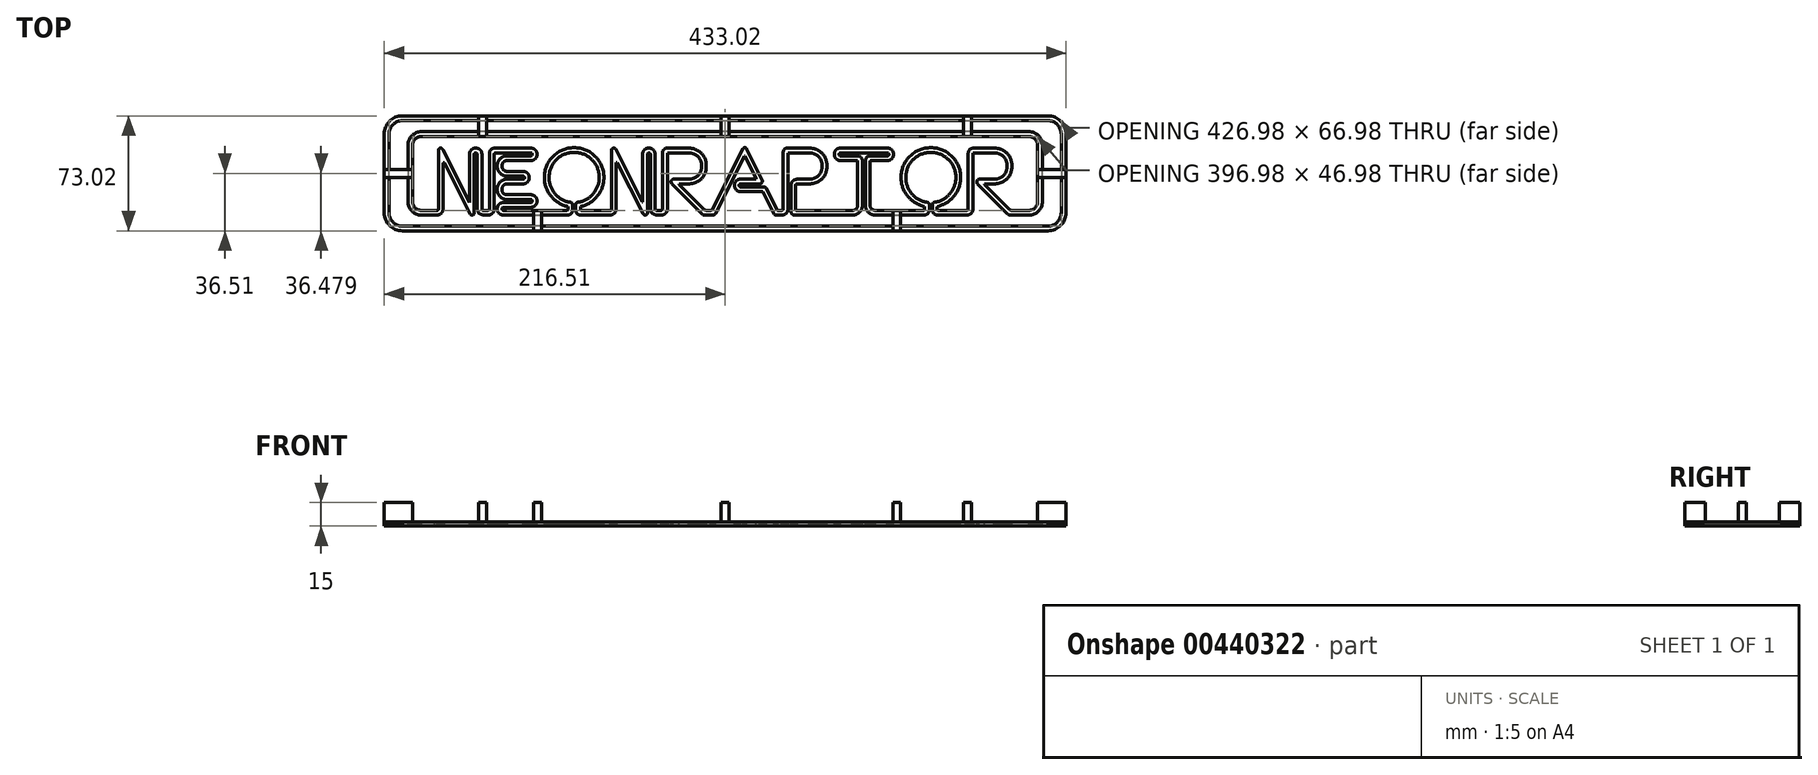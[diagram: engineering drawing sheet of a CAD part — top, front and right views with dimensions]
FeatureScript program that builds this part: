
annotation { "Feature Type Name" : "Feature", "Feature Type Description" : "" }
export const myFeature = defineFeature(function(context is Context, id is Id, definition is map)
    precondition{}
    {
        {
            var Q0;
            Q0=qCreatedBy(makeId("Top.planeOp"),FACE);
            var Q1;
            Q1=qCreatedBy(makeId("Top.planeOp"),FACE);
            var sketch = newSketch(context, id + "F0", { "sketchPlane" : qUnion([Q0, Q1])});
            skLineSegment(sketch, "E0", {"start": v(205, 36.51) * mm, "end": v(-205, 36.51) * mm});
            skLineSegment(sketch, "E1", {"start": v(-205, 36.51) * mm, "end": v(-206.18, 36.45) * mm});
            skLineSegment(sketch, "E2", {"start": v(-206.18, 36.45) * mm, "end": v(-207.32, 36.28) * mm});
            skLineSegment(sketch, "E3", {"start": v(-207.32, 36.28) * mm, "end": v(-208.42, 36) * mm});
            skLineSegment(sketch, "E4", {"start": v(-208.42, 36) * mm, "end": v(-209.48, 35.6) * mm});
            skLineSegment(sketch, "E5", {"start": v(-209.48, 35.6) * mm, "end": v(-210.48, 35.12) * mm});
            skLineSegment(sketch, "E6", {"start": v(-210.48, 35.12) * mm, "end": v(-211.43, 34.54) * mm});
            skLineSegment(sketch, "E7", {"start": v(-211.43, 34.54) * mm, "end": v(-212.32, 33.88) * mm});
            skLineSegment(sketch, "E8", {"start": v(-212.32, 33.88) * mm, "end": v(-213.14, 33.14) * mm});
            skLineSegment(sketch, "E9", {"start": v(-213.14, 33.14) * mm, "end": v(-213.88, 32.32) * mm});
            skLineSegment(sketch, "E10", {"start": v(-213.88, 32.32) * mm, "end": v(-214.54, 31.43) * mm});
            skLineSegment(sketch, "E11", {"start": v(-214.54, 31.43) * mm, "end": v(-215.12, 30.48) * mm});
            skLineSegment(sketch, "E12", {"start": v(-215.12, 30.48) * mm, "end": v(-215.6, 29.48) * mm});
            skLineSegment(sketch, "E13", {"start": v(-215.6, 29.48) * mm, "end": v(-216, 28.42) * mm});
            skLineSegment(sketch, "E14", {"start": v(-216, 28.42) * mm, "end": v(-216.28, 27.32) * mm});
            skLineSegment(sketch, "E15", {"start": v(-216.28, 27.32) * mm, "end": v(-216.45, 26.18) * mm});
            skLineSegment(sketch, "E16", {"start": v(-216.45, 26.18) * mm, "end": v(-216.51, 25) * mm});
            skLineSegment(sketch, "E17", {"start": v(-216.51, 25) * mm, "end": v(-216.51, -25) * mm});
            skLineSegment(sketch, "E18", {"start": v(-216.51, -25) * mm, "end": v(-216.45, -26.18) * mm});
            skLineSegment(sketch, "E19", {"start": v(-216.45, -26.18) * mm, "end": v(-216.28, -27.32) * mm});
            skLineSegment(sketch, "E20", {"start": v(-216.28, -27.32) * mm, "end": v(-216, -28.42) * mm});
            skLineSegment(sketch, "E21", {"start": v(-216, -28.42) * mm, "end": v(-215.6, -29.48) * mm});
            skLineSegment(sketch, "E22", {"start": v(-215.6, -29.48) * mm, "end": v(-215.12, -30.48) * mm});
            skLineSegment(sketch, "E23", {"start": v(-215.12, -30.48) * mm, "end": v(-214.54, -31.43) * mm});
            skLineSegment(sketch, "E24", {"start": v(-214.54, -31.43) * mm, "end": v(-213.88, -32.32) * mm});
            skLineSegment(sketch, "E25", {"start": v(-213.88, -32.32) * mm, "end": v(-213.14, -33.14) * mm});
            skLineSegment(sketch, "E26", {"start": v(-213.14, -33.14) * mm, "end": v(-212.32, -33.88) * mm});
            skLineSegment(sketch, "E27", {"start": v(-212.32, -33.88) * mm, "end": v(-211.43, -34.54) * mm});
            skLineSegment(sketch, "E28", {"start": v(-211.43, -34.54) * mm, "end": v(-210.48, -35.12) * mm});
            skLineSegment(sketch, "E29", {"start": v(-210.48, -35.12) * mm, "end": v(-209.48, -35.6) * mm});
            skLineSegment(sketch, "E30", {"start": v(-209.48, -35.6) * mm, "end": v(-208.42, -36) * mm});
            skLineSegment(sketch, "E31", {"start": v(-208.42, -36) * mm, "end": v(-207.32, -36.28) * mm});
            skLineSegment(sketch, "E32", {"start": v(-207.32, -36.28) * mm, "end": v(-206.18, -36.45) * mm});
            skLineSegment(sketch, "E33", {"start": v(-206.18, -36.45) * mm, "end": v(-205, -36.51) * mm});
            skLineSegment(sketch, "E34", {"start": v(-205, -36.51) * mm, "end": v(205, -36.51) * mm});
            skLineSegment(sketch, "E35", {"start": v(205, -36.51) * mm, "end": v(206.18, -36.45) * mm});
            skLineSegment(sketch, "E36", {"start": v(206.18, -36.45) * mm, "end": v(207.32, -36.28) * mm});
            skLineSegment(sketch, "E37", {"start": v(207.32, -36.28) * mm, "end": v(208.42, -36) * mm});
            skLineSegment(sketch, "E38", {"start": v(208.42, -36) * mm, "end": v(209.48, -35.6) * mm});
            skLineSegment(sketch, "E39", {"start": v(209.48, -35.6) * mm, "end": v(210.48, -35.12) * mm});
            skLineSegment(sketch, "E40", {"start": v(210.48, -35.12) * mm, "end": v(211.43, -34.54) * mm});
            skLineSegment(sketch, "E41", {"start": v(211.43, -34.54) * mm, "end": v(212.32, -33.88) * mm});
            skLineSegment(sketch, "E42", {"start": v(212.32, -33.88) * mm, "end": v(213.14, -33.14) * mm});
            skLineSegment(sketch, "E43", {"start": v(213.14, -33.14) * mm, "end": v(213.88, -32.32) * mm});
            skLineSegment(sketch, "E44", {"start": v(213.88, -32.32) * mm, "end": v(214.54, -31.43) * mm});
            skLineSegment(sketch, "E45", {"start": v(214.54, -31.43) * mm, "end": v(215.12, -30.48) * mm});
            skLineSegment(sketch, "E46", {"start": v(215.12, -30.48) * mm, "end": v(215.6, -29.48) * mm});
            skLineSegment(sketch, "E47", {"start": v(215.6, -29.48) * mm, "end": v(216, -28.42) * mm});
            skLineSegment(sketch, "E48", {"start": v(216, -28.42) * mm, "end": v(216.28, -27.32) * mm});
            skLineSegment(sketch, "E49", {"start": v(216.28, -27.32) * mm, "end": v(216.45, -26.18) * mm});
            skLineSegment(sketch, "E50", {"start": v(216.45, -26.18) * mm, "end": v(216.51, -25) * mm});
            skLineSegment(sketch, "E51", {"start": v(216.51, -25) * mm, "end": v(216.51, 25) * mm});
            skLineSegment(sketch, "E52", {"start": v(216.51, 25) * mm, "end": v(216.45, 26.18) * mm});
            skLineSegment(sketch, "E53", {"start": v(216.45, 26.18) * mm, "end": v(216.28, 27.32) * mm});
            skLineSegment(sketch, "E54", {"start": v(216.28, 27.32) * mm, "end": v(216, 28.42) * mm});
            skLineSegment(sketch, "E55", {"start": v(216, 28.42) * mm, "end": v(215.6, 29.48) * mm});
            skLineSegment(sketch, "E56", {"start": v(215.6, 29.48) * mm, "end": v(215.12, 30.48) * mm});
            skLineSegment(sketch, "E57", {"start": v(215.12, 30.48) * mm, "end": v(214.54, 31.43) * mm});
            skLineSegment(sketch, "E58", {"start": v(214.54, 31.43) * mm, "end": v(213.88, 32.32) * mm});
            skLineSegment(sketch, "E59", {"start": v(213.88, 32.32) * mm, "end": v(213.14, 33.14) * mm});
            skLineSegment(sketch, "E60", {"start": v(213.14, 33.14) * mm, "end": v(212.32, 33.88) * mm});
            skLineSegment(sketch, "E61", {"start": v(212.32, 33.88) * mm, "end": v(211.43, 34.54) * mm});
            skLineSegment(sketch, "E62", {"start": v(211.43, 34.54) * mm, "end": v(210.48, 35.12) * mm});
            skLineSegment(sketch, "E63", {"start": v(210.48, 35.12) * mm, "end": v(209.48, 35.6) * mm});
            skLineSegment(sketch, "E64", {"start": v(209.48, 35.6) * mm, "end": v(208.42, 36) * mm});
            skLineSegment(sketch, "E65", {"start": v(208.42, 36) * mm, "end": v(207.32, 36.28) * mm});
            skLineSegment(sketch, "E66", {"start": v(207.32, 36.28) * mm, "end": v(206.18, 36.45) * mm});
            skLineSegment(sketch, "E67", {"start": v(206.18, 36.45) * mm, "end": v(205, 36.51) * mm});
            skLineSegment(sketch, "E68", {"start": v(213.49, -25) * mm, "end": v(213.45, -25.87) * mm});
            skLineSegment(sketch, "E69", {"start": v(213.45, -25.87) * mm, "end": v(213.32, -26.7) * mm});
            skLineSegment(sketch, "E70", {"start": v(213.32, -26.7) * mm, "end": v(213.1, -27.52) * mm});
            skLineSegment(sketch, "E71", {"start": v(213.1, -27.52) * mm, "end": v(212.82, -28.3) * mm});
            skLineSegment(sketch, "E72", {"start": v(212.82, -28.3) * mm, "end": v(212.46, -29.04) * mm});
            skLineSegment(sketch, "E73", {"start": v(212.46, -29.04) * mm, "end": v(212.04, -29.74) * mm});
            skLineSegment(sketch, "E74", {"start": v(212.04, -29.74) * mm, "end": v(211.55, -30.4) * mm});
            skLineSegment(sketch, "E75", {"start": v(211.55, -30.4) * mm, "end": v(211, -31) * mm});
            skLineSegment(sketch, "E76", {"start": v(211, -31) * mm, "end": v(210.4, -31.55) * mm});
            skLineSegment(sketch, "E77", {"start": v(210.4, -31.55) * mm, "end": v(209.74, -32.04) * mm});
            skLineSegment(sketch, "E78", {"start": v(209.74, -32.04) * mm, "end": v(209.04, -32.46) * mm});
            skLineSegment(sketch, "E79", {"start": v(209.04, -32.46) * mm, "end": v(208.3, -32.82) * mm});
            skLineSegment(sketch, "E80", {"start": v(208.3, -32.82) * mm, "end": v(207.52, -33.1) * mm});
            skLineSegment(sketch, "E81", {"start": v(207.52, -33.1) * mm, "end": v(206.7, -33.32) * mm});
            skLineSegment(sketch, "E82", {"start": v(206.7, -33.32) * mm, "end": v(205.87, -33.45) * mm});
            skLineSegment(sketch, "E83", {"start": v(205.87, -33.45) * mm, "end": v(205, -33.49) * mm});
            skLineSegment(sketch, "E84", {"start": v(205, -33.49) * mm, "end": v(-205, -33.49) * mm});
            skLineSegment(sketch, "E85", {"start": v(-205, -33.49) * mm, "end": v(-205.87, -33.45) * mm});
            skLineSegment(sketch, "E86", {"start": v(-205.87, -33.45) * mm, "end": v(-206.7, -33.32) * mm});
            skLineSegment(sketch, "E87", {"start": v(-206.7, -33.32) * mm, "end": v(-207.52, -33.1) * mm});
            skLineSegment(sketch, "E88", {"start": v(-207.52, -33.1) * mm, "end": v(-208.3, -32.82) * mm});
            skLineSegment(sketch, "E89", {"start": v(-208.3, -32.82) * mm, "end": v(-209.04, -32.46) * mm});
            skLineSegment(sketch, "E90", {"start": v(-209.04, -32.46) * mm, "end": v(-209.74, -32.04) * mm});
            skLineSegment(sketch, "E91", {"start": v(-209.74, -32.04) * mm, "end": v(-210.4, -31.55) * mm});
            skLineSegment(sketch, "E92", {"start": v(-210.4, -31.55) * mm, "end": v(-211, -31) * mm});
            skLineSegment(sketch, "E93", {"start": v(-211, -31) * mm, "end": v(-211.55, -30.4) * mm});
            skLineSegment(sketch, "E94", {"start": v(-211.55, -30.4) * mm, "end": v(-212.04, -29.74) * mm});
            skLineSegment(sketch, "E95", {"start": v(-212.04, -29.74) * mm, "end": v(-212.46, -29.04) * mm});
            skLineSegment(sketch, "E96", {"start": v(-212.46, -29.04) * mm, "end": v(-212.82, -28.3) * mm});
            skLineSegment(sketch, "E97", {"start": v(-212.82, -28.3) * mm, "end": v(-213.1, -27.52) * mm});
            skLineSegment(sketch, "E98", {"start": v(-213.1, -27.52) * mm, "end": v(-213.32, -26.7) * mm});
            skLineSegment(sketch, "E99", {"start": v(-213.32, -26.7) * mm, "end": v(-213.44, -25.87) * mm});
            skLineSegment(sketch, "E100", {"start": v(-213.44, -25.87) * mm, "end": v(-213.49, -25) * mm});
            skLineSegment(sketch, "E101", {"start": v(-213.49, -25) * mm, "end": v(-213.49, 25) * mm});
            skLineSegment(sketch, "E102", {"start": v(-213.49, 25) * mm, "end": v(-213.44, 25.87) * mm});
            skLineSegment(sketch, "E103", {"start": v(-213.44, 25.87) * mm, "end": v(-213.32, 26.7) * mm});
            skLineSegment(sketch, "E104", {"start": v(-213.32, 26.7) * mm, "end": v(-213.1, 27.52) * mm});
            skLineSegment(sketch, "E105", {"start": v(-213.1, 27.52) * mm, "end": v(-212.82, 28.3) * mm});
            skLineSegment(sketch, "E106", {"start": v(-212.82, 28.3) * mm, "end": v(-212.46, 29.04) * mm});
            skLineSegment(sketch, "E107", {"start": v(-212.46, 29.04) * mm, "end": v(-212.04, 29.74) * mm});
            skLineSegment(sketch, "E108", {"start": v(-212.04, 29.74) * mm, "end": v(-211.55, 30.4) * mm});
            skLineSegment(sketch, "E109", {"start": v(-211.55, 30.4) * mm, "end": v(-211, 31) * mm});
            skLineSegment(sketch, "E110", {"start": v(-211, 31) * mm, "end": v(-210.4, 31.55) * mm});
            skLineSegment(sketch, "E111", {"start": v(-210.4, 31.55) * mm, "end": v(-209.74, 32.04) * mm});
            skLineSegment(sketch, "E112", {"start": v(-209.74, 32.04) * mm, "end": v(-209.04, 32.46) * mm});
            skLineSegment(sketch, "E113", {"start": v(-209.04, 32.46) * mm, "end": v(-208.3, 32.82) * mm});
            skLineSegment(sketch, "E114", {"start": v(-208.3, 32.82) * mm, "end": v(-207.52, 33.1) * mm});
            skLineSegment(sketch, "E115", {"start": v(-207.52, 33.1) * mm, "end": v(-206.7, 33.32) * mm});
            skLineSegment(sketch, "E116", {"start": v(-206.7, 33.32) * mm, "end": v(-205.87, 33.44) * mm});
            skLineSegment(sketch, "E117", {"start": v(-205.87, 33.44) * mm, "end": v(-205, 33.49) * mm});
            skLineSegment(sketch, "E118", {"start": v(-205, 33.49) * mm, "end": v(205, 33.49) * mm});
            skLineSegment(sketch, "E119", {"start": v(205, 33.49) * mm, "end": v(205.87, 33.44) * mm});
            skLineSegment(sketch, "E120", {"start": v(205.87, 33.44) * mm, "end": v(206.7, 33.32) * mm});
            skLineSegment(sketch, "E121", {"start": v(206.7, 33.32) * mm, "end": v(207.52, 33.1) * mm});
            skLineSegment(sketch, "E122", {"start": v(207.52, 33.1) * mm, "end": v(208.3, 32.82) * mm});
            skLineSegment(sketch, "E123", {"start": v(208.3, 32.82) * mm, "end": v(209.04, 32.46) * mm});
            skLineSegment(sketch, "E124", {"start": v(209.04, 32.46) * mm, "end": v(209.74, 32.04) * mm});
            skLineSegment(sketch, "E125", {"start": v(209.74, 32.04) * mm, "end": v(210.4, 31.55) * mm});
            skLineSegment(sketch, "E126", {"start": v(210.4, 31.55) * mm, "end": v(211, 31) * mm});
            skLineSegment(sketch, "E127", {"start": v(211, 31) * mm, "end": v(211.55, 30.4) * mm});
            skLineSegment(sketch, "E128", {"start": v(211.55, 30.4) * mm, "end": v(212.04, 29.74) * mm});
            skLineSegment(sketch, "E129", {"start": v(212.04, 29.74) * mm, "end": v(212.46, 29.04) * mm});
            skLineSegment(sketch, "E130", {"start": v(212.46, 29.04) * mm, "end": v(212.82, 28.3) * mm});
            skLineSegment(sketch, "E131", {"start": v(212.82, 28.3) * mm, "end": v(213.1, 27.52) * mm});
            skLineSegment(sketch, "E132", {"start": v(213.1, 27.52) * mm, "end": v(213.32, 26.7) * mm});
            skLineSegment(sketch, "E133", {"start": v(213.32, 26.7) * mm, "end": v(213.45, 25.87) * mm});
            skLineSegment(sketch, "E134", {"start": v(213.45, 25.87) * mm, "end": v(213.49, 25) * mm});
            skLineSegment(sketch, "E135", {"start": v(213.49, 25) * mm, "end": v(213.49, -25) * mm});
            skLineSegment(sketch, "E136", {"start": v(192.86, 26.48) * mm, "end": v(-192.86, 26.48) * mm});
            skLineSegment(sketch, "E137", {"start": v(-192.86, 26.48) * mm, "end": v(-193.74, 26.44) * mm});
            skLineSegment(sketch, "E138", {"start": v(-193.74, 26.44) * mm, "end": v(-194.6, 26.3) * mm});
            skLineSegment(sketch, "E139", {"start": v(-194.6, 26.3) * mm, "end": v(-195.43, 26.1) * mm});
            skLineSegment(sketch, "E140", {"start": v(-195.43, 26.1) * mm, "end": v(-196.22, 25.8) * mm});
            skLineSegment(sketch, "E141", {"start": v(-196.22, 25.8) * mm, "end": v(-196.98, 25.43) * mm});
            skLineSegment(sketch, "E142", {"start": v(-196.98, 25.43) * mm, "end": v(-197.7, 25) * mm});
            skLineSegment(sketch, "E143", {"start": v(-197.7, 25) * mm, "end": v(-198.36, 24.5) * mm});
            skLineSegment(sketch, "E144", {"start": v(-198.36, 24.5) * mm, "end": v(-198.97, 23.94) * mm});
            skLineSegment(sketch, "E145", {"start": v(-198.97, 23.94) * mm, "end": v(-199.53, 23.33) * mm});
            skLineSegment(sketch, "E146", {"start": v(-199.53, 23.33) * mm, "end": v(-200.03, 22.66) * mm});
            skLineSegment(sketch, "E147", {"start": v(-200.03, 22.66) * mm, "end": v(-200.46, 21.95) * mm});
            skLineSegment(sketch, "E148", {"start": v(-200.46, 21.95) * mm, "end": v(-200.83, 21.2) * mm});
            skLineSegment(sketch, "E149", {"start": v(-200.83, 21.2) * mm, "end": v(-201.12, 20.4) * mm});
            skLineSegment(sketch, "E150", {"start": v(-201.12, 20.4) * mm, "end": v(-201.33, 19.57) * mm});
            skLineSegment(sketch, "E151", {"start": v(-201.33, 19.57) * mm, "end": v(-201.47, 18.7) * mm});
            skLineSegment(sketch, "E152", {"start": v(-201.47, 18.7) * mm, "end": v(-201.51, 17.82) * mm});
            skLineSegment(sketch, "E153", {"start": v(-201.51, 17.82) * mm, "end": v(-201.51, -17.89) * mm});
            skLineSegment(sketch, "E154", {"start": v(-201.51, -17.89) * mm, "end": v(-201.47, -18.77) * mm});
            skLineSegment(sketch, "E155", {"start": v(-201.47, -18.77) * mm, "end": v(-201.33, -19.63) * mm});
            skLineSegment(sketch, "E156", {"start": v(-201.33, -19.63) * mm, "end": v(-201.12, -20.46) * mm});
            skLineSegment(sketch, "E157", {"start": v(-201.12, -20.46) * mm, "end": v(-200.83, -21.25) * mm});
            skLineSegment(sketch, "E158", {"start": v(-200.83, -21.25) * mm, "end": v(-200.46, -22) * mm});
            skLineSegment(sketch, "E159", {"start": v(-200.46, -22) * mm, "end": v(-200.03, -22.72) * mm});
            skLineSegment(sketch, "E160", {"start": v(-200.03, -22.72) * mm, "end": v(-199.53, -23.39) * mm});
            skLineSegment(sketch, "E161", {"start": v(-199.53, -23.39) * mm, "end": v(-198.97, -24) * mm});
            skLineSegment(sketch, "E162", {"start": v(-198.97, -24) * mm, "end": v(-198.36, -24.56) * mm});
            skLineSegment(sketch, "E163", {"start": v(-198.36, -24.56) * mm, "end": v(-197.7, -25.06) * mm});
            skLineSegment(sketch, "E164", {"start": v(-197.7, -25.06) * mm, "end": v(-196.98, -25.5) * mm});
            skLineSegment(sketch, "E165", {"start": v(-196.98, -25.5) * mm, "end": v(-196.22, -25.86) * mm});
            skLineSegment(sketch, "E166", {"start": v(-196.22, -25.86) * mm, "end": v(-195.43, -26.15) * mm});
            skLineSegment(sketch, "E167", {"start": v(-195.43, -26.15) * mm, "end": v(-194.6, -26.37) * mm});
            skLineSegment(sketch, "E168", {"start": v(-194.6, -26.37) * mm, "end": v(-193.74, -26.5) * mm});
            skLineSegment(sketch, "E169", {"start": v(-193.74, -26.5) * mm, "end": v(-192.86, -26.54) * mm});
            skLineSegment(sketch, "E170", {"start": v(-192.86, -26.54) * mm, "end": v(-184.5, -26.54) * mm});
            skLineSegment(sketch, "E171", {"start": v(-184.5, -26.54) * mm, "end": v(-184.4, -26.44) * mm});
            skLineSegment(sketch, "E172", {"start": v(-184.4, -26.44) * mm, "end": v(-184.4, -26.44) * mm});
            skLineSegment(sketch, "E173", {"start": v(-184.4, -26.44) * mm, "end": v(-183.06, -26.44) * mm});
            skLineSegment(sketch, "E174", {"start": v(-183.06, -26.44) * mm, "end": v(-182.85, -26.43) * mm});
            skLineSegment(sketch, "E175", {"start": v(-182.85, -26.43) * mm, "end": v(-182.64, -26.42) * mm});
            skLineSegment(sketch, "E176", {"start": v(-182.64, -26.42) * mm, "end": v(-182.44, -26.4) * mm});
            skLineSegment(sketch, "E177", {"start": v(-182.44, -26.4) * mm, "end": v(-182.24, -26.37) * mm});
            skLineSegment(sketch, "E178", {"start": v(-182.24, -26.37) * mm, "end": v(-182.04, -26.33) * mm});
            skLineSegment(sketch, "E179", {"start": v(-182.04, -26.33) * mm, "end": v(-181.85, -26.28) * mm});
            skLineSegment(sketch, "E180", {"start": v(-181.85, -26.28) * mm, "end": v(-181.67, -26.22) * mm});
            skLineSegment(sketch, "E181", {"start": v(-181.67, -26.22) * mm, "end": v(-181.5, -26.16) * mm});
            skLineSegment(sketch, "E182", {"start": v(-181.5, -26.16) * mm, "end": v(-181.32, -26.08) * mm});
            skLineSegment(sketch, "E183", {"start": v(-181.32, -26.08) * mm, "end": v(-181.15, -26) * mm});
            skLineSegment(sketch, "E184", {"start": v(-181.15, -26) * mm, "end": v(-180.98, -25.9) * mm});
            skLineSegment(sketch, "E185", {"start": v(-180.98, -25.9) * mm, "end": v(-180.82, -25.8) * mm});
            skLineSegment(sketch, "E186", {"start": v(-180.82, -25.8) * mm, "end": v(-180.67, -25.7) * mm});
            skLineSegment(sketch, "E187", {"start": v(-180.67, -25.7) * mm, "end": v(-180.52, -25.58) * mm});
            skLineSegment(sketch, "E188", {"start": v(-180.52, -25.58) * mm, "end": v(-180.38, -25.46) * mm});
            skLineSegment(sketch, "E189", {"start": v(-180.38, -25.46) * mm, "end": v(-180.24, -25.32) * mm});
            skLineSegment(sketch, "E190", {"start": v(-180.24, -25.32) * mm, "end": v(-180.1, -25.18) * mm});
            skLineSegment(sketch, "E191", {"start": v(-180.1, -25.18) * mm, "end": v(-179.99, -25.03) * mm});
            skLineSegment(sketch, "E192", {"start": v(-179.99, -25.03) * mm, "end": v(-179.87, -24.88) * mm});
            skLineSegment(sketch, "E193", {"start": v(-179.87, -24.88) * mm, "end": v(-179.77, -24.73) * mm});
            skLineSegment(sketch, "E194", {"start": v(-179.77, -24.73) * mm, "end": v(-179.67, -24.56) * mm});
            skLineSegment(sketch, "E195", {"start": v(-179.67, -24.56) * mm, "end": v(-179.58, -24.4) * mm});
            skLineSegment(sketch, "E196", {"start": v(-179.58, -24.4) * mm, "end": v(-179.5, -24.23) * mm});
            skLineSegment(sketch, "E197", {"start": v(-179.5, -24.23) * mm, "end": v(-179.43, -24.05) * mm});
            skLineSegment(sketch, "E198", {"start": v(-179.43, -24.05) * mm, "end": v(-179.36, -23.87) * mm});
            skLineSegment(sketch, "E199", {"start": v(-179.36, -23.87) * mm, "end": v(-179.3, -23.68) * mm});
            skLineSegment(sketch, "E200", {"start": v(-179.3, -23.68) * mm, "end": v(-179.26, -23.5) * mm});
            skLineSegment(sketch, "E201", {"start": v(-179.26, -23.5) * mm, "end": v(-179.22, -23.3) * mm});
            skLineSegment(sketch, "E202", {"start": v(-179.22, -23.3) * mm, "end": v(-179.2, -23.1) * mm});
            skLineSegment(sketch, "E203", {"start": v(-179.2, -23.1) * mm, "end": v(-179.17, -22.9) * mm});
            skLineSegment(sketch, "E204", {"start": v(-179.17, -22.9) * mm, "end": v(-179.16, -22.69) * mm});
            skLineSegment(sketch, "E205", {"start": v(-179.16, -22.69) * mm, "end": v(-179.15, -22.47) * mm});
            skLineSegment(sketch, "E206", {"start": v(-179.15, -22.47) * mm, "end": v(-179.15, 6.31) * mm});
            skLineSegment(sketch, "E207", {"start": v(-179.15, 6.31) * mm, "end": v(-179.15, 6.36) * mm});
            skLineSegment(sketch, "E208", {"start": v(-179.15, 6.36) * mm, "end": v(-179.14, 6.41) * mm});
            skLineSegment(sketch, "E209", {"start": v(-179.14, 6.41) * mm, "end": v(-179.13, 6.46) * mm});
            skLineSegment(sketch, "E210", {"start": v(-179.13, 6.46) * mm, "end": v(-179.11, 6.5) * mm});
            skLineSegment(sketch, "E211", {"start": v(-179.11, 6.5) * mm, "end": v(-179.1, 6.54) * mm});
            skLineSegment(sketch, "E212", {"start": v(-179.1, 6.54) * mm, "end": v(-179.07, 6.58) * mm});
            skLineSegment(sketch, "E213", {"start": v(-179.07, 6.58) * mm, "end": v(-179.04, 6.6) * mm});
            skLineSegment(sketch, "E214", {"start": v(-179.04, 6.6) * mm, "end": v(-179.01, 6.64) * mm});
            skLineSegment(sketch, "E215", {"start": v(-179.01, 6.64) * mm, "end": v(-178.98, 6.67) * mm});
            skLineSegment(sketch, "E216", {"start": v(-178.98, 6.67) * mm, "end": v(-178.94, 6.69) * mm});
            skLineSegment(sketch, "E217", {"start": v(-178.94, 6.69) * mm, "end": v(-178.9, 6.7) * mm});
            skLineSegment(sketch, "E218", {"start": v(-178.9, 6.7) * mm, "end": v(-178.87, 6.72) * mm});
            skLineSegment(sketch, "E219", {"start": v(-178.87, 6.72) * mm, "end": v(-178.83, 6.74) * mm});
            skLineSegment(sketch, "E220", {"start": v(-178.83, 6.74) * mm, "end": v(-178.79, 6.75) * mm});
            skLineSegment(sketch, "E221", {"start": v(-178.79, 6.75) * mm, "end": v(-178.75, 6.75) * mm});
            skLineSegment(sketch, "E222", {"start": v(-178.75, 6.75) * mm, "end": v(-178.7, 6.75) * mm});
            skLineSegment(sketch, "E223", {"start": v(-178.7, 6.75) * mm, "end": v(-178.67, 6.75) * mm});
            skLineSegment(sketch, "E224", {"start": v(-178.67, 6.75) * mm, "end": v(-178.64, 6.75) * mm});
            skLineSegment(sketch, "E225", {"start": v(-178.64, 6.75) * mm, "end": v(-178.61, 6.74) * mm});
            skLineSegment(sketch, "E226", {"start": v(-178.61, 6.74) * mm, "end": v(-178.58, 6.74) * mm});
            skLineSegment(sketch, "E227", {"start": v(-178.58, 6.74) * mm, "end": v(-178.56, 6.73) * mm});
            skLineSegment(sketch, "E228", {"start": v(-178.56, 6.73) * mm, "end": v(-178.53, 6.72) * mm});
            skLineSegment(sketch, "E229", {"start": v(-178.53, 6.72) * mm, "end": v(-178.5, 6.7) * mm});
            skLineSegment(sketch, "E230", {"start": v(-178.5, 6.7) * mm, "end": v(-178.48, 6.69) * mm});
            skLineSegment(sketch, "E231", {"start": v(-178.48, 6.69) * mm, "end": v(-178.45, 6.67) * mm});
            skLineSegment(sketch, "E232", {"start": v(-178.45, 6.67) * mm, "end": v(-178.43, 6.65) * mm});
            skLineSegment(sketch, "E233", {"start": v(-178.43, 6.65) * mm, "end": v(-178.4, 6.63) * mm});
            skLineSegment(sketch, "E234", {"start": v(-178.4, 6.63) * mm, "end": v(-178.39, 6.61) * mm});
            skLineSegment(sketch, "E235", {"start": v(-178.39, 6.61) * mm, "end": v(-178.37, 6.59) * mm});
            skLineSegment(sketch, "E236", {"start": v(-178.37, 6.59) * mm, "end": v(-178.35, 6.56) * mm});
            skLineSegment(sketch, "E237", {"start": v(-178.35, 6.56) * mm, "end": v(-178.33, 6.54) * mm});
            skLineSegment(sketch, "E238", {"start": v(-178.33, 6.54) * mm, "end": v(-178.32, 6.5) * mm});
            skLineSegment(sketch, "E239", {"start": v(-178.32, 6.5) * mm, "end": v(-162.07, -25.76) * mm});
            skLineSegment(sketch, "E240", {"start": v(-162.07, -25.76) * mm, "end": v(-162.03, -25.83) * mm});
            skLineSegment(sketch, "E241", {"start": v(-162.03, -25.83) * mm, "end": v(-161.98, -25.9) * mm});
            skLineSegment(sketch, "E242", {"start": v(-161.98, -25.9) * mm, "end": v(-161.92, -25.98) * mm});
            skLineSegment(sketch, "E243", {"start": v(-161.92, -25.98) * mm, "end": v(-161.86, -26.04) * mm});
            skLineSegment(sketch, "E244", {"start": v(-161.86, -26.04) * mm, "end": v(-161.8, -26.1) * mm});
            skLineSegment(sketch, "E245", {"start": v(-161.8, -26.1) * mm, "end": v(-161.72, -26.17) * mm});
            skLineSegment(sketch, "E246", {"start": v(-161.72, -26.17) * mm, "end": v(-161.65, -26.22) * mm});
            skLineSegment(sketch, "E247", {"start": v(-161.65, -26.22) * mm, "end": v(-161.57, -26.27) * mm});
            skLineSegment(sketch, "E248", {"start": v(-161.57, -26.27) * mm, "end": v(-161.49, -26.32) * mm});
            skLineSegment(sketch, "E249", {"start": v(-161.49, -26.32) * mm, "end": v(-161.4, -26.36) * mm});
            skLineSegment(sketch, "E250", {"start": v(-161.4, -26.36) * mm, "end": v(-161.32, -26.4) * mm});
            skLineSegment(sketch, "E251", {"start": v(-161.32, -26.4) * mm, "end": v(-161.23, -26.43) * mm});
            skLineSegment(sketch, "E252", {"start": v(-161.23, -26.43) * mm, "end": v(-161.14, -26.46) * mm});
            skLineSegment(sketch, "E253", {"start": v(-161.14, -26.46) * mm, "end": v(-161.05, -26.47) * mm});
            skLineSegment(sketch, "E254", {"start": v(-161.05, -26.47) * mm, "end": v(-160.97, -26.48) * mm});
            skLineSegment(sketch, "E255", {"start": v(-160.97, -26.48) * mm, "end": v(-160.88, -26.49) * mm});
            skLineSegment(sketch, "E256", {"start": v(-160.88, -26.49) * mm, "end": v(-160.61, -26.49) * mm});
            skLineSegment(sketch, "E257", {"start": v(-160.61, -26.49) * mm, "end": v(-160.49, -26.48) * mm});
            skLineSegment(sketch, "E258", {"start": v(-160.49, -26.48) * mm, "end": v(-160.36, -26.46) * mm});
            skLineSegment(sketch, "E259", {"start": v(-160.36, -26.46) * mm, "end": v(-160.24, -26.43) * mm});
            skLineSegment(sketch, "E260", {"start": v(-160.24, -26.43) * mm, "end": v(-160.13, -26.4) * mm});
            skLineSegment(sketch, "E261", {"start": v(-160.13, -26.4) * mm, "end": v(-160.02, -26.34) * mm});
            skLineSegment(sketch, "E262", {"start": v(-160.02, -26.34) * mm, "end": v(-159.91, -26.27) * mm});
            skLineSegment(sketch, "E263", {"start": v(-159.91, -26.27) * mm, "end": v(-159.82, -26.2) * mm});
            skLineSegment(sketch, "E264", {"start": v(-159.82, -26.2) * mm, "end": v(-159.73, -26.12) * mm});
            skLineSegment(sketch, "E265", {"start": v(-159.73, -26.12) * mm, "end": v(-159.65, -26.03) * mm});
            skLineSegment(sketch, "E266", {"start": v(-159.65, -26.03) * mm, "end": v(-159.58, -25.94) * mm});
            skLineSegment(sketch, "E267", {"start": v(-159.58, -25.94) * mm, "end": v(-159.51, -25.83) * mm});
            skLineSegment(sketch, "E268", {"start": v(-159.51, -25.83) * mm, "end": v(-159.46, -25.72) * mm});
            skLineSegment(sketch, "E269", {"start": v(-159.46, -25.72) * mm, "end": v(-159.42, -25.61) * mm});
            skLineSegment(sketch, "E270", {"start": v(-159.42, -25.61) * mm, "end": v(-159.39, -25.5) * mm});
            skLineSegment(sketch, "E271", {"start": v(-159.39, -25.5) * mm, "end": v(-159.37, -25.37) * mm});
            skLineSegment(sketch, "E272", {"start": v(-159.37, -25.37) * mm, "end": v(-159.36, -25.24) * mm});
            skLineSegment(sketch, "E273", {"start": v(-159.36, -25.24) * mm, "end": v(-159.36, 11.98) * mm});
            skLineSegment(sketch, "E274", {"start": v(-159.36, 11.98) * mm, "end": v(-159.36, 12.1) * mm});
            skLineSegment(sketch, "E275", {"start": v(-159.36, 12.1) * mm, "end": v(-159.35, 12.22) * mm});
            skLineSegment(sketch, "E276", {"start": v(-159.35, 12.22) * mm, "end": v(-159.33, 12.33) * mm});
            skLineSegment(sketch, "E277", {"start": v(-159.33, 12.33) * mm, "end": v(-159.3, 12.43) * mm});
            skLineSegment(sketch, "E278", {"start": v(-159.3, 12.43) * mm, "end": v(-159.27, 12.52) * mm});
            skLineSegment(sketch, "E279", {"start": v(-159.27, 12.52) * mm, "end": v(-159.24, 12.6) * mm});
            skLineSegment(sketch, "E280", {"start": v(-159.24, 12.6) * mm, "end": v(-159.19, 12.67) * mm});
            skLineSegment(sketch, "E281", {"start": v(-159.19, 12.67) * mm, "end": v(-159.14, 12.74) * mm});
            skLineSegment(sketch, "E282", {"start": v(-159.14, 12.74) * mm, "end": v(-159.07, 12.8) * mm});
            skLineSegment(sketch, "E283", {"start": v(-159.07, 12.8) * mm, "end": v(-159, 12.85) * mm});
            skLineSegment(sketch, "E284", {"start": v(-159, 12.85) * mm, "end": v(-158.93, 12.9) * mm});
            skLineSegment(sketch, "E285", {"start": v(-158.93, 12.9) * mm, "end": v(-158.84, 12.93) * mm});
            skLineSegment(sketch, "E286", {"start": v(-158.84, 12.93) * mm, "end": v(-158.75, 12.95) * mm});
            skLineSegment(sketch, "E287", {"start": v(-158.75, 12.95) * mm, "end": v(-158.65, 12.97) * mm});
            skLineSegment(sketch, "E288", {"start": v(-158.65, 12.97) * mm, "end": v(-158.55, 12.98) * mm});
            skLineSegment(sketch, "E289", {"start": v(-158.55, 12.98) * mm, "end": v(-158.43, 12.99) * mm});
            skLineSegment(sketch, "E290", {"start": v(-158.43, 12.99) * mm, "end": v(-158.3, 12.98) * mm});
            skLineSegment(sketch, "E291", {"start": v(-158.3, 12.98) * mm, "end": v(-158.2, 12.97) * mm});
            skLineSegment(sketch, "E292", {"start": v(-158.2, 12.97) * mm, "end": v(-158.09, 12.95) * mm});
            skLineSegment(sketch, "E293", {"start": v(-158.09, 12.95) * mm, "end": v(-158, 12.93) * mm});
            skLineSegment(sketch, "E294", {"start": v(-158, 12.93) * mm, "end": v(-157.9, 12.9) * mm});
            skLineSegment(sketch, "E295", {"start": v(-157.9, 12.9) * mm, "end": v(-157.82, 12.85) * mm});
            skLineSegment(sketch, "E296", {"start": v(-157.82, 12.85) * mm, "end": v(-157.75, 12.8) * mm});
            skLineSegment(sketch, "E297", {"start": v(-157.75, 12.8) * mm, "end": v(-157.69, 12.74) * mm});
            skLineSegment(sketch, "E298", {"start": v(-157.69, 12.74) * mm, "end": v(-157.63, 12.67) * mm});
            skLineSegment(sketch, "E299", {"start": v(-157.63, 12.67) * mm, "end": v(-157.58, 12.6) * mm});
            skLineSegment(sketch, "E300", {"start": v(-157.58, 12.6) * mm, "end": v(-157.54, 12.52) * mm});
            skLineSegment(sketch, "E301", {"start": v(-157.54, 12.52) * mm, "end": v(-157.5, 12.43) * mm});
            skLineSegment(sketch, "E302", {"start": v(-157.5, 12.43) * mm, "end": v(-157.48, 12.33) * mm});
            skLineSegment(sketch, "E303", {"start": v(-157.48, 12.33) * mm, "end": v(-157.46, 12.22) * mm});
            skLineSegment(sketch, "E304", {"start": v(-157.46, 12.22) * mm, "end": v(-157.45, 12.1) * mm});
            skLineSegment(sketch, "E305", {"start": v(-157.45, 12.1) * mm, "end": v(-157.45, 11.98) * mm});
            skLineSegment(sketch, "E306", {"start": v(-157.45, 11.98) * mm, "end": v(-157.45, -22.43) * mm});
            skLineSegment(sketch, "E307", {"start": v(-157.45, -22.43) * mm, "end": v(-157.43, -22.85) * mm});
            skLineSegment(sketch, "E308", {"start": v(-157.43, -22.85) * mm, "end": v(-157.38, -23.26) * mm});
            skLineSegment(sketch, "E309", {"start": v(-157.38, -23.26) * mm, "end": v(-157.3, -23.63) * mm});
            skLineSegment(sketch, "E310", {"start": v(-157.3, -23.63) * mm, "end": v(-157.2, -24) * mm});
            skLineSegment(sketch, "E311", {"start": v(-157.2, -24) * mm, "end": v(-157.06, -24.32) * mm});
            skLineSegment(sketch, "E312", {"start": v(-157.06, -24.32) * mm, "end": v(-156.9, -24.63) * mm});
            skLineSegment(sketch, "E313", {"start": v(-156.9, -24.63) * mm, "end": v(-156.7, -24.91) * mm});
            skLineSegment(sketch, "E314", {"start": v(-156.7, -24.91) * mm, "end": v(-156.46, -25.17) * mm});
            skLineSegment(sketch, "E315", {"start": v(-156.46, -25.17) * mm, "end": v(-156.2, -25.4) * mm});
            skLineSegment(sketch, "E316", {"start": v(-156.2, -25.4) * mm, "end": v(-155.91, -25.62) * mm});
            skLineSegment(sketch, "E317", {"start": v(-155.91, -25.62) * mm, "end": v(-155.6, -25.8) * mm});
            skLineSegment(sketch, "E318", {"start": v(-155.6, -25.8) * mm, "end": v(-155.24, -25.97) * mm});
            skLineSegment(sketch, "E319", {"start": v(-155.24, -25.97) * mm, "end": v(-154.86, -26.11) * mm});
            skLineSegment(sketch, "E320", {"start": v(-154.86, -26.11) * mm, "end": v(-154.45, -26.23) * mm});
            skLineSegment(sketch, "E321", {"start": v(-154.45, -26.23) * mm, "end": v(-154, -26.32) * mm});
            skLineSegment(sketch, "E322", {"start": v(-154, -26.32) * mm, "end": v(-153.53, -26.38) * mm});
            skLineSegment(sketch, "E323", {"start": v(-153.53, -26.38) * mm, "end": v(-150.63, -26.49) * mm});
            skLineSegment(sketch, "E324", {"start": v(-150.63, -26.49) * mm, "end": v(-150.41, -26.48) * mm});
            skLineSegment(sketch, "E325", {"start": v(-150.41, -26.48) * mm, "end": v(-150.2, -26.47) * mm});
            skLineSegment(sketch, "E326", {"start": v(-150.2, -26.47) * mm, "end": v(-150, -26.45) * mm});
            skLineSegment(sketch, "E327", {"start": v(-150, -26.45) * mm, "end": v(-149.8, -26.42) * mm});
            skLineSegment(sketch, "E328", {"start": v(-149.8, -26.42) * mm, "end": v(-149.6, -26.38) * mm});
            skLineSegment(sketch, "E329", {"start": v(-149.6, -26.38) * mm, "end": v(-149.41, -26.33) * mm});
            skLineSegment(sketch, "E330", {"start": v(-149.41, -26.33) * mm, "end": v(-149.23, -26.27) * mm});
            skLineSegment(sketch, "E331", {"start": v(-149.23, -26.27) * mm, "end": v(-149.05, -26.2) * mm});
            skLineSegment(sketch, "E332", {"start": v(-149.05, -26.2) * mm, "end": v(-148.87, -26.13) * mm});
            skLineSegment(sketch, "E333", {"start": v(-148.87, -26.13) * mm, "end": v(-148.7, -26.05) * mm});
            skLineSegment(sketch, "E334", {"start": v(-148.7, -26.05) * mm, "end": v(-148.53, -25.96) * mm});
            skLineSegment(sketch, "E335", {"start": v(-148.53, -25.96) * mm, "end": v(-148.37, -25.86) * mm});
            skLineSegment(sketch, "E336", {"start": v(-148.37, -25.86) * mm, "end": v(-148.22, -25.75) * mm});
            skLineSegment(sketch, "E337", {"start": v(-148.22, -25.75) * mm, "end": v(-148.06, -25.63) * mm});
            skLineSegment(sketch, "E338", {"start": v(-148.06, -25.63) * mm, "end": v(-147.92, -25.5) * mm});
            skLineSegment(sketch, "E339", {"start": v(-147.92, -25.5) * mm, "end": v(-147.78, -25.37) * mm});
            skLineSegment(sketch, "E340", {"start": v(-147.78, -25.37) * mm, "end": v(-147.64, -25.23) * mm});
            skLineSegment(sketch, "E341", {"start": v(-147.64, -25.23) * mm, "end": v(-147.52, -25.09) * mm});
            skLineSegment(sketch, "E342", {"start": v(-147.52, -25.09) * mm, "end": v(-147.4, -24.94) * mm});
            skLineSegment(sketch, "E343", {"start": v(-147.4, -24.94) * mm, "end": v(-147.3, -24.78) * mm});
            skLineSegment(sketch, "E344", {"start": v(-147.3, -24.78) * mm, "end": v(-147.2, -24.62) * mm});
            skLineSegment(sketch, "E345", {"start": v(-147.2, -24.62) * mm, "end": v(-147.1, -24.45) * mm});
            skLineSegment(sketch, "E346", {"start": v(-147.1, -24.45) * mm, "end": v(-147.02, -24.28) * mm});
            skLineSegment(sketch, "E347", {"start": v(-147.02, -24.28) * mm, "end": v(-146.94, -24.1) * mm});
            skLineSegment(sketch, "E348", {"start": v(-146.94, -24.1) * mm, "end": v(-146.88, -23.92) * mm});
            skLineSegment(sketch, "E349", {"start": v(-146.88, -23.92) * mm, "end": v(-146.82, -23.74) * mm});
            skLineSegment(sketch, "E350", {"start": v(-146.82, -23.74) * mm, "end": v(-146.77, -23.55) * mm});
            skLineSegment(sketch, "E351", {"start": v(-146.77, -23.55) * mm, "end": v(-146.73, -23.35) * mm});
            skLineSegment(sketch, "E352", {"start": v(-146.73, -23.35) * mm, "end": v(-146.7, -23.15) * mm});
            skLineSegment(sketch, "E353", {"start": v(-146.7, -23.15) * mm, "end": v(-146.68, -22.95) * mm});
            skLineSegment(sketch, "E354", {"start": v(-146.68, -22.95) * mm, "end": v(-146.67, -22.74) * mm});
            skLineSegment(sketch, "E355", {"start": v(-146.67, -22.74) * mm, "end": v(-146.66, -22.53) * mm});
            skLineSegment(sketch, "E356", {"start": v(-146.66, -22.53) * mm, "end": v(-146.66, 12.15) * mm});
            skLineSegment(sketch, "E357", {"start": v(-146.66, 12.15) * mm, "end": v(-146.66, 12.24) * mm});
            skLineSegment(sketch, "E358", {"start": v(-146.66, 12.24) * mm, "end": v(-146.65, 12.33) * mm});
            skLineSegment(sketch, "E359", {"start": v(-146.65, 12.33) * mm, "end": v(-146.62, 12.42) * mm});
            skLineSegment(sketch, "E360", {"start": v(-146.62, 12.42) * mm, "end": v(-146.6, 12.5) * mm});
            skLineSegment(sketch, "E361", {"start": v(-146.6, 12.5) * mm, "end": v(-146.56, 12.58) * mm});
            skLineSegment(sketch, "E362", {"start": v(-146.56, 12.58) * mm, "end": v(-146.51, 12.65) * mm});
            skLineSegment(sketch, "E363", {"start": v(-146.51, 12.65) * mm, "end": v(-146.46, 12.72) * mm});
            skLineSegment(sketch, "E364", {"start": v(-146.46, 12.72) * mm, "end": v(-146.4, 12.78) * mm});
            skLineSegment(sketch, "E365", {"start": v(-146.4, 12.78) * mm, "end": v(-146.34, 12.84) * mm});
            skLineSegment(sketch, "E366", {"start": v(-146.34, 12.84) * mm, "end": v(-146.27, 12.89) * mm});
            skLineSegment(sketch, "E367", {"start": v(-146.27, 12.89) * mm, "end": v(-146.2, 12.93) * mm});
            skLineSegment(sketch, "E368", {"start": v(-146.2, 12.93) * mm, "end": v(-146.12, 12.97) * mm});
            skLineSegment(sketch, "E369", {"start": v(-146.12, 12.97) * mm, "end": v(-146.04, 13) * mm});
            skLineSegment(sketch, "E370", {"start": v(-146.04, 13) * mm, "end": v(-145.96, 13.02) * mm});
            skLineSegment(sketch, "E371", {"start": v(-145.96, 13.02) * mm, "end": v(-145.87, 13.04) * mm});
            skLineSegment(sketch, "E372", {"start": v(-145.87, 13.04) * mm, "end": v(-145.78, 13.04) * mm});
            skLineSegment(sketch, "E373", {"start": v(-145.78, 13.04) * mm, "end": v(-123.48, 13.04) * mm});
            skLineSegment(sketch, "E374", {"start": v(-123.48, 13.04) * mm, "end": v(-123.35, 13.04) * mm});
            skLineSegment(sketch, "E375", {"start": v(-123.35, 13.04) * mm, "end": v(-123.24, 13.03) * mm});
            skLineSegment(sketch, "E376", {"start": v(-123.24, 13.03) * mm, "end": v(-123.13, 13) * mm});
            skLineSegment(sketch, "E377", {"start": v(-123.13, 13) * mm, "end": v(-123.03, 12.98) * mm});
            skLineSegment(sketch, "E378", {"start": v(-123.03, 12.98) * mm, "end": v(-122.94, 12.95) * mm});
            skLineSegment(sketch, "E379", {"start": v(-122.94, 12.95) * mm, "end": v(-122.86, 12.9) * mm});
            skLineSegment(sketch, "E380", {"start": v(-122.86, 12.9) * mm, "end": v(-122.78, 12.86) * mm});
            skLineSegment(sketch, "E381", {"start": v(-122.78, 12.86) * mm, "end": v(-122.72, 12.8) * mm});
            skLineSegment(sketch, "E382", {"start": v(-122.72, 12.8) * mm, "end": v(-122.66, 12.74) * mm});
            skLineSegment(sketch, "E383", {"start": v(-122.66, 12.74) * mm, "end": v(-122.6, 12.67) * mm});
            skLineSegment(sketch, "E384", {"start": v(-122.6, 12.67) * mm, "end": v(-122.56, 12.6) * mm});
            skLineSegment(sketch, "E385", {"start": v(-122.56, 12.6) * mm, "end": v(-122.53, 12.5) * mm});
            skLineSegment(sketch, "E386", {"start": v(-122.53, 12.5) * mm, "end": v(-122.5, 12.41) * mm});
            skLineSegment(sketch, "E387", {"start": v(-122.5, 12.41) * mm, "end": v(-122.48, 12.31) * mm});
            skLineSegment(sketch, "E388", {"start": v(-122.48, 12.31) * mm, "end": v(-122.47, 12.2) * mm});
            skLineSegment(sketch, "E389", {"start": v(-122.47, 12.2) * mm, "end": v(-122.47, 12.08) * mm});
            skLineSegment(sketch, "E390", {"start": v(-122.47, 12.08) * mm, "end": v(-122.47, 11.96) * mm});
            skLineSegment(sketch, "E391", {"start": v(-122.47, 11.96) * mm, "end": v(-122.48, 11.85) * mm});
            skLineSegment(sketch, "E392", {"start": v(-122.48, 11.85) * mm, "end": v(-122.5, 11.75) * mm});
            skLineSegment(sketch, "E393", {"start": v(-122.5, 11.75) * mm, "end": v(-122.53, 11.66) * mm});
            skLineSegment(sketch, "E394", {"start": v(-122.53, 11.66) * mm, "end": v(-122.56, 11.57) * mm});
            skLineSegment(sketch, "E395", {"start": v(-122.56, 11.57) * mm, "end": v(-122.6, 11.5) * mm});
            skLineSegment(sketch, "E396", {"start": v(-122.6, 11.5) * mm, "end": v(-122.66, 11.42) * mm});
            skLineSegment(sketch, "E397", {"start": v(-122.66, 11.42) * mm, "end": v(-122.72, 11.36) * mm});
            skLineSegment(sketch, "E398", {"start": v(-122.72, 11.36) * mm, "end": v(-122.78, 11.3) * mm});
            skLineSegment(sketch, "E399", {"start": v(-122.78, 11.3) * mm, "end": v(-122.86, 11.25) * mm});
            skLineSegment(sketch, "E400", {"start": v(-122.86, 11.25) * mm, "end": v(-122.94, 11.21) * mm});
            skLineSegment(sketch, "E401", {"start": v(-122.94, 11.21) * mm, "end": v(-123.03, 11.18) * mm});
            skLineSegment(sketch, "E402", {"start": v(-123.03, 11.18) * mm, "end": v(-123.13, 11.16) * mm});
            skLineSegment(sketch, "E403", {"start": v(-123.13, 11.16) * mm, "end": v(-123.24, 11.14) * mm});
            skLineSegment(sketch, "E404", {"start": v(-123.24, 11.14) * mm, "end": v(-123.35, 11.13) * mm});
            skLineSegment(sketch, "E405", {"start": v(-123.35, 11.13) * mm, "end": v(-123.48, 11.12) * mm});
            skLineSegment(sketch, "E406", {"start": v(-123.48, 11.12) * mm, "end": v(-138.3, 11.12) * mm});
            skLineSegment(sketch, "E407", {"start": v(-138.3, 11.12) * mm, "end": v(-138.64, 11.12) * mm});
            skLineSegment(sketch, "E408", {"start": v(-138.64, 11.12) * mm, "end": v(-138.98, 11.1) * mm});
            skLineSegment(sketch, "E409", {"start": v(-138.98, 11.1) * mm, "end": v(-139.3, 11.06) * mm});
            skLineSegment(sketch, "E410", {"start": v(-139.3, 11.06) * mm, "end": v(-139.63, 11) * mm});
            skLineSegment(sketch, "E411", {"start": v(-139.63, 11) * mm, "end": v(-139.95, 10.94) * mm});
            skLineSegment(sketch, "E412", {"start": v(-139.95, 10.94) * mm, "end": v(-140.25, 10.86) * mm});
            skLineSegment(sketch, "E413", {"start": v(-140.25, 10.86) * mm, "end": v(-140.55, 10.77) * mm});
            skLineSegment(sketch, "E414", {"start": v(-140.55, 10.77) * mm, "end": v(-140.85, 10.66) * mm});
            skLineSegment(sketch, "E415", {"start": v(-140.85, 10.66) * mm, "end": v(-141.13, 10.54) * mm});
            skLineSegment(sketch, "E416", {"start": v(-141.13, 10.54) * mm, "end": v(-141.41, 10.4) * mm});
            skLineSegment(sketch, "E417", {"start": v(-141.41, 10.4) * mm, "end": v(-141.68, 10.26) * mm});
            skLineSegment(sketch, "E418", {"start": v(-141.68, 10.26) * mm, "end": v(-141.94, 10.1) * mm});
            skLineSegment(sketch, "E419", {"start": v(-141.94, 10.1) * mm, "end": v(-142.2, 9.91) * mm});
            skLineSegment(sketch, "E420", {"start": v(-142.2, 9.91) * mm, "end": v(-142.45, 9.72) * mm});
            skLineSegment(sketch, "E421", {"start": v(-142.45, 9.72) * mm, "end": v(-142.69, 9.52) * mm});
            skLineSegment(sketch, "E422", {"start": v(-142.69, 9.52) * mm, "end": v(-142.92, 9.3) * mm});
            skLineSegment(sketch, "E423", {"start": v(-142.92, 9.3) * mm, "end": v(-143.14, 9.06) * mm});
            skLineSegment(sketch, "E424", {"start": v(-143.14, 9.06) * mm, "end": v(-143.34, 8.82) * mm});
            skLineSegment(sketch, "E425", {"start": v(-143.34, 8.82) * mm, "end": v(-143.54, 8.58) * mm});
            skLineSegment(sketch, "E426", {"start": v(-143.54, 8.58) * mm, "end": v(-143.72, 8.32) * mm});
            skLineSegment(sketch, "E427", {"start": v(-143.72, 8.32) * mm, "end": v(-143.88, 8.06) * mm});
            skLineSegment(sketch, "E428", {"start": v(-143.88, 8.06) * mm, "end": v(-144.03, 7.79) * mm});
            skLineSegment(sketch, "E429", {"start": v(-144.03, 7.79) * mm, "end": v(-144.17, 7.5) * mm});
            skLineSegment(sketch, "E430", {"start": v(-144.17, 7.5) * mm, "end": v(-144.29, 7.22) * mm});
            skLineSegment(sketch, "E431", {"start": v(-144.29, 7.22) * mm, "end": v(-144.4, 6.93) * mm});
            skLineSegment(sketch, "E432", {"start": v(-144.4, 6.93) * mm, "end": v(-144.49, 6.63) * mm});
            skLineSegment(sketch, "E433", {"start": v(-144.49, 6.63) * mm, "end": v(-144.57, 6.32) * mm});
            skLineSegment(sketch, "E434", {"start": v(-144.57, 6.32) * mm, "end": v(-144.63, 6) * mm});
            skLineSegment(sketch, "E435", {"start": v(-144.63, 6) * mm, "end": v(-144.68, 5.68) * mm});
            skLineSegment(sketch, "E436", {"start": v(-144.68, 5.68) * mm, "end": v(-144.72, 5.35) * mm});
            skLineSegment(sketch, "E437", {"start": v(-144.72, 5.35) * mm, "end": v(-144.74, 5.02) * mm});
            skLineSegment(sketch, "E438", {"start": v(-144.74, 5.02) * mm, "end": v(-144.75, 4.67) * mm});
            skLineSegment(sketch, "E439", {"start": v(-144.75, 4.67) * mm, "end": v(-144.74, 4.33) * mm});
            skLineSegment(sketch, "E440", {"start": v(-144.74, 4.33) * mm, "end": v(-144.72, 4) * mm});
            skLineSegment(sketch, "E441", {"start": v(-144.72, 4) * mm, "end": v(-144.68, 3.66) * mm});
            skLineSegment(sketch, "E442", {"start": v(-144.68, 3.66) * mm, "end": v(-144.63, 3.34) * mm});
            skLineSegment(sketch, "E443", {"start": v(-144.63, 3.34) * mm, "end": v(-144.57, 3.02) * mm});
            skLineSegment(sketch, "E444", {"start": v(-144.57, 3.02) * mm, "end": v(-144.49, 2.72) * mm});
            skLineSegment(sketch, "E445", {"start": v(-144.49, 2.72) * mm, "end": v(-144.4, 2.42) * mm});
            skLineSegment(sketch, "E446", {"start": v(-144.4, 2.42) * mm, "end": v(-144.29, 2.12) * mm});
            skLineSegment(sketch, "E447", {"start": v(-144.29, 2.12) * mm, "end": v(-144.17, 1.84) * mm});
            skLineSegment(sketch, "E448", {"start": v(-144.17, 1.84) * mm, "end": v(-144.03, 1.56) * mm});
            skLineSegment(sketch, "E449", {"start": v(-144.03, 1.56) * mm, "end": v(-143.88, 1.29) * mm});
            skLineSegment(sketch, "E450", {"start": v(-143.88, 1.29) * mm, "end": v(-143.72, 1.02) * mm});
            skLineSegment(sketch, "E451", {"start": v(-143.72, 1.02) * mm, "end": v(-143.54, 0.77) * mm});
            skLineSegment(sketch, "E452", {"start": v(-143.54, 0.77) * mm, "end": v(-143.35, 0.52) * mm});
            skLineSegment(sketch, "E453", {"start": v(-143.35, 0.52) * mm, "end": v(-143.14, 0.28) * mm});
            skLineSegment(sketch, "E454", {"start": v(-143.14, 0.28) * mm, "end": v(-142.92, 0.05) * mm});
            skLineSegment(sketch, "E455", {"start": v(-142.92, 0.05) * mm, "end": v(-142.69, -0.17) * mm});
            skLineSegment(sketch, "E456", {"start": v(-142.69, -0.17) * mm, "end": v(-142.45, -0.37) * mm});
            skLineSegment(sketch, "E457", {"start": v(-142.45, -0.37) * mm, "end": v(-142.2, -0.57) * mm});
            skLineSegment(sketch, "E458", {"start": v(-142.2, -0.57) * mm, "end": v(-141.95, -0.75) * mm});
            skLineSegment(sketch, "E459", {"start": v(-141.95, -0.75) * mm, "end": v(-141.68, -0.9) * mm});
            skLineSegment(sketch, "E460", {"start": v(-141.68, -0.9) * mm, "end": v(-141.41, -1.06) * mm});
            skLineSegment(sketch, "E461", {"start": v(-141.41, -1.06) * mm, "end": v(-141.13, -1.2) * mm});
            skLineSegment(sketch, "E462", {"start": v(-141.13, -1.2) * mm, "end": v(-140.85, -1.32) * mm});
            skLineSegment(sketch, "E463", {"start": v(-140.85, -1.32) * mm, "end": v(-140.55, -1.42) * mm});
            skLineSegment(sketch, "E464", {"start": v(-140.55, -1.42) * mm, "end": v(-140.25, -1.52) * mm});
            skLineSegment(sketch, "E465", {"start": v(-140.25, -1.52) * mm, "end": v(-139.95, -1.6) * mm});
            skLineSegment(sketch, "E466", {"start": v(-139.95, -1.6) * mm, "end": v(-139.63, -1.66) * mm});
            skLineSegment(sketch, "E467", {"start": v(-139.63, -1.66) * mm, "end": v(-139.3, -1.71) * mm});
            skLineSegment(sketch, "E468", {"start": v(-139.3, -1.71) * mm, "end": v(-138.98, -1.75) * mm});
            skLineSegment(sketch, "E469", {"start": v(-138.98, -1.75) * mm, "end": v(-138.64, -1.77) * mm});
            skLineSegment(sketch, "E470", {"start": v(-138.64, -1.77) * mm, "end": v(-138.3, -1.78) * mm});
            skLineSegment(sketch, "E471", {"start": v(-138.3, -1.78) * mm, "end": v(-128.4, -1.78) * mm});
            skLineSegment(sketch, "E472", {"start": v(-128.4, -1.78) * mm, "end": v(-128.28, -1.78) * mm});
            skLineSegment(sketch, "E473", {"start": v(-128.28, -1.78) * mm, "end": v(-128.17, -1.8) * mm});
            skLineSegment(sketch, "E474", {"start": v(-128.17, -1.8) * mm, "end": v(-128.07, -1.8) * mm});
            skLineSegment(sketch, "E475", {"start": v(-128.07, -1.8) * mm, "end": v(-127.98, -1.83) * mm});
            skLineSegment(sketch, "E476", {"start": v(-127.98, -1.83) * mm, "end": v(-127.89, -1.86) * mm});
            skLineSegment(sketch, "E477", {"start": v(-127.89, -1.86) * mm, "end": v(-127.81, -1.9) * mm});
            skLineSegment(sketch, "E478", {"start": v(-127.81, -1.9) * mm, "end": v(-127.74, -1.95) * mm});
            skLineSegment(sketch, "E479", {"start": v(-127.74, -1.95) * mm, "end": v(-127.68, -2) * mm});
            skLineSegment(sketch, "E480", {"start": v(-127.68, -2) * mm, "end": v(-127.62, -2.07) * mm});
            skLineSegment(sketch, "E481", {"start": v(-127.62, -2.07) * mm, "end": v(-127.57, -2.13) * mm});
            skLineSegment(sketch, "E482", {"start": v(-127.57, -2.13) * mm, "end": v(-127.53, -2.21) * mm});
            skLineSegment(sketch, "E483", {"start": v(-127.53, -2.21) * mm, "end": v(-127.5, -2.3) * mm});
            skLineSegment(sketch, "E484", {"start": v(-127.5, -2.3) * mm, "end": v(-127.48, -2.39) * mm});
            skLineSegment(sketch, "E485", {"start": v(-127.48, -2.39) * mm, "end": v(-127.46, -2.49) * mm});
            skLineSegment(sketch, "E486", {"start": v(-127.46, -2.49) * mm, "end": v(-127.45, -2.6) * mm});
            skLineSegment(sketch, "E487", {"start": v(-127.45, -2.6) * mm, "end": v(-127.44, -2.7) * mm});
            skLineSegment(sketch, "E488", {"start": v(-127.44, -2.7) * mm, "end": v(-127.45, -2.83) * mm});
            skLineSegment(sketch, "E489", {"start": v(-127.45, -2.83) * mm, "end": v(-127.46, -2.94) * mm});
            skLineSegment(sketch, "E490", {"start": v(-127.46, -2.94) * mm, "end": v(-127.48, -3.05) * mm});
            skLineSegment(sketch, "E491", {"start": v(-127.48, -3.05) * mm, "end": v(-127.5, -3.15) * mm});
            skLineSegment(sketch, "E492", {"start": v(-127.5, -3.15) * mm, "end": v(-127.53, -3.24) * mm});
            skLineSegment(sketch, "E493", {"start": v(-127.53, -3.24) * mm, "end": v(-127.57, -3.32) * mm});
            skLineSegment(sketch, "E494", {"start": v(-127.57, -3.32) * mm, "end": v(-127.62, -3.39) * mm});
            skLineSegment(sketch, "E495", {"start": v(-127.62, -3.39) * mm, "end": v(-127.68, -3.45) * mm});
            skLineSegment(sketch, "E496", {"start": v(-127.68, -3.45) * mm, "end": v(-127.74, -3.51) * mm});
            skLineSegment(sketch, "E497", {"start": v(-127.74, -3.51) * mm, "end": v(-127.81, -3.56) * mm});
            skLineSegment(sketch, "E498", {"start": v(-127.81, -3.56) * mm, "end": v(-127.89, -3.6) * mm});
            skLineSegment(sketch, "E499", {"start": v(-127.89, -3.6) * mm, "end": v(-127.98, -3.63) * mm});
            skLineSegment(sketch, "E500", {"start": v(-127.98, -3.63) * mm, "end": v(-128.07, -3.66) * mm});
            skLineSegment(sketch, "E501", {"start": v(-128.07, -3.66) * mm, "end": v(-128.17, -3.68) * mm});
            skLineSegment(sketch, "E502", {"start": v(-128.17, -3.68) * mm, "end": v(-128.28, -3.69) * mm});
            skLineSegment(sketch, "E503", {"start": v(-128.28, -3.69) * mm, "end": v(-128.4, -3.7) * mm});
            skLineSegment(sketch, "E504", {"start": v(-128.4, -3.7) * mm, "end": v(-138.3, -3.7) * mm});
            skLineSegment(sketch, "E505", {"start": v(-138.3, -3.7) * mm, "end": v(-138.64, -3.7) * mm});
            skLineSegment(sketch, "E506", {"start": v(-138.64, -3.7) * mm, "end": v(-138.98, -3.72) * mm});
            skLineSegment(sketch, "E507", {"start": v(-138.98, -3.72) * mm, "end": v(-139.3, -3.76) * mm});
            skLineSegment(sketch, "E508", {"start": v(-139.3, -3.76) * mm, "end": v(-139.63, -3.8) * mm});
            skLineSegment(sketch, "E509", {"start": v(-139.63, -3.8) * mm, "end": v(-139.95, -3.87) * mm});
            skLineSegment(sketch, "E510", {"start": v(-139.95, -3.87) * mm, "end": v(-140.25, -3.95) * mm});
            skLineSegment(sketch, "E511", {"start": v(-140.25, -3.95) * mm, "end": v(-140.55, -4.04) * mm});
            skLineSegment(sketch, "E512", {"start": v(-140.55, -4.04) * mm, "end": v(-140.85, -4.15) * mm});
            skLineSegment(sketch, "E513", {"start": v(-140.85, -4.15) * mm, "end": v(-141.13, -4.27) * mm});
            skLineSegment(sketch, "E514", {"start": v(-141.13, -4.27) * mm, "end": v(-141.41, -4.4) * mm});
            skLineSegment(sketch, "E515", {"start": v(-141.41, -4.4) * mm, "end": v(-141.68, -4.55) * mm});
            skLineSegment(sketch, "E516", {"start": v(-141.68, -4.55) * mm, "end": v(-141.94, -4.72) * mm});
            skLineSegment(sketch, "E517", {"start": v(-141.94, -4.72) * mm, "end": v(-142.2, -4.9) * mm});
            skLineSegment(sketch, "E518", {"start": v(-142.2, -4.9) * mm, "end": v(-142.45, -5.09) * mm});
            skLineSegment(sketch, "E519", {"start": v(-142.45, -5.09) * mm, "end": v(-142.69, -5.3) * mm});
            skLineSegment(sketch, "E520", {"start": v(-142.69, -5.3) * mm, "end": v(-142.92, -5.51) * mm});
            skLineSegment(sketch, "E521", {"start": v(-142.92, -5.51) * mm, "end": v(-143.14, -5.74) * mm});
            skLineSegment(sketch, "E522", {"start": v(-143.14, -5.74) * mm, "end": v(-143.34, -5.98) * mm});
            skLineSegment(sketch, "E523", {"start": v(-143.34, -5.98) * mm, "end": v(-143.54, -6.23) * mm});
            skLineSegment(sketch, "E524", {"start": v(-143.54, -6.23) * mm, "end": v(-143.72, -6.48) * mm});
            skLineSegment(sketch, "E525", {"start": v(-143.72, -6.48) * mm, "end": v(-143.88, -6.74) * mm});
            skLineSegment(sketch, "E526", {"start": v(-143.88, -6.74) * mm, "end": v(-144.03, -7.01) * mm});
            skLineSegment(sketch, "E527", {"start": v(-144.03, -7.01) * mm, "end": v(-144.17, -7.3) * mm});
            skLineSegment(sketch, "E528", {"start": v(-144.17, -7.3) * mm, "end": v(-144.29, -7.58) * mm});
            skLineSegment(sketch, "E529", {"start": v(-144.29, -7.58) * mm, "end": v(-144.4, -7.87) * mm});
            skLineSegment(sketch, "E530", {"start": v(-144.4, -7.87) * mm, "end": v(-144.49, -8.17) * mm});
            skLineSegment(sketch, "E531", {"start": v(-144.49, -8.17) * mm, "end": v(-144.57, -8.48) * mm});
            skLineSegment(sketch, "E532", {"start": v(-144.57, -8.48) * mm, "end": v(-144.63, -8.8) * mm});
            skLineSegment(sketch, "E533", {"start": v(-144.63, -8.8) * mm, "end": v(-144.68, -9.13) * mm});
            skLineSegment(sketch, "E534", {"start": v(-144.68, -9.13) * mm, "end": v(-144.72, -9.46) * mm});
            skLineSegment(sketch, "E535", {"start": v(-144.72, -9.46) * mm, "end": v(-144.74, -9.8) * mm});
            skLineSegment(sketch, "E536", {"start": v(-144.74, -9.8) * mm, "end": v(-144.75, -10.14) * mm});
            skLineSegment(sketch, "E537", {"start": v(-144.75, -10.14) * mm, "end": v(-144.74, -10.5) * mm});
            skLineSegment(sketch, "E538", {"start": v(-144.74, -10.5) * mm, "end": v(-144.72, -10.83) * mm});
            skLineSegment(sketch, "E539", {"start": v(-144.72, -10.83) * mm, "end": v(-144.68, -11.16) * mm});
            skLineSegment(sketch, "E540", {"start": v(-144.68, -11.16) * mm, "end": v(-144.63, -11.49) * mm});
            skLineSegment(sketch, "E541", {"start": v(-144.63, -11.49) * mm, "end": v(-144.57, -11.8) * mm});
            skLineSegment(sketch, "E542", {"start": v(-144.57, -11.8) * mm, "end": v(-144.49, -12.12) * mm});
            skLineSegment(sketch, "E543", {"start": v(-144.49, -12.12) * mm, "end": v(-144.4, -12.42) * mm});
            skLineSegment(sketch, "E544", {"start": v(-144.4, -12.42) * mm, "end": v(-144.29, -12.72) * mm});
            skLineSegment(sketch, "E545", {"start": v(-144.29, -12.72) * mm, "end": v(-144.17, -13) * mm});
            skLineSegment(sketch, "E546", {"start": v(-144.17, -13) * mm, "end": v(-144.03, -13.28) * mm});
            skLineSegment(sketch, "E547", {"start": v(-144.03, -13.28) * mm, "end": v(-143.88, -13.56) * mm});
            skLineSegment(sketch, "E548", {"start": v(-143.88, -13.56) * mm, "end": v(-143.72, -13.82) * mm});
            skLineSegment(sketch, "E549", {"start": v(-143.72, -13.82) * mm, "end": v(-143.54, -14.08) * mm});
            skLineSegment(sketch, "E550", {"start": v(-143.54, -14.08) * mm, "end": v(-143.35, -14.33) * mm});
            skLineSegment(sketch, "E551", {"start": v(-143.35, -14.33) * mm, "end": v(-143.14, -14.57) * mm});
            skLineSegment(sketch, "E552", {"start": v(-143.14, -14.57) * mm, "end": v(-142.92, -14.8) * mm});
            skLineSegment(sketch, "E553", {"start": v(-142.92, -14.8) * mm, "end": v(-142.69, -15.02) * mm});
            skLineSegment(sketch, "E554", {"start": v(-142.69, -15.02) * mm, "end": v(-142.45, -15.23) * mm});
            skLineSegment(sketch, "E555", {"start": v(-142.45, -15.23) * mm, "end": v(-142.2, -15.43) * mm});
            skLineSegment(sketch, "E556", {"start": v(-142.2, -15.43) * mm, "end": v(-141.95, -15.6) * mm});
            skLineSegment(sketch, "E557", {"start": v(-141.95, -15.6) * mm, "end": v(-141.68, -15.77) * mm});
            skLineSegment(sketch, "E558", {"start": v(-141.68, -15.77) * mm, "end": v(-141.41, -15.92) * mm});
            skLineSegment(sketch, "E559", {"start": v(-141.41, -15.92) * mm, "end": v(-141.13, -16.06) * mm});
            skLineSegment(sketch, "E560", {"start": v(-141.13, -16.06) * mm, "end": v(-140.85, -16.18) * mm});
            skLineSegment(sketch, "E561", {"start": v(-140.85, -16.18) * mm, "end": v(-140.55, -16.3) * mm});
            skLineSegment(sketch, "E562", {"start": v(-140.55, -16.3) * mm, "end": v(-140.25, -16.39) * mm});
            skLineSegment(sketch, "E563", {"start": v(-140.25, -16.39) * mm, "end": v(-139.95, -16.46) * mm});
            skLineSegment(sketch, "E564", {"start": v(-139.95, -16.46) * mm, "end": v(-139.63, -16.53) * mm});
            skLineSegment(sketch, "E565", {"start": v(-139.63, -16.53) * mm, "end": v(-139.3, -16.58) * mm});
            skLineSegment(sketch, "E566", {"start": v(-139.3, -16.58) * mm, "end": v(-138.98, -16.62) * mm});
            skLineSegment(sketch, "E567", {"start": v(-138.98, -16.62) * mm, "end": v(-138.64, -16.64) * mm});
            skLineSegment(sketch, "E568", {"start": v(-138.64, -16.64) * mm, "end": v(-138.3, -16.65) * mm});
            skLineSegment(sketch, "E569", {"start": v(-138.3, -16.65) * mm, "end": v(-123.48, -16.65) * mm});
            skLineSegment(sketch, "E570", {"start": v(-123.48, -16.65) * mm, "end": v(-123.35, -16.65) * mm});
            skLineSegment(sketch, "E571", {"start": v(-123.35, -16.65) * mm, "end": v(-123.24, -16.66) * mm});
            skLineSegment(sketch, "E572", {"start": v(-123.24, -16.66) * mm, "end": v(-123.13, -16.68) * mm});
            skLineSegment(sketch, "E573", {"start": v(-123.13, -16.68) * mm, "end": v(-123.03, -16.7) * mm});
            skLineSegment(sketch, "E574", {"start": v(-123.03, -16.7) * mm, "end": v(-122.94, -16.74) * mm});
            skLineSegment(sketch, "E575", {"start": v(-122.94, -16.74) * mm, "end": v(-122.86, -16.78) * mm});
            skLineSegment(sketch, "E576", {"start": v(-122.86, -16.78) * mm, "end": v(-122.78, -16.83) * mm});
            skLineSegment(sketch, "E577", {"start": v(-122.78, -16.83) * mm, "end": v(-122.72, -16.89) * mm});
            skLineSegment(sketch, "E578", {"start": v(-122.72, -16.89) * mm, "end": v(-122.66, -16.95) * mm});
            skLineSegment(sketch, "E579", {"start": v(-122.66, -16.95) * mm, "end": v(-122.6, -17.02) * mm});
            skLineSegment(sketch, "E580", {"start": v(-122.6, -17.02) * mm, "end": v(-122.56, -17.1) * mm});
            skLineSegment(sketch, "E581", {"start": v(-122.56, -17.1) * mm, "end": v(-122.53, -17.2) * mm});
            skLineSegment(sketch, "E582", {"start": v(-122.53, -17.2) * mm, "end": v(-122.5, -17.3) * mm});
            skLineSegment(sketch, "E583", {"start": v(-122.5, -17.3) * mm, "end": v(-122.48, -17.4) * mm});
            skLineSegment(sketch, "E584", {"start": v(-122.48, -17.4) * mm, "end": v(-122.47, -17.5) * mm});
            skLineSegment(sketch, "E585", {"start": v(-122.47, -17.5) * mm, "end": v(-122.47, -17.63) * mm});
            skLineSegment(sketch, "E586", {"start": v(-122.47, -17.63) * mm, "end": v(-122.47, -17.75) * mm});
            skLineSegment(sketch, "E587", {"start": v(-122.47, -17.75) * mm, "end": v(-122.48, -17.85) * mm});
            skLineSegment(sketch, "E588", {"start": v(-122.48, -17.85) * mm, "end": v(-122.5, -17.95) * mm});
            skLineSegment(sketch, "E589", {"start": v(-122.5, -17.95) * mm, "end": v(-122.53, -18.04) * mm});
            skLineSegment(sketch, "E590", {"start": v(-122.53, -18.04) * mm, "end": v(-122.56, -18.13) * mm});
            skLineSegment(sketch, "E591", {"start": v(-122.56, -18.13) * mm, "end": v(-122.6, -18.2) * mm});
            skLineSegment(sketch, "E592", {"start": v(-122.6, -18.2) * mm, "end": v(-122.66, -18.27) * mm});
            skLineSegment(sketch, "E593", {"start": v(-122.66, -18.27) * mm, "end": v(-122.72, -18.34) * mm});
            skLineSegment(sketch, "E594", {"start": v(-122.72, -18.34) * mm, "end": v(-122.78, -18.39) * mm});
            skLineSegment(sketch, "E595", {"start": v(-122.78, -18.39) * mm, "end": v(-122.86, -18.44) * mm});
            skLineSegment(sketch, "E596", {"start": v(-122.86, -18.44) * mm, "end": v(-122.94, -18.47) * mm});
            skLineSegment(sketch, "E597", {"start": v(-122.94, -18.47) * mm, "end": v(-123.03, -18.5) * mm});
            skLineSegment(sketch, "E598", {"start": v(-123.03, -18.5) * mm, "end": v(-123.13, -18.53) * mm});
            skLineSegment(sketch, "E599", {"start": v(-123.13, -18.53) * mm, "end": v(-123.24, -18.55) * mm});
            skLineSegment(sketch, "E600", {"start": v(-123.24, -18.55) * mm, "end": v(-123.35, -18.56) * mm});
            skLineSegment(sketch, "E601", {"start": v(-123.35, -18.56) * mm, "end": v(-123.48, -18.56) * mm});
            skLineSegment(sketch, "E602", {"start": v(-123.48, -18.56) * mm, "end": v(-140.73, -18.56) * mm});
            skLineSegment(sketch, "E603", {"start": v(-140.73, -18.56) * mm, "end": v(-140.94, -18.57) * mm});
            skLineSegment(sketch, "E604", {"start": v(-140.94, -18.57) * mm, "end": v(-141.15, -18.58) * mm});
            skLineSegment(sketch, "E605", {"start": v(-141.15, -18.58) * mm, "end": v(-141.36, -18.6) * mm});
            skLineSegment(sketch, "E606", {"start": v(-141.36, -18.6) * mm, "end": v(-141.56, -18.63) * mm});
            skLineSegment(sketch, "E607", {"start": v(-141.56, -18.63) * mm, "end": v(-141.75, -18.67) * mm});
            skLineSegment(sketch, "E608", {"start": v(-141.75, -18.67) * mm, "end": v(-141.95, -18.72) * mm});
            skLineSegment(sketch, "E609", {"start": v(-141.95, -18.72) * mm, "end": v(-142.13, -18.78) * mm});
            skLineSegment(sketch, "E610", {"start": v(-142.13, -18.78) * mm, "end": v(-142.31, -18.84) * mm});
            skLineSegment(sketch, "E611", {"start": v(-142.31, -18.84) * mm, "end": v(-142.5, -18.92) * mm});
            skLineSegment(sketch, "E612", {"start": v(-142.5, -18.92) * mm, "end": v(-142.67, -19) * mm});
            skLineSegment(sketch, "E613", {"start": v(-142.67, -19) * mm, "end": v(-142.83, -19.1) * mm});
            skLineSegment(sketch, "E614", {"start": v(-142.83, -19.1) * mm, "end": v(-143, -19.2) * mm});
            skLineSegment(sketch, "E615", {"start": v(-143, -19.2) * mm, "end": v(-143.16, -19.3) * mm});
            skLineSegment(sketch, "E616", {"start": v(-143.16, -19.3) * mm, "end": v(-143.31, -19.42) * mm});
            skLineSegment(sketch, "E617", {"start": v(-143.31, -19.42) * mm, "end": v(-143.46, -19.54) * mm});
            skLineSegment(sketch, "E618", {"start": v(-143.46, -19.54) * mm, "end": v(-143.6, -19.68) * mm});
            skLineSegment(sketch, "E619", {"start": v(-143.6, -19.68) * mm, "end": v(-143.74, -19.82) * mm});
            skLineSegment(sketch, "E620", {"start": v(-143.74, -19.82) * mm, "end": v(-143.87, -19.96) * mm});
            skLineSegment(sketch, "E621", {"start": v(-143.87, -19.96) * mm, "end": v(-144, -20.11) * mm});
            skLineSegment(sketch, "E622", {"start": v(-144, -20.11) * mm, "end": v(-144.1, -20.27) * mm});
            skLineSegment(sketch, "E623", {"start": v(-144.1, -20.27) * mm, "end": v(-144.2, -20.43) * mm});
            skLineSegment(sketch, "E624", {"start": v(-144.2, -20.43) * mm, "end": v(-144.3, -20.6) * mm});
            skLineSegment(sketch, "E625", {"start": v(-144.3, -20.6) * mm, "end": v(-144.38, -20.77) * mm});
            skLineSegment(sketch, "E626", {"start": v(-144.38, -20.77) * mm, "end": v(-144.46, -20.95) * mm});
            skLineSegment(sketch, "E627", {"start": v(-144.46, -20.95) * mm, "end": v(-144.53, -21.13) * mm});
            skLineSegment(sketch, "E628", {"start": v(-144.53, -21.13) * mm, "end": v(-144.59, -21.31) * mm});
            skLineSegment(sketch, "E629", {"start": v(-144.59, -21.31) * mm, "end": v(-144.63, -21.5) * mm});
            skLineSegment(sketch, "E630", {"start": v(-144.63, -21.5) * mm, "end": v(-144.67, -21.7) * mm});
            skLineSegment(sketch, "E631", {"start": v(-144.67, -21.7) * mm, "end": v(-144.7, -21.9) * mm});
            skLineSegment(sketch, "E632", {"start": v(-144.7, -21.9) * mm, "end": v(-144.73, -22.1) * mm});
            skLineSegment(sketch, "E633", {"start": v(-144.73, -22.1) * mm, "end": v(-144.74, -22.31) * mm});
            skLineSegment(sketch, "E634", {"start": v(-144.74, -22.31) * mm, "end": v(-144.75, -22.53) * mm});
            skLineSegment(sketch, "E635", {"start": v(-144.75, -22.53) * mm, "end": v(-144.74, -22.74) * mm});
            skLineSegment(sketch, "E636", {"start": v(-144.74, -22.74) * mm, "end": v(-144.73, -22.95) * mm});
            skLineSegment(sketch, "E637", {"start": v(-144.73, -22.95) * mm, "end": v(-144.7, -23.15) * mm});
            skLineSegment(sketch, "E638", {"start": v(-144.7, -23.15) * mm, "end": v(-144.67, -23.35) * mm});
            skLineSegment(sketch, "E639", {"start": v(-144.67, -23.35) * mm, "end": v(-144.63, -23.55) * mm});
            skLineSegment(sketch, "E640", {"start": v(-144.63, -23.55) * mm, "end": v(-144.59, -23.74) * mm});
            skLineSegment(sketch, "E641", {"start": v(-144.59, -23.74) * mm, "end": v(-144.53, -23.92) * mm});
            skLineSegment(sketch, "E642", {"start": v(-144.53, -23.92) * mm, "end": v(-144.46, -24.1) * mm});
            skLineSegment(sketch, "E643", {"start": v(-144.46, -24.1) * mm, "end": v(-144.38, -24.28) * mm});
            skLineSegment(sketch, "E644", {"start": v(-144.38, -24.28) * mm, "end": v(-144.3, -24.45) * mm});
            skLineSegment(sketch, "E645", {"start": v(-144.3, -24.45) * mm, "end": v(-144.2, -24.62) * mm});
            skLineSegment(sketch, "E646", {"start": v(-144.2, -24.62) * mm, "end": v(-144.1, -24.78) * mm});
            skLineSegment(sketch, "E647", {"start": v(-144.1, -24.78) * mm, "end": v(-144, -24.94) * mm});
            skLineSegment(sketch, "E648", {"start": v(-144, -24.94) * mm, "end": v(-143.87, -25.09) * mm});
            skLineSegment(sketch, "E649", {"start": v(-143.87, -25.09) * mm, "end": v(-143.74, -25.23) * mm});
            skLineSegment(sketch, "E650", {"start": v(-143.74, -25.23) * mm, "end": v(-143.6, -25.38) * mm});
            skLineSegment(sketch, "E651", {"start": v(-143.6, -25.38) * mm, "end": v(-143.46, -25.5) * mm});
            skLineSegment(sketch, "E652", {"start": v(-143.46, -25.5) * mm, "end": v(-143.31, -25.64) * mm});
            skLineSegment(sketch, "E653", {"start": v(-143.31, -25.64) * mm, "end": v(-143.16, -25.75) * mm});
            skLineSegment(sketch, "E654", {"start": v(-143.16, -25.75) * mm, "end": v(-143, -25.86) * mm});
            skLineSegment(sketch, "E655", {"start": v(-143, -25.86) * mm, "end": v(-142.84, -25.96) * mm});
            skLineSegment(sketch, "E656", {"start": v(-142.84, -25.96) * mm, "end": v(-142.67, -26.05) * mm});
            skLineSegment(sketch, "E657", {"start": v(-142.67, -26.05) * mm, "end": v(-142.5, -26.14) * mm});
            skLineSegment(sketch, "E658", {"start": v(-142.5, -26.14) * mm, "end": v(-142.32, -26.2) * mm});
            skLineSegment(sketch, "E659", {"start": v(-142.32, -26.2) * mm, "end": v(-142.13, -26.27) * mm});
            skLineSegment(sketch, "E660", {"start": v(-142.13, -26.27) * mm, "end": v(-141.95, -26.33) * mm});
            skLineSegment(sketch, "E661", {"start": v(-141.95, -26.33) * mm, "end": v(-141.75, -26.38) * mm});
            skLineSegment(sketch, "E662", {"start": v(-141.75, -26.38) * mm, "end": v(-141.56, -26.42) * mm});
            skLineSegment(sketch, "E663", {"start": v(-141.56, -26.42) * mm, "end": v(-141.36, -26.45) * mm});
            skLineSegment(sketch, "E664", {"start": v(-141.36, -26.45) * mm, "end": v(-141.15, -26.47) * mm});
            skLineSegment(sketch, "E665", {"start": v(-141.15, -26.47) * mm, "end": v(-140.94, -26.48) * mm});
            skLineSegment(sketch, "E666", {"start": v(-140.94, -26.48) * mm, "end": v(-140.73, -26.49) * mm});
            skLineSegment(sketch, "E667", {"start": v(-140.73, -26.49) * mm, "end": v(-100, -26.49) * mm});
            skLineSegment(sketch, "E668", {"start": v(-100, -26.49) * mm, "end": v(-99.68, -26.47) * mm});
            skLineSegment(sketch, "E669", {"start": v(-99.68, -26.47) * mm, "end": v(-99.37, -26.42) * mm});
            skLineSegment(sketch, "E670", {"start": v(-99.37, -26.42) * mm, "end": v(-99.07, -26.35) * mm});
            skLineSegment(sketch, "E671", {"start": v(-99.07, -26.35) * mm, "end": v(-98.78, -26.24) * mm});
            skLineSegment(sketch, "E672", {"start": v(-98.78, -26.24) * mm, "end": v(-98.5, -26.11) * mm});
            skLineSegment(sketch, "E673", {"start": v(-98.5, -26.11) * mm, "end": v(-98.25, -25.95) * mm});
            skLineSegment(sketch, "E674", {"start": v(-98.25, -25.95) * mm, "end": v(-98.01, -25.77) * mm});
            skLineSegment(sketch, "E675", {"start": v(-98.01, -25.77) * mm, "end": v(-97.79, -25.57) * mm});
            skLineSegment(sketch, "E676", {"start": v(-97.79, -25.57) * mm, "end": v(-97.59, -25.35) * mm});
            skLineSegment(sketch, "E677", {"start": v(-97.59, -25.35) * mm, "end": v(-97.4, -25.1) * mm});
            skLineSegment(sketch, "E678", {"start": v(-97.4, -25.1) * mm, "end": v(-97.25, -24.85) * mm});
            skLineSegment(sketch, "E679", {"start": v(-97.25, -24.85) * mm, "end": v(-97.12, -24.57) * mm});
            skLineSegment(sketch, "E680", {"start": v(-97.12, -24.57) * mm, "end": v(-97.01, -24.29) * mm});
            skLineSegment(sketch, "E681", {"start": v(-97.01, -24.29) * mm, "end": v(-96.93, -23.99) * mm});
            skLineSegment(sketch, "E682", {"start": v(-96.93, -23.99) * mm, "end": v(-96.89, -23.68) * mm});
            skLineSegment(sketch, "E683", {"start": v(-96.89, -23.68) * mm, "end": v(-96.87, -23.36) * mm});
            skLineSegment(sketch, "E684", {"start": v(-96.87, -23.36) * mm, "end": v(-96.87, -19.84) * mm});
            skLineSegment(sketch, "E685", {"start": v(-96.87, -19.84) * mm, "end": v(-96.88, -19.7) * mm});
            skLineSegment(sketch, "E686", {"start": v(-96.88, -19.7) * mm, "end": v(-96.9, -19.56) * mm});
            skLineSegment(sketch, "E687", {"start": v(-96.9, -19.56) * mm, "end": v(-96.93, -19.43) * mm});
            skLineSegment(sketch, "E688", {"start": v(-96.93, -19.43) * mm, "end": v(-96.97, -19.3) * mm});
            skLineSegment(sketch, "E689", {"start": v(-96.97, -19.3) * mm, "end": v(-97.02, -19.18) * mm});
            skLineSegment(sketch, "E690", {"start": v(-97.02, -19.18) * mm, "end": v(-97.09, -19.06) * mm});
            skLineSegment(sketch, "E691", {"start": v(-97.09, -19.06) * mm, "end": v(-97.16, -18.95) * mm});
            skLineSegment(sketch, "E692", {"start": v(-97.16, -18.95) * mm, "end": v(-97.24, -18.85) * mm});
            skLineSegment(sketch, "E693", {"start": v(-97.24, -18.85) * mm, "end": v(-97.33, -18.75) * mm});
            skLineSegment(sketch, "E694", {"start": v(-97.33, -18.75) * mm, "end": v(-97.43, -18.67) * mm});
            skLineSegment(sketch, "E695", {"start": v(-97.43, -18.67) * mm, "end": v(-97.54, -18.59) * mm});
            skLineSegment(sketch, "E696", {"start": v(-97.54, -18.59) * mm, "end": v(-97.66, -18.52) * mm});
            skLineSegment(sketch, "E697", {"start": v(-97.66, -18.52) * mm, "end": v(-97.78, -18.46) * mm});
            skLineSegment(sketch, "E698", {"start": v(-97.78, -18.46) * mm, "end": v(-97.9, -18.41) * mm});
            skLineSegment(sketch, "E699", {"start": v(-97.9, -18.41) * mm, "end": v(-98.04, -18.38) * mm});
            skLineSegment(sketch, "E700", {"start": v(-98.04, -18.38) * mm, "end": v(-98.17, -18.35) * mm});
            skLineSegment(sketch, "E701", {"start": v(-98.17, -18.35) * mm, "end": v(-98.9, -18.25) * mm});
            skLineSegment(sketch, "E702", {"start": v(-98.9, -18.25) * mm, "end": v(-99.6, -18.1) * mm});
            skLineSegment(sketch, "E703", {"start": v(-99.6, -18.1) * mm, "end": v(-100.29, -17.94) * mm});
            skLineSegment(sketch, "E704", {"start": v(-100.29, -17.94) * mm, "end": v(-100.96, -17.74) * mm});
            skLineSegment(sketch, "E705", {"start": v(-100.96, -17.74) * mm, "end": v(-101.63, -17.52) * mm});
            skLineSegment(sketch, "E706", {"start": v(-101.63, -17.52) * mm, "end": v(-102.27, -17.26) * mm});
            skLineSegment(sketch, "E707", {"start": v(-102.27, -17.26) * mm, "end": v(-102.9, -16.97) * mm});
            skLineSegment(sketch, "E708", {"start": v(-102.9, -16.97) * mm, "end": v(-103.52, -16.66) * mm});
            skLineSegment(sketch, "E709", {"start": v(-103.52, -16.66) * mm, "end": v(-104.12, -16.31) * mm});
            skLineSegment(sketch, "E710", {"start": v(-104.12, -16.31) * mm, "end": v(-104.7, -15.94) * mm});
            skLineSegment(sketch, "E711", {"start": v(-104.7, -15.94) * mm, "end": v(-105.28, -15.53) * mm});
            skLineSegment(sketch, "E712", {"start": v(-105.28, -15.53) * mm, "end": v(-105.84, -15.1) * mm});
            skLineSegment(sketch, "E713", {"start": v(-105.84, -15.1) * mm, "end": v(-106.38, -14.63) * mm});
            skLineSegment(sketch, "E714", {"start": v(-106.38, -14.63) * mm, "end": v(-106.9, -14.14) * mm});
            skLineSegment(sketch, "E715", {"start": v(-106.9, -14.14) * mm, "end": v(-107.4, -13.62) * mm});
            skLineSegment(sketch, "E716", {"start": v(-107.4, -13.62) * mm, "end": v(-107.9, -13.07) * mm});
            skLineSegment(sketch, "E717", {"start": v(-107.9, -13.07) * mm, "end": v(-108.37, -12.5) * mm});
            skLineSegment(sketch, "E718", {"start": v(-108.37, -12.5) * mm, "end": v(-108.8, -11.91) * mm});
            skLineSegment(sketch, "E719", {"start": v(-108.8, -11.91) * mm, "end": v(-109.22, -11.32) * mm});
            skLineSegment(sketch, "E720", {"start": v(-109.22, -11.32) * mm, "end": v(-109.6, -10.71) * mm});
            skLineSegment(sketch, "E721", {"start": v(-109.6, -10.71) * mm, "end": v(-109.95, -10.1) * mm});
            skLineSegment(sketch, "E722", {"start": v(-109.95, -10.1) * mm, "end": v(-110.27, -9.47) * mm});
            skLineSegment(sketch, "E723", {"start": v(-110.27, -9.47) * mm, "end": v(-110.55, -8.83) * mm});
            skLineSegment(sketch, "E724", {"start": v(-110.55, -8.83) * mm, "end": v(-110.81, -8.18) * mm});
            skLineSegment(sketch, "E725", {"start": v(-110.81, -8.18) * mm, "end": v(-111.04, -7.52) * mm});
            skLineSegment(sketch, "E726", {"start": v(-111.04, -7.52) * mm, "end": v(-111.24, -6.85) * mm});
            skLineSegment(sketch, "E727", {"start": v(-111.24, -6.85) * mm, "end": v(-111.4, -6.17) * mm});
            skLineSegment(sketch, "E728", {"start": v(-111.4, -6.17) * mm, "end": v(-111.55, -5.49) * mm});
            skLineSegment(sketch, "E729", {"start": v(-111.55, -5.49) * mm, "end": v(-111.65, -4.79) * mm});
            skLineSegment(sketch, "E730", {"start": v(-111.65, -4.79) * mm, "end": v(-111.73, -4.08) * mm});
            skLineSegment(sketch, "E731", {"start": v(-111.73, -4.08) * mm, "end": v(-111.78, -3.36) * mm});
            skLineSegment(sketch, "E732", {"start": v(-111.78, -3.36) * mm, "end": v(-111.8, -2.63) * mm});
            skLineSegment(sketch, "E733", {"start": v(-111.8, -2.63) * mm, "end": v(-111.77, -1.81) * mm});
            skLineSegment(sketch, "E734", {"start": v(-111.77, -1.81) * mm, "end": v(-111.72, -1) * mm});
            skLineSegment(sketch, "E735", {"start": v(-111.72, -1) * mm, "end": v(-111.63, -0.22) * mm});
            skLineSegment(sketch, "E736", {"start": v(-111.63, -0.22) * mm, "end": v(-111.5, 0.55) * mm});
            skLineSegment(sketch, "E737", {"start": v(-111.5, 0.55) * mm, "end": v(-111.34, 1.31) * mm});
            skLineSegment(sketch, "E738", {"start": v(-111.34, 1.31) * mm, "end": v(-111.14, 2.06) * mm});
            skLineSegment(sketch, "E739", {"start": v(-111.14, 2.06) * mm, "end": v(-110.9, 2.79) * mm});
            skLineSegment(sketch, "E740", {"start": v(-110.9, 2.79) * mm, "end": v(-110.63, 3.5) * mm});
            skLineSegment(sketch, "E741", {"start": v(-110.63, 3.5) * mm, "end": v(-110.32, 4.2) * mm});
            skLineSegment(sketch, "E742", {"start": v(-110.32, 4.2) * mm, "end": v(-109.98, 4.88) * mm});
            skLineSegment(sketch, "E743", {"start": v(-109.98, 4.88) * mm, "end": v(-109.6, 5.55) * mm});
            skLineSegment(sketch, "E744", {"start": v(-109.6, 5.55) * mm, "end": v(-109.18, 6.2) * mm});
            skLineSegment(sketch, "E745", {"start": v(-109.18, 6.2) * mm, "end": v(-108.73, 6.84) * mm});
            skLineSegment(sketch, "E746", {"start": v(-108.73, 6.84) * mm, "end": v(-108.24, 7.46) * mm});
            skLineSegment(sketch, "E747", {"start": v(-108.24, 7.46) * mm, "end": v(-107.72, 8.06) * mm});
            skLineSegment(sketch, "E748", {"start": v(-107.72, 8.06) * mm, "end": v(-107.16, 8.65) * mm});
            skLineSegment(sketch, "E749", {"start": v(-107.16, 8.65) * mm, "end": v(-106.58, 9.21) * mm});
            skLineSegment(sketch, "E750", {"start": v(-106.58, 9.21) * mm, "end": v(-105.98, 9.74) * mm});
            skLineSegment(sketch, "E751", {"start": v(-105.98, 9.74) * mm, "end": v(-105.36, 10.23) * mm});
            skLineSegment(sketch, "E752", {"start": v(-105.36, 10.23) * mm, "end": v(-104.73, 10.68) * mm});
            skLineSegment(sketch, "E753", {"start": v(-104.73, 10.68) * mm, "end": v(-104.08, 11.1) * mm});
            skLineSegment(sketch, "E754", {"start": v(-104.08, 11.1) * mm, "end": v(-103.41, 11.48) * mm});
            skLineSegment(sketch, "E755", {"start": v(-103.41, 11.48) * mm, "end": v(-102.73, 11.83) * mm});
            skLineSegment(sketch, "E756", {"start": v(-102.73, 11.83) * mm, "end": v(-102.03, 12.14) * mm});
            skLineSegment(sketch, "E757", {"start": v(-102.03, 12.14) * mm, "end": v(-101.32, 12.4) * mm});
            skLineSegment(sketch, "E758", {"start": v(-101.32, 12.4) * mm, "end": v(-100.6, 12.65) * mm});
            skLineSegment(sketch, "E759", {"start": v(-100.6, 12.65) * mm, "end": v(-99.85, 12.85) * mm});
            skLineSegment(sketch, "E760", {"start": v(-99.85, 12.85) * mm, "end": v(-99.1, 13.01) * mm});
            skLineSegment(sketch, "E761", {"start": v(-99.1, 13.01) * mm, "end": v(-98.32, 13.14) * mm});
            skLineSegment(sketch, "E762", {"start": v(-98.32, 13.14) * mm, "end": v(-97.53, 13.23) * mm});
            skLineSegment(sketch, "E763", {"start": v(-97.53, 13.23) * mm, "end": v(-96.73, 13.29) * mm});
            skLineSegment(sketch, "E764", {"start": v(-96.73, 13.29) * mm, "end": v(-95.91, 13.3) * mm});
            skLineSegment(sketch, "E765", {"start": v(-95.91, 13.3) * mm, "end": v(-95.09, 13.29) * mm});
            skLineSegment(sketch, "E766", {"start": v(-95.09, 13.29) * mm, "end": v(-94.28, 13.23) * mm});
            skLineSegment(sketch, "E767", {"start": v(-94.28, 13.23) * mm, "end": v(-93.48, 13.14) * mm});
            skLineSegment(sketch, "E768", {"start": v(-93.48, 13.14) * mm, "end": v(-92.7, 13.01) * mm});
            skLineSegment(sketch, "E769", {"start": v(-92.7, 13.01) * mm, "end": v(-91.94, 12.85) * mm});
            skLineSegment(sketch, "E770", {"start": v(-91.94, 12.85) * mm, "end": v(-91.2, 12.65) * mm});
            skLineSegment(sketch, "E771", {"start": v(-91.2, 12.65) * mm, "end": v(-90.46, 12.41) * mm});
            skLineSegment(sketch, "E772", {"start": v(-90.46, 12.41) * mm, "end": v(-89.75, 12.14) * mm});
            skLineSegment(sketch, "E773", {"start": v(-89.75, 12.14) * mm, "end": v(-89.05, 11.83) * mm});
            skLineSegment(sketch, "E774", {"start": v(-89.05, 11.83) * mm, "end": v(-88.36, 11.5) * mm});
            skLineSegment(sketch, "E775", {"start": v(-88.36, 11.5) * mm, "end": v(-87.7, 11.11) * mm});
            skLineSegment(sketch, "E776", {"start": v(-87.7, 11.11) * mm, "end": v(-87.04, 10.7) * mm});
            skLineSegment(sketch, "E777", {"start": v(-87.04, 10.7) * mm, "end": v(-86.4, 10.24) * mm});
            skLineSegment(sketch, "E778", {"start": v(-86.4, 10.24) * mm, "end": v(-85.8, 9.76) * mm});
            skLineSegment(sketch, "E779", {"start": v(-85.8, 9.76) * mm, "end": v(-85.19, 9.24) * mm});
            skLineSegment(sketch, "E780", {"start": v(-85.19, 9.24) * mm, "end": v(-84.6, 8.68) * mm});
            skLineSegment(sketch, "E781", {"start": v(-84.6, 8.68) * mm, "end": v(-84.05, 8.1) * mm});
            skLineSegment(sketch, "E782", {"start": v(-84.05, 8.1) * mm, "end": v(-83.52, 7.5) * mm});
            skLineSegment(sketch, "E783", {"start": v(-83.52, 7.5) * mm, "end": v(-83.04, 6.87) * mm});
            skLineSegment(sketch, "E784", {"start": v(-83.04, 6.87) * mm, "end": v(-82.59, 6.24) * mm});
            skLineSegment(sketch, "E785", {"start": v(-82.59, 6.24) * mm, "end": v(-82.17, 5.59) * mm});
            skLineSegment(sketch, "E786", {"start": v(-82.17, 5.59) * mm, "end": v(-81.8, 4.92) * mm});
            skLineSegment(sketch, "E787", {"start": v(-81.8, 4.92) * mm, "end": v(-81.45, 4.23) * mm});
            skLineSegment(sketch, "E788", {"start": v(-81.45, 4.23) * mm, "end": v(-81.14, 3.53) * mm});
            skLineSegment(sketch, "E789", {"start": v(-81.14, 3.53) * mm, "end": v(-80.87, 2.82) * mm});
            skLineSegment(sketch, "E790", {"start": v(-80.87, 2.82) * mm, "end": v(-80.63, 2.09) * mm});
            skLineSegment(sketch, "E791", {"start": v(-80.63, 2.09) * mm, "end": v(-80.43, 1.34) * mm});
            skLineSegment(sketch, "E792", {"start": v(-80.43, 1.34) * mm, "end": v(-80.27, 0.57) * mm});
            skLineSegment(sketch, "E793", {"start": v(-80.27, 0.57) * mm, "end": v(-80.14, -0.2) * mm});
            skLineSegment(sketch, "E794", {"start": v(-80.14, -0.2) * mm, "end": v(-80.05, -1) * mm});
            skLineSegment(sketch, "E795", {"start": v(-80.05, -1) * mm, "end": v(-80, -1.8) * mm});
            skLineSegment(sketch, "E796", {"start": v(-80, -1.8) * mm, "end": v(-79.98, -2.63) * mm});
            skLineSegment(sketch, "E797", {"start": v(-79.98, -2.63) * mm, "end": v(-80, -3.36) * mm});
            skLineSegment(sketch, "E798", {"start": v(-80, -3.36) * mm, "end": v(-80.04, -4.08) * mm});
            skLineSegment(sketch, "E799", {"start": v(-80.04, -4.08) * mm, "end": v(-80.12, -4.79) * mm});
            skLineSegment(sketch, "E800", {"start": v(-80.12, -4.79) * mm, "end": v(-80.22, -5.48) * mm});
            skLineSegment(sketch, "E801", {"start": v(-80.22, -5.48) * mm, "end": v(-80.36, -6.17) * mm});
            skLineSegment(sketch, "E802", {"start": v(-80.36, -6.17) * mm, "end": v(-80.53, -6.85) * mm});
            skLineSegment(sketch, "E803", {"start": v(-80.53, -6.85) * mm, "end": v(-80.73, -7.52) * mm});
            skLineSegment(sketch, "E804", {"start": v(-80.73, -7.52) * mm, "end": v(-80.96, -8.18) * mm});
            skLineSegment(sketch, "E805", {"start": v(-80.96, -8.18) * mm, "end": v(-81.22, -8.83) * mm});
            skLineSegment(sketch, "E806", {"start": v(-81.22, -8.83) * mm, "end": v(-81.5, -9.47) * mm});
            skLineSegment(sketch, "E807", {"start": v(-81.5, -9.47) * mm, "end": v(-81.83, -10.1) * mm});
            skLineSegment(sketch, "E808", {"start": v(-81.83, -10.1) * mm, "end": v(-82.18, -10.71) * mm});
            skLineSegment(sketch, "E809", {"start": v(-82.18, -10.71) * mm, "end": v(-82.56, -11.32) * mm});
            skLineSegment(sketch, "E810", {"start": v(-82.56, -11.32) * mm, "end": v(-82.97, -11.91) * mm});
            skLineSegment(sketch, "E811", {"start": v(-82.97, -11.91) * mm, "end": v(-83.41, -12.5) * mm});
            skLineSegment(sketch, "E812", {"start": v(-83.41, -12.5) * mm, "end": v(-83.88, -13.07) * mm});
            skLineSegment(sketch, "E813", {"start": v(-83.88, -13.07) * mm, "end": v(-84.38, -13.62) * mm});
            skLineSegment(sketch, "E814", {"start": v(-84.38, -13.62) * mm, "end": v(-84.89, -14.14) * mm});
            skLineSegment(sketch, "E815", {"start": v(-84.89, -14.14) * mm, "end": v(-85.41, -14.63) * mm});
            skLineSegment(sketch, "E816", {"start": v(-85.41, -14.63) * mm, "end": v(-85.95, -15.1) * mm});
            skLineSegment(sketch, "E817", {"start": v(-85.95, -15.1) * mm, "end": v(-86.51, -15.53) * mm});
            skLineSegment(sketch, "E818", {"start": v(-86.51, -15.53) * mm, "end": v(-87.09, -15.94) * mm});
            skLineSegment(sketch, "E819", {"start": v(-87.09, -15.94) * mm, "end": v(-87.67, -16.31) * mm});
            skLineSegment(sketch, "E820", {"start": v(-87.67, -16.31) * mm, "end": v(-88.28, -16.66) * mm});
            skLineSegment(sketch, "E821", {"start": v(-88.28, -16.66) * mm, "end": v(-88.9, -16.97) * mm});
            skLineSegment(sketch, "E822", {"start": v(-88.9, -16.97) * mm, "end": v(-89.53, -17.26) * mm});
            skLineSegment(sketch, "E823", {"start": v(-89.53, -17.26) * mm, "end": v(-90.18, -17.52) * mm});
            skLineSegment(sketch, "E824", {"start": v(-90.18, -17.52) * mm, "end": v(-90.85, -17.74) * mm});
            skLineSegment(sketch, "E825", {"start": v(-90.85, -17.74) * mm, "end": v(-91.52, -17.94) * mm});
            skLineSegment(sketch, "E826", {"start": v(-91.52, -17.94) * mm, "end": v(-92.22, -18.1) * mm});
            skLineSegment(sketch, "E827", {"start": v(-92.22, -18.1) * mm, "end": v(-92.93, -18.25) * mm});
            skLineSegment(sketch, "E828", {"start": v(-92.93, -18.25) * mm, "end": v(-93.65, -18.35) * mm});
            skLineSegment(sketch, "E829", {"start": v(-93.65, -18.35) * mm, "end": v(-93.78, -18.38) * mm});
            skLineSegment(sketch, "E830", {"start": v(-93.78, -18.38) * mm, "end": v(-93.92, -18.41) * mm});
            skLineSegment(sketch, "E831", {"start": v(-93.92, -18.41) * mm, "end": v(-94.04, -18.46) * mm});
            skLineSegment(sketch, "E832", {"start": v(-94.04, -18.46) * mm, "end": v(-94.17, -18.52) * mm});
            skLineSegment(sketch, "E833", {"start": v(-94.17, -18.52) * mm, "end": v(-94.28, -18.59) * mm});
            skLineSegment(sketch, "E834", {"start": v(-94.28, -18.59) * mm, "end": v(-94.39, -18.67) * mm});
            skLineSegment(sketch, "E835", {"start": v(-94.39, -18.67) * mm, "end": v(-94.49, -18.75) * mm});
            skLineSegment(sketch, "E836", {"start": v(-94.49, -18.75) * mm, "end": v(-94.58, -18.85) * mm});
            skLineSegment(sketch, "E837", {"start": v(-94.58, -18.85) * mm, "end": v(-94.66, -18.95) * mm});
            skLineSegment(sketch, "E838", {"start": v(-94.66, -18.95) * mm, "end": v(-94.74, -19.06) * mm});
            skLineSegment(sketch, "E839", {"start": v(-94.74, -19.06) * mm, "end": v(-94.8, -19.18) * mm});
            skLineSegment(sketch, "E840", {"start": v(-94.8, -19.18) * mm, "end": v(-94.85, -19.3) * mm});
            skLineSegment(sketch, "E841", {"start": v(-94.85, -19.3) * mm, "end": v(-94.9, -19.43) * mm});
            skLineSegment(sketch, "E842", {"start": v(-94.9, -19.43) * mm, "end": v(-94.93, -19.56) * mm});
            skLineSegment(sketch, "E843", {"start": v(-94.93, -19.56) * mm, "end": v(-94.95, -19.7) * mm});
            skLineSegment(sketch, "E844", {"start": v(-94.95, -19.7) * mm, "end": v(-94.95, -19.84) * mm});
            skLineSegment(sketch, "E845", {"start": v(-94.95, -19.84) * mm, "end": v(-94.95, -23.36) * mm});
            skLineSegment(sketch, "E846", {"start": v(-94.95, -23.36) * mm, "end": v(-94.94, -23.68) * mm});
            skLineSegment(sketch, "E847", {"start": v(-94.94, -23.68) * mm, "end": v(-94.89, -23.99) * mm});
            skLineSegment(sketch, "E848", {"start": v(-94.89, -23.99) * mm, "end": v(-94.81, -24.29) * mm});
            skLineSegment(sketch, "E849", {"start": v(-94.81, -24.29) * mm, "end": v(-94.7, -24.57) * mm});
            skLineSegment(sketch, "E850", {"start": v(-94.7, -24.57) * mm, "end": v(-94.57, -24.85) * mm});
            skLineSegment(sketch, "E851", {"start": v(-94.57, -24.85) * mm, "end": v(-94.42, -25.1) * mm});
            skLineSegment(sketch, "E852", {"start": v(-94.42, -25.1) * mm, "end": v(-94.24, -25.35) * mm});
            skLineSegment(sketch, "E853", {"start": v(-94.24, -25.35) * mm, "end": v(-94.03, -25.57) * mm});
            skLineSegment(sketch, "E854", {"start": v(-94.03, -25.57) * mm, "end": v(-93.81, -25.77) * mm});
            skLineSegment(sketch, "E855", {"start": v(-93.81, -25.77) * mm, "end": v(-93.57, -25.95) * mm});
            skLineSegment(sketch, "E856", {"start": v(-93.57, -25.95) * mm, "end": v(-93.31, -26.11) * mm});
            skLineSegment(sketch, "E857", {"start": v(-93.31, -26.11) * mm, "end": v(-93.04, -26.24) * mm});
            skLineSegment(sketch, "E858", {"start": v(-93.04, -26.24) * mm, "end": v(-92.75, -26.35) * mm});
            skLineSegment(sketch, "E859", {"start": v(-92.75, -26.35) * mm, "end": v(-92.45, -26.42) * mm});
            skLineSegment(sketch, "E860", {"start": v(-92.45, -26.42) * mm, "end": v(-92.14, -26.47) * mm});
            skLineSegment(sketch, "E861", {"start": v(-92.14, -26.47) * mm, "end": v(-91.82, -26.49) * mm});
            skLineSegment(sketch, "E862", {"start": v(-91.82, -26.49) * mm, "end": v(-73.1, -26.44) * mm});
            skLineSegment(sketch, "E863", {"start": v(-73.1, -26.44) * mm, "end": v(-72.89, -26.43) * mm});
            skLineSegment(sketch, "E864", {"start": v(-72.89, -26.43) * mm, "end": v(-72.68, -26.42) * mm});
            skLineSegment(sketch, "E865", {"start": v(-72.68, -26.42) * mm, "end": v(-72.48, -26.4) * mm});
            skLineSegment(sketch, "E866", {"start": v(-72.48, -26.4) * mm, "end": v(-72.28, -26.37) * mm});
            skLineSegment(sketch, "E867", {"start": v(-72.28, -26.37) * mm, "end": v(-72.08, -26.33) * mm});
            skLineSegment(sketch, "E868", {"start": v(-72.08, -26.33) * mm, "end": v(-71.9, -26.28) * mm});
            skLineSegment(sketch, "E869", {"start": v(-71.9, -26.28) * mm, "end": v(-71.71, -26.22) * mm});
            skLineSegment(sketch, "E870", {"start": v(-71.71, -26.22) * mm, "end": v(-71.53, -26.16) * mm});
            skLineSegment(sketch, "E871", {"start": v(-71.53, -26.16) * mm, "end": v(-71.36, -26.08) * mm});
            skLineSegment(sketch, "E872", {"start": v(-71.36, -26.08) * mm, "end": v(-71.19, -26) * mm});
            skLineSegment(sketch, "E873", {"start": v(-71.19, -26) * mm, "end": v(-71.02, -25.9) * mm});
            skLineSegment(sketch, "E874", {"start": v(-71.02, -25.9) * mm, "end": v(-70.86, -25.8) * mm});
            skLineSegment(sketch, "E875", {"start": v(-70.86, -25.8) * mm, "end": v(-70.71, -25.7) * mm});
            skLineSegment(sketch, "E876", {"start": v(-70.71, -25.7) * mm, "end": v(-70.56, -25.58) * mm});
            skLineSegment(sketch, "E877", {"start": v(-70.56, -25.58) * mm, "end": v(-70.42, -25.46) * mm});
            skLineSegment(sketch, "E878", {"start": v(-70.42, -25.46) * mm, "end": v(-70.28, -25.32) * mm});
            skLineSegment(sketch, "E879", {"start": v(-70.28, -25.32) * mm, "end": v(-70.15, -25.18) * mm});
            skLineSegment(sketch, "E880", {"start": v(-70.15, -25.18) * mm, "end": v(-70.03, -25.03) * mm});
            skLineSegment(sketch, "E881", {"start": v(-70.03, -25.03) * mm, "end": v(-69.91, -24.88) * mm});
            skLineSegment(sketch, "E882", {"start": v(-69.91, -24.88) * mm, "end": v(-69.8, -24.73) * mm});
            skLineSegment(sketch, "E883", {"start": v(-69.8, -24.73) * mm, "end": v(-69.7, -24.56) * mm});
            skLineSegment(sketch, "E884", {"start": v(-69.7, -24.56) * mm, "end": v(-69.62, -24.4) * mm});
            skLineSegment(sketch, "E885", {"start": v(-69.62, -24.4) * mm, "end": v(-69.54, -24.23) * mm});
            skLineSegment(sketch, "E886", {"start": v(-69.54, -24.23) * mm, "end": v(-69.47, -24.05) * mm});
            skLineSegment(sketch, "E887", {"start": v(-69.47, -24.05) * mm, "end": v(-69.4, -23.87) * mm});
            skLineSegment(sketch, "E888", {"start": v(-69.4, -23.87) * mm, "end": v(-69.35, -23.69) * mm});
            skLineSegment(sketch, "E889", {"start": v(-69.35, -23.69) * mm, "end": v(-69.3, -23.5) * mm});
            skLineSegment(sketch, "E890", {"start": v(-69.3, -23.5) * mm, "end": v(-69.26, -23.3) * mm});
            skLineSegment(sketch, "E891", {"start": v(-69.26, -23.3) * mm, "end": v(-69.23, -23.1) * mm});
            skLineSegment(sketch, "E892", {"start": v(-69.23, -23.1) * mm, "end": v(-69.21, -22.9) * mm});
            skLineSegment(sketch, "E893", {"start": v(-69.21, -22.9) * mm, "end": v(-69.2, -22.69) * mm});
            skLineSegment(sketch, "E894", {"start": v(-69.2, -22.69) * mm, "end": v(-69.2, -22.47) * mm});
            skLineSegment(sketch, "E895", {"start": v(-69.2, -22.47) * mm, "end": v(-69.2, 6.62) * mm});
            skLineSegment(sketch, "E896", {"start": v(-69.2, 6.62) * mm, "end": v(-69.2, 6.66) * mm});
            skLineSegment(sketch, "E897", {"start": v(-69.2, 6.66) * mm, "end": v(-69.18, 6.7) * mm});
            skLineSegment(sketch, "E898", {"start": v(-69.18, 6.7) * mm, "end": v(-69.17, 6.74) * mm});
            skLineSegment(sketch, "E899", {"start": v(-69.17, 6.74) * mm, "end": v(-69.16, 6.78) * mm});
            skLineSegment(sketch, "E900", {"start": v(-69.16, 6.78) * mm, "end": v(-69.14, 6.81) * mm});
            skLineSegment(sketch, "E901", {"start": v(-69.14, 6.81) * mm, "end": v(-69.12, 6.84) * mm});
            skLineSegment(sketch, "E902", {"start": v(-69.12, 6.84) * mm, "end": v(-69.1, 6.87) * mm});
            skLineSegment(sketch, "E903", {"start": v(-69.1, 6.87) * mm, "end": v(-69.07, 6.9) * mm});
            skLineSegment(sketch, "E904", {"start": v(-69.07, 6.9) * mm, "end": v(-69.05, 6.92) * mm});
            skLineSegment(sketch, "E905", {"start": v(-69.05, 6.92) * mm, "end": v(-69.02, 6.93) * mm});
            skLineSegment(sketch, "E906", {"start": v(-69.02, 6.93) * mm, "end": v(-68.99, 6.95) * mm});
            skLineSegment(sketch, "E907", {"start": v(-68.99, 6.95) * mm, "end": v(-68.95, 6.96) * mm});
            skLineSegment(sketch, "E908", {"start": v(-68.95, 6.96) * mm, "end": v(-68.92, 6.98) * mm});
            skLineSegment(sketch, "E909", {"start": v(-68.92, 6.98) * mm, "end": v(-68.89, 6.98) * mm});
            skLineSegment(sketch, "E910", {"start": v(-68.89, 6.98) * mm, "end": v(-68.85, 6.99) * mm});
            skLineSegment(sketch, "E911", {"start": v(-68.85, 6.99) * mm, "end": v(-68.82, 6.99) * mm});
            skLineSegment(sketch, "E912", {"start": v(-68.82, 6.99) * mm, "end": v(-68.8, 6.99) * mm});
            skLineSegment(sketch, "E913", {"start": v(-68.8, 6.99) * mm, "end": v(-68.77, 6.99) * mm});
            skLineSegment(sketch, "E914", {"start": v(-68.77, 6.99) * mm, "end": v(-68.74, 6.98) * mm});
            skLineSegment(sketch, "E915", {"start": v(-68.74, 6.98) * mm, "end": v(-68.72, 6.97) * mm});
            skLineSegment(sketch, "E916", {"start": v(-68.72, 6.97) * mm, "end": v(-68.7, 6.97) * mm});
            skLineSegment(sketch, "E917", {"start": v(-68.7, 6.97) * mm, "end": v(-68.67, 6.96) * mm});
            skLineSegment(sketch, "E918", {"start": v(-68.67, 6.96) * mm, "end": v(-68.65, 6.95) * mm});
            skLineSegment(sketch, "E919", {"start": v(-68.65, 6.95) * mm, "end": v(-68.63, 6.94) * mm});
            skLineSegment(sketch, "E920", {"start": v(-68.63, 6.94) * mm, "end": v(-68.6, 6.92) * mm});
            skLineSegment(sketch, "E921", {"start": v(-68.6, 6.92) * mm, "end": v(-68.6, 6.9) * mm});
            skLineSegment(sketch, "E922", {"start": v(-68.6, 6.9) * mm, "end": v(-68.57, 6.89) * mm});
            skLineSegment(sketch, "E923", {"start": v(-68.57, 6.89) * mm, "end": v(-68.55, 6.87) * mm});
            skLineSegment(sketch, "E924", {"start": v(-68.55, 6.87) * mm, "end": v(-68.54, 6.85) * mm});
            skLineSegment(sketch, "E925", {"start": v(-68.54, 6.85) * mm, "end": v(-68.52, 6.83) * mm});
            skLineSegment(sketch, "E926", {"start": v(-68.52, 6.83) * mm, "end": v(-68.5, 6.8) * mm});
            skLineSegment(sketch, "E927", {"start": v(-68.5, 6.8) * mm, "end": v(-68.5, 6.79) * mm});
            skLineSegment(sketch, "E928", {"start": v(-68.5, 6.79) * mm, "end": v(-52.2, -25.59) * mm});
            skLineSegment(sketch, "E929", {"start": v(-52.2, -25.59) * mm, "end": v(-52.14, -25.69) * mm});
            skLineSegment(sketch, "E930", {"start": v(-52.14, -25.69) * mm, "end": v(-52.08, -25.78) * mm});
            skLineSegment(sketch, "E931", {"start": v(-52.08, -25.78) * mm, "end": v(-52, -25.88) * mm});
            skLineSegment(sketch, "E932", {"start": v(-52, -25.88) * mm, "end": v(-51.93, -25.96) * mm});
            skLineSegment(sketch, "E933", {"start": v(-51.93, -25.96) * mm, "end": v(-51.86, -26.04) * mm});
            skLineSegment(sketch, "E934", {"start": v(-51.86, -26.04) * mm, "end": v(-51.77, -26.12) * mm});
            skLineSegment(sketch, "E935", {"start": v(-51.77, -26.12) * mm, "end": v(-51.68, -26.18) * mm});
            skLineSegment(sketch, "E936", {"start": v(-51.68, -26.18) * mm, "end": v(-51.6, -26.25) * mm});
            skLineSegment(sketch, "E937", {"start": v(-51.6, -26.25) * mm, "end": v(-51.5, -26.3) * mm});
            skLineSegment(sketch, "E938", {"start": v(-51.5, -26.3) * mm, "end": v(-51.4, -26.35) * mm});
            skLineSegment(sketch, "E939", {"start": v(-51.4, -26.35) * mm, "end": v(-51.29, -26.4) * mm});
            skLineSegment(sketch, "E940", {"start": v(-51.29, -26.4) * mm, "end": v(-51.18, -26.43) * mm});
            skLineSegment(sketch, "E941", {"start": v(-51.18, -26.43) * mm, "end": v(-51.07, -26.45) * mm});
            skLineSegment(sketch, "E942", {"start": v(-51.07, -26.45) * mm, "end": v(-50.96, -26.47) * mm});
            skLineSegment(sketch, "E943", {"start": v(-50.96, -26.47) * mm, "end": v(-50.85, -26.48) * mm});
            skLineSegment(sketch, "E944", {"start": v(-50.85, -26.48) * mm, "end": v(-50.73, -26.49) * mm});
            skLineSegment(sketch, "E945", {"start": v(-50.73, -26.49) * mm, "end": v(-50.6, -26.48) * mm});
            skLineSegment(sketch, "E946", {"start": v(-50.6, -26.48) * mm, "end": v(-50.46, -26.46) * mm});
            skLineSegment(sketch, "E947", {"start": v(-50.46, -26.46) * mm, "end": v(-50.34, -26.43) * mm});
            skLineSegment(sketch, "E948", {"start": v(-50.34, -26.43) * mm, "end": v(-50.21, -26.38) * mm});
            skLineSegment(sketch, "E949", {"start": v(-50.21, -26.38) * mm, "end": v(-50.1, -26.33) * mm});
            skLineSegment(sketch, "E950", {"start": v(-50.1, -26.33) * mm, "end": v(-49.99, -26.26) * mm});
            skLineSegment(sketch, "E951", {"start": v(-49.99, -26.26) * mm, "end": v(-49.89, -26.19) * mm});
            skLineSegment(sketch, "E952", {"start": v(-49.89, -26.19) * mm, "end": v(-49.8, -26.1) * mm});
            skLineSegment(sketch, "E953", {"start": v(-49.8, -26.1) * mm, "end": v(-49.7, -26) * mm});
            skLineSegment(sketch, "E954", {"start": v(-49.7, -26) * mm, "end": v(-49.63, -25.9) * mm});
            skLineSegment(sketch, "E955", {"start": v(-49.63, -25.9) * mm, "end": v(-49.56, -25.8) * mm});
            skLineSegment(sketch, "E956", {"start": v(-49.56, -25.8) * mm, "end": v(-49.5, -25.68) * mm});
            skLineSegment(sketch, "E957", {"start": v(-49.5, -25.68) * mm, "end": v(-49.46, -25.56) * mm});
            skLineSegment(sketch, "E958", {"start": v(-49.46, -25.56) * mm, "end": v(-49.43, -25.43) * mm});
            skLineSegment(sketch, "E959", {"start": v(-49.43, -25.43) * mm, "end": v(-49.4, -25.3) * mm});
            skLineSegment(sketch, "E960", {"start": v(-49.4, -25.3) * mm, "end": v(-49.4, -25.16) * mm});
            skLineSegment(sketch, "E961", {"start": v(-49.4, -25.16) * mm, "end": v(-49.4, 11.98) * mm});
            skLineSegment(sketch, "E962", {"start": v(-49.4, 11.98) * mm, "end": v(-49.4, 12.1) * mm});
            skLineSegment(sketch, "E963", {"start": v(-49.4, 12.1) * mm, "end": v(-49.39, 12.22) * mm});
            skLineSegment(sketch, "E964", {"start": v(-49.39, 12.22) * mm, "end": v(-49.37, 12.33) * mm});
            skLineSegment(sketch, "E965", {"start": v(-49.37, 12.33) * mm, "end": v(-49.35, 12.43) * mm});
            skLineSegment(sketch, "E966", {"start": v(-49.35, 12.43) * mm, "end": v(-49.31, 12.52) * mm});
            skLineSegment(sketch, "E967", {"start": v(-49.31, 12.52) * mm, "end": v(-49.28, 12.6) * mm});
            skLineSegment(sketch, "E968", {"start": v(-49.28, 12.6) * mm, "end": v(-49.23, 12.67) * mm});
            skLineSegment(sketch, "E969", {"start": v(-49.23, 12.67) * mm, "end": v(-49.17, 12.74) * mm});
            skLineSegment(sketch, "E970", {"start": v(-49.17, 12.74) * mm, "end": v(-49.11, 12.8) * mm});
            skLineSegment(sketch, "E971", {"start": v(-49.11, 12.8) * mm, "end": v(-49.04, 12.85) * mm});
            skLineSegment(sketch, "E972", {"start": v(-49.04, 12.85) * mm, "end": v(-48.97, 12.9) * mm});
            skLineSegment(sketch, "E973", {"start": v(-48.97, 12.9) * mm, "end": v(-48.88, 12.93) * mm});
            skLineSegment(sketch, "E974", {"start": v(-48.88, 12.93) * mm, "end": v(-48.8, 12.95) * mm});
            skLineSegment(sketch, "E975", {"start": v(-48.8, 12.95) * mm, "end": v(-48.7, 12.97) * mm});
            skLineSegment(sketch, "E976", {"start": v(-48.7, 12.97) * mm, "end": v(-48.59, 12.98) * mm});
            skLineSegment(sketch, "E977", {"start": v(-48.59, 12.98) * mm, "end": v(-48.47, 12.99) * mm});
            skLineSegment(sketch, "E978", {"start": v(-48.47, 12.99) * mm, "end": v(-48.35, 12.98) * mm});
            skLineSegment(sketch, "E979", {"start": v(-48.35, 12.98) * mm, "end": v(-48.23, 12.97) * mm});
            skLineSegment(sketch, "E980", {"start": v(-48.23, 12.97) * mm, "end": v(-48.13, 12.95) * mm});
            skLineSegment(sketch, "E981", {"start": v(-48.13, 12.95) * mm, "end": v(-48.03, 12.93) * mm});
            skLineSegment(sketch, "E982", {"start": v(-48.03, 12.93) * mm, "end": v(-47.94, 12.9) * mm});
            skLineSegment(sketch, "E983", {"start": v(-47.94, 12.9) * mm, "end": v(-47.86, 12.85) * mm});
            skLineSegment(sketch, "E984", {"start": v(-47.86, 12.85) * mm, "end": v(-47.8, 12.8) * mm});
            skLineSegment(sketch, "E985", {"start": v(-47.8, 12.8) * mm, "end": v(-47.73, 12.74) * mm});
            skLineSegment(sketch, "E986", {"start": v(-47.73, 12.74) * mm, "end": v(-47.67, 12.67) * mm});
            skLineSegment(sketch, "E987", {"start": v(-47.67, 12.67) * mm, "end": v(-47.62, 12.6) * mm});
            skLineSegment(sketch, "E988", {"start": v(-47.62, 12.6) * mm, "end": v(-47.58, 12.52) * mm});
            skLineSegment(sketch, "E989", {"start": v(-47.58, 12.52) * mm, "end": v(-47.55, 12.43) * mm});
            skLineSegment(sketch, "E990", {"start": v(-47.55, 12.43) * mm, "end": v(-47.52, 12.33) * mm});
            skLineSegment(sketch, "E991", {"start": v(-47.52, 12.33) * mm, "end": v(-47.5, 12.22) * mm});
            skLineSegment(sketch, "E992", {"start": v(-47.5, 12.22) * mm, "end": v(-47.49, 12.1) * mm});
            skLineSegment(sketch, "E993", {"start": v(-47.49, 12.1) * mm, "end": v(-47.49, 11.98) * mm});
            skLineSegment(sketch, "E994", {"start": v(-47.49, 11.98) * mm, "end": v(-47.49, -22.43) * mm});
            skLineSegment(sketch, "E995", {"start": v(-47.49, -22.43) * mm, "end": v(-47.47, -22.85) * mm});
            skLineSegment(sketch, "E996", {"start": v(-47.47, -22.85) * mm, "end": v(-47.42, -23.26) * mm});
            skLineSegment(sketch, "E997", {"start": v(-47.42, -23.26) * mm, "end": v(-47.35, -23.64) * mm});
            skLineSegment(sketch, "E998", {"start": v(-47.35, -23.64) * mm, "end": v(-47.24, -24) * mm});
            skLineSegment(sketch, "E999", {"start": v(-47.24, -24) * mm, "end": v(-47.1, -24.32) * mm});
            skLineSegment(sketch, "E1000", {"start": v(-47.1, -24.32) * mm, "end": v(-46.93, -24.63) * mm});
            skLineSegment(sketch, "E1001", {"start": v(-46.93, -24.63) * mm, "end": v(-46.73, -24.91) * mm});
            skLineSegment(sketch, "E1002", {"start": v(-46.73, -24.91) * mm, "end": v(-46.5, -25.17) * mm});
            skLineSegment(sketch, "E1003", {"start": v(-46.5, -25.17) * mm, "end": v(-46.24, -25.4) * mm});
            skLineSegment(sketch, "E1004", {"start": v(-46.24, -25.4) * mm, "end": v(-45.95, -25.62) * mm});
            skLineSegment(sketch, "E1005", {"start": v(-45.95, -25.62) * mm, "end": v(-45.63, -25.8) * mm});
            skLineSegment(sketch, "E1006", {"start": v(-45.63, -25.8) * mm, "end": v(-45.28, -25.97) * mm});
            skLineSegment(sketch, "E1007", {"start": v(-45.28, -25.97) * mm, "end": v(-44.9, -26.11) * mm});
            skLineSegment(sketch, "E1008", {"start": v(-44.9, -26.11) * mm, "end": v(-44.49, -26.23) * mm});
            skLineSegment(sketch, "E1009", {"start": v(-44.49, -26.23) * mm, "end": v(-44.04, -26.32) * mm});
            skLineSegment(sketch, "E1010", {"start": v(-44.04, -26.32) * mm, "end": v(-43.57, -26.38) * mm});
            skLineSegment(sketch, "E1011", {"start": v(-43.57, -26.38) * mm, "end": v(-40.67, -26.49) * mm});
            skLineSegment(sketch, "E1012", {"start": v(-40.67, -26.49) * mm, "end": v(-40.45, -26.48) * mm});
            skLineSegment(sketch, "E1013", {"start": v(-40.45, -26.48) * mm, "end": v(-40.24, -26.47) * mm});
            skLineSegment(sketch, "E1014", {"start": v(-40.24, -26.47) * mm, "end": v(-40.04, -26.45) * mm});
            skLineSegment(sketch, "E1015", {"start": v(-40.04, -26.45) * mm, "end": v(-39.84, -26.42) * mm});
            skLineSegment(sketch, "E1016", {"start": v(-39.84, -26.42) * mm, "end": v(-39.64, -26.38) * mm});
            skLineSegment(sketch, "E1017", {"start": v(-39.64, -26.38) * mm, "end": v(-39.45, -26.33) * mm});
            skLineSegment(sketch, "E1018", {"start": v(-39.45, -26.33) * mm, "end": v(-39.27, -26.27) * mm});
            skLineSegment(sketch, "E1019", {"start": v(-39.27, -26.27) * mm, "end": v(-39.09, -26.2) * mm});
            skLineSegment(sketch, "E1020", {"start": v(-39.09, -26.2) * mm, "end": v(-38.91, -26.13) * mm});
            skLineSegment(sketch, "E1021", {"start": v(-38.91, -26.13) * mm, "end": v(-38.74, -26.05) * mm});
            skLineSegment(sketch, "E1022", {"start": v(-38.74, -26.05) * mm, "end": v(-38.57, -25.96) * mm});
            skLineSegment(sketch, "E1023", {"start": v(-38.57, -25.96) * mm, "end": v(-38.41, -25.86) * mm});
            skLineSegment(sketch, "E1024", {"start": v(-38.41, -25.86) * mm, "end": v(-38.26, -25.75) * mm});
            skLineSegment(sketch, "E1025", {"start": v(-38.26, -25.75) * mm, "end": v(-38.1, -25.63) * mm});
            skLineSegment(sketch, "E1026", {"start": v(-38.1, -25.63) * mm, "end": v(-37.96, -25.5) * mm});
            skLineSegment(sketch, "E1027", {"start": v(-37.96, -25.5) * mm, "end": v(-37.82, -25.37) * mm});
            skLineSegment(sketch, "E1028", {"start": v(-37.82, -25.37) * mm, "end": v(-37.68, -25.23) * mm});
            skLineSegment(sketch, "E1029", {"start": v(-37.68, -25.23) * mm, "end": v(-37.56, -25.09) * mm});
            skLineSegment(sketch, "E1030", {"start": v(-37.56, -25.09) * mm, "end": v(-37.44, -24.94) * mm});
            skLineSegment(sketch, "E1031", {"start": v(-37.44, -24.94) * mm, "end": v(-37.33, -24.78) * mm});
            skLineSegment(sketch, "E1032", {"start": v(-37.33, -24.78) * mm, "end": v(-37.23, -24.62) * mm});
            skLineSegment(sketch, "E1033", {"start": v(-37.23, -24.62) * mm, "end": v(-37.14, -24.45) * mm});
            skLineSegment(sketch, "E1034", {"start": v(-37.14, -24.45) * mm, "end": v(-37.06, -24.28) * mm});
            skLineSegment(sketch, "E1035", {"start": v(-37.06, -24.28) * mm, "end": v(-36.98, -24.1) * mm});
            skLineSegment(sketch, "E1036", {"start": v(-36.98, -24.1) * mm, "end": v(-36.92, -23.92) * mm});
            skLineSegment(sketch, "E1037", {"start": v(-36.92, -23.92) * mm, "end": v(-36.86, -23.74) * mm});
            skLineSegment(sketch, "E1038", {"start": v(-36.86, -23.74) * mm, "end": v(-36.81, -23.55) * mm});
            skLineSegment(sketch, "E1039", {"start": v(-36.81, -23.55) * mm, "end": v(-36.77, -23.35) * mm});
            skLineSegment(sketch, "E1040", {"start": v(-36.77, -23.35) * mm, "end": v(-36.74, -23.15) * mm});
            skLineSegment(sketch, "E1041", {"start": v(-36.74, -23.15) * mm, "end": v(-36.72, -22.95) * mm});
            skLineSegment(sketch, "E1042", {"start": v(-36.72, -22.95) * mm, "end": v(-36.7, -22.74) * mm});
            skLineSegment(sketch, "E1043", {"start": v(-36.7, -22.74) * mm, "end": v(-36.7, -22.53) * mm});
            skLineSegment(sketch, "E1044", {"start": v(-36.7, -22.53) * mm, "end": v(-36.7, 12.27) * mm});
            skLineSegment(sketch, "E1045", {"start": v(-36.7, 12.27) * mm, "end": v(-36.7, 12.34) * mm});
            skLineSegment(sketch, "E1046", {"start": v(-36.7, 12.34) * mm, "end": v(-36.69, 12.42) * mm});
            skLineSegment(sketch, "E1047", {"start": v(-36.69, 12.42) * mm, "end": v(-36.67, 12.5) * mm});
            skLineSegment(sketch, "E1048", {"start": v(-36.67, 12.5) * mm, "end": v(-36.64, 12.57) * mm});
            skLineSegment(sketch, "E1049", {"start": v(-36.64, 12.57) * mm, "end": v(-36.6, 12.63) * mm});
            skLineSegment(sketch, "E1050", {"start": v(-36.6, 12.63) * mm, "end": v(-36.57, 12.7) * mm});
            skLineSegment(sketch, "E1051", {"start": v(-36.57, 12.7) * mm, "end": v(-36.53, 12.76) * mm});
            skLineSegment(sketch, "E1052", {"start": v(-36.53, 12.76) * mm, "end": v(-36.48, 12.81) * mm});
            skLineSegment(sketch, "E1053", {"start": v(-36.48, 12.81) * mm, "end": v(-36.42, 12.86) * mm});
            skLineSegment(sketch, "E1054", {"start": v(-36.42, 12.86) * mm, "end": v(-36.36, 12.9) * mm});
            skLineSegment(sketch, "E1055", {"start": v(-36.36, 12.9) * mm, "end": v(-36.3, 12.95) * mm});
            skLineSegment(sketch, "E1056", {"start": v(-36.3, 12.95) * mm, "end": v(-36.23, 12.98) * mm});
            skLineSegment(sketch, "E1057", {"start": v(-36.23, 12.98) * mm, "end": v(-36.16, 13) * mm});
            skLineSegment(sketch, "E1058", {"start": v(-36.16, 13) * mm, "end": v(-36.08, 13.02) * mm});
            skLineSegment(sketch, "E1059", {"start": v(-36.08, 13.02) * mm, "end": v(-36, 13.04) * mm});
            skLineSegment(sketch, "E1060", {"start": v(-36, 13.04) * mm, "end": v(-35.93, 13.04) * mm});
            skLineSegment(sketch, "E1061", {"start": v(-35.93, 13.04) * mm, "end": v(-23.09, 13.04) * mm});
            skLineSegment(sketch, "E1062", {"start": v(-23.09, 13.04) * mm, "end": v(-22.82, 13.02) * mm});
            skLineSegment(sketch, "E1063", {"start": v(-22.82, 13.02) * mm, "end": v(-22.54, 13) * mm});
            skLineSegment(sketch, "E1064", {"start": v(-22.54, 13) * mm, "end": v(-22.27, 12.97) * mm});
            skLineSegment(sketch, "E1065", {"start": v(-22.27, 12.97) * mm, "end": v(-22, 12.93) * mm});
            skLineSegment(sketch, "E1066", {"start": v(-22, 12.93) * mm, "end": v(-21.72, 12.88) * mm});
            skLineSegment(sketch, "E1067", {"start": v(-21.72, 12.88) * mm, "end": v(-21.45, 12.83) * mm});
            skLineSegment(sketch, "E1068", {"start": v(-21.45, 12.83) * mm, "end": v(-21.18, 12.76) * mm});
            skLineSegment(sketch, "E1069", {"start": v(-21.18, 12.76) * mm, "end": v(-20.9, 12.7) * mm});
            skLineSegment(sketch, "E1070", {"start": v(-20.9, 12.7) * mm, "end": v(-20.63, 12.6) * mm});
            skLineSegment(sketch, "E1071", {"start": v(-20.63, 12.6) * mm, "end": v(-20.36, 12.52) * mm});
            skLineSegment(sketch, "E1072", {"start": v(-20.36, 12.52) * mm, "end": v(-20.1, 12.42) * mm});
            skLineSegment(sketch, "E1073", {"start": v(-20.1, 12.42) * mm, "end": v(-19.82, 12.31) * mm});
            skLineSegment(sketch, "E1074", {"start": v(-19.82, 12.31) * mm, "end": v(-19.55, 12.2) * mm});
            skLineSegment(sketch, "E1075", {"start": v(-19.55, 12.2) * mm, "end": v(-19.28, 12.07) * mm});
            skLineSegment(sketch, "E1076", {"start": v(-19.28, 12.07) * mm, "end": v(-19.02, 11.94) * mm});
            skLineSegment(sketch, "E1077", {"start": v(-19.02, 11.94) * mm, "end": v(-18.53, 11.67) * mm});
            skLineSegment(sketch, "E1078", {"start": v(-18.53, 11.67) * mm, "end": v(-18.08, 11.37) * mm});
            skLineSegment(sketch, "E1079", {"start": v(-18.08, 11.37) * mm, "end": v(-17.65, 11.05) * mm});
            skLineSegment(sketch, "E1080", {"start": v(-17.65, 11.05) * mm, "end": v(-17.26, 10.7) * mm});
            skLineSegment(sketch, "E1081", {"start": v(-17.26, 10.7) * mm, "end": v(-16.9, 10.33) * mm});
            skLineSegment(sketch, "E1082", {"start": v(-16.9, 10.33) * mm, "end": v(-16.57, 9.94) * mm});
            skLineSegment(sketch, "E1083", {"start": v(-16.57, 9.94) * mm, "end": v(-16.27, 9.52) * mm});
            skLineSegment(sketch, "E1084", {"start": v(-16.27, 9.52) * mm, "end": v(-16, 9.08) * mm});
            skLineSegment(sketch, "E1085", {"start": v(-16, 9.08) * mm, "end": v(-15.77, 8.6) * mm});
            skLineSegment(sketch, "E1086", {"start": v(-15.77, 8.6) * mm, "end": v(-15.56, 8.12) * mm});
            skLineSegment(sketch, "E1087", {"start": v(-15.56, 8.12) * mm, "end": v(-15.4, 7.6) * mm});
            skLineSegment(sketch, "E1088", {"start": v(-15.4, 7.6) * mm, "end": v(-15.25, 7.06) * mm});
            skLineSegment(sketch, "E1089", {"start": v(-15.25, 7.06) * mm, "end": v(-15.14, 6.5) * mm});
            skLineSegment(sketch, "E1090", {"start": v(-15.14, 6.5) * mm, "end": v(-15.06, 5.92) * mm});
            skLineSegment(sketch, "E1091", {"start": v(-15.06, 5.92) * mm, "end": v(-15.01, 5.3) * mm});
            skLineSegment(sketch, "E1092", {"start": v(-15.01, 5.3) * mm, "end": v(-15, 4.67) * mm});
            skLineSegment(sketch, "E1093", {"start": v(-15, 4.67) * mm, "end": v(-15.01, 4.04) * mm});
            skLineSegment(sketch, "E1094", {"start": v(-15.01, 4.04) * mm, "end": v(-15.06, 3.43) * mm});
            skLineSegment(sketch, "E1095", {"start": v(-15.06, 3.43) * mm, "end": v(-15.14, 2.85) * mm});
            skLineSegment(sketch, "E1096", {"start": v(-15.14, 2.85) * mm, "end": v(-15.25, 2.28) * mm});
            skLineSegment(sketch, "E1097", {"start": v(-15.25, 2.28) * mm, "end": v(-15.4, 1.74) * mm});
            skLineSegment(sketch, "E1098", {"start": v(-15.4, 1.74) * mm, "end": v(-15.56, 1.23) * mm});
            skLineSegment(sketch, "E1099", {"start": v(-15.56, 1.23) * mm, "end": v(-15.77, 0.74) * mm});
            skLineSegment(sketch, "E1100", {"start": v(-15.77, 0.74) * mm, "end": v(-16, 0.27) * mm});
            skLineSegment(sketch, "E1101", {"start": v(-16, 0.27) * mm, "end": v(-16.27, -0.17) * mm});
            skLineSegment(sketch, "E1102", {"start": v(-16.27, -0.17) * mm, "end": v(-16.57, -0.6) * mm});
            skLineSegment(sketch, "E1103", {"start": v(-16.57, -0.6) * mm, "end": v(-16.9, -0.99) * mm});
            skLineSegment(sketch, "E1104", {"start": v(-16.9, -0.99) * mm, "end": v(-17.26, -1.36) * mm});
            skLineSegment(sketch, "E1105", {"start": v(-17.26, -1.36) * mm, "end": v(-17.65, -1.7) * mm});
            skLineSegment(sketch, "E1106", {"start": v(-17.65, -1.7) * mm, "end": v(-18.08, -2.02) * mm});
            skLineSegment(sketch, "E1107", {"start": v(-18.08, -2.02) * mm, "end": v(-18.53, -2.32) * mm});
            skLineSegment(sketch, "E1108", {"start": v(-18.53, -2.32) * mm, "end": v(-19.02, -2.6) * mm});
            skLineSegment(sketch, "E1109", {"start": v(-19.02, -2.6) * mm, "end": v(-19.3, -2.73) * mm});
            skLineSegment(sketch, "E1110", {"start": v(-19.3, -2.73) * mm, "end": v(-19.57, -2.86) * mm});
            skLineSegment(sketch, "E1111", {"start": v(-19.57, -2.86) * mm, "end": v(-19.85, -2.98) * mm});
            skLineSegment(sketch, "E1112", {"start": v(-19.85, -2.98) * mm, "end": v(-20.13, -3.1) * mm});
            skLineSegment(sketch, "E1113", {"start": v(-20.13, -3.1) * mm, "end": v(-20.4, -3.2) * mm});
            skLineSegment(sketch, "E1114", {"start": v(-20.4, -3.2) * mm, "end": v(-20.68, -3.3) * mm});
            skLineSegment(sketch, "E1115", {"start": v(-20.68, -3.3) * mm, "end": v(-20.96, -3.38) * mm});
            skLineSegment(sketch, "E1116", {"start": v(-20.96, -3.38) * mm, "end": v(-21.23, -3.46) * mm});
            skLineSegment(sketch, "E1117", {"start": v(-21.23, -3.46) * mm, "end": v(-21.5, -3.52) * mm});
            skLineSegment(sketch, "E1118", {"start": v(-21.5, -3.52) * mm, "end": v(-21.77, -3.58) * mm});
            skLineSegment(sketch, "E1119", {"start": v(-21.77, -3.58) * mm, "end": v(-22.04, -3.63) * mm});
            skLineSegment(sketch, "E1120", {"start": v(-22.04, -3.63) * mm, "end": v(-22.3, -3.67) * mm});
            skLineSegment(sketch, "E1121", {"start": v(-22.3, -3.67) * mm, "end": v(-22.57, -3.7) * mm});
            skLineSegment(sketch, "E1122", {"start": v(-22.57, -3.7) * mm, "end": v(-22.84, -3.73) * mm});
            skLineSegment(sketch, "E1123", {"start": v(-22.84, -3.73) * mm, "end": v(-23.1, -3.74) * mm});
            skLineSegment(sketch, "E1124", {"start": v(-23.1, -3.74) * mm, "end": v(-33.04, -3.75) * mm});
            skLineSegment(sketch, "E1125", {"start": v(-33.04, -3.75) * mm, "end": v(-33.16, -3.75) * mm});
            skLineSegment(sketch, "E1126", {"start": v(-33.16, -3.75) * mm, "end": v(-33.27, -3.77) * mm});
            skLineSegment(sketch, "E1127", {"start": v(-33.27, -3.77) * mm, "end": v(-33.39, -3.8) * mm});
            skLineSegment(sketch, "E1128", {"start": v(-33.39, -3.8) * mm, "end": v(-33.5, -3.84) * mm});
            skLineSegment(sketch, "E1129", {"start": v(-33.5, -3.84) * mm, "end": v(-33.6, -3.89) * mm});
            skLineSegment(sketch, "E1130", {"start": v(-33.6, -3.89) * mm, "end": v(-33.7, -3.95) * mm});
            skLineSegment(sketch, "E1131", {"start": v(-33.7, -3.95) * mm, "end": v(-33.78, -4.01) * mm});
            skLineSegment(sketch, "E1132", {"start": v(-33.78, -4.01) * mm, "end": v(-33.86, -4.09) * mm});
            skLineSegment(sketch, "E1133", {"start": v(-33.86, -4.09) * mm, "end": v(-33.94, -4.17) * mm});
            skLineSegment(sketch, "E1134", {"start": v(-33.94, -4.17) * mm, "end": v(-34, -4.26) * mm});
            skLineSegment(sketch, "E1135", {"start": v(-34, -4.26) * mm, "end": v(-34.06, -4.36) * mm});
            skLineSegment(sketch, "E1136", {"start": v(-34.06, -4.36) * mm, "end": v(-34.11, -4.46) * mm});
            skLineSegment(sketch, "E1137", {"start": v(-34.11, -4.46) * mm, "end": v(-34.15, -4.57) * mm});
            skLineSegment(sketch, "E1138", {"start": v(-34.15, -4.57) * mm, "end": v(-34.18, -4.68) * mm});
            skLineSegment(sketch, "E1139", {"start": v(-34.18, -4.68) * mm, "end": v(-34.2, -4.8) * mm});
            skLineSegment(sketch, "E1140", {"start": v(-34.2, -4.8) * mm, "end": v(-34.2, -4.91) * mm});
            skLineSegment(sketch, "E1141", {"start": v(-34.2, -4.91) * mm, "end": v(-34.2, -5.74) * mm});
            skLineSegment(sketch, "E1142", {"start": v(-34.2, -5.74) * mm, "end": v(-34.2, -5.82) * mm});
            skLineSegment(sketch, "E1143", {"start": v(-34.2, -5.82) * mm, "end": v(-34.2, -5.9) * mm});
            skLineSegment(sketch, "E1144", {"start": v(-34.2, -5.9) * mm, "end": v(-34.19, -5.98) * mm});
            skLineSegment(sketch, "E1145", {"start": v(-34.19, -5.98) * mm, "end": v(-34.17, -6.06) * mm});
            skLineSegment(sketch, "E1146", {"start": v(-34.17, -6.06) * mm, "end": v(-34.15, -6.14) * mm});
            skLineSegment(sketch, "E1147", {"start": v(-34.15, -6.14) * mm, "end": v(-34.13, -6.22) * mm});
            skLineSegment(sketch, "E1148", {"start": v(-34.13, -6.22) * mm, "end": v(-34.1, -6.3) * mm});
            skLineSegment(sketch, "E1149", {"start": v(-34.1, -6.3) * mm, "end": v(-34.08, -6.37) * mm});
            skLineSegment(sketch, "E1150", {"start": v(-34.08, -6.37) * mm, "end": v(-34.04, -6.45) * mm});
            skLineSegment(sketch, "E1151", {"start": v(-34.04, -6.45) * mm, "end": v(-34, -6.52) * mm});
            skLineSegment(sketch, "E1152", {"start": v(-34, -6.52) * mm, "end": v(-33.97, -6.6) * mm});
            skLineSegment(sketch, "E1153", {"start": v(-33.97, -6.6) * mm, "end": v(-33.92, -6.66) * mm});
            skLineSegment(sketch, "E1154", {"start": v(-33.92, -6.66) * mm, "end": v(-33.88, -6.73) * mm});
            skLineSegment(sketch, "E1155", {"start": v(-33.88, -6.73) * mm, "end": v(-33.83, -6.8) * mm});
            skLineSegment(sketch, "E1156", {"start": v(-33.83, -6.8) * mm, "end": v(-33.77, -6.86) * mm});
            skLineSegment(sketch, "E1157", {"start": v(-33.77, -6.86) * mm, "end": v(-33.72, -6.91) * mm});
            skLineSegment(sketch, "E1158", {"start": v(-33.72, -6.91) * mm, "end": v(-14.92, -25.66) * mm});
            skLineSegment(sketch, "E1159", {"start": v(-14.92, -25.66) * mm, "end": v(-14.82, -25.76) * mm});
            skLineSegment(sketch, "E1160", {"start": v(-14.82, -25.76) * mm, "end": v(-14.7, -25.85) * mm});
            skLineSegment(sketch, "E1161", {"start": v(-14.7, -25.85) * mm, "end": v(-14.6, -25.94) * mm});
            skLineSegment(sketch, "E1162", {"start": v(-14.6, -25.94) * mm, "end": v(-14.49, -26.02) * mm});
            skLineSegment(sketch, "E1163", {"start": v(-14.49, -26.02) * mm, "end": v(-14.37, -26.1) * mm});
            skLineSegment(sketch, "E1164", {"start": v(-14.37, -26.1) * mm, "end": v(-14.25, -26.16) * mm});
            skLineSegment(sketch, "E1165", {"start": v(-14.25, -26.16) * mm, "end": v(-14.13, -26.22) * mm});
            skLineSegment(sketch, "E1166", {"start": v(-14.13, -26.22) * mm, "end": v(-14, -26.28) * mm});
            skLineSegment(sketch, "E1167", {"start": v(-14, -26.28) * mm, "end": v(-13.87, -26.33) * mm});
            skLineSegment(sketch, "E1168", {"start": v(-13.87, -26.33) * mm, "end": v(-13.74, -26.37) * mm});
            skLineSegment(sketch, "E1169", {"start": v(-13.74, -26.37) * mm, "end": v(-13.61, -26.4) * mm});
            skLineSegment(sketch, "E1170", {"start": v(-13.61, -26.4) * mm, "end": v(-13.48, -26.43) * mm});
            skLineSegment(sketch, "E1171", {"start": v(-13.48, -26.43) * mm, "end": v(-13.34, -26.46) * mm});
            skLineSegment(sketch, "E1172", {"start": v(-13.34, -26.46) * mm, "end": v(-13.2, -26.48) * mm});
            skLineSegment(sketch, "E1173", {"start": v(-13.2, -26.48) * mm, "end": v(-13.06, -26.49) * mm});
            skLineSegment(sketch, "E1174", {"start": v(-13.06, -26.49) * mm, "end": v(-12.92, -26.49) * mm});
            skLineSegment(sketch, "E1175", {"start": v(-12.92, -26.49) * mm, "end": v(-7.66, -26.49) * mm});
            skLineSegment(sketch, "E1176", {"start": v(-7.66, -26.49) * mm, "end": v(-7.53, -26.48) * mm});
            skLineSegment(sketch, "E1177", {"start": v(-7.53, -26.48) * mm, "end": v(-7.4, -26.47) * mm});
            skLineSegment(sketch, "E1178", {"start": v(-7.4, -26.47) * mm, "end": v(-7.28, -26.45) * mm});
            skLineSegment(sketch, "E1179", {"start": v(-7.28, -26.45) * mm, "end": v(-7.15, -26.42) * mm});
            skLineSegment(sketch, "E1180", {"start": v(-7.15, -26.42) * mm, "end": v(-7.03, -26.38) * mm});
            skLineSegment(sketch, "E1181", {"start": v(-7.03, -26.38) * mm, "end": v(-6.92, -26.33) * mm});
            skLineSegment(sketch, "E1182", {"start": v(-6.92, -26.33) * mm, "end": v(-6.8, -26.28) * mm});
            skLineSegment(sketch, "E1183", {"start": v(-6.8, -26.28) * mm, "end": v(-6.7, -26.22) * mm});
            skLineSegment(sketch, "E1184", {"start": v(-6.7, -26.22) * mm, "end": v(-6.6, -26.15) * mm});
            skLineSegment(sketch, "E1185", {"start": v(-6.6, -26.15) * mm, "end": v(-6.5, -26.07) * mm});
            skLineSegment(sketch, "E1186", {"start": v(-6.5, -26.07) * mm, "end": v(-6.4, -25.99) * mm});
            skLineSegment(sketch, "E1187", {"start": v(-6.4, -25.99) * mm, "end": v(-6.3, -25.9) * mm});
            skLineSegment(sketch, "E1188", {"start": v(-6.3, -25.9) * mm, "end": v(-6.23, -25.8) * mm});
            skLineSegment(sketch, "E1189", {"start": v(-6.23, -25.8) * mm, "end": v(-6.15, -25.7) * mm});
            skLineSegment(sketch, "E1190", {"start": v(-6.15, -25.7) * mm, "end": v(-6.08, -25.59) * mm});
            skLineSegment(sketch, "E1191", {"start": v(-6.08, -25.59) * mm, "end": v(-6.02, -25.47) * mm});
            skLineSegment(sketch, "E1192", {"start": v(-6.02, -25.47) * mm, "end": v(12.19, 10.93) * mm});
            skLineSegment(sketch, "E1193", {"start": v(12.19, 10.93) * mm, "end": v(12.2, 10.95) * mm});
            skLineSegment(sketch, "E1194", {"start": v(12.2, 10.95) * mm, "end": v(12.2, 10.97) * mm});
            skLineSegment(sketch, "E1195", {"start": v(12.2, 10.97) * mm, "end": v(12.21, 10.98) * mm});
            skLineSegment(sketch, "E1196", {"start": v(12.21, 10.98) * mm, "end": v(12.22, 11) * mm});
            skLineSegment(sketch, "E1197", {"start": v(12.22, 11) * mm, "end": v(12.24, 11) * mm});
            skLineSegment(sketch, "E1198", {"start": v(12.24, 11) * mm, "end": v(12.25, 11.02) * mm});
            skLineSegment(sketch, "E1199", {"start": v(12.25, 11.02) * mm, "end": v(12.26, 11.03) * mm});
            skLineSegment(sketch, "E1200", {"start": v(12.26, 11.03) * mm, "end": v(12.28, 11.04) * mm});
            skLineSegment(sketch, "E1201", {"start": v(12.28, 11.04) * mm, "end": v(12.3, 11.04) * mm});
            skLineSegment(sketch, "E1202", {"start": v(12.3, 11.04) * mm, "end": v(12.3, 11.05) * mm});
            skLineSegment(sketch, "E1203", {"start": v(12.3, 11.05) * mm, "end": v(12.32, 11.06) * mm});
            skLineSegment(sketch, "E1204", {"start": v(12.32, 11.06) * mm, "end": v(12.34, 11.06) * mm});
            skLineSegment(sketch, "E1205", {"start": v(12.34, 11.06) * mm, "end": v(12.36, 11.07) * mm});
            skLineSegment(sketch, "E1206", {"start": v(12.36, 11.07) * mm, "end": v(12.37, 11.07) * mm});
            skLineSegment(sketch, "E1207", {"start": v(12.37, 11.07) * mm, "end": v(12.4, 11.07) * mm});
            skLineSegment(sketch, "E1208", {"start": v(12.4, 11.07) * mm, "end": v(12.4, 11.07) * mm});
            skLineSegment(sketch, "E1209", {"start": v(12.4, 11.07) * mm, "end": v(12.43, 11.07) * mm});
            skLineSegment(sketch, "E1210", {"start": v(12.43, 11.07) * mm, "end": v(12.44, 11.07) * mm});
            skLineSegment(sketch, "E1211", {"start": v(12.44, 11.07) * mm, "end": v(12.46, 11.07) * mm});
            skLineSegment(sketch, "E1212", {"start": v(12.46, 11.07) * mm, "end": v(12.48, 11.06) * mm});
            skLineSegment(sketch, "E1213", {"start": v(12.48, 11.06) * mm, "end": v(12.5, 11.06) * mm});
            skLineSegment(sketch, "E1214", {"start": v(12.5, 11.06) * mm, "end": v(12.51, 11.05) * mm});
            skLineSegment(sketch, "E1215", {"start": v(12.51, 11.05) * mm, "end": v(12.53, 11.04) * mm});
            skLineSegment(sketch, "E1216", {"start": v(12.53, 11.04) * mm, "end": v(12.54, 11.04) * mm});
            skLineSegment(sketch, "E1217", {"start": v(12.54, 11.04) * mm, "end": v(12.56, 11.03) * mm});
            skLineSegment(sketch, "E1218", {"start": v(12.56, 11.03) * mm, "end": v(12.57, 11.02) * mm});
            skLineSegment(sketch, "E1219", {"start": v(12.57, 11.02) * mm, "end": v(12.58, 11) * mm});
            skLineSegment(sketch, "E1220", {"start": v(12.58, 11) * mm, "end": v(12.6, 11) * mm});
            skLineSegment(sketch, "E1221", {"start": v(12.6, 11) * mm, "end": v(12.6, 10.98) * mm});
            skLineSegment(sketch, "E1222", {"start": v(12.6, 10.98) * mm, "end": v(12.61, 10.97) * mm});
            skLineSegment(sketch, "E1223", {"start": v(12.61, 10.97) * mm, "end": v(12.62, 10.95) * mm});
            skLineSegment(sketch, "E1224", {"start": v(12.62, 10.95) * mm, "end": v(12.63, 10.93) * mm});
            skLineSegment(sketch, "E1225", {"start": v(12.63, 10.93) * mm, "end": v(19.74, -3.27) * mm});
            skLineSegment(sketch, "E1226", {"start": v(19.74, -3.27) * mm, "end": v(19.74, -3.29) * mm});
            skLineSegment(sketch, "E1227", {"start": v(19.74, -3.29) * mm, "end": v(19.75, -3.3) * mm});
            skLineSegment(sketch, "E1228", {"start": v(19.75, -3.3) * mm, "end": v(19.75, -3.32) * mm});
            skLineSegment(sketch, "E1229", {"start": v(19.75, -3.32) * mm, "end": v(19.76, -3.33) * mm});
            skLineSegment(sketch, "E1230", {"start": v(19.76, -3.33) * mm, "end": v(19.76, -3.35) * mm});
            skLineSegment(sketch, "E1231", {"start": v(19.76, -3.35) * mm, "end": v(19.76, -3.37) * mm});
            skLineSegment(sketch, "E1232", {"start": v(19.76, -3.37) * mm, "end": v(19.76, -3.38) * mm});
            skLineSegment(sketch, "E1233", {"start": v(19.76, -3.38) * mm, "end": v(19.76, -3.4) * mm});
            skLineSegment(sketch, "E1234", {"start": v(19.76, -3.4) * mm, "end": v(19.76, -3.41) * mm});
            skLineSegment(sketch, "E1235", {"start": v(19.76, -3.41) * mm, "end": v(19.76, -3.43) * mm});
            skLineSegment(sketch, "E1236", {"start": v(19.76, -3.43) * mm, "end": v(19.76, -3.44) * mm});
            skLineSegment(sketch, "E1237", {"start": v(19.76, -3.44) * mm, "end": v(19.75, -3.46) * mm});
            skLineSegment(sketch, "E1238", {"start": v(19.75, -3.46) * mm, "end": v(19.75, -3.48) * mm});
            skLineSegment(sketch, "E1239", {"start": v(19.75, -3.48) * mm, "end": v(19.74, -3.5) * mm});
            skLineSegment(sketch, "E1240", {"start": v(19.74, -3.5) * mm, "end": v(19.73, -3.5) * mm});
            skLineSegment(sketch, "E1241", {"start": v(19.73, -3.5) * mm, "end": v(19.72, -3.52) * mm});
            skLineSegment(sketch, "E1242", {"start": v(19.72, -3.52) * mm, "end": v(19.72, -3.53) * mm});
            skLineSegment(sketch, "E1243", {"start": v(19.72, -3.53) * mm, "end": v(19.7, -3.55) * mm});
            skLineSegment(sketch, "E1244", {"start": v(19.7, -3.55) * mm, "end": v(19.7, -3.56) * mm});
            skLineSegment(sketch, "E1245", {"start": v(19.7, -3.56) * mm, "end": v(19.68, -3.57) * mm});
            skLineSegment(sketch, "E1246", {"start": v(19.68, -3.57) * mm, "end": v(19.67, -3.58) * mm});
            skLineSegment(sketch, "E1247", {"start": v(19.67, -3.58) * mm, "end": v(19.66, -3.6) * mm});
            skLineSegment(sketch, "E1248", {"start": v(19.66, -3.6) * mm, "end": v(19.65, -3.6) * mm});
            skLineSegment(sketch, "E1249", {"start": v(19.65, -3.6) * mm, "end": v(19.63, -3.6) * mm});
            skLineSegment(sketch, "E1250", {"start": v(19.63, -3.6) * mm, "end": v(19.62, -3.62) * mm});
            skLineSegment(sketch, "E1251", {"start": v(19.62, -3.62) * mm, "end": v(19.6, -3.62) * mm});
            skLineSegment(sketch, "E1252", {"start": v(19.6, -3.62) * mm, "end": v(19.59, -3.63) * mm});
            skLineSegment(sketch, "E1253", {"start": v(19.59, -3.63) * mm, "end": v(19.57, -3.63) * mm});
            skLineSegment(sketch, "E1254", {"start": v(19.57, -3.63) * mm, "end": v(19.56, -3.64) * mm});
            skLineSegment(sketch, "E1255", {"start": v(19.56, -3.64) * mm, "end": v(19.54, -3.64) * mm});
            skLineSegment(sketch, "E1256", {"start": v(19.54, -3.64) * mm, "end": v(19.53, -3.64) * mm});
            skLineSegment(sketch, "E1257", {"start": v(19.53, -3.64) * mm, "end": v(19.5, -3.64) * mm});
            skLineSegment(sketch, "E1258", {"start": v(19.5, -3.64) * mm, "end": v(9.92, -3.64) * mm});
            skLineSegment(sketch, "E1259", {"start": v(9.92, -3.64) * mm, "end": v(9.7, -3.64) * mm});
            skLineSegment(sketch, "E1260", {"start": v(9.7, -3.64) * mm, "end": v(9.49, -3.66) * mm});
            skLineSegment(sketch, "E1261", {"start": v(9.49, -3.66) * mm, "end": v(9.28, -3.68) * mm});
            skLineSegment(sketch, "E1262", {"start": v(9.28, -3.68) * mm, "end": v(9.07, -3.7) * mm});
            skLineSegment(sketch, "E1263", {"start": v(9.07, -3.7) * mm, "end": v(8.87, -3.75) * mm});
            skLineSegment(sketch, "E1264", {"start": v(8.87, -3.75) * mm, "end": v(8.68, -3.8) * mm});
            skLineSegment(sketch, "E1265", {"start": v(8.68, -3.8) * mm, "end": v(8.5, -3.85) * mm});
            skLineSegment(sketch, "E1266", {"start": v(8.5, -3.85) * mm, "end": v(8.31, -3.91) * mm});
            skLineSegment(sketch, "E1267", {"start": v(8.31, -3.91) * mm, "end": v(8.13, -3.99) * mm});
            skLineSegment(sketch, "E1268", {"start": v(8.13, -3.99) * mm, "end": v(7.96, -4.07) * mm});
            skLineSegment(sketch, "E1269", {"start": v(7.96, -4.07) * mm, "end": v(7.8, -4.16) * mm});
            skLineSegment(sketch, "E1270", {"start": v(7.8, -4.16) * mm, "end": v(7.63, -4.25) * mm});
            skLineSegment(sketch, "E1271", {"start": v(7.63, -4.25) * mm, "end": v(7.48, -4.36) * mm});
            skLineSegment(sketch, "E1272", {"start": v(7.48, -4.36) * mm, "end": v(7.33, -4.47) * mm});
            skLineSegment(sketch, "E1273", {"start": v(7.33, -4.47) * mm, "end": v(7.18, -4.6) * mm});
            skLineSegment(sketch, "E1274", {"start": v(7.18, -4.6) * mm, "end": v(7.05, -4.73) * mm});
            skLineSegment(sketch, "E1275", {"start": v(7.05, -4.73) * mm, "end": v(6.92, -4.87) * mm});
            skLineSegment(sketch, "E1276", {"start": v(6.92, -4.87) * mm, "end": v(6.8, -5.01) * mm});
            skLineSegment(sketch, "E1277", {"start": v(6.8, -5.01) * mm, "end": v(6.68, -5.16) * mm});
            skLineSegment(sketch, "E1278", {"start": v(6.68, -5.16) * mm, "end": v(6.57, -5.31) * mm});
            skLineSegment(sketch, "E1279", {"start": v(6.57, -5.31) * mm, "end": v(6.47, -5.48) * mm});
            skLineSegment(sketch, "E1280", {"start": v(6.47, -5.48) * mm, "end": v(6.39, -5.64) * mm});
            skLineSegment(sketch, "E1281", {"start": v(6.39, -5.64) * mm, "end": v(6.3, -5.81) * mm});
            skLineSegment(sketch, "E1282", {"start": v(6.3, -5.81) * mm, "end": v(6.23, -6) * mm});
            skLineSegment(sketch, "E1283", {"start": v(6.23, -6) * mm, "end": v(6.17, -6.17) * mm});
            skLineSegment(sketch, "E1284", {"start": v(6.17, -6.17) * mm, "end": v(6.11, -6.36) * mm});
            skLineSegment(sketch, "E1285", {"start": v(6.11, -6.36) * mm, "end": v(6.07, -6.56) * mm});
            skLineSegment(sketch, "E1286", {"start": v(6.07, -6.56) * mm, "end": v(6.03, -6.76) * mm});
            skLineSegment(sketch, "E1287", {"start": v(6.03, -6.76) * mm, "end": v(6, -6.96) * mm});
            skLineSegment(sketch, "E1288", {"start": v(6, -6.96) * mm, "end": v(5.98, -7.17) * mm});
            skLineSegment(sketch, "E1289", {"start": v(5.98, -7.17) * mm, "end": v(5.96, -7.38) * mm});
            skLineSegment(sketch, "E1290", {"start": v(5.96, -7.38) * mm, "end": v(5.96, -7.6) * mm});
            skLineSegment(sketch, "E1291", {"start": v(5.96, -7.6) * mm, "end": v(5.96, -7.82) * mm});
            skLineSegment(sketch, "E1292", {"start": v(5.96, -7.82) * mm, "end": v(5.98, -8.03) * mm});
            skLineSegment(sketch, "E1293", {"start": v(5.98, -8.03) * mm, "end": v(6, -8.23) * mm});
            skLineSegment(sketch, "E1294", {"start": v(6, -8.23) * mm, "end": v(6.03, -8.43) * mm});
            skLineSegment(sketch, "E1295", {"start": v(6.03, -8.43) * mm, "end": v(6.07, -8.63) * mm});
            skLineSegment(sketch, "E1296", {"start": v(6.07, -8.63) * mm, "end": v(6.12, -8.82) * mm});
            skLineSegment(sketch, "E1297", {"start": v(6.12, -8.82) * mm, "end": v(6.17, -9) * mm});
            skLineSegment(sketch, "E1298", {"start": v(6.17, -9) * mm, "end": v(6.24, -9.19) * mm});
            skLineSegment(sketch, "E1299", {"start": v(6.24, -9.19) * mm, "end": v(6.31, -9.37) * mm});
            skLineSegment(sketch, "E1300", {"start": v(6.31, -9.37) * mm, "end": v(6.4, -9.54) * mm});
            skLineSegment(sketch, "E1301", {"start": v(6.4, -9.54) * mm, "end": v(6.49, -9.7) * mm});
            skLineSegment(sketch, "E1302", {"start": v(6.49, -9.7) * mm, "end": v(6.59, -9.87) * mm});
            skLineSegment(sketch, "E1303", {"start": v(6.59, -9.87) * mm, "end": v(6.7, -10.03) * mm});
            skLineSegment(sketch, "E1304", {"start": v(6.7, -10.03) * mm, "end": v(6.81, -10.18) * mm});
            skLineSegment(sketch, "E1305", {"start": v(6.81, -10.18) * mm, "end": v(6.94, -10.33) * mm});
            skLineSegment(sketch, "E1306", {"start": v(6.94, -10.33) * mm, "end": v(7.07, -10.48) * mm});
            skLineSegment(sketch, "E1307", {"start": v(7.07, -10.48) * mm, "end": v(7.21, -10.62) * mm});
            skLineSegment(sketch, "E1308", {"start": v(7.21, -10.62) * mm, "end": v(7.36, -10.74) * mm});
            skLineSegment(sketch, "E1309", {"start": v(7.36, -10.74) * mm, "end": v(7.51, -10.86) * mm});
            skLineSegment(sketch, "E1310", {"start": v(7.51, -10.86) * mm, "end": v(7.67, -10.98) * mm});
            skLineSegment(sketch, "E1311", {"start": v(7.67, -10.98) * mm, "end": v(7.83, -11.08) * mm});
            skLineSegment(sketch, "E1312", {"start": v(7.83, -11.08) * mm, "end": v(8, -11.17) * mm});
            skLineSegment(sketch, "E1313", {"start": v(8, -11.17) * mm, "end": v(8.17, -11.26) * mm});
            skLineSegment(sketch, "E1314", {"start": v(8.17, -11.26) * mm, "end": v(8.34, -11.33) * mm});
            skLineSegment(sketch, "E1315", {"start": v(8.34, -11.33) * mm, "end": v(8.52, -11.4) * mm});
            skLineSegment(sketch, "E1316", {"start": v(8.52, -11.4) * mm, "end": v(8.7, -11.46) * mm});
            skLineSegment(sketch, "E1317", {"start": v(8.7, -11.46) * mm, "end": v(8.9, -11.5) * mm});
            skLineSegment(sketch, "E1318", {"start": v(8.9, -11.5) * mm, "end": v(9.1, -11.55) * mm});
            skLineSegment(sketch, "E1319", {"start": v(9.1, -11.55) * mm, "end": v(9.3, -11.58) * mm});
            skLineSegment(sketch, "E1320", {"start": v(9.3, -11.58) * mm, "end": v(9.5, -11.6) * mm});
            skLineSegment(sketch, "E1321", {"start": v(9.5, -11.6) * mm, "end": v(9.7, -11.61) * mm});
            skLineSegment(sketch, "E1322", {"start": v(9.7, -11.61) * mm, "end": v(9.92, -11.62) * mm});
            skLineSegment(sketch, "E1323", {"start": v(9.92, -11.62) * mm, "end": v(23.5, -11.62) * mm});
            skLineSegment(sketch, "E1324", {"start": v(23.5, -11.62) * mm, "end": v(23.54, -11.62) * mm});
            skLineSegment(sketch, "E1325", {"start": v(23.54, -11.62) * mm, "end": v(23.58, -11.63) * mm});
            skLineSegment(sketch, "E1326", {"start": v(23.58, -11.63) * mm, "end": v(23.63, -11.63) * mm});
            skLineSegment(sketch, "E1327", {"start": v(23.63, -11.63) * mm, "end": v(23.67, -11.64) * mm});
            skLineSegment(sketch, "E1328", {"start": v(23.67, -11.64) * mm, "end": v(23.7, -11.66) * mm});
            skLineSegment(sketch, "E1329", {"start": v(23.7, -11.66) * mm, "end": v(23.75, -11.67) * mm});
            skLineSegment(sketch, "E1330", {"start": v(23.75, -11.67) * mm, "end": v(23.79, -11.7) * mm});
            skLineSegment(sketch, "E1331", {"start": v(23.79, -11.7) * mm, "end": v(23.83, -11.71) * mm});
            skLineSegment(sketch, "E1332", {"start": v(23.83, -11.71) * mm, "end": v(23.86, -11.74) * mm});
            skLineSegment(sketch, "E1333", {"start": v(23.86, -11.74) * mm, "end": v(23.9, -11.76) * mm});
            skLineSegment(sketch, "E1334", {"start": v(23.9, -11.76) * mm, "end": v(23.93, -11.8) * mm});
            skLineSegment(sketch, "E1335", {"start": v(23.93, -11.8) * mm, "end": v(23.96, -11.82) * mm});
            skLineSegment(sketch, "E1336", {"start": v(23.96, -11.82) * mm, "end": v(23.99, -11.85) * mm});
            skLineSegment(sketch, "E1337", {"start": v(23.99, -11.85) * mm, "end": v(24.01, -11.89) * mm});
            skLineSegment(sketch, "E1338", {"start": v(24.01, -11.89) * mm, "end": v(24.04, -11.93) * mm});
            skLineSegment(sketch, "E1339", {"start": v(24.04, -11.93) * mm, "end": v(24.06, -11.97) * mm});
            skLineSegment(sketch, "E1340", {"start": v(24.06, -11.97) * mm, "end": v(30.99, -25.78) * mm});
            skLineSegment(sketch, "E1341", {"start": v(30.99, -25.78) * mm, "end": v(31.03, -25.86) * mm});
            skLineSegment(sketch, "E1342", {"start": v(31.03, -25.86) * mm, "end": v(31.08, -25.93) * mm});
            skLineSegment(sketch, "E1343", {"start": v(31.08, -25.93) * mm, "end": v(31.13, -26) * mm});
            skLineSegment(sketch, "E1344", {"start": v(31.13, -26) * mm, "end": v(31.2, -26.07) * mm});
            skLineSegment(sketch, "E1345", {"start": v(31.2, -26.07) * mm, "end": v(31.25, -26.14) * mm});
            skLineSegment(sketch, "E1346", {"start": v(31.25, -26.14) * mm, "end": v(31.32, -26.2) * mm});
            skLineSegment(sketch, "E1347", {"start": v(31.32, -26.2) * mm, "end": v(31.39, -26.25) * mm});
            skLineSegment(sketch, "E1348", {"start": v(31.39, -26.25) * mm, "end": v(31.46, -26.3) * mm});
            skLineSegment(sketch, "E1349", {"start": v(31.46, -26.3) * mm, "end": v(31.54, -26.34) * mm});
            skLineSegment(sketch, "E1350", {"start": v(31.54, -26.34) * mm, "end": v(31.62, -26.38) * mm});
            skLineSegment(sketch, "E1351", {"start": v(31.62, -26.38) * mm, "end": v(31.7, -26.41) * mm});
            skLineSegment(sketch, "E1352", {"start": v(31.7, -26.41) * mm, "end": v(31.79, -26.44) * mm});
            skLineSegment(sketch, "E1353", {"start": v(31.79, -26.44) * mm, "end": v(31.87, -26.46) * mm});
            skLineSegment(sketch, "E1354", {"start": v(31.87, -26.46) * mm, "end": v(31.96, -26.48) * mm});
            skLineSegment(sketch, "E1355", {"start": v(31.96, -26.48) * mm, "end": v(32.05, -26.49) * mm});
            skLineSegment(sketch, "E1356", {"start": v(32.05, -26.49) * mm, "end": v(32.14, -26.49) * mm});
            skLineSegment(sketch, "E1357", {"start": v(32.14, -26.49) * mm, "end": v(35.96, -26.49) * mm});
            skLineSegment(sketch, "E1358", {"start": v(35.96, -26.49) * mm, "end": v(36.17, -26.48) * mm});
            skLineSegment(sketch, "E1359", {"start": v(36.17, -26.48) * mm, "end": v(36.38, -26.47) * mm});
            skLineSegment(sketch, "E1360", {"start": v(36.38, -26.47) * mm, "end": v(36.58, -26.45) * mm});
            skLineSegment(sketch, "E1361", {"start": v(36.58, -26.45) * mm, "end": v(36.78, -26.42) * mm});
            skLineSegment(sketch, "E1362", {"start": v(36.78, -26.42) * mm, "end": v(36.98, -26.38) * mm});
            skLineSegment(sketch, "E1363", {"start": v(36.98, -26.38) * mm, "end": v(37.17, -26.33) * mm});
            skLineSegment(sketch, "E1364", {"start": v(37.17, -26.33) * mm, "end": v(37.35, -26.27) * mm});
            skLineSegment(sketch, "E1365", {"start": v(37.35, -26.27) * mm, "end": v(37.53, -26.2) * mm});
            skLineSegment(sketch, "E1366", {"start": v(37.53, -26.2) * mm, "end": v(37.71, -26.13) * mm});
            skLineSegment(sketch, "E1367", {"start": v(37.71, -26.13) * mm, "end": v(37.88, -26.05) * mm});
            skLineSegment(sketch, "E1368", {"start": v(37.88, -26.05) * mm, "end": v(38.05, -25.96) * mm});
            skLineSegment(sketch, "E1369", {"start": v(38.05, -25.96) * mm, "end": v(38.2, -25.86) * mm});
            skLineSegment(sketch, "E1370", {"start": v(38.2, -25.86) * mm, "end": v(38.37, -25.75) * mm});
            skLineSegment(sketch, "E1371", {"start": v(38.37, -25.75) * mm, "end": v(38.52, -25.63) * mm});
            skLineSegment(sketch, "E1372", {"start": v(38.52, -25.63) * mm, "end": v(38.66, -25.5) * mm});
            skLineSegment(sketch, "E1373", {"start": v(38.66, -25.5) * mm, "end": v(38.8, -25.37) * mm});
            skLineSegment(sketch, "E1374", {"start": v(38.8, -25.37) * mm, "end": v(38.94, -25.23) * mm});
            skLineSegment(sketch, "E1375", {"start": v(38.94, -25.23) * mm, "end": v(39.07, -25.09) * mm});
            skLineSegment(sketch, "E1376", {"start": v(39.07, -25.09) * mm, "end": v(39.18, -24.94) * mm});
            skLineSegment(sketch, "E1377", {"start": v(39.18, -24.94) * mm, "end": v(39.3, -24.78) * mm});
            skLineSegment(sketch, "E1378", {"start": v(39.3, -24.78) * mm, "end": v(39.4, -24.62) * mm});
            skLineSegment(sketch, "E1379", {"start": v(39.4, -24.62) * mm, "end": v(39.48, -24.45) * mm});
            skLineSegment(sketch, "E1380", {"start": v(39.48, -24.45) * mm, "end": v(39.57, -24.28) * mm});
            skLineSegment(sketch, "E1381", {"start": v(39.57, -24.28) * mm, "end": v(39.64, -24.1) * mm});
            skLineSegment(sketch, "E1382", {"start": v(39.64, -24.1) * mm, "end": v(39.7, -23.92) * mm});
            skLineSegment(sketch, "E1383", {"start": v(39.7, -23.92) * mm, "end": v(39.76, -23.74) * mm});
            skLineSegment(sketch, "E1384", {"start": v(39.76, -23.74) * mm, "end": v(39.8, -23.55) * mm});
            skLineSegment(sketch, "E1385", {"start": v(39.8, -23.55) * mm, "end": v(39.85, -23.35) * mm});
            skLineSegment(sketch, "E1386", {"start": v(39.85, -23.35) * mm, "end": v(39.88, -23.15) * mm});
            skLineSegment(sketch, "E1387", {"start": v(39.88, -23.15) * mm, "end": v(39.9, -22.95) * mm});
            skLineSegment(sketch, "E1388", {"start": v(39.9, -22.95) * mm, "end": v(39.91, -22.74) * mm});
            skLineSegment(sketch, "E1389", {"start": v(39.91, -22.74) * mm, "end": v(39.92, -22.53) * mm});
            skLineSegment(sketch, "E1390", {"start": v(39.92, -22.53) * mm, "end": v(39.92, 12.54) * mm});
            skLineSegment(sketch, "E1391", {"start": v(39.92, 12.54) * mm, "end": v(39.92, 12.6) * mm});
            skLineSegment(sketch, "E1392", {"start": v(39.92, 12.6) * mm, "end": v(39.93, 12.64) * mm});
            skLineSegment(sketch, "E1393", {"start": v(39.93, 12.64) * mm, "end": v(39.94, 12.7) * mm});
            skLineSegment(sketch, "E1394", {"start": v(39.94, 12.7) * mm, "end": v(39.96, 12.74) * mm});
            skLineSegment(sketch, "E1395", {"start": v(39.96, 12.74) * mm, "end": v(39.98, 12.78) * mm});
            skLineSegment(sketch, "E1396", {"start": v(39.98, 12.78) * mm, "end": v(40, 12.82) * mm});
            skLineSegment(sketch, "E1397", {"start": v(40, 12.82) * mm, "end": v(40.03, 12.86) * mm});
            skLineSegment(sketch, "E1398", {"start": v(40.03, 12.86) * mm, "end": v(40.06, 12.9) * mm});
            skLineSegment(sketch, "E1399", {"start": v(40.06, 12.9) * mm, "end": v(40.1, 12.93) * mm});
            skLineSegment(sketch, "E1400", {"start": v(40.1, 12.93) * mm, "end": v(40.14, 12.96) * mm});
            skLineSegment(sketch, "E1401", {"start": v(40.14, 12.96) * mm, "end": v(40.18, 12.98) * mm});
            skLineSegment(sketch, "E1402", {"start": v(40.18, 12.98) * mm, "end": v(40.22, 13) * mm});
            skLineSegment(sketch, "E1403", {"start": v(40.22, 13) * mm, "end": v(40.27, 13.02) * mm});
            skLineSegment(sketch, "E1404", {"start": v(40.27, 13.02) * mm, "end": v(40.32, 13.03) * mm});
            skLineSegment(sketch, "E1405", {"start": v(40.32, 13.03) * mm, "end": v(40.37, 13.04) * mm});
            skLineSegment(sketch, "E1406", {"start": v(40.37, 13.04) * mm, "end": v(40.42, 13.04) * mm});
            skLineSegment(sketch, "E1407", {"start": v(40.42, 13.04) * mm, "end": v(53.53, 13.04) * mm});
            skLineSegment(sketch, "E1408", {"start": v(53.53, 13.04) * mm, "end": v(53.8, 13.02) * mm});
            skLineSegment(sketch, "E1409", {"start": v(53.8, 13.02) * mm, "end": v(54.08, 13) * mm});
            skLineSegment(sketch, "E1410", {"start": v(54.08, 13) * mm, "end": v(54.35, 12.97) * mm});
            skLineSegment(sketch, "E1411", {"start": v(54.35, 12.97) * mm, "end": v(54.63, 12.93) * mm});
            skLineSegment(sketch, "E1412", {"start": v(54.63, 12.93) * mm, "end": v(54.9, 12.88) * mm});
            skLineSegment(sketch, "E1413", {"start": v(54.9, 12.88) * mm, "end": v(55.17, 12.83) * mm});
            skLineSegment(sketch, "E1414", {"start": v(55.17, 12.83) * mm, "end": v(55.45, 12.76) * mm});
            skLineSegment(sketch, "E1415", {"start": v(55.45, 12.76) * mm, "end": v(55.72, 12.7) * mm});
            skLineSegment(sketch, "E1416", {"start": v(55.72, 12.7) * mm, "end": v(55.99, 12.6) * mm});
            skLineSegment(sketch, "E1417", {"start": v(55.99, 12.6) * mm, "end": v(56.26, 12.52) * mm});
            skLineSegment(sketch, "E1418", {"start": v(56.26, 12.52) * mm, "end": v(56.53, 12.42) * mm});
            skLineSegment(sketch, "E1419", {"start": v(56.53, 12.42) * mm, "end": v(56.8, 12.31) * mm});
            skLineSegment(sketch, "E1420", {"start": v(56.8, 12.31) * mm, "end": v(57.07, 12.2) * mm});
            skLineSegment(sketch, "E1421", {"start": v(57.07, 12.2) * mm, "end": v(57.34, 12.07) * mm});
            skLineSegment(sketch, "E1422", {"start": v(57.34, 12.07) * mm, "end": v(57.6, 11.94) * mm});
            skLineSegment(sketch, "E1423", {"start": v(57.6, 11.94) * mm, "end": v(58.1, 11.67) * mm});
            skLineSegment(sketch, "E1424", {"start": v(58.1, 11.67) * mm, "end": v(58.54, 11.37) * mm});
            skLineSegment(sketch, "E1425", {"start": v(58.54, 11.37) * mm, "end": v(58.97, 11.05) * mm});
            skLineSegment(sketch, "E1426", {"start": v(58.97, 11.05) * mm, "end": v(59.36, 10.7) * mm});
            skLineSegment(sketch, "E1427", {"start": v(59.36, 10.7) * mm, "end": v(59.72, 10.33) * mm});
            skLineSegment(sketch, "E1428", {"start": v(59.72, 10.33) * mm, "end": v(60.05, 9.94) * mm});
            skLineSegment(sketch, "E1429", {"start": v(60.05, 9.94) * mm, "end": v(60.35, 9.52) * mm});
            skLineSegment(sketch, "E1430", {"start": v(60.35, 9.52) * mm, "end": v(60.62, 9.08) * mm});
            skLineSegment(sketch, "E1431", {"start": v(60.62, 9.08) * mm, "end": v(60.85, 8.6) * mm});
            skLineSegment(sketch, "E1432", {"start": v(60.85, 8.6) * mm, "end": v(61.06, 8.12) * mm});
            skLineSegment(sketch, "E1433", {"start": v(61.06, 8.12) * mm, "end": v(61.23, 7.6) * mm});
            skLineSegment(sketch, "E1434", {"start": v(61.23, 7.6) * mm, "end": v(61.37, 7.06) * mm});
            skLineSegment(sketch, "E1435", {"start": v(61.37, 7.06) * mm, "end": v(61.48, 6.5) * mm});
            skLineSegment(sketch, "E1436", {"start": v(61.48, 6.5) * mm, "end": v(61.56, 5.92) * mm});
            skLineSegment(sketch, "E1437", {"start": v(61.56, 5.92) * mm, "end": v(61.61, 5.3) * mm});
            skLineSegment(sketch, "E1438", {"start": v(61.61, 5.3) * mm, "end": v(61.63, 4.67) * mm});
            skLineSegment(sketch, "E1439", {"start": v(61.63, 4.67) * mm, "end": v(61.61, 4.04) * mm});
            skLineSegment(sketch, "E1440", {"start": v(61.61, 4.04) * mm, "end": v(61.56, 3.43) * mm});
            skLineSegment(sketch, "E1441", {"start": v(61.56, 3.43) * mm, "end": v(61.48, 2.85) * mm});
            skLineSegment(sketch, "E1442", {"start": v(61.48, 2.85) * mm, "end": v(61.37, 2.28) * mm});
            skLineSegment(sketch, "E1443", {"start": v(61.37, 2.28) * mm, "end": v(61.23, 1.74) * mm});
            skLineSegment(sketch, "E1444", {"start": v(61.23, 1.74) * mm, "end": v(61.06, 1.23) * mm});
            skLineSegment(sketch, "E1445", {"start": v(61.06, 1.23) * mm, "end": v(60.85, 0.74) * mm});
            skLineSegment(sketch, "E1446", {"start": v(60.85, 0.74) * mm, "end": v(60.62, 0.27) * mm});
            skLineSegment(sketch, "E1447", {"start": v(60.62, 0.27) * mm, "end": v(60.35, -0.17) * mm});
            skLineSegment(sketch, "E1448", {"start": v(60.35, -0.17) * mm, "end": v(60.05, -0.6) * mm});
            skLineSegment(sketch, "E1449", {"start": v(60.05, -0.6) * mm, "end": v(59.72, -0.99) * mm});
            skLineSegment(sketch, "E1450", {"start": v(59.72, -0.99) * mm, "end": v(59.36, -1.36) * mm});
            skLineSegment(sketch, "E1451", {"start": v(59.36, -1.36) * mm, "end": v(58.97, -1.7) * mm});
            skLineSegment(sketch, "E1452", {"start": v(58.97, -1.7) * mm, "end": v(58.55, -2.02) * mm});
            skLineSegment(sketch, "E1453", {"start": v(58.55, -2.02) * mm, "end": v(58.1, -2.32) * mm});
            skLineSegment(sketch, "E1454", {"start": v(58.1, -2.32) * mm, "end": v(57.6, -2.6) * mm});
            skLineSegment(sketch, "E1455", {"start": v(57.6, -2.6) * mm, "end": v(57.33, -2.73) * mm});
            skLineSegment(sketch, "E1456", {"start": v(57.33, -2.73) * mm, "end": v(57.05, -2.86) * mm});
            skLineSegment(sketch, "E1457", {"start": v(57.05, -2.86) * mm, "end": v(56.77, -2.98) * mm});
            skLineSegment(sketch, "E1458", {"start": v(56.77, -2.98) * mm, "end": v(56.5, -3.1) * mm});
            skLineSegment(sketch, "E1459", {"start": v(56.5, -3.1) * mm, "end": v(56.22, -3.2) * mm});
            skLineSegment(sketch, "E1460", {"start": v(56.22, -3.2) * mm, "end": v(55.94, -3.3) * mm});
            skLineSegment(sketch, "E1461", {"start": v(55.94, -3.3) * mm, "end": v(55.67, -3.38) * mm});
            skLineSegment(sketch, "E1462", {"start": v(55.67, -3.38) * mm, "end": v(55.4, -3.46) * mm});
            skLineSegment(sketch, "E1463", {"start": v(55.4, -3.46) * mm, "end": v(55.12, -3.52) * mm});
            skLineSegment(sketch, "E1464", {"start": v(55.12, -3.52) * mm, "end": v(54.85, -3.58) * mm});
            skLineSegment(sketch, "E1465", {"start": v(54.85, -3.58) * mm, "end": v(54.58, -3.63) * mm});
            skLineSegment(sketch, "E1466", {"start": v(54.58, -3.63) * mm, "end": v(54.31, -3.67) * mm});
            skLineSegment(sketch, "E1467", {"start": v(54.31, -3.67) * mm, "end": v(54.05, -3.7) * mm});
            skLineSegment(sketch, "E1468", {"start": v(54.05, -3.7) * mm, "end": v(53.78, -3.73) * mm});
            skLineSegment(sketch, "E1469", {"start": v(53.78, -3.73) * mm, "end": v(53.52, -3.74) * mm});
            skLineSegment(sketch, "E1470", {"start": v(53.52, -3.74) * mm, "end": v(45.85, -3.75) * mm});
            skLineSegment(sketch, "E1471", {"start": v(45.85, -3.75) * mm, "end": v(45.64, -3.75) * mm});
            skLineSegment(sketch, "E1472", {"start": v(45.64, -3.75) * mm, "end": v(45.43, -3.76) * mm});
            skLineSegment(sketch, "E1473", {"start": v(45.43, -3.76) * mm, "end": v(45.22, -3.79) * mm});
            skLineSegment(sketch, "E1474", {"start": v(45.22, -3.79) * mm, "end": v(45.02, -3.82) * mm});
            skLineSegment(sketch, "E1475", {"start": v(45.02, -3.82) * mm, "end": v(44.83, -3.86) * mm});
            skLineSegment(sketch, "E1476", {"start": v(44.83, -3.86) * mm, "end": v(44.64, -3.9) * mm});
            skLineSegment(sketch, "E1477", {"start": v(44.64, -3.9) * mm, "end": v(44.45, -3.96) * mm});
            skLineSegment(sketch, "E1478", {"start": v(44.45, -3.96) * mm, "end": v(44.27, -4.03) * mm});
            skLineSegment(sketch, "E1479", {"start": v(44.27, -4.03) * mm, "end": v(44.09, -4.1) * mm});
            skLineSegment(sketch, "E1480", {"start": v(44.09, -4.1) * mm, "end": v(43.92, -4.18) * mm});
            skLineSegment(sketch, "E1481", {"start": v(43.92, -4.18) * mm, "end": v(43.75, -4.27) * mm});
            skLineSegment(sketch, "E1482", {"start": v(43.75, -4.27) * mm, "end": v(43.58, -4.37) * mm});
            skLineSegment(sketch, "E1483", {"start": v(43.58, -4.37) * mm, "end": v(43.43, -4.48) * mm});
            skLineSegment(sketch, "E1484", {"start": v(43.43, -4.48) * mm, "end": v(43.27, -4.6) * mm});
            skLineSegment(sketch, "E1485", {"start": v(43.27, -4.6) * mm, "end": v(43.12, -4.73) * mm});
            skLineSegment(sketch, "E1486", {"start": v(43.12, -4.73) * mm, "end": v(42.98, -4.86) * mm});
            skLineSegment(sketch, "E1487", {"start": v(42.98, -4.86) * mm, "end": v(42.84, -5) * mm});
            skLineSegment(sketch, "E1488", {"start": v(42.84, -5) * mm, "end": v(42.71, -5.15) * mm});
            skLineSegment(sketch, "E1489", {"start": v(42.71, -5.15) * mm, "end": v(42.6, -5.3) * mm});
            skLineSegment(sketch, "E1490", {"start": v(42.6, -5.3) * mm, "end": v(42.48, -5.45) * mm});
            skLineSegment(sketch, "E1491", {"start": v(42.48, -5.45) * mm, "end": v(42.38, -5.62) * mm});
            skLineSegment(sketch, "E1492", {"start": v(42.38, -5.62) * mm, "end": v(42.28, -5.78) * mm});
            skLineSegment(sketch, "E1493", {"start": v(42.28, -5.78) * mm, "end": v(42.2, -5.95) * mm});
            skLineSegment(sketch, "E1494", {"start": v(42.2, -5.95) * mm, "end": v(42.12, -6.13) * mm});
            skLineSegment(sketch, "E1495", {"start": v(42.12, -6.13) * mm, "end": v(42.06, -6.31) * mm});
            skLineSegment(sketch, "E1496", {"start": v(42.06, -6.31) * mm, "end": v(42, -6.5) * mm});
            skLineSegment(sketch, "E1497", {"start": v(42, -6.5) * mm, "end": v(41.95, -6.69) * mm});
            skLineSegment(sketch, "E1498", {"start": v(41.95, -6.69) * mm, "end": v(41.9, -6.88) * mm});
            skLineSegment(sketch, "E1499", {"start": v(41.9, -6.88) * mm, "end": v(41.88, -7.08) * mm});
            skLineSegment(sketch, "E1500", {"start": v(41.88, -7.08) * mm, "end": v(41.85, -7.29) * mm});
            skLineSegment(sketch, "E1501", {"start": v(41.85, -7.29) * mm, "end": v(41.84, -7.5) * mm});
            skLineSegment(sketch, "E1502", {"start": v(41.84, -7.5) * mm, "end": v(41.84, -7.7) * mm});
            skLineSegment(sketch, "E1503", {"start": v(41.84, -7.7) * mm, "end": v(41.84, -24.27) * mm});
            skLineSegment(sketch, "E1504", {"start": v(41.84, -24.27) * mm, "end": v(41.85, -24.5) * mm});
            skLineSegment(sketch, "E1505", {"start": v(41.85, -24.5) * mm, "end": v(41.88, -24.72) * mm});
            skLineSegment(sketch, "E1506", {"start": v(41.88, -24.72) * mm, "end": v(41.94, -24.93) * mm});
            skLineSegment(sketch, "E1507", {"start": v(41.94, -24.93) * mm, "end": v(42.01, -25.13) * mm});
            skLineSegment(sketch, "E1508", {"start": v(42.01, -25.13) * mm, "end": v(42.1, -25.33) * mm});
            skLineSegment(sketch, "E1509", {"start": v(42.1, -25.33) * mm, "end": v(42.22, -25.5) * mm});
            skLineSegment(sketch, "E1510", {"start": v(42.22, -25.5) * mm, "end": v(42.34, -25.68) * mm});
            skLineSegment(sketch, "E1511", {"start": v(42.34, -25.68) * mm, "end": v(42.49, -25.84) * mm});
            skLineSegment(sketch, "E1512", {"start": v(42.49, -25.84) * mm, "end": v(42.64, -25.98) * mm});
            skLineSegment(sketch, "E1513", {"start": v(42.64, -25.98) * mm, "end": v(42.81, -26.1) * mm});
            skLineSegment(sketch, "E1514", {"start": v(42.81, -26.1) * mm, "end": v(43, -26.22) * mm});
            skLineSegment(sketch, "E1515", {"start": v(43, -26.22) * mm, "end": v(43.2, -26.31) * mm});
            skLineSegment(sketch, "E1516", {"start": v(43.2, -26.31) * mm, "end": v(43.4, -26.39) * mm});
            skLineSegment(sketch, "E1517", {"start": v(43.4, -26.39) * mm, "end": v(43.6, -26.44) * mm});
            skLineSegment(sketch, "E1518", {"start": v(43.6, -26.44) * mm, "end": v(43.83, -26.48) * mm});
            skLineSegment(sketch, "E1519", {"start": v(43.83, -26.48) * mm, "end": v(44.05, -26.49) * mm});
            skLineSegment(sketch, "E1520", {"start": v(44.05, -26.49) * mm, "end": v(80.72, -26.49) * mm});
            skLineSegment(sketch, "E1521", {"start": v(80.72, -26.49) * mm, "end": v(81.07, -26.48) * mm});
            skLineSegment(sketch, "E1522", {"start": v(81.07, -26.48) * mm, "end": v(81.42, -26.46) * mm});
            skLineSegment(sketch, "E1523", {"start": v(81.42, -26.46) * mm, "end": v(81.75, -26.42) * mm});
            skLineSegment(sketch, "E1524", {"start": v(81.75, -26.42) * mm, "end": v(82.08, -26.38) * mm});
            skLineSegment(sketch, "E1525", {"start": v(82.08, -26.38) * mm, "end": v(82.4, -26.31) * mm});
            skLineSegment(sketch, "E1526", {"start": v(82.4, -26.31) * mm, "end": v(82.7, -26.23) * mm});
            skLineSegment(sketch, "E1527", {"start": v(82.7, -26.23) * mm, "end": v(83.01, -26.14) * mm});
            skLineSegment(sketch, "E1528", {"start": v(83.01, -26.14) * mm, "end": v(83.3, -26.04) * mm});
            skLineSegment(sketch, "E1529", {"start": v(83.3, -26.04) * mm, "end": v(83.6, -25.92) * mm});
            skLineSegment(sketch, "E1530", {"start": v(83.6, -25.92) * mm, "end": v(83.87, -25.78) * mm});
            skLineSegment(sketch, "E1531", {"start": v(83.87, -25.78) * mm, "end": v(84.14, -25.63) * mm});
            skLineSegment(sketch, "E1532", {"start": v(84.14, -25.63) * mm, "end": v(84.4, -25.47) * mm});
            skLineSegment(sketch, "E1533", {"start": v(84.4, -25.47) * mm, "end": v(84.66, -25.3) * mm});
            skLineSegment(sketch, "E1534", {"start": v(84.66, -25.3) * mm, "end": v(84.9, -25.1) * mm});
            skLineSegment(sketch, "E1535", {"start": v(84.9, -25.1) * mm, "end": v(85.14, -24.9) * mm});
            skLineSegment(sketch, "E1536", {"start": v(85.14, -24.9) * mm, "end": v(85.37, -24.69) * mm});
            skLineSegment(sketch, "E1537", {"start": v(85.37, -24.69) * mm, "end": v(85.59, -24.46) * mm});
            skLineSegment(sketch, "E1538", {"start": v(85.59, -24.46) * mm, "end": v(85.8, -24.22) * mm});
            skLineSegment(sketch, "E1539", {"start": v(85.8, -24.22) * mm, "end": v(85.98, -23.98) * mm});
            skLineSegment(sketch, "E1540", {"start": v(85.98, -23.98) * mm, "end": v(86.16, -23.72) * mm});
            skLineSegment(sketch, "E1541", {"start": v(86.16, -23.72) * mm, "end": v(86.32, -23.46) * mm});
            skLineSegment(sketch, "E1542", {"start": v(86.32, -23.46) * mm, "end": v(86.47, -23.19) * mm});
            skLineSegment(sketch, "E1543", {"start": v(86.47, -23.19) * mm, "end": v(86.6, -22.9) * mm});
            skLineSegment(sketch, "E1544", {"start": v(86.6, -22.9) * mm, "end": v(86.72, -22.62) * mm});
            skLineSegment(sketch, "E1545", {"start": v(86.72, -22.62) * mm, "end": v(86.83, -22.33) * mm});
            skLineSegment(sketch, "E1546", {"start": v(86.83, -22.33) * mm, "end": v(86.92, -22.02) * mm});
            skLineSegment(sketch, "E1547", {"start": v(86.92, -22.02) * mm, "end": v(87, -21.71) * mm});
            skLineSegment(sketch, "E1548", {"start": v(87, -21.71) * mm, "end": v(87.06, -21.4) * mm});
            skLineSegment(sketch, "E1549", {"start": v(87.06, -21.4) * mm, "end": v(87.1, -21.07) * mm});
            skLineSegment(sketch, "E1550", {"start": v(87.1, -21.07) * mm, "end": v(87.15, -20.73) * mm});
            skLineSegment(sketch, "E1551", {"start": v(87.15, -20.73) * mm, "end": v(87.17, -20.39) * mm});
            skLineSegment(sketch, "E1552", {"start": v(87.17, -20.39) * mm, "end": v(87.17, -20.04) * mm});
            skLineSegment(sketch, "E1553", {"start": v(87.17, -20.04) * mm, "end": v(87.17, 7.99) * mm});
            skLineSegment(sketch, "E1554", {"start": v(87.17, 7.99) * mm, "end": v(87.16, 8.3) * mm});
            skLineSegment(sketch, "E1555", {"start": v(87.16, 8.3) * mm, "end": v(87.1, 8.62) * mm});
            skLineSegment(sketch, "E1556", {"start": v(87.1, 8.62) * mm, "end": v(87.03, 8.92) * mm});
            skLineSegment(sketch, "E1557", {"start": v(87.03, 8.92) * mm, "end": v(86.93, 9.2) * mm});
            skLineSegment(sketch, "E1558", {"start": v(86.93, 9.2) * mm, "end": v(86.8, 9.48) * mm});
            skLineSegment(sketch, "E1559", {"start": v(86.8, 9.48) * mm, "end": v(86.64, 9.74) * mm});
            skLineSegment(sketch, "E1560", {"start": v(86.64, 9.74) * mm, "end": v(86.46, 9.98) * mm});
            skLineSegment(sketch, "E1561", {"start": v(86.46, 9.98) * mm, "end": v(86.25, 10.2) * mm});
            skLineSegment(sketch, "E1562", {"start": v(86.25, 10.2) * mm, "end": v(86.03, 10.4) * mm});
            skLineSegment(sketch, "E1563", {"start": v(86.03, 10.4) * mm, "end": v(85.8, 10.59) * mm});
            skLineSegment(sketch, "E1564", {"start": v(85.8, 10.59) * mm, "end": v(85.53, 10.74) * mm});
            skLineSegment(sketch, "E1565", {"start": v(85.53, 10.74) * mm, "end": v(85.26, 10.88) * mm});
            skLineSegment(sketch, "E1566", {"start": v(85.26, 10.88) * mm, "end": v(84.97, 10.98) * mm});
            skLineSegment(sketch, "E1567", {"start": v(84.97, 10.98) * mm, "end": v(84.67, 11.06) * mm});
            skLineSegment(sketch, "E1568", {"start": v(84.67, 11.06) * mm, "end": v(84.36, 11.1) * mm});
            skLineSegment(sketch, "E1569", {"start": v(84.36, 11.1) * mm, "end": v(84.04, 11.12) * mm});
            skLineSegment(sketch, "E1570", {"start": v(84.04, 11.12) * mm, "end": v(73.32, 11.12) * mm});
            skLineSegment(sketch, "E1571", {"start": v(73.32, 11.12) * mm, "end": v(73.2, 11.13) * mm});
            skLineSegment(sketch, "E1572", {"start": v(73.2, 11.13) * mm, "end": v(73.07, 11.14) * mm});
            skLineSegment(sketch, "E1573", {"start": v(73.07, 11.14) * mm, "end": v(72.97, 11.16) * mm});
            skLineSegment(sketch, "E1574", {"start": v(72.97, 11.16) * mm, "end": v(72.87, 11.18) * mm});
            skLineSegment(sketch, "E1575", {"start": v(72.87, 11.18) * mm, "end": v(72.77, 11.21) * mm});
            skLineSegment(sketch, "E1576", {"start": v(72.77, 11.21) * mm, "end": v(72.7, 11.25) * mm});
            skLineSegment(sketch, "E1577", {"start": v(72.7, 11.25) * mm, "end": v(72.62, 11.3) * mm});
            skLineSegment(sketch, "E1578", {"start": v(72.62, 11.3) * mm, "end": v(72.55, 11.36) * mm});
            skLineSegment(sketch, "E1579", {"start": v(72.55, 11.36) * mm, "end": v(72.5, 11.42) * mm});
            skLineSegment(sketch, "E1580", {"start": v(72.5, 11.42) * mm, "end": v(72.44, 11.5) * mm});
            skLineSegment(sketch, "E1581", {"start": v(72.44, 11.5) * mm, "end": v(72.4, 11.57) * mm});
            skLineSegment(sketch, "E1582", {"start": v(72.4, 11.57) * mm, "end": v(72.36, 11.66) * mm});
            skLineSegment(sketch, "E1583", {"start": v(72.36, 11.66) * mm, "end": v(72.34, 11.75) * mm});
            skLineSegment(sketch, "E1584", {"start": v(72.34, 11.75) * mm, "end": v(72.32, 11.85) * mm});
            skLineSegment(sketch, "E1585", {"start": v(72.32, 11.85) * mm, "end": v(72.3, 11.96) * mm});
            skLineSegment(sketch, "E1586", {"start": v(72.3, 11.96) * mm, "end": v(72.3, 12.08) * mm});
            skLineSegment(sketch, "E1587", {"start": v(72.3, 12.08) * mm, "end": v(72.3, 12.2) * mm});
            skLineSegment(sketch, "E1588", {"start": v(72.3, 12.2) * mm, "end": v(72.32, 12.31) * mm});
            skLineSegment(sketch, "E1589", {"start": v(72.32, 12.31) * mm, "end": v(72.34, 12.41) * mm});
            skLineSegment(sketch, "E1590", {"start": v(72.34, 12.41) * mm, "end": v(72.36, 12.5) * mm});
            skLineSegment(sketch, "E1591", {"start": v(72.36, 12.5) * mm, "end": v(72.4, 12.6) * mm});
            skLineSegment(sketch, "E1592", {"start": v(72.4, 12.6) * mm, "end": v(72.44, 12.67) * mm});
            skLineSegment(sketch, "E1593", {"start": v(72.44, 12.67) * mm, "end": v(72.5, 12.74) * mm});
            skLineSegment(sketch, "E1594", {"start": v(72.5, 12.74) * mm, "end": v(72.55, 12.8) * mm});
            skLineSegment(sketch, "E1595", {"start": v(72.55, 12.8) * mm, "end": v(72.62, 12.86) * mm});
            skLineSegment(sketch, "E1596", {"start": v(72.62, 12.86) * mm, "end": v(72.7, 12.9) * mm});
            skLineSegment(sketch, "E1597", {"start": v(72.7, 12.9) * mm, "end": v(72.77, 12.95) * mm});
            skLineSegment(sketch, "E1598", {"start": v(72.77, 12.95) * mm, "end": v(72.87, 12.98) * mm});
            skLineSegment(sketch, "E1599", {"start": v(72.87, 12.98) * mm, "end": v(72.97, 13) * mm});
            skLineSegment(sketch, "E1600", {"start": v(72.97, 13) * mm, "end": v(73.07, 13.03) * mm});
            skLineSegment(sketch, "E1601", {"start": v(73.07, 13.03) * mm, "end": v(73.2, 13.04) * mm});
            skLineSegment(sketch, "E1602", {"start": v(73.2, 13.04) * mm, "end": v(73.32, 13.04) * mm});
            skLineSegment(sketch, "E1603", {"start": v(73.32, 13.04) * mm, "end": v(102.95, 13.04) * mm});
            skLineSegment(sketch, "E1604", {"start": v(102.95, 13.04) * mm, "end": v(103.07, 13.04) * mm});
            skLineSegment(sketch, "E1605", {"start": v(103.07, 13.04) * mm, "end": v(103.2, 13.03) * mm});
            skLineSegment(sketch, "E1606", {"start": v(103.2, 13.03) * mm, "end": v(103.3, 13) * mm});
            skLineSegment(sketch, "E1607", {"start": v(103.3, 13) * mm, "end": v(103.4, 12.98) * mm});
            skLineSegment(sketch, "E1608", {"start": v(103.4, 12.98) * mm, "end": v(103.49, 12.95) * mm});
            skLineSegment(sketch, "E1609", {"start": v(103.49, 12.95) * mm, "end": v(103.57, 12.9) * mm});
            skLineSegment(sketch, "E1610", {"start": v(103.57, 12.9) * mm, "end": v(103.65, 12.86) * mm});
            skLineSegment(sketch, "E1611", {"start": v(103.65, 12.86) * mm, "end": v(103.71, 12.8) * mm});
            skLineSegment(sketch, "E1612", {"start": v(103.71, 12.8) * mm, "end": v(103.77, 12.74) * mm});
            skLineSegment(sketch, "E1613", {"start": v(103.77, 12.74) * mm, "end": v(103.82, 12.67) * mm});
            skLineSegment(sketch, "E1614", {"start": v(103.82, 12.67) * mm, "end": v(103.86, 12.6) * mm});
            skLineSegment(sketch, "E1615", {"start": v(103.86, 12.6) * mm, "end": v(103.9, 12.5) * mm});
            skLineSegment(sketch, "E1616", {"start": v(103.9, 12.5) * mm, "end": v(103.93, 12.41) * mm});
            skLineSegment(sketch, "E1617", {"start": v(103.93, 12.41) * mm, "end": v(103.94, 12.31) * mm});
            skLineSegment(sketch, "E1618", {"start": v(103.94, 12.31) * mm, "end": v(103.96, 12.2) * mm});
            skLineSegment(sketch, "E1619", {"start": v(103.96, 12.2) * mm, "end": v(103.96, 12.08) * mm});
            skLineSegment(sketch, "E1620", {"start": v(103.96, 12.08) * mm, "end": v(103.96, 11.96) * mm});
            skLineSegment(sketch, "E1621", {"start": v(103.96, 11.96) * mm, "end": v(103.94, 11.85) * mm});
            skLineSegment(sketch, "E1622", {"start": v(103.94, 11.85) * mm, "end": v(103.93, 11.75) * mm});
            skLineSegment(sketch, "E1623", {"start": v(103.93, 11.75) * mm, "end": v(103.9, 11.66) * mm});
            skLineSegment(sketch, "E1624", {"start": v(103.9, 11.66) * mm, "end": v(103.86, 11.57) * mm});
            skLineSegment(sketch, "E1625", {"start": v(103.86, 11.57) * mm, "end": v(103.82, 11.5) * mm});
            skLineSegment(sketch, "E1626", {"start": v(103.82, 11.5) * mm, "end": v(103.77, 11.42) * mm});
            skLineSegment(sketch, "E1627", {"start": v(103.77, 11.42) * mm, "end": v(103.71, 11.36) * mm});
            skLineSegment(sketch, "E1628", {"start": v(103.71, 11.36) * mm, "end": v(103.65, 11.3) * mm});
            skLineSegment(sketch, "E1629", {"start": v(103.65, 11.3) * mm, "end": v(103.57, 11.25) * mm});
            skLineSegment(sketch, "E1630", {"start": v(103.57, 11.25) * mm, "end": v(103.49, 11.21) * mm});
            skLineSegment(sketch, "E1631", {"start": v(103.49, 11.21) * mm, "end": v(103.4, 11.18) * mm});
            skLineSegment(sketch, "E1632", {"start": v(103.4, 11.18) * mm, "end": v(103.3, 11.16) * mm});
            skLineSegment(sketch, "E1633", {"start": v(103.3, 11.16) * mm, "end": v(103.2, 11.14) * mm});
            skLineSegment(sketch, "E1634", {"start": v(103.2, 11.14) * mm, "end": v(103.07, 11.13) * mm});
            skLineSegment(sketch, "E1635", {"start": v(103.07, 11.13) * mm, "end": v(102.95, 11.12) * mm});
            skLineSegment(sketch, "E1636", {"start": v(102.95, 11.12) * mm, "end": v(92.22, 11.12) * mm});
            skLineSegment(sketch, "E1637", {"start": v(92.22, 11.12) * mm, "end": v(91.9, 11.1) * mm});
            skLineSegment(sketch, "E1638", {"start": v(91.9, 11.1) * mm, "end": v(91.6, 11.06) * mm});
            skLineSegment(sketch, "E1639", {"start": v(91.6, 11.06) * mm, "end": v(91.3, 10.98) * mm});
            skLineSegment(sketch, "E1640", {"start": v(91.3, 10.98) * mm, "end": v(91, 10.88) * mm});
            skLineSegment(sketch, "E1641", {"start": v(91, 10.88) * mm, "end": v(90.73, 10.74) * mm});
            skLineSegment(sketch, "E1642", {"start": v(90.73, 10.74) * mm, "end": v(90.47, 10.59) * mm});
            skLineSegment(sketch, "E1643", {"start": v(90.47, 10.59) * mm, "end": v(90.23, 10.4) * mm});
            skLineSegment(sketch, "E1644", {"start": v(90.23, 10.4) * mm, "end": v(90, 10.2) * mm});
            skLineSegment(sketch, "E1645", {"start": v(90, 10.2) * mm, "end": v(89.8, 9.98) * mm});
            skLineSegment(sketch, "E1646", {"start": v(89.8, 9.98) * mm, "end": v(89.63, 9.74) * mm});
            skLineSegment(sketch, "E1647", {"start": v(89.63, 9.74) * mm, "end": v(89.47, 9.48) * mm});
            skLineSegment(sketch, "E1648", {"start": v(89.47, 9.48) * mm, "end": v(89.34, 9.2) * mm});
            skLineSegment(sketch, "E1649", {"start": v(89.34, 9.2) * mm, "end": v(89.23, 8.92) * mm});
            skLineSegment(sketch, "E1650", {"start": v(89.23, 8.92) * mm, "end": v(89.15, 8.62) * mm});
            skLineSegment(sketch, "E1651", {"start": v(89.15, 8.62) * mm, "end": v(89.1, 8.3) * mm});
            skLineSegment(sketch, "E1652", {"start": v(89.1, 8.3) * mm, "end": v(89.1, 7.99) * mm});
            skLineSegment(sketch, "E1653", {"start": v(89.1, 7.99) * mm, "end": v(89.1, -20.04) * mm});
            skLineSegment(sketch, "E1654", {"start": v(89.1, -20.04) * mm, "end": v(89.1, -20.38) * mm});
            skLineSegment(sketch, "E1655", {"start": v(89.1, -20.38) * mm, "end": v(89.12, -20.72) * mm});
            skLineSegment(sketch, "E1656", {"start": v(89.12, -20.72) * mm, "end": v(89.16, -21.05) * mm});
            skLineSegment(sketch, "E1657", {"start": v(89.16, -21.05) * mm, "end": v(89.2, -21.37) * mm});
            skLineSegment(sketch, "E1658", {"start": v(89.2, -21.37) * mm, "end": v(89.27, -21.69) * mm});
            skLineSegment(sketch, "E1659", {"start": v(89.27, -21.69) * mm, "end": v(89.35, -22) * mm});
            skLineSegment(sketch, "E1660", {"start": v(89.35, -22) * mm, "end": v(89.44, -22.3) * mm});
            skLineSegment(sketch, "E1661", {"start": v(89.44, -22.3) * mm, "end": v(89.55, -22.6) * mm});
            skLineSegment(sketch, "E1662", {"start": v(89.55, -22.6) * mm, "end": v(89.67, -22.88) * mm});
            skLineSegment(sketch, "E1663", {"start": v(89.67, -22.88) * mm, "end": v(89.8, -23.15) * mm});
            skLineSegment(sketch, "E1664", {"start": v(89.8, -23.15) * mm, "end": v(89.96, -23.42) * mm});
            skLineSegment(sketch, "E1665", {"start": v(89.96, -23.42) * mm, "end": v(90.12, -23.69) * mm});
            skLineSegment(sketch, "E1666", {"start": v(90.12, -23.69) * mm, "end": v(90.3, -23.94) * mm});
            skLineSegment(sketch, "E1667", {"start": v(90.3, -23.94) * mm, "end": v(90.5, -24.19) * mm});
            skLineSegment(sketch, "E1668", {"start": v(90.5, -24.19) * mm, "end": v(90.7, -24.43) * mm});
            skLineSegment(sketch, "E1669", {"start": v(90.7, -24.43) * mm, "end": v(90.92, -24.66) * mm});
            skLineSegment(sketch, "E1670", {"start": v(90.92, -24.66) * mm, "end": v(91.15, -24.88) * mm});
            skLineSegment(sketch, "E1671", {"start": v(91.15, -24.88) * mm, "end": v(91.39, -25.09) * mm});
            skLineSegment(sketch, "E1672", {"start": v(91.39, -25.09) * mm, "end": v(91.64, -25.28) * mm});
            skLineSegment(sketch, "E1673", {"start": v(91.64, -25.28) * mm, "end": v(91.9, -25.46) * mm});
            skLineSegment(sketch, "E1674", {"start": v(91.9, -25.46) * mm, "end": v(92.15, -25.62) * mm});
            skLineSegment(sketch, "E1675", {"start": v(92.15, -25.62) * mm, "end": v(92.42, -25.77) * mm});
            skLineSegment(sketch, "E1676", {"start": v(92.42, -25.77) * mm, "end": v(92.7, -25.9) * mm});
            skLineSegment(sketch, "E1677", {"start": v(92.7, -25.9) * mm, "end": v(92.99, -26.03) * mm});
            skLineSegment(sketch, "E1678", {"start": v(92.99, -26.03) * mm, "end": v(93.28, -26.14) * mm});
            skLineSegment(sketch, "E1679", {"start": v(93.28, -26.14) * mm, "end": v(93.58, -26.23) * mm});
            skLineSegment(sketch, "E1680", {"start": v(93.58, -26.23) * mm, "end": v(93.9, -26.3) * mm});
            skLineSegment(sketch, "E1681", {"start": v(93.9, -26.3) * mm, "end": v(94.2, -26.37) * mm});
            skLineSegment(sketch, "E1682", {"start": v(94.2, -26.37) * mm, "end": v(94.53, -26.42) * mm});
            skLineSegment(sketch, "E1683", {"start": v(94.53, -26.42) * mm, "end": v(94.86, -26.46) * mm});
            skLineSegment(sketch, "E1684", {"start": v(94.86, -26.46) * mm, "end": v(95.2, -26.48) * mm});
            skLineSegment(sketch, "E1685", {"start": v(95.2, -26.48) * mm, "end": v(95.54, -26.49) * mm});
            skLineSegment(sketch, "E1686", {"start": v(95.54, -26.49) * mm, "end": v(126.33, -26.49) * mm});
            skLineSegment(sketch, "E1687", {"start": v(126.33, -26.49) * mm, "end": v(126.67, -26.47) * mm});
            skLineSegment(sketch, "E1688", {"start": v(126.67, -26.47) * mm, "end": v(127, -26.42) * mm});
            skLineSegment(sketch, "E1689", {"start": v(127, -26.42) * mm, "end": v(127.32, -26.34) * mm});
            skLineSegment(sketch, "E1690", {"start": v(127.32, -26.34) * mm, "end": v(127.63, -26.23) * mm});
            skLineSegment(sketch, "E1691", {"start": v(127.63, -26.23) * mm, "end": v(127.92, -26.09) * mm});
            skLineSegment(sketch, "E1692", {"start": v(127.92, -26.09) * mm, "end": v(128.2, -25.92) * mm});
            skLineSegment(sketch, "E1693", {"start": v(128.2, -25.92) * mm, "end": v(128.45, -25.73) * mm});
            skLineSegment(sketch, "E1694", {"start": v(128.45, -25.73) * mm, "end": v(128.69, -25.51) * mm});
            skLineSegment(sketch, "E1695", {"start": v(128.69, -25.51) * mm, "end": v(128.9, -25.27) * mm});
            skLineSegment(sketch, "E1696", {"start": v(128.9, -25.27) * mm, "end": v(129.1, -25.02) * mm});
            skLineSegment(sketch, "E1697", {"start": v(129.1, -25.02) * mm, "end": v(129.26, -24.74) * mm});
            skLineSegment(sketch, "E1698", {"start": v(129.26, -24.74) * mm, "end": v(129.4, -24.45) * mm});
            skLineSegment(sketch, "E1699", {"start": v(129.4, -24.45) * mm, "end": v(129.52, -24.14) * mm});
            skLineSegment(sketch, "E1700", {"start": v(129.52, -24.14) * mm, "end": v(129.6, -23.83) * mm});
            skLineSegment(sketch, "E1701", {"start": v(129.6, -23.83) * mm, "end": v(129.65, -23.5) * mm});
            skLineSegment(sketch, "E1702", {"start": v(129.65, -23.5) * mm, "end": v(129.67, -23.15) * mm});
            skLineSegment(sketch, "E1703", {"start": v(129.67, -23.15) * mm, "end": v(129.67, -19.84) * mm});
            skLineSegment(sketch, "E1704", {"start": v(129.67, -19.84) * mm, "end": v(129.66, -19.7) * mm});
            skLineSegment(sketch, "E1705", {"start": v(129.66, -19.7) * mm, "end": v(129.64, -19.56) * mm});
            skLineSegment(sketch, "E1706", {"start": v(129.64, -19.56) * mm, "end": v(129.6, -19.43) * mm});
            skLineSegment(sketch, "E1707", {"start": v(129.6, -19.43) * mm, "end": v(129.57, -19.3) * mm});
            skLineSegment(sketch, "E1708", {"start": v(129.57, -19.3) * mm, "end": v(129.51, -19.18) * mm});
            skLineSegment(sketch, "E1709", {"start": v(129.51, -19.18) * mm, "end": v(129.45, -19.06) * mm});
            skLineSegment(sketch, "E1710", {"start": v(129.45, -19.06) * mm, "end": v(129.37, -18.95) * mm});
            skLineSegment(sketch, "E1711", {"start": v(129.37, -18.95) * mm, "end": v(129.3, -18.85) * mm});
            skLineSegment(sketch, "E1712", {"start": v(129.3, -18.85) * mm, "end": v(129.2, -18.75) * mm});
            skLineSegment(sketch, "E1713", {"start": v(129.2, -18.75) * mm, "end": v(129.1, -18.67) * mm});
            skLineSegment(sketch, "E1714", {"start": v(129.1, -18.67) * mm, "end": v(129, -18.59) * mm});
            skLineSegment(sketch, "E1715", {"start": v(129, -18.59) * mm, "end": v(128.88, -18.52) * mm});
            skLineSegment(sketch, "E1716", {"start": v(128.88, -18.52) * mm, "end": v(128.76, -18.46) * mm});
            skLineSegment(sketch, "E1717", {"start": v(128.76, -18.46) * mm, "end": v(128.63, -18.41) * mm});
            skLineSegment(sketch, "E1718", {"start": v(128.63, -18.41) * mm, "end": v(128.5, -18.38) * mm});
            skLineSegment(sketch, "E1719", {"start": v(128.5, -18.38) * mm, "end": v(128.36, -18.35) * mm});
            skLineSegment(sketch, "E1720", {"start": v(128.36, -18.35) * mm, "end": v(127.64, -18.25) * mm});
            skLineSegment(sketch, "E1721", {"start": v(127.64, -18.25) * mm, "end": v(126.94, -18.1) * mm});
            skLineSegment(sketch, "E1722", {"start": v(126.94, -18.1) * mm, "end": v(126.25, -17.94) * mm});
            skLineSegment(sketch, "E1723", {"start": v(126.25, -17.94) * mm, "end": v(125.57, -17.74) * mm});
            skLineSegment(sketch, "E1724", {"start": v(125.57, -17.74) * mm, "end": v(124.9, -17.52) * mm});
            skLineSegment(sketch, "E1725", {"start": v(124.9, -17.52) * mm, "end": v(124.26, -17.26) * mm});
            skLineSegment(sketch, "E1726", {"start": v(124.26, -17.26) * mm, "end": v(123.63, -16.97) * mm});
            skLineSegment(sketch, "E1727", {"start": v(123.63, -16.97) * mm, "end": v(123.01, -16.66) * mm});
            skLineSegment(sketch, "E1728", {"start": v(123.01, -16.66) * mm, "end": v(122.41, -16.31) * mm});
            skLineSegment(sketch, "E1729", {"start": v(122.41, -16.31) * mm, "end": v(121.83, -15.94) * mm});
            skLineSegment(sketch, "E1730", {"start": v(121.83, -15.94) * mm, "end": v(121.25, -15.53) * mm});
            skLineSegment(sketch, "E1731", {"start": v(121.25, -15.53) * mm, "end": v(120.7, -15.1) * mm});
            skLineSegment(sketch, "E1732", {"start": v(120.7, -15.1) * mm, "end": v(120.16, -14.63) * mm});
            skLineSegment(sketch, "E1733", {"start": v(120.16, -14.63) * mm, "end": v(119.63, -14.14) * mm});
            skLineSegment(sketch, "E1734", {"start": v(119.63, -14.14) * mm, "end": v(119.13, -13.62) * mm});
            skLineSegment(sketch, "E1735", {"start": v(119.13, -13.62) * mm, "end": v(118.63, -13.07) * mm});
            skLineSegment(sketch, "E1736", {"start": v(118.63, -13.07) * mm, "end": v(118.17, -12.5) * mm});
            skLineSegment(sketch, "E1737", {"start": v(118.17, -12.5) * mm, "end": v(117.73, -11.91) * mm});
            skLineSegment(sketch, "E1738", {"start": v(117.73, -11.91) * mm, "end": v(117.32, -11.32) * mm});
            skLineSegment(sketch, "E1739", {"start": v(117.32, -11.32) * mm, "end": v(116.94, -10.71) * mm});
            skLineSegment(sketch, "E1740", {"start": v(116.94, -10.71) * mm, "end": v(116.59, -10.1) * mm});
            skLineSegment(sketch, "E1741", {"start": v(116.59, -10.1) * mm, "end": v(116.27, -9.47) * mm});
            skLineSegment(sketch, "E1742", {"start": v(116.27, -9.47) * mm, "end": v(115.98, -8.83) * mm});
            skLineSegment(sketch, "E1743", {"start": v(115.98, -8.83) * mm, "end": v(115.72, -8.18) * mm});
            skLineSegment(sketch, "E1744", {"start": v(115.72, -8.18) * mm, "end": v(115.5, -7.52) * mm});
            skLineSegment(sketch, "E1745", {"start": v(115.5, -7.52) * mm, "end": v(115.3, -6.85) * mm});
            skLineSegment(sketch, "E1746", {"start": v(115.3, -6.85) * mm, "end": v(115.13, -6.17) * mm});
            skLineSegment(sketch, "E1747", {"start": v(115.13, -6.17) * mm, "end": v(114.99, -5.49) * mm});
            skLineSegment(sketch, "E1748", {"start": v(114.99, -5.49) * mm, "end": v(114.88, -4.79) * mm});
            skLineSegment(sketch, "E1749", {"start": v(114.88, -4.79) * mm, "end": v(114.8, -4.08) * mm});
            skLineSegment(sketch, "E1750", {"start": v(114.8, -4.08) * mm, "end": v(114.76, -3.36) * mm});
            skLineSegment(sketch, "E1751", {"start": v(114.76, -3.36) * mm, "end": v(114.74, -2.63) * mm});
            skLineSegment(sketch, "E1752", {"start": v(114.74, -2.63) * mm, "end": v(114.76, -1.81) * mm});
            skLineSegment(sketch, "E1753", {"start": v(114.76, -1.81) * mm, "end": v(114.82, -1) * mm});
            skLineSegment(sketch, "E1754", {"start": v(114.82, -1) * mm, "end": v(114.9, -0.22) * mm});
            skLineSegment(sketch, "E1755", {"start": v(114.9, -0.22) * mm, "end": v(115.03, 0.55) * mm});
            skLineSegment(sketch, "E1756", {"start": v(115.03, 0.55) * mm, "end": v(115.2, 1.31) * mm});
            skLineSegment(sketch, "E1757", {"start": v(115.2, 1.31) * mm, "end": v(115.4, 2.06) * mm});
            skLineSegment(sketch, "E1758", {"start": v(115.4, 2.06) * mm, "end": v(115.63, 2.79) * mm});
            skLineSegment(sketch, "E1759", {"start": v(115.63, 2.79) * mm, "end": v(115.9, 3.5) * mm});
            skLineSegment(sketch, "E1760", {"start": v(115.9, 3.5) * mm, "end": v(116.21, 4.2) * mm});
            skLineSegment(sketch, "E1761", {"start": v(116.21, 4.2) * mm, "end": v(116.56, 4.88) * mm});
            skLineSegment(sketch, "E1762", {"start": v(116.56, 4.88) * mm, "end": v(116.94, 5.55) * mm});
            skLineSegment(sketch, "E1763", {"start": v(116.94, 5.55) * mm, "end": v(117.35, 6.2) * mm});
            skLineSegment(sketch, "E1764", {"start": v(117.35, 6.2) * mm, "end": v(117.8, 6.84) * mm});
            skLineSegment(sketch, "E1765", {"start": v(117.8, 6.84) * mm, "end": v(118.3, 7.46) * mm});
            skLineSegment(sketch, "E1766", {"start": v(118.3, 7.46) * mm, "end": v(118.81, 8.06) * mm});
            skLineSegment(sketch, "E1767", {"start": v(118.81, 8.06) * mm, "end": v(119.37, 8.65) * mm});
            skLineSegment(sketch, "E1768", {"start": v(119.37, 8.65) * mm, "end": v(119.95, 9.21) * mm});
            skLineSegment(sketch, "E1769", {"start": v(119.95, 9.21) * mm, "end": v(120.56, 9.74) * mm});
            skLineSegment(sketch, "E1770", {"start": v(120.56, 9.74) * mm, "end": v(121.17, 10.23) * mm});
            skLineSegment(sketch, "E1771", {"start": v(121.17, 10.23) * mm, "end": v(121.8, 10.68) * mm});
            skLineSegment(sketch, "E1772", {"start": v(121.8, 10.68) * mm, "end": v(122.46, 11.1) * mm});
            skLineSegment(sketch, "E1773", {"start": v(122.46, 11.1) * mm, "end": v(123.12, 11.48) * mm});
            skLineSegment(sketch, "E1774", {"start": v(123.12, 11.48) * mm, "end": v(123.8, 11.83) * mm});
            skLineSegment(sketch, "E1775", {"start": v(123.8, 11.83) * mm, "end": v(124.5, 12.14) * mm});
            skLineSegment(sketch, "E1776", {"start": v(124.5, 12.14) * mm, "end": v(125.21, 12.4) * mm});
            skLineSegment(sketch, "E1777", {"start": v(125.21, 12.4) * mm, "end": v(125.94, 12.65) * mm});
            skLineSegment(sketch, "E1778", {"start": v(125.94, 12.65) * mm, "end": v(126.68, 12.85) * mm});
            skLineSegment(sketch, "E1779", {"start": v(126.68, 12.85) * mm, "end": v(127.44, 13.01) * mm});
            skLineSegment(sketch, "E1780", {"start": v(127.44, 13.01) * mm, "end": v(128.22, 13.14) * mm});
            skLineSegment(sketch, "E1781", {"start": v(128.22, 13.14) * mm, "end": v(129, 13.23) * mm});
            skLineSegment(sketch, "E1782", {"start": v(129, 13.23) * mm, "end": v(129.8, 13.29) * mm});
            skLineSegment(sketch, "E1783", {"start": v(129.8, 13.29) * mm, "end": v(130.62, 13.3) * mm});
            skLineSegment(sketch, "E1784", {"start": v(130.62, 13.3) * mm, "end": v(131.45, 13.29) * mm});
            skLineSegment(sketch, "E1785", {"start": v(131.45, 13.29) * mm, "end": v(132.26, 13.23) * mm});
            skLineSegment(sketch, "E1786", {"start": v(132.26, 13.23) * mm, "end": v(133.05, 13.14) * mm});
            skLineSegment(sketch, "E1787", {"start": v(133.05, 13.14) * mm, "end": v(133.83, 13.01) * mm});
            skLineSegment(sketch, "E1788", {"start": v(133.83, 13.01) * mm, "end": v(134.6, 12.85) * mm});
            skLineSegment(sketch, "E1789", {"start": v(134.6, 12.85) * mm, "end": v(135.34, 12.65) * mm});
            skLineSegment(sketch, "E1790", {"start": v(135.34, 12.65) * mm, "end": v(136.07, 12.41) * mm});
            skLineSegment(sketch, "E1791", {"start": v(136.07, 12.41) * mm, "end": v(136.79, 12.14) * mm});
            skLineSegment(sketch, "E1792", {"start": v(136.79, 12.14) * mm, "end": v(137.49, 11.83) * mm});
            skLineSegment(sketch, "E1793", {"start": v(137.49, 11.83) * mm, "end": v(138.17, 11.5) * mm});
            skLineSegment(sketch, "E1794", {"start": v(138.17, 11.5) * mm, "end": v(138.84, 11.11) * mm});
            skLineSegment(sketch, "E1795", {"start": v(138.84, 11.11) * mm, "end": v(139.5, 10.7) * mm});
            skLineSegment(sketch, "E1796", {"start": v(139.5, 10.7) * mm, "end": v(140.13, 10.24) * mm});
            skLineSegment(sketch, "E1797", {"start": v(140.13, 10.24) * mm, "end": v(140.74, 9.76) * mm});
            skLineSegment(sketch, "E1798", {"start": v(140.74, 9.76) * mm, "end": v(141.35, 9.24) * mm});
            skLineSegment(sketch, "E1799", {"start": v(141.35, 9.24) * mm, "end": v(141.93, 8.68) * mm});
            skLineSegment(sketch, "E1800", {"start": v(141.93, 8.68) * mm, "end": v(142.49, 8.1) * mm});
            skLineSegment(sketch, "E1801", {"start": v(142.49, 8.1) * mm, "end": v(143.01, 7.5) * mm});
            skLineSegment(sketch, "E1802", {"start": v(143.01, 7.5) * mm, "end": v(143.5, 6.87) * mm});
            skLineSegment(sketch, "E1803", {"start": v(143.5, 6.87) * mm, "end": v(143.95, 6.24) * mm});
            skLineSegment(sketch, "E1804", {"start": v(143.95, 6.24) * mm, "end": v(144.36, 5.59) * mm});
            skLineSegment(sketch, "E1805", {"start": v(144.36, 5.59) * mm, "end": v(144.74, 4.92) * mm});
            skLineSegment(sketch, "E1806", {"start": v(144.74, 4.92) * mm, "end": v(145.09, 4.23) * mm});
            skLineSegment(sketch, "E1807", {"start": v(145.09, 4.23) * mm, "end": v(145.4, 3.53) * mm});
            skLineSegment(sketch, "E1808", {"start": v(145.4, 3.53) * mm, "end": v(145.67, 2.82) * mm});
            skLineSegment(sketch, "E1809", {"start": v(145.67, 2.82) * mm, "end": v(145.9, 2.09) * mm});
            skLineSegment(sketch, "E1810", {"start": v(145.9, 2.09) * mm, "end": v(146.1, 1.34) * mm});
            skLineSegment(sketch, "E1811", {"start": v(146.1, 1.34) * mm, "end": v(146.27, 0.57) * mm});
            skLineSegment(sketch, "E1812", {"start": v(146.27, 0.57) * mm, "end": v(146.4, -0.2) * mm});
            skLineSegment(sketch, "E1813", {"start": v(146.4, -0.2) * mm, "end": v(146.48, -1) * mm});
            skLineSegment(sketch, "E1814", {"start": v(146.48, -1) * mm, "end": v(146.54, -1.8) * mm});
            skLineSegment(sketch, "E1815", {"start": v(146.54, -1.8) * mm, "end": v(146.56, -2.63) * mm});
            skLineSegment(sketch, "E1816", {"start": v(146.56, -2.63) * mm, "end": v(146.54, -3.36) * mm});
            skLineSegment(sketch, "E1817", {"start": v(146.54, -3.36) * mm, "end": v(146.5, -4.08) * mm});
            skLineSegment(sketch, "E1818", {"start": v(146.5, -4.08) * mm, "end": v(146.42, -4.79) * mm});
            skLineSegment(sketch, "E1819", {"start": v(146.42, -4.79) * mm, "end": v(146.31, -5.48) * mm});
            skLineSegment(sketch, "E1820", {"start": v(146.31, -5.48) * mm, "end": v(146.17, -6.17) * mm});
            skLineSegment(sketch, "E1821", {"start": v(146.17, -6.17) * mm, "end": v(146, -6.85) * mm});
            skLineSegment(sketch, "E1822", {"start": v(146, -6.85) * mm, "end": v(145.8, -7.52) * mm});
            skLineSegment(sketch, "E1823", {"start": v(145.8, -7.52) * mm, "end": v(145.58, -8.18) * mm});
            skLineSegment(sketch, "E1824", {"start": v(145.58, -8.18) * mm, "end": v(145.32, -8.83) * mm});
            skLineSegment(sketch, "E1825", {"start": v(145.32, -8.83) * mm, "end": v(145.03, -9.47) * mm});
            skLineSegment(sketch, "E1826", {"start": v(145.03, -9.47) * mm, "end": v(144.7, -10.1) * mm});
            skLineSegment(sketch, "E1827", {"start": v(144.7, -10.1) * mm, "end": v(144.36, -10.71) * mm});
            skLineSegment(sketch, "E1828", {"start": v(144.36, -10.71) * mm, "end": v(143.97, -11.32) * mm});
            skLineSegment(sketch, "E1829", {"start": v(143.97, -11.32) * mm, "end": v(143.56, -11.91) * mm});
            skLineSegment(sketch, "E1830", {"start": v(143.56, -11.91) * mm, "end": v(143.12, -12.5) * mm});
            skLineSegment(sketch, "E1831", {"start": v(143.12, -12.5) * mm, "end": v(142.65, -13.07) * mm});
            skLineSegment(sketch, "E1832", {"start": v(142.65, -13.07) * mm, "end": v(142.16, -13.62) * mm});
            skLineSegment(sketch, "E1833", {"start": v(142.16, -13.62) * mm, "end": v(141.65, -14.14) * mm});
            skLineSegment(sketch, "E1834", {"start": v(141.65, -14.14) * mm, "end": v(141.12, -14.63) * mm});
            skLineSegment(sketch, "E1835", {"start": v(141.12, -14.63) * mm, "end": v(140.58, -15.1) * mm});
            skLineSegment(sketch, "E1836", {"start": v(140.58, -15.1) * mm, "end": v(140.02, -15.53) * mm});
            skLineSegment(sketch, "E1837", {"start": v(140.02, -15.53) * mm, "end": v(139.45, -15.94) * mm});
            skLineSegment(sketch, "E1838", {"start": v(139.45, -15.94) * mm, "end": v(138.86, -16.31) * mm});
            skLineSegment(sketch, "E1839", {"start": v(138.86, -16.31) * mm, "end": v(138.26, -16.66) * mm});
            skLineSegment(sketch, "E1840", {"start": v(138.26, -16.66) * mm, "end": v(137.64, -16.97) * mm});
            skLineSegment(sketch, "E1841", {"start": v(137.64, -16.97) * mm, "end": v(137, -17.26) * mm});
            skLineSegment(sketch, "E1842", {"start": v(137, -17.26) * mm, "end": v(136.35, -17.52) * mm});
            skLineSegment(sketch, "E1843", {"start": v(136.35, -17.52) * mm, "end": v(135.69, -17.74) * mm});
            skLineSegment(sketch, "E1844", {"start": v(135.69, -17.74) * mm, "end": v(135.01, -17.94) * mm});
            skLineSegment(sketch, "E1845", {"start": v(135.01, -17.94) * mm, "end": v(134.32, -18.1) * mm});
            skLineSegment(sketch, "E1846", {"start": v(134.32, -18.1) * mm, "end": v(133.6, -18.25) * mm});
            skLineSegment(sketch, "E1847", {"start": v(133.6, -18.25) * mm, "end": v(132.89, -18.35) * mm});
            skLineSegment(sketch, "E1848", {"start": v(132.89, -18.35) * mm, "end": v(132.75, -18.38) * mm});
            skLineSegment(sketch, "E1849", {"start": v(132.75, -18.38) * mm, "end": v(132.62, -18.41) * mm});
            skLineSegment(sketch, "E1850", {"start": v(132.62, -18.41) * mm, "end": v(132.5, -18.46) * mm});
            skLineSegment(sketch, "E1851", {"start": v(132.5, -18.46) * mm, "end": v(132.37, -18.52) * mm});
            skLineSegment(sketch, "E1852", {"start": v(132.37, -18.52) * mm, "end": v(132.25, -18.59) * mm});
            skLineSegment(sketch, "E1853", {"start": v(132.25, -18.59) * mm, "end": v(132.15, -18.67) * mm});
            skLineSegment(sketch, "E1854", {"start": v(132.15, -18.67) * mm, "end": v(132.05, -18.75) * mm});
            skLineSegment(sketch, "E1855", {"start": v(132.05, -18.75) * mm, "end": v(131.96, -18.85) * mm});
            skLineSegment(sketch, "E1856", {"start": v(131.96, -18.85) * mm, "end": v(131.87, -18.95) * mm});
            skLineSegment(sketch, "E1857", {"start": v(131.87, -18.95) * mm, "end": v(131.8, -19.06) * mm});
            skLineSegment(sketch, "E1858", {"start": v(131.8, -19.06) * mm, "end": v(131.73, -19.18) * mm});
            skLineSegment(sketch, "E1859", {"start": v(131.73, -19.18) * mm, "end": v(131.68, -19.3) * mm});
            skLineSegment(sketch, "E1860", {"start": v(131.68, -19.3) * mm, "end": v(131.64, -19.43) * mm});
            skLineSegment(sketch, "E1861", {"start": v(131.64, -19.43) * mm, "end": v(131.6, -19.56) * mm});
            skLineSegment(sketch, "E1862", {"start": v(131.6, -19.56) * mm, "end": v(131.59, -19.7) * mm});
            skLineSegment(sketch, "E1863", {"start": v(131.59, -19.7) * mm, "end": v(131.58, -19.84) * mm});
            skLineSegment(sketch, "E1864", {"start": v(131.58, -19.84) * mm, "end": v(131.58, -23.15) * mm});
            skLineSegment(sketch, "E1865", {"start": v(131.58, -23.15) * mm, "end": v(131.6, -23.5) * mm});
            skLineSegment(sketch, "E1866", {"start": v(131.6, -23.5) * mm, "end": v(131.65, -23.83) * mm});
            skLineSegment(sketch, "E1867", {"start": v(131.65, -23.83) * mm, "end": v(131.73, -24.14) * mm});
            skLineSegment(sketch, "E1868", {"start": v(131.73, -24.14) * mm, "end": v(131.84, -24.45) * mm});
            skLineSegment(sketch, "E1869", {"start": v(131.84, -24.45) * mm, "end": v(131.99, -24.74) * mm});
            skLineSegment(sketch, "E1870", {"start": v(131.99, -24.74) * mm, "end": v(132.15, -25.02) * mm});
            skLineSegment(sketch, "E1871", {"start": v(132.15, -25.02) * mm, "end": v(132.34, -25.27) * mm});
            skLineSegment(sketch, "E1872", {"start": v(132.34, -25.27) * mm, "end": v(132.56, -25.51) * mm});
            skLineSegment(sketch, "E1873", {"start": v(132.56, -25.51) * mm, "end": v(132.8, -25.73) * mm});
            skLineSegment(sketch, "E1874", {"start": v(132.8, -25.73) * mm, "end": v(133.05, -25.92) * mm});
            skLineSegment(sketch, "E1875", {"start": v(133.05, -25.92) * mm, "end": v(133.33, -26.09) * mm});
            skLineSegment(sketch, "E1876", {"start": v(133.33, -26.09) * mm, "end": v(133.62, -26.23) * mm});
            skLineSegment(sketch, "E1877", {"start": v(133.62, -26.23) * mm, "end": v(133.93, -26.34) * mm});
            skLineSegment(sketch, "E1878", {"start": v(133.93, -26.34) * mm, "end": v(134.25, -26.42) * mm});
            skLineSegment(sketch, "E1879", {"start": v(134.25, -26.42) * mm, "end": v(134.58, -26.47) * mm});
            skLineSegment(sketch, "E1880", {"start": v(134.58, -26.47) * mm, "end": v(134.92, -26.49) * mm});
            skLineSegment(sketch, "E1881", {"start": v(134.92, -26.49) * mm, "end": v(153.43, -26.49) * mm});
            skLineSegment(sketch, "E1882", {"start": v(153.43, -26.49) * mm, "end": v(153.64, -26.48) * mm});
            skLineSegment(sketch, "E1883", {"start": v(153.64, -26.48) * mm, "end": v(153.85, -26.47) * mm});
            skLineSegment(sketch, "E1884", {"start": v(153.85, -26.47) * mm, "end": v(154.06, -26.45) * mm});
            skLineSegment(sketch, "E1885", {"start": v(154.06, -26.45) * mm, "end": v(154.26, -26.42) * mm});
            skLineSegment(sketch, "E1886", {"start": v(154.26, -26.42) * mm, "end": v(154.45, -26.38) * mm});
            skLineSegment(sketch, "E1887", {"start": v(154.45, -26.38) * mm, "end": v(154.64, -26.33) * mm});
            skLineSegment(sketch, "E1888", {"start": v(154.64, -26.33) * mm, "end": v(154.83, -26.27) * mm});
            skLineSegment(sketch, "E1889", {"start": v(154.83, -26.27) * mm, "end": v(155, -26.2) * mm});
            skLineSegment(sketch, "E1890", {"start": v(155, -26.2) * mm, "end": v(155.19, -26.13) * mm});
            skLineSegment(sketch, "E1891", {"start": v(155.19, -26.13) * mm, "end": v(155.36, -26.05) * mm});
            skLineSegment(sketch, "E1892", {"start": v(155.36, -26.05) * mm, "end": v(155.52, -25.96) * mm});
            skLineSegment(sketch, "E1893", {"start": v(155.52, -25.96) * mm, "end": v(155.68, -25.86) * mm});
            skLineSegment(sketch, "E1894", {"start": v(155.68, -25.86) * mm, "end": v(155.84, -25.75) * mm});
            skLineSegment(sketch, "E1895", {"start": v(155.84, -25.75) * mm, "end": v(156, -25.63) * mm});
            skLineSegment(sketch, "E1896", {"start": v(156, -25.63) * mm, "end": v(156.14, -25.5) * mm});
            skLineSegment(sketch, "E1897", {"start": v(156.14, -25.5) * mm, "end": v(156.28, -25.37) * mm});
            skLineSegment(sketch, "E1898", {"start": v(156.28, -25.37) * mm, "end": v(156.41, -25.23) * mm});
            skLineSegment(sketch, "E1899", {"start": v(156.41, -25.23) * mm, "end": v(156.54, -25.09) * mm});
            skLineSegment(sketch, "E1900", {"start": v(156.54, -25.09) * mm, "end": v(156.66, -24.94) * mm});
            skLineSegment(sketch, "E1901", {"start": v(156.66, -24.94) * mm, "end": v(156.77, -24.78) * mm});
            skLineSegment(sketch, "E1902", {"start": v(156.77, -24.78) * mm, "end": v(156.87, -24.62) * mm});
            skLineSegment(sketch, "E1903", {"start": v(156.87, -24.62) * mm, "end": v(156.96, -24.45) * mm});
            skLineSegment(sketch, "E1904", {"start": v(156.96, -24.45) * mm, "end": v(157.04, -24.28) * mm});
            skLineSegment(sketch, "E1905", {"start": v(157.04, -24.28) * mm, "end": v(157.11, -24.1) * mm});
            skLineSegment(sketch, "E1906", {"start": v(157.11, -24.1) * mm, "end": v(157.18, -23.92) * mm});
            skLineSegment(sketch, "E1907", {"start": v(157.18, -23.92) * mm, "end": v(157.24, -23.74) * mm});
            skLineSegment(sketch, "E1908", {"start": v(157.24, -23.74) * mm, "end": v(157.28, -23.55) * mm});
            skLineSegment(sketch, "E1909", {"start": v(157.28, -23.55) * mm, "end": v(157.32, -23.35) * mm});
            skLineSegment(sketch, "E1910", {"start": v(157.32, -23.35) * mm, "end": v(157.35, -23.15) * mm});
            skLineSegment(sketch, "E1911", {"start": v(157.35, -23.15) * mm, "end": v(157.38, -22.95) * mm});
            skLineSegment(sketch, "E1912", {"start": v(157.38, -22.95) * mm, "end": v(157.39, -22.74) * mm});
            skLineSegment(sketch, "E1913", {"start": v(157.39, -22.74) * mm, "end": v(157.4, -22.53) * mm});
            skLineSegment(sketch, "E1914", {"start": v(157.4, -22.53) * mm, "end": v(157.4, 12.26) * mm});
            skLineSegment(sketch, "E1915", {"start": v(157.4, 12.26) * mm, "end": v(157.4, 12.34) * mm});
            skLineSegment(sketch, "E1916", {"start": v(157.4, 12.34) * mm, "end": v(157.4, 12.42) * mm});
            skLineSegment(sketch, "E1917", {"start": v(157.4, 12.42) * mm, "end": v(157.43, 12.5) * mm});
            skLineSegment(sketch, "E1918", {"start": v(157.43, 12.5) * mm, "end": v(157.45, 12.57) * mm});
            skLineSegment(sketch, "E1919", {"start": v(157.45, 12.57) * mm, "end": v(157.49, 12.63) * mm});
            skLineSegment(sketch, "E1920", {"start": v(157.49, 12.63) * mm, "end": v(157.53, 12.7) * mm});
            skLineSegment(sketch, "E1921", {"start": v(157.53, 12.7) * mm, "end": v(157.57, 12.76) * mm});
            skLineSegment(sketch, "E1922", {"start": v(157.57, 12.76) * mm, "end": v(157.62, 12.81) * mm});
            skLineSegment(sketch, "E1923", {"start": v(157.62, 12.81) * mm, "end": v(157.68, 12.86) * mm});
            skLineSegment(sketch, "E1924", {"start": v(157.68, 12.86) * mm, "end": v(157.74, 12.9) * mm});
            skLineSegment(sketch, "E1925", {"start": v(157.74, 12.9) * mm, "end": v(157.8, 12.95) * mm});
            skLineSegment(sketch, "E1926", {"start": v(157.8, 12.95) * mm, "end": v(157.87, 12.98) * mm});
            skLineSegment(sketch, "E1927", {"start": v(157.87, 12.98) * mm, "end": v(157.94, 13) * mm});
            skLineSegment(sketch, "E1928", {"start": v(157.94, 13) * mm, "end": v(158.01, 13.02) * mm});
            skLineSegment(sketch, "E1929", {"start": v(158.01, 13.02) * mm, "end": v(158.09, 13.04) * mm});
            skLineSegment(sketch, "E1930", {"start": v(158.09, 13.04) * mm, "end": v(158.17, 13.04) * mm});
            skLineSegment(sketch, "E1931", {"start": v(158.17, 13.04) * mm, "end": v(171, 13.04) * mm});
            skLineSegment(sketch, "E1932", {"start": v(171, 13.04) * mm, "end": v(171.28, 13.02) * mm});
            skLineSegment(sketch, "E1933", {"start": v(171.28, 13.02) * mm, "end": v(171.55, 13) * mm});
            skLineSegment(sketch, "E1934", {"start": v(171.55, 13) * mm, "end": v(171.83, 12.97) * mm});
            skLineSegment(sketch, "E1935", {"start": v(171.83, 12.97) * mm, "end": v(172.1, 12.93) * mm});
            skLineSegment(sketch, "E1936", {"start": v(172.1, 12.93) * mm, "end": v(172.37, 12.88) * mm});
            skLineSegment(sketch, "E1937", {"start": v(172.37, 12.88) * mm, "end": v(172.65, 12.83) * mm});
            skLineSegment(sketch, "E1938", {"start": v(172.65, 12.83) * mm, "end": v(172.92, 12.76) * mm});
            skLineSegment(sketch, "E1939", {"start": v(172.92, 12.76) * mm, "end": v(173.2, 12.7) * mm});
            skLineSegment(sketch, "E1940", {"start": v(173.2, 12.7) * mm, "end": v(173.46, 12.6) * mm});
            skLineSegment(sketch, "E1941", {"start": v(173.46, 12.6) * mm, "end": v(173.73, 12.52) * mm});
            skLineSegment(sketch, "E1942", {"start": v(173.73, 12.52) * mm, "end": v(174, 12.42) * mm});
            skLineSegment(sketch, "E1943", {"start": v(174, 12.42) * mm, "end": v(174.27, 12.31) * mm});
            skLineSegment(sketch, "E1944", {"start": v(174.27, 12.31) * mm, "end": v(174.54, 12.2) * mm});
            skLineSegment(sketch, "E1945", {"start": v(174.54, 12.2) * mm, "end": v(174.81, 12.07) * mm});
            skLineSegment(sketch, "E1946", {"start": v(174.81, 12.07) * mm, "end": v(175.08, 11.94) * mm});
            skLineSegment(sketch, "E1947", {"start": v(175.08, 11.94) * mm, "end": v(175.56, 11.67) * mm});
            skLineSegment(sketch, "E1948", {"start": v(175.56, 11.67) * mm, "end": v(176.02, 11.37) * mm});
            skLineSegment(sketch, "E1949", {"start": v(176.02, 11.37) * mm, "end": v(176.44, 11.05) * mm});
            skLineSegment(sketch, "E1950", {"start": v(176.44, 11.05) * mm, "end": v(176.83, 10.7) * mm});
            skLineSegment(sketch, "E1951", {"start": v(176.83, 10.7) * mm, "end": v(177.2, 10.33) * mm});
            skLineSegment(sketch, "E1952", {"start": v(177.2, 10.33) * mm, "end": v(177.52, 9.94) * mm});
            skLineSegment(sketch, "E1953", {"start": v(177.52, 9.94) * mm, "end": v(177.82, 9.52) * mm});
            skLineSegment(sketch, "E1954", {"start": v(177.82, 9.52) * mm, "end": v(178.1, 9.08) * mm});
            skLineSegment(sketch, "E1955", {"start": v(178.1, 9.08) * mm, "end": v(178.33, 8.6) * mm});
            skLineSegment(sketch, "E1956", {"start": v(178.33, 8.6) * mm, "end": v(178.53, 8.12) * mm});
            skLineSegment(sketch, "E1957", {"start": v(178.53, 8.12) * mm, "end": v(178.7, 7.6) * mm});
            skLineSegment(sketch, "E1958", {"start": v(178.7, 7.6) * mm, "end": v(178.85, 7.06) * mm});
            skLineSegment(sketch, "E1959", {"start": v(178.85, 7.06) * mm, "end": v(178.96, 6.5) * mm});
            skLineSegment(sketch, "E1960", {"start": v(178.96, 6.5) * mm, "end": v(179.04, 5.92) * mm});
            skLineSegment(sketch, "E1961", {"start": v(179.04, 5.92) * mm, "end": v(179.09, 5.3) * mm});
            skLineSegment(sketch, "E1962", {"start": v(179.09, 5.3) * mm, "end": v(179.1, 4.67) * mm});
            skLineSegment(sketch, "E1963", {"start": v(179.1, 4.67) * mm, "end": v(179.09, 4.04) * mm});
            skLineSegment(sketch, "E1964", {"start": v(179.09, 4.04) * mm, "end": v(179.04, 3.43) * mm});
            skLineSegment(sketch, "E1965", {"start": v(179.04, 3.43) * mm, "end": v(178.96, 2.85) * mm});
            skLineSegment(sketch, "E1966", {"start": v(178.96, 2.85) * mm, "end": v(178.85, 2.28) * mm});
            skLineSegment(sketch, "E1967", {"start": v(178.85, 2.28) * mm, "end": v(178.7, 1.74) * mm});
            skLineSegment(sketch, "E1968", {"start": v(178.7, 1.74) * mm, "end": v(178.53, 1.23) * mm});
            skLineSegment(sketch, "E1969", {"start": v(178.53, 1.23) * mm, "end": v(178.33, 0.74) * mm});
            skLineSegment(sketch, "E1970", {"start": v(178.33, 0.74) * mm, "end": v(178.1, 0.27) * mm});
            skLineSegment(sketch, "E1971", {"start": v(178.1, 0.27) * mm, "end": v(177.82, -0.17) * mm});
            skLineSegment(sketch, "E1972", {"start": v(177.82, -0.17) * mm, "end": v(177.52, -0.6) * mm});
            skLineSegment(sketch, "E1973", {"start": v(177.52, -0.6) * mm, "end": v(177.2, -0.99) * mm});
            skLineSegment(sketch, "E1974", {"start": v(177.2, -0.99) * mm, "end": v(176.83, -1.36) * mm});
            skLineSegment(sketch, "E1975", {"start": v(176.83, -1.36) * mm, "end": v(176.44, -1.7) * mm});
            skLineSegment(sketch, "E1976", {"start": v(176.44, -1.7) * mm, "end": v(176.02, -2.02) * mm});
            skLineSegment(sketch, "E1977", {"start": v(176.02, -2.02) * mm, "end": v(175.57, -2.32) * mm});
            skLineSegment(sketch, "E1978", {"start": v(175.57, -2.32) * mm, "end": v(175.08, -2.6) * mm});
            skLineSegment(sketch, "E1979", {"start": v(175.08, -2.6) * mm, "end": v(174.8, -2.73) * mm});
            skLineSegment(sketch, "E1980", {"start": v(174.8, -2.73) * mm, "end": v(174.52, -2.86) * mm});
            skLineSegment(sketch, "E1981", {"start": v(174.52, -2.86) * mm, "end": v(174.24, -2.98) * mm});
            skLineSegment(sketch, "E1982", {"start": v(174.24, -2.98) * mm, "end": v(173.97, -3.1) * mm});
            skLineSegment(sketch, "E1983", {"start": v(173.97, -3.1) * mm, "end": v(173.7, -3.2) * mm});
            skLineSegment(sketch, "E1984", {"start": v(173.7, -3.2) * mm, "end": v(173.41, -3.3) * mm});
            skLineSegment(sketch, "E1985", {"start": v(173.41, -3.3) * mm, "end": v(173.14, -3.38) * mm});
            skLineSegment(sketch, "E1986", {"start": v(173.14, -3.38) * mm, "end": v(172.87, -3.46) * mm});
            skLineSegment(sketch, "E1987", {"start": v(172.87, -3.46) * mm, "end": v(172.6, -3.52) * mm});
            skLineSegment(sketch, "E1988", {"start": v(172.6, -3.52) * mm, "end": v(172.33, -3.58) * mm});
            skLineSegment(sketch, "E1989", {"start": v(172.33, -3.58) * mm, "end": v(172.06, -3.63) * mm});
            skLineSegment(sketch, "E1990", {"start": v(172.06, -3.63) * mm, "end": v(171.79, -3.67) * mm});
            skLineSegment(sketch, "E1991", {"start": v(171.79, -3.67) * mm, "end": v(171.52, -3.7) * mm});
            skLineSegment(sketch, "E1992", {"start": v(171.52, -3.7) * mm, "end": v(171.26, -3.73) * mm});
            skLineSegment(sketch, "E1993", {"start": v(171.26, -3.73) * mm, "end": v(171, -3.74) * mm});
            skLineSegment(sketch, "E1994", {"start": v(171, -3.74) * mm, "end": v(161.26, -3.75) * mm});
            skLineSegment(sketch, "E1995", {"start": v(161.26, -3.75) * mm, "end": v(161.12, -3.75) * mm});
            skLineSegment(sketch, "E1996", {"start": v(161.12, -3.75) * mm, "end": v(160.99, -3.77) * mm});
            skLineSegment(sketch, "E1997", {"start": v(160.99, -3.77) * mm, "end": v(160.85, -3.8) * mm});
            skLineSegment(sketch, "E1998", {"start": v(160.85, -3.8) * mm, "end": v(160.73, -3.85) * mm});
            skLineSegment(sketch, "E1999", {"start": v(160.73, -3.85) * mm, "end": v(160.6, -3.91) * mm});
            skLineSegment(sketch, "E2000", {"start": v(160.6, -3.91) * mm, "end": v(160.5, -3.98) * mm});
            skLineSegment(sketch, "E2001", {"start": v(160.5, -3.98) * mm, "end": v(160.4, -4.06) * mm});
            skLineSegment(sketch, "E2002", {"start": v(160.4, -4.06) * mm, "end": v(160.3, -4.15) * mm});
            skLineSegment(sketch, "E2003", {"start": v(160.3, -4.15) * mm, "end": v(160.2, -4.24) * mm});
            skLineSegment(sketch, "E2004", {"start": v(160.2, -4.24) * mm, "end": v(160.13, -4.35) * mm});
            skLineSegment(sketch, "E2005", {"start": v(160.13, -4.35) * mm, "end": v(160.06, -4.46) * mm});
            skLineSegment(sketch, "E2006", {"start": v(160.06, -4.46) * mm, "end": v(160, -4.58) * mm});
            skLineSegment(sketch, "E2007", {"start": v(160, -4.58) * mm, "end": v(159.95, -4.7) * mm});
            skLineSegment(sketch, "E2008", {"start": v(159.95, -4.7) * mm, "end": v(159.92, -4.84) * mm});
            skLineSegment(sketch, "E2009", {"start": v(159.92, -4.84) * mm, "end": v(159.9, -4.98) * mm});
            skLineSegment(sketch, "E2010", {"start": v(159.9, -4.98) * mm, "end": v(159.9, -5.11) * mm});
            skLineSegment(sketch, "E2011", {"start": v(159.9, -5.11) * mm, "end": v(159.9, -5.43) * mm});
            skLineSegment(sketch, "E2012", {"start": v(159.9, -5.43) * mm, "end": v(159.9, -5.55) * mm});
            skLineSegment(sketch, "E2013", {"start": v(159.9, -5.55) * mm, "end": v(159.9, -5.67) * mm});
            skLineSegment(sketch, "E2014", {"start": v(159.9, -5.67) * mm, "end": v(159.92, -5.79) * mm});
            skLineSegment(sketch, "E2015", {"start": v(159.92, -5.79) * mm, "end": v(159.94, -5.9) * mm});
            skLineSegment(sketch, "E2016", {"start": v(159.94, -5.9) * mm, "end": v(159.97, -6.02) * mm});
            skLineSegment(sketch, "E2017", {"start": v(159.97, -6.02) * mm, "end": v(160, -6.13) * mm});
            skLineSegment(sketch, "E2018", {"start": v(160, -6.13) * mm, "end": v(160.03, -6.24) * mm});
            skLineSegment(sketch, "E2019", {"start": v(160.03, -6.24) * mm, "end": v(160.08, -6.35) * mm});
            skLineSegment(sketch, "E2020", {"start": v(160.08, -6.35) * mm, "end": v(160.12, -6.46) * mm});
            skLineSegment(sketch, "E2021", {"start": v(160.12, -6.46) * mm, "end": v(160.18, -6.56) * mm});
            skLineSegment(sketch, "E2022", {"start": v(160.18, -6.56) * mm, "end": v(160.23, -6.67) * mm});
            skLineSegment(sketch, "E2023", {"start": v(160.23, -6.67) * mm, "end": v(160.3, -6.76) * mm});
            skLineSegment(sketch, "E2024", {"start": v(160.3, -6.76) * mm, "end": v(160.36, -6.86) * mm});
            skLineSegment(sketch, "E2025", {"start": v(160.36, -6.86) * mm, "end": v(160.44, -6.95) * mm});
            skLineSegment(sketch, "E2026", {"start": v(160.44, -6.95) * mm, "end": v(160.51, -7.04) * mm});
            skLineSegment(sketch, "E2027", {"start": v(160.51, -7.04) * mm, "end": v(160.6, -7.13) * mm});
            skLineSegment(sketch, "E2028", {"start": v(160.6, -7.13) * mm, "end": v(179.2, -25.68) * mm});
            skLineSegment(sketch, "E2029", {"start": v(179.2, -25.68) * mm, "end": v(179.3, -25.78) * mm});
            skLineSegment(sketch, "E2030", {"start": v(179.3, -25.78) * mm, "end": v(179.4, -25.87) * mm});
            skLineSegment(sketch, "E2031", {"start": v(179.4, -25.87) * mm, "end": v(179.5, -25.95) * mm});
            skLineSegment(sketch, "E2032", {"start": v(179.5, -25.95) * mm, "end": v(179.62, -26.03) * mm});
            skLineSegment(sketch, "E2033", {"start": v(179.62, -26.03) * mm, "end": v(179.73, -26.1) * mm});
            skLineSegment(sketch, "E2034", {"start": v(179.73, -26.1) * mm, "end": v(179.85, -26.17) * mm});
            skLineSegment(sketch, "E2035", {"start": v(179.85, -26.17) * mm, "end": v(179.97, -26.23) * mm});
            skLineSegment(sketch, "E2036", {"start": v(179.97, -26.23) * mm, "end": v(180.1, -26.28) * mm});
            skLineSegment(sketch, "E2037", {"start": v(180.1, -26.28) * mm, "end": v(180.22, -26.33) * mm});
            skLineSegment(sketch, "E2038", {"start": v(180.22, -26.33) * mm, "end": v(180.34, -26.37) * mm});
            skLineSegment(sketch, "E2039", {"start": v(180.34, -26.37) * mm, "end": v(180.47, -26.4) * mm});
            skLineSegment(sketch, "E2040", {"start": v(180.47, -26.4) * mm, "end": v(180.6, -26.44) * mm});
            skLineSegment(sketch, "E2041", {"start": v(180.6, -26.44) * mm, "end": v(180.74, -26.46) * mm});
            skLineSegment(sketch, "E2042", {"start": v(180.74, -26.46) * mm, "end": v(180.87, -26.48) * mm});
            skLineSegment(sketch, "E2043", {"start": v(180.87, -26.48) * mm, "end": v(181.01, -26.49) * mm});
            skLineSegment(sketch, "E2044", {"start": v(181.01, -26.49) * mm, "end": v(181.15, -26.5) * mm});
            skLineSegment(sketch, "E2045", {"start": v(181.15, -26.5) * mm, "end": v(192.86, -26.54) * mm});
            skLineSegment(sketch, "E2046", {"start": v(192.86, -26.54) * mm, "end": v(193.74, -26.5) * mm});
            skLineSegment(sketch, "E2047", {"start": v(193.74, -26.5) * mm, "end": v(194.6, -26.37) * mm});
            skLineSegment(sketch, "E2048", {"start": v(194.6, -26.37) * mm, "end": v(195.43, -26.15) * mm});
            skLineSegment(sketch, "E2049", {"start": v(195.43, -26.15) * mm, "end": v(196.22, -25.86) * mm});
            skLineSegment(sketch, "E2050", {"start": v(196.22, -25.86) * mm, "end": v(196.98, -25.5) * mm});
            skLineSegment(sketch, "E2051", {"start": v(196.98, -25.5) * mm, "end": v(197.7, -25.06) * mm});
            skLineSegment(sketch, "E2052", {"start": v(197.7, -25.06) * mm, "end": v(198.36, -24.56) * mm});
            skLineSegment(sketch, "E2053", {"start": v(198.36, -24.56) * mm, "end": v(198.97, -24) * mm});
            skLineSegment(sketch, "E2054", {"start": v(198.97, -24) * mm, "end": v(199.53, -23.39) * mm});
            skLineSegment(sketch, "E2055", {"start": v(199.53, -23.39) * mm, "end": v(200.03, -22.72) * mm});
            skLineSegment(sketch, "E2056", {"start": v(200.03, -22.72) * mm, "end": v(200.46, -22) * mm});
            skLineSegment(sketch, "E2057", {"start": v(200.46, -22) * mm, "end": v(200.83, -21.25) * mm});
            skLineSegment(sketch, "E2058", {"start": v(200.83, -21.25) * mm, "end": v(201.12, -20.46) * mm});
            skLineSegment(sketch, "E2059", {"start": v(201.12, -20.46) * mm, "end": v(201.33, -19.63) * mm});
            skLineSegment(sketch, "E2060", {"start": v(201.33, -19.63) * mm, "end": v(201.47, -18.77) * mm});
            skLineSegment(sketch, "E2061", {"start": v(201.47, -18.77) * mm, "end": v(201.51, -17.89) * mm});
            skLineSegment(sketch, "E2062", {"start": v(201.51, -17.89) * mm, "end": v(201.51, 17.82) * mm});
            skLineSegment(sketch, "E2063", {"start": v(201.51, 17.82) * mm, "end": v(201.47, 18.7) * mm});
            skLineSegment(sketch, "E2064", {"start": v(201.47, 18.7) * mm, "end": v(201.33, 19.57) * mm});
            skLineSegment(sketch, "E2065", {"start": v(201.33, 19.57) * mm, "end": v(201.12, 20.4) * mm});
            skLineSegment(sketch, "E2066", {"start": v(201.12, 20.4) * mm, "end": v(200.83, 21.2) * mm});
            skLineSegment(sketch, "E2067", {"start": v(200.83, 21.2) * mm, "end": v(200.46, 21.95) * mm});
            skLineSegment(sketch, "E2068", {"start": v(200.46, 21.95) * mm, "end": v(200.03, 22.66) * mm});
            skLineSegment(sketch, "E2069", {"start": v(200.03, 22.66) * mm, "end": v(199.53, 23.33) * mm});
            skLineSegment(sketch, "E2070", {"start": v(199.53, 23.33) * mm, "end": v(198.97, 23.94) * mm});
            skLineSegment(sketch, "E2071", {"start": v(198.97, 23.94) * mm, "end": v(198.36, 24.5) * mm});
            skLineSegment(sketch, "E2072", {"start": v(198.36, 24.5) * mm, "end": v(197.7, 25) * mm});
            skLineSegment(sketch, "E2073", {"start": v(197.7, 25) * mm, "end": v(196.98, 25.43) * mm});
            skLineSegment(sketch, "E2074", {"start": v(196.98, 25.43) * mm, "end": v(196.22, 25.8) * mm});
            skLineSegment(sketch, "E2075", {"start": v(196.22, 25.8) * mm, "end": v(195.43, 26.1) * mm});
            skLineSegment(sketch, "E2076", {"start": v(195.43, 26.1) * mm, "end": v(194.6, 26.3) * mm});
            skLineSegment(sketch, "E2077", {"start": v(194.6, 26.3) * mm, "end": v(193.74, 26.44) * mm});
            skLineSegment(sketch, "E2078", {"start": v(193.74, 26.44) * mm, "end": v(192.86, 26.48) * mm});
            skLineSegment(sketch, "E2079", {"start": v(198.49, -17.89) * mm, "end": v(198.46, -18.46) * mm});
            skLineSegment(sketch, "E2080", {"start": v(198.46, -18.46) * mm, "end": v(198.37, -19.02) * mm});
            skLineSegment(sketch, "E2081", {"start": v(198.37, -19.02) * mm, "end": v(198.24, -19.56) * mm});
            skLineSegment(sketch, "E2082", {"start": v(198.24, -19.56) * mm, "end": v(198.05, -20.08) * mm});
            skLineSegment(sketch, "E2083", {"start": v(198.05, -20.08) * mm, "end": v(197.8, -20.57) * mm});
            skLineSegment(sketch, "E2084", {"start": v(197.8, -20.57) * mm, "end": v(197.53, -21.03) * mm});
            skLineSegment(sketch, "E2085", {"start": v(197.53, -21.03) * mm, "end": v(197.2, -21.47) * mm});
            skLineSegment(sketch, "E2086", {"start": v(197.2, -21.47) * mm, "end": v(196.84, -21.87) * mm});
            skLineSegment(sketch, "E2087", {"start": v(196.84, -21.87) * mm, "end": v(196.44, -22.23) * mm});
            skLineSegment(sketch, "E2088", {"start": v(196.44, -22.23) * mm, "end": v(196, -22.56) * mm});
            skLineSegment(sketch, "E2089", {"start": v(196, -22.56) * mm, "end": v(195.54, -22.84) * mm});
            skLineSegment(sketch, "E2090", {"start": v(195.54, -22.84) * mm, "end": v(195.05, -23.08) * mm});
            skLineSegment(sketch, "E2091", {"start": v(195.05, -23.08) * mm, "end": v(194.53, -23.27) * mm});
            skLineSegment(sketch, "E2092", {"start": v(194.53, -23.27) * mm, "end": v(193.99, -23.4) * mm});
            skLineSegment(sketch, "E2093", {"start": v(193.99, -23.4) * mm, "end": v(193.43, -23.5) * mm});
            skLineSegment(sketch, "E2094", {"start": v(193.43, -23.5) * mm, "end": v(192.86, -23.52) * mm});
            skLineSegment(sketch, "E2095", {"start": v(192.86, -23.52) * mm, "end": v(181.97, -23.49) * mm});
            skLineSegment(sketch, "E2096", {"start": v(181.97, -23.49) * mm, "end": v(181.88, -23.48) * mm});
            skLineSegment(sketch, "E2097", {"start": v(181.88, -23.48) * mm, "end": v(181.79, -23.48) * mm});
            skLineSegment(sketch, "E2098", {"start": v(181.79, -23.48) * mm, "end": v(181.7, -23.47) * mm});
            skLineSegment(sketch, "E2099", {"start": v(181.7, -23.47) * mm, "end": v(181.6, -23.45) * mm});
            skLineSegment(sketch, "E2100", {"start": v(181.6, -23.45) * mm, "end": v(181.52, -23.43) * mm});
            skLineSegment(sketch, "E2101", {"start": v(181.52, -23.43) * mm, "end": v(181.43, -23.4) * mm});
            skLineSegment(sketch, "E2102", {"start": v(181.43, -23.4) * mm, "end": v(181.34, -23.38) * mm});
            skLineSegment(sketch, "E2103", {"start": v(181.34, -23.38) * mm, "end": v(181.26, -23.34) * mm});
            skLineSegment(sketch, "E2104", {"start": v(181.26, -23.34) * mm, "end": v(181.18, -23.3) * mm});
            skLineSegment(sketch, "E2105", {"start": v(181.18, -23.3) * mm, "end": v(181.1, -23.27) * mm});
            skLineSegment(sketch, "E2106", {"start": v(181.1, -23.27) * mm, "end": v(181.02, -23.22) * mm});
            skLineSegment(sketch, "E2107", {"start": v(181.02, -23.22) * mm, "end": v(180.94, -23.17) * mm});
            skLineSegment(sketch, "E2108", {"start": v(180.94, -23.17) * mm, "end": v(180.86, -23.12) * mm});
            skLineSegment(sketch, "E2109", {"start": v(180.86, -23.12) * mm, "end": v(180.8, -23.06) * mm});
            skLineSegment(sketch, "E2110", {"start": v(180.8, -23.06) * mm, "end": v(180.72, -23) * mm});
            skLineSegment(sketch, "E2111", {"start": v(180.72, -23) * mm, "end": v(180.66, -22.94) * mm});
            skLineSegment(sketch, "E2112", {"start": v(180.66, -22.94) * mm, "end": v(164.7, -7) * mm});
            skLineSegment(sketch, "E2113", {"start": v(164.7, -7) * mm, "end": v(164.7, -6.98) * mm});
            skLineSegment(sketch, "E2114", {"start": v(164.7, -6.98) * mm, "end": v(164.69, -6.97) * mm});
            skLineSegment(sketch, "E2115", {"start": v(164.69, -6.97) * mm, "end": v(164.68, -6.96) * mm});
            skLineSegment(sketch, "E2116", {"start": v(164.68, -6.96) * mm, "end": v(164.68, -6.95) * mm});
            skLineSegment(sketch, "E2117", {"start": v(164.68, -6.95) * mm, "end": v(164.67, -6.94) * mm});
            skLineSegment(sketch, "E2118", {"start": v(164.67, -6.94) * mm, "end": v(164.67, -6.93) * mm});
            skLineSegment(sketch, "E2119", {"start": v(164.67, -6.93) * mm, "end": v(164.66, -6.92) * mm});
            skLineSegment(sketch, "E2120", {"start": v(164.66, -6.92) * mm, "end": v(164.66, -6.9) * mm});
            skLineSegment(sketch, "E2121", {"start": v(164.66, -6.9) * mm, "end": v(164.66, -6.9) * mm});
            skLineSegment(sketch, "E2122", {"start": v(164.66, -6.9) * mm, "end": v(164.66, -6.88) * mm});
            skLineSegment(sketch, "E2123", {"start": v(164.66, -6.88) * mm, "end": v(164.66, -6.87) * mm});
            skLineSegment(sketch, "E2124", {"start": v(164.66, -6.87) * mm, "end": v(164.66, -6.85) * mm});
            skLineSegment(sketch, "E2125", {"start": v(164.66, -6.85) * mm, "end": v(164.66, -6.84) * mm});
            skLineSegment(sketch, "E2126", {"start": v(164.66, -6.84) * mm, "end": v(164.66, -6.83) * mm});
            skLineSegment(sketch, "E2127", {"start": v(164.66, -6.83) * mm, "end": v(164.67, -6.82) * mm});
            skLineSegment(sketch, "E2128", {"start": v(164.67, -6.82) * mm, "end": v(164.67, -6.8) * mm});
            skLineSegment(sketch, "E2129", {"start": v(164.67, -6.8) * mm, "end": v(164.68, -6.8) * mm});
            skLineSegment(sketch, "E2130", {"start": v(164.68, -6.8) * mm, "end": v(164.68, -6.78) * mm});
            skLineSegment(sketch, "E2131", {"start": v(164.68, -6.78) * mm, "end": v(164.69, -6.77) * mm});
            skLineSegment(sketch, "E2132", {"start": v(164.69, -6.77) * mm, "end": v(164.7, -6.76) * mm});
            skLineSegment(sketch, "E2133", {"start": v(164.7, -6.76) * mm, "end": v(164.7, -6.75) * mm});
            skLineSegment(sketch, "E2134", {"start": v(164.7, -6.75) * mm, "end": v(164.71, -6.74) * mm});
            skLineSegment(sketch, "E2135", {"start": v(164.71, -6.74) * mm, "end": v(164.72, -6.73) * mm});
            skLineSegment(sketch, "E2136", {"start": v(164.72, -6.73) * mm, "end": v(164.73, -6.73) * mm});
            skLineSegment(sketch, "E2137", {"start": v(164.73, -6.73) * mm, "end": v(164.74, -6.72) * mm});
            skLineSegment(sketch, "E2138", {"start": v(164.74, -6.72) * mm, "end": v(164.75, -6.71) * mm});
            skLineSegment(sketch, "E2139", {"start": v(164.75, -6.71) * mm, "end": v(164.77, -6.7) * mm});
            skLineSegment(sketch, "E2140", {"start": v(164.77, -6.7) * mm, "end": v(164.78, -6.7) * mm});
            skLineSegment(sketch, "E2141", {"start": v(164.78, -6.7) * mm, "end": v(164.79, -6.7) * mm});
            skLineSegment(sketch, "E2142", {"start": v(164.79, -6.7) * mm, "end": v(164.8, -6.7) * mm});
            skLineSegment(sketch, "E2143", {"start": v(164.8, -6.7) * mm, "end": v(164.82, -6.7) * mm});
            skLineSegment(sketch, "E2144", {"start": v(164.82, -6.7) * mm, "end": v(164.83, -6.7) * mm});
            skLineSegment(sketch, "E2145", {"start": v(164.83, -6.7) * mm, "end": v(170.73, -6.7) * mm});
            skLineSegment(sketch, "E2146", {"start": v(170.73, -6.7) * mm, "end": v(171.23, -6.69) * mm});
            skLineSegment(sketch, "E2147", {"start": v(171.23, -6.69) * mm, "end": v(171.72, -6.66) * mm});
            skLineSegment(sketch, "E2148", {"start": v(171.72, -6.66) * mm, "end": v(172.2, -6.62) * mm});
            skLineSegment(sketch, "E2149", {"start": v(172.2, -6.62) * mm, "end": v(172.68, -6.55) * mm});
            skLineSegment(sketch, "E2150", {"start": v(172.68, -6.55) * mm, "end": v(173.15, -6.47) * mm});
            skLineSegment(sketch, "E2151", {"start": v(173.15, -6.47) * mm, "end": v(173.61, -6.37) * mm});
            skLineSegment(sketch, "E2152", {"start": v(173.61, -6.37) * mm, "end": v(174.07, -6.26) * mm});
            skLineSegment(sketch, "E2153", {"start": v(174.07, -6.26) * mm, "end": v(174.52, -6.12) * mm});
            skLineSegment(sketch, "E2154", {"start": v(174.52, -6.12) * mm, "end": v(174.97, -5.97) * mm});
            skLineSegment(sketch, "E2155", {"start": v(174.97, -5.97) * mm, "end": v(175.4, -5.8) * mm});
            skLineSegment(sketch, "E2156", {"start": v(175.4, -5.8) * mm, "end": v(175.83, -5.61) * mm});
            skLineSegment(sketch, "E2157", {"start": v(175.83, -5.61) * mm, "end": v(176.26, -5.4) * mm});
            skLineSegment(sketch, "E2158", {"start": v(176.26, -5.4) * mm, "end": v(176.68, -5.18) * mm});
            skLineSegment(sketch, "E2159", {"start": v(176.68, -5.18) * mm, "end": v(177.09, -4.94) * mm});
            skLineSegment(sketch, "E2160", {"start": v(177.09, -4.94) * mm, "end": v(177.49, -4.68) * mm});
            skLineSegment(sketch, "E2161", {"start": v(177.49, -4.68) * mm, "end": v(177.88, -4.4) * mm});
            skLineSegment(sketch, "E2162", {"start": v(177.88, -4.4) * mm, "end": v(178.4, -4) * mm});
            skLineSegment(sketch, "E2163", {"start": v(178.4, -4) * mm, "end": v(178.87, -3.59) * mm});
            skLineSegment(sketch, "E2164", {"start": v(178.87, -3.59) * mm, "end": v(179.31, -3.14) * mm});
            skLineSegment(sketch, "E2165", {"start": v(179.31, -3.14) * mm, "end": v(179.73, -2.68) * mm});
            skLineSegment(sketch, "E2166", {"start": v(179.73, -2.68) * mm, "end": v(180.1, -2.19) * mm});
            skLineSegment(sketch, "E2167", {"start": v(180.1, -2.19) * mm, "end": v(180.45, -1.67) * mm});
            skLineSegment(sketch, "E2168", {"start": v(180.45, -1.67) * mm, "end": v(180.76, -1.14) * mm});
            skLineSegment(sketch, "E2169", {"start": v(180.76, -1.14) * mm, "end": v(181.05, -0.58) * mm});
            skLineSegment(sketch, "E2170", {"start": v(181.05, -0.58) * mm, "end": v(181.3, 0) * mm});
            skLineSegment(sketch, "E2171", {"start": v(181.3, 0) * mm, "end": v(181.5, 0.6) * mm});
            skLineSegment(sketch, "E2172", {"start": v(181.5, 0.6) * mm, "end": v(181.7, 1.22) * mm});
            skLineSegment(sketch, "E2173", {"start": v(181.7, 1.22) * mm, "end": v(181.84, 1.87) * mm});
            skLineSegment(sketch, "E2174", {"start": v(181.84, 1.87) * mm, "end": v(181.96, 2.54) * mm});
            skLineSegment(sketch, "E2175", {"start": v(181.96, 2.54) * mm, "end": v(182.04, 3.23) * mm});
            skLineSegment(sketch, "E2176", {"start": v(182.04, 3.23) * mm, "end": v(182.09, 3.94) * mm});
            skLineSegment(sketch, "E2177", {"start": v(182.09, 3.94) * mm, "end": v(182.1, 4.67) * mm});
            skLineSegment(sketch, "E2178", {"start": v(182.1, 4.67) * mm, "end": v(182.09, 5.4) * mm});
            skLineSegment(sketch, "E2179", {"start": v(182.09, 5.4) * mm, "end": v(182.04, 6.12) * mm});
            skLineSegment(sketch, "E2180", {"start": v(182.04, 6.12) * mm, "end": v(181.96, 6.8) * mm});
            skLineSegment(sketch, "E2181", {"start": v(181.96, 6.8) * mm, "end": v(181.84, 7.48) * mm});
            skLineSegment(sketch, "E2182", {"start": v(181.84, 7.48) * mm, "end": v(181.7, 8.12) * mm});
            skLineSegment(sketch, "E2183", {"start": v(181.7, 8.12) * mm, "end": v(181.5, 8.75) * mm});
            skLineSegment(sketch, "E2184", {"start": v(181.5, 8.75) * mm, "end": v(181.3, 9.35) * mm});
            skLineSegment(sketch, "E2185", {"start": v(181.3, 9.35) * mm, "end": v(181.05, 9.93) * mm});
            skLineSegment(sketch, "E2186", {"start": v(181.05, 9.93) * mm, "end": v(180.76, 10.48) * mm});
            skLineSegment(sketch, "E2187", {"start": v(180.76, 10.48) * mm, "end": v(180.45, 11.02) * mm});
            skLineSegment(sketch, "E2188", {"start": v(180.45, 11.02) * mm, "end": v(180.1, 11.53) * mm});
            skLineSegment(sketch, "E2189", {"start": v(180.1, 11.53) * mm, "end": v(179.73, 12.02) * mm});
            skLineSegment(sketch, "E2190", {"start": v(179.73, 12.02) * mm, "end": v(179.31, 12.49) * mm});
            skLineSegment(sketch, "E2191", {"start": v(179.31, 12.49) * mm, "end": v(178.87, 12.93) * mm});
            skLineSegment(sketch, "E2192", {"start": v(178.87, 12.93) * mm, "end": v(178.4, 13.35) * mm});
            skLineSegment(sketch, "E2193", {"start": v(178.4, 13.35) * mm, "end": v(177.88, 13.75) * mm});
            skLineSegment(sketch, "E2194", {"start": v(177.88, 13.75) * mm, "end": v(177.49, 14.03) * mm});
            skLineSegment(sketch, "E2195", {"start": v(177.49, 14.03) * mm, "end": v(177.09, 14.29) * mm});
            skLineSegment(sketch, "E2196", {"start": v(177.09, 14.29) * mm, "end": v(176.68, 14.53) * mm});
            skLineSegment(sketch, "E2197", {"start": v(176.68, 14.53) * mm, "end": v(176.26, 14.75) * mm});
            skLineSegment(sketch, "E2198", {"start": v(176.26, 14.75) * mm, "end": v(175.83, 14.96) * mm});
            skLineSegment(sketch, "E2199", {"start": v(175.83, 14.96) * mm, "end": v(175.4, 15.15) * mm});
            skLineSegment(sketch, "E2200", {"start": v(175.4, 15.15) * mm, "end": v(174.97, 15.32) * mm});
            skLineSegment(sketch, "E2201", {"start": v(174.97, 15.32) * mm, "end": v(174.52, 15.47) * mm});
            skLineSegment(sketch, "E2202", {"start": v(174.52, 15.47) * mm, "end": v(174.07, 15.6) * mm});
            skLineSegment(sketch, "E2203", {"start": v(174.07, 15.6) * mm, "end": v(173.61, 15.72) * mm});
            skLineSegment(sketch, "E2204", {"start": v(173.61, 15.72) * mm, "end": v(173.15, 15.82) * mm});
            skLineSegment(sketch, "E2205", {"start": v(173.15, 15.82) * mm, "end": v(172.68, 15.9) * mm});
            skLineSegment(sketch, "E2206", {"start": v(172.68, 15.9) * mm, "end": v(172.2, 15.96) * mm});
            skLineSegment(sketch, "E2207", {"start": v(172.2, 15.96) * mm, "end": v(171.72, 16) * mm});
            skLineSegment(sketch, "E2208", {"start": v(171.72, 16) * mm, "end": v(171.23, 16.04) * mm});
            skLineSegment(sketch, "E2209", {"start": v(171.23, 16.04) * mm, "end": v(170.73, 16.04) * mm});
            skLineSegment(sketch, "E2210", {"start": v(170.73, 16.04) * mm, "end": v(157.68, 16.04) * mm});
            skLineSegment(sketch, "E2211", {"start": v(157.68, 16.04) * mm, "end": v(157.35, 16.03) * mm});
            skLineSegment(sketch, "E2212", {"start": v(157.35, 16.03) * mm, "end": v(157.02, 15.98) * mm});
            skLineSegment(sketch, "E2213", {"start": v(157.02, 15.98) * mm, "end": v(156.7, 15.9) * mm});
            skLineSegment(sketch, "E2214", {"start": v(156.7, 15.9) * mm, "end": v(156.4, 15.79) * mm});
            skLineSegment(sketch, "E2215", {"start": v(156.4, 15.79) * mm, "end": v(156.11, 15.65) * mm});
            skLineSegment(sketch, "E2216", {"start": v(156.11, 15.65) * mm, "end": v(155.84, 15.48) * mm});
            skLineSegment(sketch, "E2217", {"start": v(155.84, 15.48) * mm, "end": v(155.59, 15.3) * mm});
            skLineSegment(sketch, "E2218", {"start": v(155.59, 15.3) * mm, "end": v(155.35, 15.08) * mm});
            skLineSegment(sketch, "E2219", {"start": v(155.35, 15.08) * mm, "end": v(155.14, 14.85) * mm});
            skLineSegment(sketch, "E2220", {"start": v(155.14, 14.85) * mm, "end": v(154.95, 14.6) * mm});
            skLineSegment(sketch, "E2221", {"start": v(154.95, 14.6) * mm, "end": v(154.79, 14.32) * mm});
            skLineSegment(sketch, "E2222", {"start": v(154.79, 14.32) * mm, "end": v(154.65, 14.03) * mm});
            skLineSegment(sketch, "E2223", {"start": v(154.65, 14.03) * mm, "end": v(154.54, 13.73) * mm});
            skLineSegment(sketch, "E2224", {"start": v(154.54, 13.73) * mm, "end": v(154.46, 13.41) * mm});
            skLineSegment(sketch, "E2225", {"start": v(154.46, 13.41) * mm, "end": v(154.4, 13.09) * mm});
            skLineSegment(sketch, "E2226", {"start": v(154.4, 13.09) * mm, "end": v(154.39, 12.75) * mm});
            skLineSegment(sketch, "E2227", {"start": v(154.39, 12.75) * mm, "end": v(154.39, -22.53) * mm});
            skLineSegment(sketch, "E2228", {"start": v(154.39, -22.53) * mm, "end": v(154.39, -22.64) * mm});
            skLineSegment(sketch, "E2229", {"start": v(154.39, -22.64) * mm, "end": v(154.37, -22.74) * mm});
            skLineSegment(sketch, "E2230", {"start": v(154.37, -22.74) * mm, "end": v(154.35, -22.84) * mm});
            skLineSegment(sketch, "E2231", {"start": v(154.35, -22.84) * mm, "end": v(154.33, -22.93) * mm});
            skLineSegment(sketch, "E2232", {"start": v(154.33, -22.93) * mm, "end": v(154.3, -23.01) * mm});
            skLineSegment(sketch, "E2233", {"start": v(154.3, -23.01) * mm, "end": v(154.25, -23.09) * mm});
            skLineSegment(sketch, "E2234", {"start": v(154.25, -23.09) * mm, "end": v(154.2, -23.16) * mm});
            skLineSegment(sketch, "E2235", {"start": v(154.2, -23.16) * mm, "end": v(154.14, -23.22) * mm});
            skLineSegment(sketch, "E2236", {"start": v(154.14, -23.22) * mm, "end": v(154.07, -23.28) * mm});
            skLineSegment(sketch, "E2237", {"start": v(154.07, -23.28) * mm, "end": v(154, -23.33) * mm});
            skLineSegment(sketch, "E2238", {"start": v(154, -23.33) * mm, "end": v(153.91, -23.37) * mm});
            skLineSegment(sketch, "E2239", {"start": v(153.91, -23.37) * mm, "end": v(153.82, -23.4) * mm});
            skLineSegment(sketch, "E2240", {"start": v(153.82, -23.4) * mm, "end": v(153.72, -23.44) * mm});
            skLineSegment(sketch, "E2241", {"start": v(153.72, -23.44) * mm, "end": v(153.61, -23.46) * mm});
            skLineSegment(sketch, "E2242", {"start": v(153.61, -23.46) * mm, "end": v(153.5, -23.47) * mm});
            skLineSegment(sketch, "E2243", {"start": v(153.5, -23.47) * mm, "end": v(153.37, -23.48) * mm});
            skLineSegment(sketch, "E2244", {"start": v(153.37, -23.48) * mm, "end": v(152.53, -23.52) * mm});
            skLineSegment(sketch, "E2245", {"start": v(152.53, -23.52) * mm, "end": v(135.23, -23.49) * mm});
            skLineSegment(sketch, "E2246", {"start": v(135.23, -23.49) * mm, "end": v(135.17, -23.48) * mm});
            skLineSegment(sketch, "E2247", {"start": v(135.17, -23.48) * mm, "end": v(135.1, -23.47) * mm});
            skLineSegment(sketch, "E2248", {"start": v(135.1, -23.47) * mm, "end": v(135.05, -23.46) * mm});
            skLineSegment(sketch, "E2249", {"start": v(135.05, -23.46) * mm, "end": v(135, -23.44) * mm});
            skLineSegment(sketch, "E2250", {"start": v(135, -23.44) * mm, "end": v(134.95, -23.41) * mm});
            skLineSegment(sketch, "E2251", {"start": v(134.95, -23.41) * mm, "end": v(134.9, -23.38) * mm});
            skLineSegment(sketch, "E2252", {"start": v(134.9, -23.38) * mm, "end": v(134.85, -23.35) * mm});
            skLineSegment(sketch, "E2253", {"start": v(134.85, -23.35) * mm, "end": v(134.81, -23.31) * mm});
            skLineSegment(sketch, "E2254", {"start": v(134.81, -23.31) * mm, "end": v(134.77, -23.27) * mm});
            skLineSegment(sketch, "E2255", {"start": v(134.77, -23.27) * mm, "end": v(134.74, -23.23) * mm});
            skLineSegment(sketch, "E2256", {"start": v(134.74, -23.23) * mm, "end": v(134.71, -23.18) * mm});
            skLineSegment(sketch, "E2257", {"start": v(134.71, -23.18) * mm, "end": v(134.69, -23.13) * mm});
            skLineSegment(sketch, "E2258", {"start": v(134.69, -23.13) * mm, "end": v(134.67, -23.07) * mm});
            skLineSegment(sketch, "E2259", {"start": v(134.67, -23.07) * mm, "end": v(134.65, -23.02) * mm});
            skLineSegment(sketch, "E2260", {"start": v(134.65, -23.02) * mm, "end": v(134.64, -22.96) * mm});
            skLineSegment(sketch, "E2261", {"start": v(134.64, -22.96) * mm, "end": v(134.64, -22.9) * mm});
            skLineSegment(sketch, "E2262", {"start": v(134.64, -22.9) * mm, "end": v(134.64, -21.76) * mm});
            skLineSegment(sketch, "E2263", {"start": v(134.64, -21.76) * mm, "end": v(134.64, -21.69) * mm});
            skLineSegment(sketch, "E2264", {"start": v(134.64, -21.69) * mm, "end": v(134.65, -21.61) * mm});
            skLineSegment(sketch, "E2265", {"start": v(134.65, -21.61) * mm, "end": v(134.67, -21.54) * mm});
            skLineSegment(sketch, "E2266", {"start": v(134.67, -21.54) * mm, "end": v(134.69, -21.47) * mm});
            skLineSegment(sketch, "E2267", {"start": v(134.69, -21.47) * mm, "end": v(134.71, -21.4) * mm});
            skLineSegment(sketch, "E2268", {"start": v(134.71, -21.4) * mm, "end": v(134.74, -21.35) * mm});
            skLineSegment(sketch, "E2269", {"start": v(134.74, -21.35) * mm, "end": v(134.78, -21.28) * mm});
            skLineSegment(sketch, "E2270", {"start": v(134.78, -21.28) * mm, "end": v(134.82, -21.23) * mm});
            skLineSegment(sketch, "E2271", {"start": v(134.82, -21.23) * mm, "end": v(134.86, -21.17) * mm});
            skLineSegment(sketch, "E2272", {"start": v(134.86, -21.17) * mm, "end": v(134.91, -21.12) * mm});
            skLineSegment(sketch, "E2273", {"start": v(134.91, -21.12) * mm, "end": v(134.96, -21.08) * mm});
            skLineSegment(sketch, "E2274", {"start": v(134.96, -21.08) * mm, "end": v(135.02, -21.04) * mm});
            skLineSegment(sketch, "E2275", {"start": v(135.02, -21.04) * mm, "end": v(135.08, -21) * mm});
            skLineSegment(sketch, "E2276", {"start": v(135.08, -21) * mm, "end": v(135.14, -20.97) * mm});
            skLineSegment(sketch, "E2277", {"start": v(135.14, -20.97) * mm, "end": v(135.21, -20.94) * mm});
            skLineSegment(sketch, "E2278", {"start": v(135.21, -20.94) * mm, "end": v(135.28, -20.92) * mm});
            skLineSegment(sketch, "E2279", {"start": v(135.28, -20.92) * mm, "end": v(136.03, -20.72) * mm});
            skLineSegment(sketch, "E2280", {"start": v(136.03, -20.72) * mm, "end": v(136.76, -20.5) * mm});
            skLineSegment(sketch, "E2281", {"start": v(136.76, -20.5) * mm, "end": v(137.47, -20.24) * mm});
            skLineSegment(sketch, "E2282", {"start": v(137.47, -20.24) * mm, "end": v(138.17, -19.96) * mm});
            skLineSegment(sketch, "E2283", {"start": v(138.17, -19.96) * mm, "end": v(138.86, -19.65) * mm});
            skLineSegment(sketch, "E2284", {"start": v(138.86, -19.65) * mm, "end": v(139.53, -19.31) * mm});
            skLineSegment(sketch, "E2285", {"start": v(139.53, -19.31) * mm, "end": v(140.18, -18.95) * mm});
            skLineSegment(sketch, "E2286", {"start": v(140.18, -18.95) * mm, "end": v(140.82, -18.56) * mm});
            skLineSegment(sketch, "E2287", {"start": v(140.82, -18.56) * mm, "end": v(141.44, -18.14) * mm});
            skLineSegment(sketch, "E2288", {"start": v(141.44, -18.14) * mm, "end": v(142.05, -17.7) * mm});
            skLineSegment(sketch, "E2289", {"start": v(142.05, -17.7) * mm, "end": v(142.64, -17.23) * mm});
            skLineSegment(sketch, "E2290", {"start": v(142.64, -17.23) * mm, "end": v(143.2, -16.74) * mm});
            skLineSegment(sketch, "E2291", {"start": v(143.2, -16.74) * mm, "end": v(143.77, -16.21) * mm});
            skLineSegment(sketch, "E2292", {"start": v(143.77, -16.21) * mm, "end": v(144.3, -15.67) * mm});
            skLineSegment(sketch, "E2293", {"start": v(144.3, -15.67) * mm, "end": v(144.83, -15.1) * mm});
            skLineSegment(sketch, "E2294", {"start": v(144.83, -15.1) * mm, "end": v(145.33, -14.5) * mm});
            skLineSegment(sketch, "E2295", {"start": v(145.33, -14.5) * mm, "end": v(145.84, -13.84) * mm});
            skLineSegment(sketch, "E2296", {"start": v(145.84, -13.84) * mm, "end": v(146.32, -13.17) * mm});
            skLineSegment(sketch, "E2297", {"start": v(146.32, -13.17) * mm, "end": v(146.77, -12.5) * mm});
            skLineSegment(sketch, "E2298", {"start": v(146.77, -12.5) * mm, "end": v(147.18, -11.8) * mm});
            skLineSegment(sketch, "E2299", {"start": v(147.18, -11.8) * mm, "end": v(147.56, -11.1) * mm});
            skLineSegment(sketch, "E2300", {"start": v(147.56, -11.1) * mm, "end": v(147.9, -10.38) * mm});
            skLineSegment(sketch, "E2301", {"start": v(147.9, -10.38) * mm, "end": v(148.22, -9.66) * mm});
            skLineSegment(sketch, "E2302", {"start": v(148.22, -9.66) * mm, "end": v(148.5, -8.92) * mm});
            skLineSegment(sketch, "E2303", {"start": v(148.5, -8.92) * mm, "end": v(148.75, -8.17) * mm});
            skLineSegment(sketch, "E2304", {"start": v(148.75, -8.17) * mm, "end": v(148.96, -7.4) * mm});
            skLineSegment(sketch, "E2305", {"start": v(148.96, -7.4) * mm, "end": v(149.15, -6.64) * mm});
            skLineSegment(sketch, "E2306", {"start": v(149.15, -6.64) * mm, "end": v(149.3, -5.86) * mm});
            skLineSegment(sketch, "E2307", {"start": v(149.3, -5.86) * mm, "end": v(149.41, -5.07) * mm});
            skLineSegment(sketch, "E2308", {"start": v(149.41, -5.07) * mm, "end": v(149.5, -4.26) * mm});
            skLineSegment(sketch, "E2309", {"start": v(149.5, -4.26) * mm, "end": v(149.55, -3.45) * mm});
            skLineSegment(sketch, "E2310", {"start": v(149.55, -3.45) * mm, "end": v(149.56, -2.63) * mm});
            skLineSegment(sketch, "E2311", {"start": v(149.56, -2.63) * mm, "end": v(149.54, -1.65) * mm});
            skLineSegment(sketch, "E2312", {"start": v(149.54, -1.65) * mm, "end": v(149.48, -0.7) * mm});
            skLineSegment(sketch, "E2313", {"start": v(149.48, -0.7) * mm, "end": v(149.37, 0.25) * mm});
            skLineSegment(sketch, "E2314", {"start": v(149.37, 0.25) * mm, "end": v(149.22, 1.17) * mm});
            skLineSegment(sketch, "E2315", {"start": v(149.22, 1.17) * mm, "end": v(149.02, 2.08) * mm});
            skLineSegment(sketch, "E2316", {"start": v(149.02, 2.08) * mm, "end": v(148.78, 2.97) * mm});
            skLineSegment(sketch, "E2317", {"start": v(148.78, 2.97) * mm, "end": v(148.5, 3.84) * mm});
            skLineSegment(sketch, "E2318", {"start": v(148.5, 3.84) * mm, "end": v(148.18, 4.69) * mm});
            skLineSegment(sketch, "E2319", {"start": v(148.18, 4.69) * mm, "end": v(147.81, 5.52) * mm});
            skLineSegment(sketch, "E2320", {"start": v(147.81, 5.52) * mm, "end": v(147.4, 6.33) * mm});
            skLineSegment(sketch, "E2321", {"start": v(147.4, 6.33) * mm, "end": v(146.95, 7.13) * mm});
            skLineSegment(sketch, "E2322", {"start": v(146.95, 7.13) * mm, "end": v(146.46, 7.9) * mm});
            skLineSegment(sketch, "E2323", {"start": v(146.46, 7.9) * mm, "end": v(145.92, 8.66) * mm});
            skLineSegment(sketch, "E2324", {"start": v(145.92, 8.66) * mm, "end": v(145.34, 9.4) * mm});
            skLineSegment(sketch, "E2325", {"start": v(145.34, 9.4) * mm, "end": v(144.72, 10.1) * mm});
            skLineSegment(sketch, "E2326", {"start": v(144.72, 10.1) * mm, "end": v(144.06, 10.8) * mm});
            skLineSegment(sketch, "E2327", {"start": v(144.06, 10.8) * mm, "end": v(143.36, 11.47) * mm});
            skLineSegment(sketch, "E2328", {"start": v(143.36, 11.47) * mm, "end": v(142.65, 12.09) * mm});
            skLineSegment(sketch, "E2329", {"start": v(142.65, 12.09) * mm, "end": v(141.91, 12.67) * mm});
            skLineSegment(sketch, "E2330", {"start": v(141.91, 12.67) * mm, "end": v(141.16, 13.2) * mm});
            skLineSegment(sketch, "E2331", {"start": v(141.16, 13.2) * mm, "end": v(140.38, 13.7) * mm});
            skLineSegment(sketch, "E2332", {"start": v(140.38, 13.7) * mm, "end": v(139.59, 14.15) * mm});
            skLineSegment(sketch, "E2333", {"start": v(139.59, 14.15) * mm, "end": v(138.77, 14.56) * mm});
            skLineSegment(sketch, "E2334", {"start": v(138.77, 14.56) * mm, "end": v(137.94, 14.93) * mm});
            skLineSegment(sketch, "E2335", {"start": v(137.94, 14.93) * mm, "end": v(137.1, 15.25) * mm});
            skLineSegment(sketch, "E2336", {"start": v(137.1, 15.25) * mm, "end": v(136.22, 15.53) * mm});
            skLineSegment(sketch, "E2337", {"start": v(136.22, 15.53) * mm, "end": v(135.33, 15.77) * mm});
            skLineSegment(sketch, "E2338", {"start": v(135.33, 15.77) * mm, "end": v(134.43, 15.96) * mm});
            skLineSegment(sketch, "E2339", {"start": v(134.43, 15.96) * mm, "end": v(133.5, 16.11) * mm});
            skLineSegment(sketch, "E2340", {"start": v(133.5, 16.11) * mm, "end": v(132.56, 16.22) * mm});
            skLineSegment(sketch, "E2341", {"start": v(132.56, 16.22) * mm, "end": v(131.6, 16.29) * mm});
            skLineSegment(sketch, "E2342", {"start": v(131.6, 16.29) * mm, "end": v(130.62, 16.3) * mm});
            skLineSegment(sketch, "E2343", {"start": v(130.62, 16.3) * mm, "end": v(129.65, 16.29) * mm});
            skLineSegment(sketch, "E2344", {"start": v(129.65, 16.29) * mm, "end": v(128.7, 16.22) * mm});
            skLineSegment(sketch, "E2345", {"start": v(128.7, 16.22) * mm, "end": v(127.76, 16.11) * mm});
            skLineSegment(sketch, "E2346", {"start": v(127.76, 16.11) * mm, "end": v(126.84, 15.96) * mm});
            skLineSegment(sketch, "E2347", {"start": v(126.84, 15.96) * mm, "end": v(125.94, 15.77) * mm});
            skLineSegment(sketch, "E2348", {"start": v(125.94, 15.77) * mm, "end": v(125.06, 15.53) * mm});
            skLineSegment(sketch, "E2349", {"start": v(125.06, 15.53) * mm, "end": v(124.2, 15.25) * mm});
            skLineSegment(sketch, "E2350", {"start": v(124.2, 15.25) * mm, "end": v(123.34, 14.93) * mm});
            skLineSegment(sketch, "E2351", {"start": v(123.34, 14.93) * mm, "end": v(122.52, 14.56) * mm});
            skLineSegment(sketch, "E2352", {"start": v(122.52, 14.56) * mm, "end": v(121.7, 14.15) * mm});
            skLineSegment(sketch, "E2353", {"start": v(121.7, 14.15) * mm, "end": v(120.91, 13.7) * mm});
            skLineSegment(sketch, "E2354", {"start": v(120.91, 13.7) * mm, "end": v(120.14, 13.2) * mm});
            skLineSegment(sketch, "E2355", {"start": v(120.14, 13.2) * mm, "end": v(119.39, 12.67) * mm});
            skLineSegment(sketch, "E2356", {"start": v(119.39, 12.67) * mm, "end": v(118.65, 12.09) * mm});
            skLineSegment(sketch, "E2357", {"start": v(118.65, 12.09) * mm, "end": v(117.94, 11.47) * mm});
            skLineSegment(sketch, "E2358", {"start": v(117.94, 11.47) * mm, "end": v(117.24, 10.8) * mm});
            skLineSegment(sketch, "E2359", {"start": v(117.24, 10.8) * mm, "end": v(116.58, 10.1) * mm});
            skLineSegment(sketch, "E2360", {"start": v(116.58, 10.1) * mm, "end": v(115.96, 9.4) * mm});
            skLineSegment(sketch, "E2361", {"start": v(115.96, 9.4) * mm, "end": v(115.38, 8.66) * mm});
            skLineSegment(sketch, "E2362", {"start": v(115.38, 8.66) * mm, "end": v(114.84, 7.9) * mm});
            skLineSegment(sketch, "E2363", {"start": v(114.84, 7.9) * mm, "end": v(114.35, 7.13) * mm});
            skLineSegment(sketch, "E2364", {"start": v(114.35, 7.13) * mm, "end": v(113.9, 6.33) * mm});
            skLineSegment(sketch, "E2365", {"start": v(113.9, 6.33) * mm, "end": v(113.49, 5.52) * mm});
            skLineSegment(sketch, "E2366", {"start": v(113.49, 5.52) * mm, "end": v(113.12, 4.69) * mm});
            skLineSegment(sketch, "E2367", {"start": v(113.12, 4.69) * mm, "end": v(112.8, 3.84) * mm});
            skLineSegment(sketch, "E2368", {"start": v(112.8, 3.84) * mm, "end": v(112.52, 2.97) * mm});
            skLineSegment(sketch, "E2369", {"start": v(112.52, 2.97) * mm, "end": v(112.28, 2.08) * mm});
            skLineSegment(sketch, "E2370", {"start": v(112.28, 2.08) * mm, "end": v(112.08, 1.17) * mm});
            skLineSegment(sketch, "E2371", {"start": v(112.08, 1.17) * mm, "end": v(111.93, 0.25) * mm});
            skLineSegment(sketch, "E2372", {"start": v(111.93, 0.25) * mm, "end": v(111.83, -0.7) * mm});
            skLineSegment(sketch, "E2373", {"start": v(111.83, -0.7) * mm, "end": v(111.76, -1.65) * mm});
            skLineSegment(sketch, "E2374", {"start": v(111.76, -1.65) * mm, "end": v(111.74, -2.63) * mm});
            skLineSegment(sketch, "E2375", {"start": v(111.74, -2.63) * mm, "end": v(111.75, -3.45) * mm});
            skLineSegment(sketch, "E2376", {"start": v(111.75, -3.45) * mm, "end": v(111.8, -4.26) * mm});
            skLineSegment(sketch, "E2377", {"start": v(111.8, -4.26) * mm, "end": v(111.89, -5.07) * mm});
            skLineSegment(sketch, "E2378", {"start": v(111.89, -5.07) * mm, "end": v(112, -5.86) * mm});
            skLineSegment(sketch, "E2379", {"start": v(112, -5.86) * mm, "end": v(112.15, -6.64) * mm});
            skLineSegment(sketch, "E2380", {"start": v(112.15, -6.64) * mm, "end": v(112.34, -7.4) * mm});
            skLineSegment(sketch, "E2381", {"start": v(112.34, -7.4) * mm, "end": v(112.55, -8.17) * mm});
            skLineSegment(sketch, "E2382", {"start": v(112.55, -8.17) * mm, "end": v(112.8, -8.92) * mm});
            skLineSegment(sketch, "E2383", {"start": v(112.8, -8.92) * mm, "end": v(113.08, -9.66) * mm});
            skLineSegment(sketch, "E2384", {"start": v(113.08, -9.66) * mm, "end": v(113.4, -10.38) * mm});
            skLineSegment(sketch, "E2385", {"start": v(113.4, -10.38) * mm, "end": v(113.74, -11.1) * mm});
            skLineSegment(sketch, "E2386", {"start": v(113.74, -11.1) * mm, "end": v(114.12, -11.8) * mm});
            skLineSegment(sketch, "E2387", {"start": v(114.12, -11.8) * mm, "end": v(114.54, -12.5) * mm});
            skLineSegment(sketch, "E2388", {"start": v(114.54, -12.5) * mm, "end": v(114.98, -13.17) * mm});
            skLineSegment(sketch, "E2389", {"start": v(114.98, -13.17) * mm, "end": v(115.46, -13.84) * mm});
            skLineSegment(sketch, "E2390", {"start": v(115.46, -13.84) * mm, "end": v(115.97, -14.5) * mm});
            skLineSegment(sketch, "E2391", {"start": v(115.97, -14.5) * mm, "end": v(116.47, -15.1) * mm});
            skLineSegment(sketch, "E2392", {"start": v(116.47, -15.1) * mm, "end": v(117, -15.67) * mm});
            skLineSegment(sketch, "E2393", {"start": v(117, -15.67) * mm, "end": v(117.53, -16.21) * mm});
            skLineSegment(sketch, "E2394", {"start": v(117.53, -16.21) * mm, "end": v(118.1, -16.74) * mm});
            skLineSegment(sketch, "E2395", {"start": v(118.1, -16.74) * mm, "end": v(118.66, -17.23) * mm});
            skLineSegment(sketch, "E2396", {"start": v(118.66, -17.23) * mm, "end": v(119.25, -17.7) * mm});
            skLineSegment(sketch, "E2397", {"start": v(119.25, -17.7) * mm, "end": v(119.86, -18.14) * mm});
            skLineSegment(sketch, "E2398", {"start": v(119.86, -18.14) * mm, "end": v(120.48, -18.56) * mm});
            skLineSegment(sketch, "E2399", {"start": v(120.48, -18.56) * mm, "end": v(121.12, -18.95) * mm});
            skLineSegment(sketch, "E2400", {"start": v(121.12, -18.95) * mm, "end": v(121.77, -19.31) * mm});
            skLineSegment(sketch, "E2401", {"start": v(121.77, -19.31) * mm, "end": v(122.44, -19.65) * mm});
            skLineSegment(sketch, "E2402", {"start": v(122.44, -19.65) * mm, "end": v(123.13, -19.96) * mm});
            skLineSegment(sketch, "E2403", {"start": v(123.13, -19.96) * mm, "end": v(123.83, -20.24) * mm});
            skLineSegment(sketch, "E2404", {"start": v(123.83, -20.24) * mm, "end": v(124.54, -20.5) * mm});
            skLineSegment(sketch, "E2405", {"start": v(124.54, -20.5) * mm, "end": v(125.27, -20.72) * mm});
            skLineSegment(sketch, "E2406", {"start": v(125.27, -20.72) * mm, "end": v(126.02, -20.92) * mm});
            skLineSegment(sketch, "E2407", {"start": v(126.02, -20.92) * mm, "end": v(126.09, -20.94) * mm});
            skLineSegment(sketch, "E2408", {"start": v(126.09, -20.94) * mm, "end": v(126.16, -20.97) * mm});
            skLineSegment(sketch, "E2409", {"start": v(126.16, -20.97) * mm, "end": v(126.22, -21) * mm});
            skLineSegment(sketch, "E2410", {"start": v(126.22, -21) * mm, "end": v(126.28, -21.04) * mm});
            skLineSegment(sketch, "E2411", {"start": v(126.28, -21.04) * mm, "end": v(126.34, -21.08) * mm});
            skLineSegment(sketch, "E2412", {"start": v(126.34, -21.08) * mm, "end": v(126.39, -21.12) * mm});
            skLineSegment(sketch, "E2413", {"start": v(126.39, -21.12) * mm, "end": v(126.44, -21.17) * mm});
            skLineSegment(sketch, "E2414", {"start": v(126.44, -21.17) * mm, "end": v(126.48, -21.23) * mm});
            skLineSegment(sketch, "E2415", {"start": v(126.48, -21.23) * mm, "end": v(126.52, -21.28) * mm});
            skLineSegment(sketch, "E2416", {"start": v(126.52, -21.28) * mm, "end": v(126.56, -21.34) * mm});
            skLineSegment(sketch, "E2417", {"start": v(126.56, -21.34) * mm, "end": v(126.59, -21.4) * mm});
            skLineSegment(sketch, "E2418", {"start": v(126.59, -21.4) * mm, "end": v(126.61, -21.47) * mm});
            skLineSegment(sketch, "E2419", {"start": v(126.61, -21.47) * mm, "end": v(126.63, -21.54) * mm});
            skLineSegment(sketch, "E2420", {"start": v(126.63, -21.54) * mm, "end": v(126.65, -21.61) * mm});
            skLineSegment(sketch, "E2421", {"start": v(126.65, -21.61) * mm, "end": v(126.66, -21.69) * mm});
            skLineSegment(sketch, "E2422", {"start": v(126.66, -21.69) * mm, "end": v(126.66, -21.76) * mm});
            skLineSegment(sketch, "E2423", {"start": v(126.66, -21.76) * mm, "end": v(126.66, -22.9) * mm});
            skLineSegment(sketch, "E2424", {"start": v(126.66, -22.9) * mm, "end": v(126.66, -22.96) * mm});
            skLineSegment(sketch, "E2425", {"start": v(126.66, -22.96) * mm, "end": v(126.65, -23.02) * mm});
            skLineSegment(sketch, "E2426", {"start": v(126.65, -23.02) * mm, "end": v(126.63, -23.07) * mm});
            skLineSegment(sketch, "E2427", {"start": v(126.63, -23.07) * mm, "end": v(126.61, -23.13) * mm});
            skLineSegment(sketch, "E2428", {"start": v(126.61, -23.13) * mm, "end": v(126.59, -23.18) * mm});
            skLineSegment(sketch, "E2429", {"start": v(126.59, -23.18) * mm, "end": v(126.56, -23.23) * mm});
            skLineSegment(sketch, "E2430", {"start": v(126.56, -23.23) * mm, "end": v(126.53, -23.27) * mm});
            skLineSegment(sketch, "E2431", {"start": v(126.53, -23.27) * mm, "end": v(126.49, -23.31) * mm});
            skLineSegment(sketch, "E2432", {"start": v(126.49, -23.31) * mm, "end": v(126.45, -23.35) * mm});
            skLineSegment(sketch, "E2433", {"start": v(126.45, -23.35) * mm, "end": v(126.4, -23.38) * mm});
            skLineSegment(sketch, "E2434", {"start": v(126.4, -23.38) * mm, "end": v(126.35, -23.41) * mm});
            skLineSegment(sketch, "E2435", {"start": v(126.35, -23.41) * mm, "end": v(126.3, -23.44) * mm});
            skLineSegment(sketch, "E2436", {"start": v(126.3, -23.44) * mm, "end": v(126.25, -23.46) * mm});
            skLineSegment(sketch, "E2437", {"start": v(126.25, -23.46) * mm, "end": v(126.2, -23.47) * mm});
            skLineSegment(sketch, "E2438", {"start": v(126.2, -23.47) * mm, "end": v(126.13, -23.48) * mm});
            skLineSegment(sketch, "E2439", {"start": v(126.13, -23.48) * mm, "end": v(126.07, -23.48) * mm});
            skLineSegment(sketch, "E2440", {"start": v(126.07, -23.48) * mm, "end": v(95.18, -23.48) * mm});
            skLineSegment(sketch, "E2441", {"start": v(95.18, -23.48) * mm, "end": v(94.87, -23.47) * mm});
            skLineSegment(sketch, "E2442", {"start": v(94.87, -23.47) * mm, "end": v(94.56, -23.42) * mm});
            skLineSegment(sketch, "E2443", {"start": v(94.56, -23.42) * mm, "end": v(94.27, -23.35) * mm});
            skLineSegment(sketch, "E2444", {"start": v(94.27, -23.35) * mm, "end": v(93.98, -23.24) * mm});
            skLineSegment(sketch, "E2445", {"start": v(93.98, -23.24) * mm, "end": v(93.71, -23.11) * mm});
            skLineSegment(sketch, "E2446", {"start": v(93.71, -23.11) * mm, "end": v(93.46, -22.96) * mm});
            skLineSegment(sketch, "E2447", {"start": v(93.46, -22.96) * mm, "end": v(93.22, -22.78) * mm});
            skLineSegment(sketch, "E2448", {"start": v(93.22, -22.78) * mm, "end": v(93, -22.58) * mm});
            skLineSegment(sketch, "E2449", {"start": v(93, -22.58) * mm, "end": v(92.8, -22.36) * mm});
            skLineSegment(sketch, "E2450", {"start": v(92.8, -22.36) * mm, "end": v(92.62, -22.12) * mm});
            skLineSegment(sketch, "E2451", {"start": v(92.62, -22.12) * mm, "end": v(92.47, -21.87) * mm});
            skLineSegment(sketch, "E2452", {"start": v(92.47, -21.87) * mm, "end": v(92.34, -21.6) * mm});
            skLineSegment(sketch, "E2453", {"start": v(92.34, -21.6) * mm, "end": v(92.23, -21.31) * mm});
            skLineSegment(sketch, "E2454", {"start": v(92.23, -21.31) * mm, "end": v(92.16, -21.02) * mm});
            skLineSegment(sketch, "E2455", {"start": v(92.16, -21.02) * mm, "end": v(92.11, -20.7) * mm});
            skLineSegment(sketch, "E2456", {"start": v(92.11, -20.7) * mm, "end": v(92.1, -20.4) * mm});
            skLineSegment(sketch, "E2457", {"start": v(92.1, -20.4) * mm, "end": v(92.1, 7.6) * mm});
            skLineSegment(sketch, "E2458", {"start": v(92.1, 7.6) * mm, "end": v(92.1, 7.65) * mm});
            skLineSegment(sketch, "E2459", {"start": v(92.1, 7.65) * mm, "end": v(92.1, 7.7) * mm});
            skLineSegment(sketch, "E2460", {"start": v(92.1, 7.7) * mm, "end": v(92.12, 7.75) * mm});
            skLineSegment(sketch, "E2461", {"start": v(92.12, 7.75) * mm, "end": v(92.14, 7.8) * mm});
            skLineSegment(sketch, "E2462", {"start": v(92.14, 7.8) * mm, "end": v(92.16, 7.85) * mm});
            skLineSegment(sketch, "E2463", {"start": v(92.16, 7.85) * mm, "end": v(92.18, 7.89) * mm});
            skLineSegment(sketch, "E2464", {"start": v(92.18, 7.89) * mm, "end": v(92.21, 7.93) * mm});
            skLineSegment(sketch, "E2465", {"start": v(92.21, 7.93) * mm, "end": v(92.25, 7.97) * mm});
            skLineSegment(sketch, "E2466", {"start": v(92.25, 7.97) * mm, "end": v(92.28, 8) * mm});
            skLineSegment(sketch, "E2467", {"start": v(92.28, 8) * mm, "end": v(92.33, 8.03) * mm});
            skLineSegment(sketch, "E2468", {"start": v(92.33, 8.03) * mm, "end": v(92.37, 8.06) * mm});
            skLineSegment(sketch, "E2469", {"start": v(92.37, 8.06) * mm, "end": v(92.41, 8.08) * mm});
            skLineSegment(sketch, "E2470", {"start": v(92.41, 8.08) * mm, "end": v(92.46, 8.1) * mm});
            skLineSegment(sketch, "E2471", {"start": v(92.46, 8.1) * mm, "end": v(92.51, 8.1) * mm});
            skLineSegment(sketch, "E2472", {"start": v(92.51, 8.1) * mm, "end": v(92.56, 8.12) * mm});
            skLineSegment(sketch, "E2473", {"start": v(92.56, 8.12) * mm, "end": v(92.62, 8.12) * mm});
            skLineSegment(sketch, "E2474", {"start": v(92.62, 8.12) * mm, "end": v(102.95, 8.12) * mm});
            skLineSegment(sketch, "E2475", {"start": v(102.95, 8.12) * mm, "end": v(103.17, 8.12) * mm});
            skLineSegment(sketch, "E2476", {"start": v(103.17, 8.12) * mm, "end": v(103.38, 8.14) * mm});
            skLineSegment(sketch, "E2477", {"start": v(103.38, 8.14) * mm, "end": v(103.6, 8.16) * mm});
            skLineSegment(sketch, "E2478", {"start": v(103.6, 8.16) * mm, "end": v(103.8, 8.19) * mm});
            skLineSegment(sketch, "E2479", {"start": v(103.8, 8.19) * mm, "end": v(104, 8.23) * mm});
            skLineSegment(sketch, "E2480", {"start": v(104, 8.23) * mm, "end": v(104.19, 8.27) * mm});
            skLineSegment(sketch, "E2481", {"start": v(104.19, 8.27) * mm, "end": v(104.38, 8.33) * mm});
            skLineSegment(sketch, "E2482", {"start": v(104.38, 8.33) * mm, "end": v(104.56, 8.4) * mm});
            skLineSegment(sketch, "E2483", {"start": v(104.56, 8.4) * mm, "end": v(104.74, 8.46) * mm});
            skLineSegment(sketch, "E2484", {"start": v(104.74, 8.46) * mm, "end": v(104.9, 8.55) * mm});
            skLineSegment(sketch, "E2485", {"start": v(104.9, 8.55) * mm, "end": v(105.08, 8.63) * mm});
            skLineSegment(sketch, "E2486", {"start": v(105.08, 8.63) * mm, "end": v(105.24, 8.73) * mm});
            skLineSegment(sketch, "E2487", {"start": v(105.24, 8.73) * mm, "end": v(105.4, 8.84) * mm});
            skLineSegment(sketch, "E2488", {"start": v(105.4, 8.84) * mm, "end": v(105.54, 8.95) * mm});
            skLineSegment(sketch, "E2489", {"start": v(105.54, 8.95) * mm, "end": v(105.69, 9.08) * mm});
            skLineSegment(sketch, "E2490", {"start": v(105.69, 9.08) * mm, "end": v(105.82, 9.2) * mm});
            skLineSegment(sketch, "E2491", {"start": v(105.82, 9.2) * mm, "end": v(105.95, 9.34) * mm});
            skLineSegment(sketch, "E2492", {"start": v(105.95, 9.34) * mm, "end": v(106.08, 9.49) * mm});
            skLineSegment(sketch, "E2493", {"start": v(106.08, 9.49) * mm, "end": v(106.2, 9.64) * mm});
            skLineSegment(sketch, "E2494", {"start": v(106.2, 9.64) * mm, "end": v(106.3, 9.8) * mm});
            skLineSegment(sketch, "E2495", {"start": v(106.3, 9.8) * mm, "end": v(106.4, 9.95) * mm});
            skLineSegment(sketch, "E2496", {"start": v(106.4, 9.95) * mm, "end": v(106.49, 10.12) * mm});
            skLineSegment(sketch, "E2497", {"start": v(106.49, 10.12) * mm, "end": v(106.57, 10.3) * mm});
            skLineSegment(sketch, "E2498", {"start": v(106.57, 10.3) * mm, "end": v(106.64, 10.47) * mm});
            skLineSegment(sketch, "E2499", {"start": v(106.64, 10.47) * mm, "end": v(106.7, 10.65) * mm});
            skLineSegment(sketch, "E2500", {"start": v(106.7, 10.65) * mm, "end": v(106.76, 10.84) * mm});
            skLineSegment(sketch, "E2501", {"start": v(106.76, 10.84) * mm, "end": v(106.8, 11.03) * mm});
            skLineSegment(sketch, "E2502", {"start": v(106.8, 11.03) * mm, "end": v(106.84, 11.23) * mm});
            skLineSegment(sketch, "E2503", {"start": v(106.84, 11.23) * mm, "end": v(106.87, 11.44) * mm});
            skLineSegment(sketch, "E2504", {"start": v(106.87, 11.44) * mm, "end": v(106.9, 11.65) * mm});
            skLineSegment(sketch, "E2505", {"start": v(106.9, 11.65) * mm, "end": v(106.9, 11.86) * mm});
            skLineSegment(sketch, "E2506", {"start": v(106.9, 11.86) * mm, "end": v(106.91, 12.08) * mm});
            skLineSegment(sketch, "E2507", {"start": v(106.91, 12.08) * mm, "end": v(106.9, 12.3) * mm});
            skLineSegment(sketch, "E2508", {"start": v(106.9, 12.3) * mm, "end": v(106.9, 12.52) * mm});
            skLineSegment(sketch, "E2509", {"start": v(106.9, 12.52) * mm, "end": v(106.87, 12.73) * mm});
            skLineSegment(sketch, "E2510", {"start": v(106.87, 12.73) * mm, "end": v(106.84, 12.93) * mm});
            skLineSegment(sketch, "E2511", {"start": v(106.84, 12.93) * mm, "end": v(106.8, 13.13) * mm});
            skLineSegment(sketch, "E2512", {"start": v(106.8, 13.13) * mm, "end": v(106.76, 13.32) * mm});
            skLineSegment(sketch, "E2513", {"start": v(106.76, 13.32) * mm, "end": v(106.7, 13.5) * mm});
            skLineSegment(sketch, "E2514", {"start": v(106.7, 13.5) * mm, "end": v(106.64, 13.7) * mm});
            skLineSegment(sketch, "E2515", {"start": v(106.64, 13.7) * mm, "end": v(106.57, 13.87) * mm});
            skLineSegment(sketch, "E2516", {"start": v(106.57, 13.87) * mm, "end": v(106.49, 14.04) * mm});
            skLineSegment(sketch, "E2517", {"start": v(106.49, 14.04) * mm, "end": v(106.4, 14.2) * mm});
            skLineSegment(sketch, "E2518", {"start": v(106.4, 14.2) * mm, "end": v(106.3, 14.37) * mm});
            skLineSegment(sketch, "E2519", {"start": v(106.3, 14.37) * mm, "end": v(106.2, 14.52) * mm});
            skLineSegment(sketch, "E2520", {"start": v(106.2, 14.52) * mm, "end": v(106.08, 14.67) * mm});
            skLineSegment(sketch, "E2521", {"start": v(106.08, 14.67) * mm, "end": v(105.95, 14.82) * mm});
            skLineSegment(sketch, "E2522", {"start": v(105.95, 14.82) * mm, "end": v(105.82, 14.96) * mm});
            skLineSegment(sketch, "E2523", {"start": v(105.82, 14.96) * mm, "end": v(105.69, 15.09) * mm});
            skLineSegment(sketch, "E2524", {"start": v(105.69, 15.09) * mm, "end": v(105.54, 15.21) * mm});
            skLineSegment(sketch, "E2525", {"start": v(105.54, 15.21) * mm, "end": v(105.4, 15.33) * mm});
            skLineSegment(sketch, "E2526", {"start": v(105.4, 15.33) * mm, "end": v(105.24, 15.43) * mm});
            skLineSegment(sketch, "E2527", {"start": v(105.24, 15.43) * mm, "end": v(105.08, 15.53) * mm});
            skLineSegment(sketch, "E2528", {"start": v(105.08, 15.53) * mm, "end": v(104.9, 15.62) * mm});
            skLineSegment(sketch, "E2529", {"start": v(104.9, 15.62) * mm, "end": v(104.74, 15.7) * mm});
            skLineSegment(sketch, "E2530", {"start": v(104.74, 15.7) * mm, "end": v(104.56, 15.77) * mm});
            skLineSegment(sketch, "E2531", {"start": v(104.56, 15.77) * mm, "end": v(104.38, 15.84) * mm});
            skLineSegment(sketch, "E2532", {"start": v(104.38, 15.84) * mm, "end": v(104.19, 15.9) * mm});
            skLineSegment(sketch, "E2533", {"start": v(104.19, 15.9) * mm, "end": v(104, 15.94) * mm});
            skLineSegment(sketch, "E2534", {"start": v(104, 15.94) * mm, "end": v(103.8, 15.98) * mm});
            skLineSegment(sketch, "E2535", {"start": v(103.8, 15.98) * mm, "end": v(103.6, 16) * mm});
            skLineSegment(sketch, "E2536", {"start": v(103.6, 16) * mm, "end": v(103.38, 16.03) * mm});
            skLineSegment(sketch, "E2537", {"start": v(103.38, 16.03) * mm, "end": v(103.17, 16.04) * mm});
            skLineSegment(sketch, "E2538", {"start": v(103.17, 16.04) * mm, "end": v(102.95, 16.04) * mm});
            skLineSegment(sketch, "E2539", {"start": v(102.95, 16.04) * mm, "end": v(73.32, 16.04) * mm});
            skLineSegment(sketch, "E2540", {"start": v(73.32, 16.04) * mm, "end": v(73.1, 16.04) * mm});
            skLineSegment(sketch, "E2541", {"start": v(73.1, 16.04) * mm, "end": v(72.88, 16.03) * mm});
            skLineSegment(sketch, "E2542", {"start": v(72.88, 16.03) * mm, "end": v(72.67, 16) * mm});
            skLineSegment(sketch, "E2543", {"start": v(72.67, 16) * mm, "end": v(72.47, 15.98) * mm});
            skLineSegment(sketch, "E2544", {"start": v(72.47, 15.98) * mm, "end": v(72.27, 15.94) * mm});
            skLineSegment(sketch, "E2545", {"start": v(72.27, 15.94) * mm, "end": v(72.07, 15.9) * mm});
            skLineSegment(sketch, "E2546", {"start": v(72.07, 15.9) * mm, "end": v(71.89, 15.84) * mm});
            skLineSegment(sketch, "E2547", {"start": v(71.89, 15.84) * mm, "end": v(71.7, 15.77) * mm});
            skLineSegment(sketch, "E2548", {"start": v(71.7, 15.77) * mm, "end": v(71.53, 15.7) * mm});
            skLineSegment(sketch, "E2549", {"start": v(71.53, 15.7) * mm, "end": v(71.35, 15.62) * mm});
            skLineSegment(sketch, "E2550", {"start": v(71.35, 15.62) * mm, "end": v(71.19, 15.53) * mm});
            skLineSegment(sketch, "E2551", {"start": v(71.19, 15.53) * mm, "end": v(71.03, 15.43) * mm});
            skLineSegment(sketch, "E2552", {"start": v(71.03, 15.43) * mm, "end": v(70.87, 15.33) * mm});
            skLineSegment(sketch, "E2553", {"start": v(70.87, 15.33) * mm, "end": v(70.72, 15.21) * mm});
            skLineSegment(sketch, "E2554", {"start": v(70.72, 15.21) * mm, "end": v(70.58, 15.09) * mm});
            skLineSegment(sketch, "E2555", {"start": v(70.58, 15.09) * mm, "end": v(70.44, 14.96) * mm});
            skLineSegment(sketch, "E2556", {"start": v(70.44, 14.96) * mm, "end": v(70.3, 14.82) * mm});
            skLineSegment(sketch, "E2557", {"start": v(70.3, 14.82) * mm, "end": v(70.19, 14.67) * mm});
            skLineSegment(sketch, "E2558", {"start": v(70.19, 14.67) * mm, "end": v(70.07, 14.53) * mm});
            skLineSegment(sketch, "E2559", {"start": v(70.07, 14.53) * mm, "end": v(69.97, 14.37) * mm});
            skLineSegment(sketch, "E2560", {"start": v(69.97, 14.37) * mm, "end": v(69.87, 14.2) * mm});
            skLineSegment(sketch, "E2561", {"start": v(69.87, 14.2) * mm, "end": v(69.78, 14.04) * mm});
            skLineSegment(sketch, "E2562", {"start": v(69.78, 14.04) * mm, "end": v(69.7, 13.87) * mm});
            skLineSegment(sketch, "E2563", {"start": v(69.7, 13.87) * mm, "end": v(69.63, 13.7) * mm});
            skLineSegment(sketch, "E2564", {"start": v(69.63, 13.7) * mm, "end": v(69.56, 13.51) * mm});
            skLineSegment(sketch, "E2565", {"start": v(69.56, 13.51) * mm, "end": v(69.5, 13.32) * mm});
            skLineSegment(sketch, "E2566", {"start": v(69.5, 13.32) * mm, "end": v(69.46, 13.13) * mm});
            skLineSegment(sketch, "E2567", {"start": v(69.46, 13.13) * mm, "end": v(69.42, 12.93) * mm});
            skLineSegment(sketch, "E2568", {"start": v(69.42, 12.93) * mm, "end": v(69.4, 12.73) * mm});
            skLineSegment(sketch, "E2569", {"start": v(69.4, 12.73) * mm, "end": v(69.37, 12.52) * mm});
            skLineSegment(sketch, "E2570", {"start": v(69.37, 12.52) * mm, "end": v(69.36, 12.3) * mm});
            skLineSegment(sketch, "E2571", {"start": v(69.36, 12.3) * mm, "end": v(69.35, 12.08) * mm});
            skLineSegment(sketch, "E2572", {"start": v(69.35, 12.08) * mm, "end": v(69.36, 11.87) * mm});
            skLineSegment(sketch, "E2573", {"start": v(69.36, 11.87) * mm, "end": v(69.37, 11.66) * mm});
            skLineSegment(sketch, "E2574", {"start": v(69.37, 11.66) * mm, "end": v(69.4, 11.45) * mm});
            skLineSegment(sketch, "E2575", {"start": v(69.4, 11.45) * mm, "end": v(69.42, 11.25) * mm});
            skLineSegment(sketch, "E2576", {"start": v(69.42, 11.25) * mm, "end": v(69.46, 11.06) * mm});
            skLineSegment(sketch, "E2577", {"start": v(69.46, 11.06) * mm, "end": v(69.5, 10.87) * mm});
            skLineSegment(sketch, "E2578", {"start": v(69.5, 10.87) * mm, "end": v(69.57, 10.68) * mm});
            skLineSegment(sketch, "E2579", {"start": v(69.57, 10.68) * mm, "end": v(69.63, 10.5) * mm});
            skLineSegment(sketch, "E2580", {"start": v(69.63, 10.5) * mm, "end": v(69.7, 10.33) * mm});
            skLineSegment(sketch, "E2581", {"start": v(69.7, 10.33) * mm, "end": v(69.79, 10.16) * mm});
            skLineSegment(sketch, "E2582", {"start": v(69.79, 10.16) * mm, "end": v(69.88, 9.99) * mm});
            skLineSegment(sketch, "E2583", {"start": v(69.88, 9.99) * mm, "end": v(69.98, 9.83) * mm});
            skLineSegment(sketch, "E2584", {"start": v(69.98, 9.83) * mm, "end": v(70.09, 9.67) * mm});
            skLineSegment(sketch, "E2585", {"start": v(70.09, 9.67) * mm, "end": v(70.2, 9.52) * mm});
            skLineSegment(sketch, "E2586", {"start": v(70.2, 9.52) * mm, "end": v(70.33, 9.37) * mm});
            skLineSegment(sketch, "E2587", {"start": v(70.33, 9.37) * mm, "end": v(70.47, 9.23) * mm});
            skLineSegment(sketch, "E2588", {"start": v(70.47, 9.23) * mm, "end": v(70.6, 9.1) * mm});
            skLineSegment(sketch, "E2589", {"start": v(70.6, 9.1) * mm, "end": v(70.75, 8.97) * mm});
            skLineSegment(sketch, "E2590", {"start": v(70.75, 8.97) * mm, "end": v(70.9, 8.86) * mm});
            skLineSegment(sketch, "E2591", {"start": v(70.9, 8.86) * mm, "end": v(71.06, 8.75) * mm});
            skLineSegment(sketch, "E2592", {"start": v(71.06, 8.75) * mm, "end": v(71.22, 8.65) * mm});
            skLineSegment(sketch, "E2593", {"start": v(71.22, 8.65) * mm, "end": v(71.39, 8.56) * mm});
            skLineSegment(sketch, "E2594", {"start": v(71.39, 8.56) * mm, "end": v(71.56, 8.47) * mm});
            skLineSegment(sketch, "E2595", {"start": v(71.56, 8.47) * mm, "end": v(71.74, 8.4) * mm});
            skLineSegment(sketch, "E2596", {"start": v(71.74, 8.4) * mm, "end": v(71.92, 8.33) * mm});
            skLineSegment(sketch, "E2597", {"start": v(71.92, 8.33) * mm, "end": v(72.1, 8.28) * mm});
            skLineSegment(sketch, "E2598", {"start": v(72.1, 8.28) * mm, "end": v(72.3, 8.23) * mm});
            skLineSegment(sketch, "E2599", {"start": v(72.3, 8.23) * mm, "end": v(72.49, 8.19) * mm});
            skLineSegment(sketch, "E2600", {"start": v(72.49, 8.19) * mm, "end": v(72.69, 8.16) * mm});
            skLineSegment(sketch, "E2601", {"start": v(72.69, 8.16) * mm, "end": v(72.9, 8.14) * mm});
            skLineSegment(sketch, "E2602", {"start": v(72.9, 8.14) * mm, "end": v(73.1, 8.12) * mm});
            skLineSegment(sketch, "E2603", {"start": v(73.1, 8.12) * mm, "end": v(73.32, 8.12) * mm});
            skLineSegment(sketch, "E2604", {"start": v(73.32, 8.12) * mm, "end": v(83.65, 8.12) * mm});
            skLineSegment(sketch, "E2605", {"start": v(83.65, 8.12) * mm, "end": v(83.7, 8.12) * mm});
            skLineSegment(sketch, "E2606", {"start": v(83.7, 8.12) * mm, "end": v(83.75, 8.1) * mm});
            skLineSegment(sketch, "E2607", {"start": v(83.75, 8.1) * mm, "end": v(83.8, 8.1) * mm});
            skLineSegment(sketch, "E2608", {"start": v(83.8, 8.1) * mm, "end": v(83.85, 8.08) * mm});
            skLineSegment(sketch, "E2609", {"start": v(83.85, 8.08) * mm, "end": v(83.9, 8.06) * mm});
            skLineSegment(sketch, "E2610", {"start": v(83.9, 8.06) * mm, "end": v(83.94, 8.03) * mm});
            skLineSegment(sketch, "E2611", {"start": v(83.94, 8.03) * mm, "end": v(83.98, 8) * mm});
            skLineSegment(sketch, "E2612", {"start": v(83.98, 8) * mm, "end": v(84.02, 7.97) * mm});
            skLineSegment(sketch, "E2613", {"start": v(84.02, 7.97) * mm, "end": v(84.05, 7.93) * mm});
            skLineSegment(sketch, "E2614", {"start": v(84.05, 7.93) * mm, "end": v(84.08, 7.89) * mm});
            skLineSegment(sketch, "E2615", {"start": v(84.08, 7.89) * mm, "end": v(84.1, 7.85) * mm});
            skLineSegment(sketch, "E2616", {"start": v(84.1, 7.85) * mm, "end": v(84.13, 7.8) * mm});
            skLineSegment(sketch, "E2617", {"start": v(84.13, 7.8) * mm, "end": v(84.15, 7.75) * mm});
            skLineSegment(sketch, "E2618", {"start": v(84.15, 7.75) * mm, "end": v(84.16, 7.7) * mm});
            skLineSegment(sketch, "E2619", {"start": v(84.16, 7.7) * mm, "end": v(84.17, 7.65) * mm});
            skLineSegment(sketch, "E2620", {"start": v(84.17, 7.65) * mm, "end": v(84.17, 7.6) * mm});
            skLineSegment(sketch, "E2621", {"start": v(84.17, 7.6) * mm, "end": v(84.17, -20.4) * mm});
            skLineSegment(sketch, "E2622", {"start": v(84.17, -20.4) * mm, "end": v(84.15, -20.7) * mm});
            skLineSegment(sketch, "E2623", {"start": v(84.15, -20.7) * mm, "end": v(84.1, -21.02) * mm});
            skLineSegment(sketch, "E2624", {"start": v(84.1, -21.02) * mm, "end": v(84.03, -21.31) * mm});
            skLineSegment(sketch, "E2625", {"start": v(84.03, -21.31) * mm, "end": v(83.93, -21.6) * mm});
            skLineSegment(sketch, "E2626", {"start": v(83.93, -21.6) * mm, "end": v(83.8, -21.87) * mm});
            skLineSegment(sketch, "E2627", {"start": v(83.8, -21.87) * mm, "end": v(83.64, -22.12) * mm});
            skLineSegment(sketch, "E2628", {"start": v(83.64, -22.12) * mm, "end": v(83.46, -22.36) * mm});
            skLineSegment(sketch, "E2629", {"start": v(83.46, -22.36) * mm, "end": v(83.26, -22.58) * mm});
            skLineSegment(sketch, "E2630", {"start": v(83.26, -22.58) * mm, "end": v(83.04, -22.78) * mm});
            skLineSegment(sketch, "E2631", {"start": v(83.04, -22.78) * mm, "end": v(82.8, -22.96) * mm});
            skLineSegment(sketch, "E2632", {"start": v(82.8, -22.96) * mm, "end": v(82.55, -23.11) * mm});
            skLineSegment(sketch, "E2633", {"start": v(82.55, -23.11) * mm, "end": v(82.28, -23.24) * mm});
            skLineSegment(sketch, "E2634", {"start": v(82.28, -23.24) * mm, "end": v(82, -23.35) * mm});
            skLineSegment(sketch, "E2635", {"start": v(82, -23.35) * mm, "end": v(81.7, -23.42) * mm});
            skLineSegment(sketch, "E2636", {"start": v(81.7, -23.42) * mm, "end": v(81.4, -23.47) * mm});
            skLineSegment(sketch, "E2637", {"start": v(81.4, -23.47) * mm, "end": v(81.08, -23.48) * mm});
            skLineSegment(sketch, "E2638", {"start": v(81.08, -23.48) * mm, "end": v(45.27, -23.48) * mm});
            skLineSegment(sketch, "E2639", {"start": v(45.27, -23.48) * mm, "end": v(45.23, -23.48) * mm});
            skLineSegment(sketch, "E2640", {"start": v(45.23, -23.48) * mm, "end": v(45.18, -23.48) * mm});
            skLineSegment(sketch, "E2641", {"start": v(45.18, -23.48) * mm, "end": v(45.14, -23.46) * mm});
            skLineSegment(sketch, "E2642", {"start": v(45.14, -23.46) * mm, "end": v(45.1, -23.45) * mm});
            skLineSegment(sketch, "E2643", {"start": v(45.1, -23.45) * mm, "end": v(45.07, -23.43) * mm});
            skLineSegment(sketch, "E2644", {"start": v(45.07, -23.43) * mm, "end": v(45.03, -23.41) * mm});
            skLineSegment(sketch, "E2645", {"start": v(45.03, -23.41) * mm, "end": v(45, -23.39) * mm});
            skLineSegment(sketch, "E2646", {"start": v(45, -23.39) * mm, "end": v(44.97, -23.36) * mm});
            skLineSegment(sketch, "E2647", {"start": v(44.97, -23.36) * mm, "end": v(44.94, -23.33) * mm});
            skLineSegment(sketch, "E2648", {"start": v(44.94, -23.33) * mm, "end": v(44.91, -23.3) * mm});
            skLineSegment(sketch, "E2649", {"start": v(44.91, -23.3) * mm, "end": v(44.9, -23.26) * mm});
            skLineSegment(sketch, "E2650", {"start": v(44.9, -23.26) * mm, "end": v(44.87, -23.22) * mm});
            skLineSegment(sketch, "E2651", {"start": v(44.87, -23.22) * mm, "end": v(44.86, -23.18) * mm});
            skLineSegment(sketch, "E2652", {"start": v(44.86, -23.18) * mm, "end": v(44.85, -23.14) * mm});
            skLineSegment(sketch, "E2653", {"start": v(44.85, -23.14) * mm, "end": v(44.84, -23.1) * mm});
            skLineSegment(sketch, "E2654", {"start": v(44.84, -23.1) * mm, "end": v(44.84, -23.05) * mm});
            skLineSegment(sketch, "E2655", {"start": v(44.84, -23.05) * mm, "end": v(44.84, -7.35) * mm});
            skLineSegment(sketch, "E2656", {"start": v(44.84, -7.35) * mm, "end": v(44.84, -7.29) * mm});
            skLineSegment(sketch, "E2657", {"start": v(44.84, -7.29) * mm, "end": v(44.85, -7.22) * mm});
            skLineSegment(sketch, "E2658", {"start": v(44.85, -7.22) * mm, "end": v(44.87, -7.16) * mm});
            skLineSegment(sketch, "E2659", {"start": v(44.87, -7.16) * mm, "end": v(44.9, -7.1) * mm});
            skLineSegment(sketch, "E2660", {"start": v(44.9, -7.1) * mm, "end": v(44.92, -7.04) * mm});
            skLineSegment(sketch, "E2661", {"start": v(44.92, -7.04) * mm, "end": v(44.95, -6.99) * mm});
            skLineSegment(sketch, "E2662", {"start": v(44.95, -6.99) * mm, "end": v(45, -6.94) * mm});
            skLineSegment(sketch, "E2663", {"start": v(45, -6.94) * mm, "end": v(45.03, -6.9) * mm});
            skLineSegment(sketch, "E2664", {"start": v(45.03, -6.9) * mm, "end": v(45.08, -6.85) * mm});
            skLineSegment(sketch, "E2665", {"start": v(45.08, -6.85) * mm, "end": v(45.13, -6.81) * mm});
            skLineSegment(sketch, "E2666", {"start": v(45.13, -6.81) * mm, "end": v(45.18, -6.78) * mm});
            skLineSegment(sketch, "E2667", {"start": v(45.18, -6.78) * mm, "end": v(45.24, -6.75) * mm});
            skLineSegment(sketch, "E2668", {"start": v(45.24, -6.75) * mm, "end": v(45.3, -6.73) * mm});
            skLineSegment(sketch, "E2669", {"start": v(45.3, -6.73) * mm, "end": v(45.36, -6.71) * mm});
            skLineSegment(sketch, "E2670", {"start": v(45.36, -6.71) * mm, "end": v(45.43, -6.7) * mm});
            skLineSegment(sketch, "E2671", {"start": v(45.43, -6.7) * mm, "end": v(45.5, -6.7) * mm});
            skLineSegment(sketch, "E2672", {"start": v(45.5, -6.7) * mm, "end": v(53.26, -6.7) * mm});
            skLineSegment(sketch, "E2673", {"start": v(53.26, -6.7) * mm, "end": v(53.75, -6.69) * mm});
            skLineSegment(sketch, "E2674", {"start": v(53.75, -6.69) * mm, "end": v(54.24, -6.66) * mm});
            skLineSegment(sketch, "E2675", {"start": v(54.24, -6.66) * mm, "end": v(54.73, -6.62) * mm});
            skLineSegment(sketch, "E2676", {"start": v(54.73, -6.62) * mm, "end": v(55.2, -6.55) * mm});
            skLineSegment(sketch, "E2677", {"start": v(55.2, -6.55) * mm, "end": v(55.67, -6.47) * mm});
            skLineSegment(sketch, "E2678", {"start": v(55.67, -6.47) * mm, "end": v(56.14, -6.37) * mm});
            skLineSegment(sketch, "E2679", {"start": v(56.14, -6.37) * mm, "end": v(56.6, -6.26) * mm});
            skLineSegment(sketch, "E2680", {"start": v(56.6, -6.26) * mm, "end": v(57.05, -6.12) * mm});
            skLineSegment(sketch, "E2681", {"start": v(57.05, -6.12) * mm, "end": v(57.5, -5.97) * mm});
            skLineSegment(sketch, "E2682", {"start": v(57.5, -5.97) * mm, "end": v(57.93, -5.8) * mm});
            skLineSegment(sketch, "E2683", {"start": v(57.93, -5.8) * mm, "end": v(58.36, -5.61) * mm});
            skLineSegment(sketch, "E2684", {"start": v(58.36, -5.61) * mm, "end": v(58.78, -5.4) * mm});
            skLineSegment(sketch, "E2685", {"start": v(58.78, -5.4) * mm, "end": v(59.2, -5.18) * mm});
            skLineSegment(sketch, "E2686", {"start": v(59.2, -5.18) * mm, "end": v(59.61, -4.94) * mm});
            skLineSegment(sketch, "E2687", {"start": v(59.61, -4.94) * mm, "end": v(60.01, -4.68) * mm});
            skLineSegment(sketch, "E2688", {"start": v(60.01, -4.68) * mm, "end": v(60.41, -4.4) * mm});
            skLineSegment(sketch, "E2689", {"start": v(60.41, -4.4) * mm, "end": v(60.92, -4) * mm});
            skLineSegment(sketch, "E2690", {"start": v(60.92, -4) * mm, "end": v(61.4, -3.59) * mm});
            skLineSegment(sketch, "E2691", {"start": v(61.4, -3.59) * mm, "end": v(61.84, -3.14) * mm});
            skLineSegment(sketch, "E2692", {"start": v(61.84, -3.14) * mm, "end": v(62.25, -2.68) * mm});
            skLineSegment(sketch, "E2693", {"start": v(62.25, -2.68) * mm, "end": v(62.63, -2.19) * mm});
            skLineSegment(sketch, "E2694", {"start": v(62.63, -2.19) * mm, "end": v(62.98, -1.67) * mm});
            skLineSegment(sketch, "E2695", {"start": v(62.98, -1.67) * mm, "end": v(63.3, -1.14) * mm});
            skLineSegment(sketch, "E2696", {"start": v(63.3, -1.14) * mm, "end": v(63.57, -0.58) * mm});
            skLineSegment(sketch, "E2697", {"start": v(63.57, -0.58) * mm, "end": v(63.82, 0) * mm});
            skLineSegment(sketch, "E2698", {"start": v(63.82, 0) * mm, "end": v(64.03, 0.6) * mm});
            skLineSegment(sketch, "E2699", {"start": v(64.03, 0.6) * mm, "end": v(64.22, 1.22) * mm});
            skLineSegment(sketch, "E2700", {"start": v(64.22, 1.22) * mm, "end": v(64.37, 1.87) * mm});
            skLineSegment(sketch, "E2701", {"start": v(64.37, 1.87) * mm, "end": v(64.48, 2.54) * mm});
            skLineSegment(sketch, "E2702", {"start": v(64.48, 2.54) * mm, "end": v(64.56, 3.23) * mm});
            skLineSegment(sketch, "E2703", {"start": v(64.56, 3.23) * mm, "end": v(64.61, 3.94) * mm});
            skLineSegment(sketch, "E2704", {"start": v(64.61, 3.94) * mm, "end": v(64.63, 4.67) * mm});
            skLineSegment(sketch, "E2705", {"start": v(64.63, 4.67) * mm, "end": v(64.61, 5.4) * mm});
            skLineSegment(sketch, "E2706", {"start": v(64.61, 5.4) * mm, "end": v(64.56, 6.12) * mm});
            skLineSegment(sketch, "E2707", {"start": v(64.56, 6.12) * mm, "end": v(64.48, 6.8) * mm});
            skLineSegment(sketch, "E2708", {"start": v(64.48, 6.8) * mm, "end": v(64.37, 7.48) * mm});
            skLineSegment(sketch, "E2709", {"start": v(64.37, 7.48) * mm, "end": v(64.22, 8.12) * mm});
            skLineSegment(sketch, "E2710", {"start": v(64.22, 8.12) * mm, "end": v(64.03, 8.75) * mm});
            skLineSegment(sketch, "E2711", {"start": v(64.03, 8.75) * mm, "end": v(63.82, 9.35) * mm});
            skLineSegment(sketch, "E2712", {"start": v(63.82, 9.35) * mm, "end": v(63.57, 9.93) * mm});
            skLineSegment(sketch, "E2713", {"start": v(63.57, 9.93) * mm, "end": v(63.3, 10.48) * mm});
            skLineSegment(sketch, "E2714", {"start": v(63.3, 10.48) * mm, "end": v(62.98, 11.02) * mm});
            skLineSegment(sketch, "E2715", {"start": v(62.98, 11.02) * mm, "end": v(62.63, 11.53) * mm});
            skLineSegment(sketch, "E2716", {"start": v(62.63, 11.53) * mm, "end": v(62.25, 12.02) * mm});
            skLineSegment(sketch, "E2717", {"start": v(62.25, 12.02) * mm, "end": v(61.84, 12.49) * mm});
            skLineSegment(sketch, "E2718", {"start": v(61.84, 12.49) * mm, "end": v(61.4, 12.93) * mm});
            skLineSegment(sketch, "E2719", {"start": v(61.4, 12.93) * mm, "end": v(60.92, 13.35) * mm});
            skLineSegment(sketch, "E2720", {"start": v(60.92, 13.35) * mm, "end": v(60.4, 13.75) * mm});
            skLineSegment(sketch, "E2721", {"start": v(60.4, 13.75) * mm, "end": v(60.01, 14.03) * mm});
            skLineSegment(sketch, "E2722", {"start": v(60.01, 14.03) * mm, "end": v(59.61, 14.29) * mm});
            skLineSegment(sketch, "E2723", {"start": v(59.61, 14.29) * mm, "end": v(59.2, 14.53) * mm});
            skLineSegment(sketch, "E2724", {"start": v(59.2, 14.53) * mm, "end": v(58.78, 14.75) * mm});
            skLineSegment(sketch, "E2725", {"start": v(58.78, 14.75) * mm, "end": v(58.36, 14.96) * mm});
            skLineSegment(sketch, "E2726", {"start": v(58.36, 14.96) * mm, "end": v(57.93, 15.15) * mm});
            skLineSegment(sketch, "E2727", {"start": v(57.93, 15.15) * mm, "end": v(57.5, 15.32) * mm});
            skLineSegment(sketch, "E2728", {"start": v(57.5, 15.32) * mm, "end": v(57.05, 15.47) * mm});
            skLineSegment(sketch, "E2729", {"start": v(57.05, 15.47) * mm, "end": v(56.6, 15.6) * mm});
            skLineSegment(sketch, "E2730", {"start": v(56.6, 15.6) * mm, "end": v(56.14, 15.72) * mm});
            skLineSegment(sketch, "E2731", {"start": v(56.14, 15.72) * mm, "end": v(55.67, 15.82) * mm});
            skLineSegment(sketch, "E2732", {"start": v(55.67, 15.82) * mm, "end": v(55.2, 15.9) * mm});
            skLineSegment(sketch, "E2733", {"start": v(55.2, 15.9) * mm, "end": v(54.73, 15.96) * mm});
            skLineSegment(sketch, "E2734", {"start": v(54.73, 15.96) * mm, "end": v(54.24, 16) * mm});
            skLineSegment(sketch, "E2735", {"start": v(54.24, 16) * mm, "end": v(53.75, 16.04) * mm});
            skLineSegment(sketch, "E2736", {"start": v(53.75, 16.04) * mm, "end": v(53.26, 16.04) * mm});
            skLineSegment(sketch, "E2737", {"start": v(53.26, 16.04) * mm, "end": v(39.5, 16.04) * mm});
            skLineSegment(sketch, "E2738", {"start": v(39.5, 16.04) * mm, "end": v(39.24, 16.03) * mm});
            skLineSegment(sketch, "E2739", {"start": v(39.24, 16.03) * mm, "end": v(38.98, 16) * mm});
            skLineSegment(sketch, "E2740", {"start": v(38.98, 16) * mm, "end": v(38.74, 15.93) * mm});
            skLineSegment(sketch, "E2741", {"start": v(38.74, 15.93) * mm, "end": v(38.5, 15.84) * mm});
            skLineSegment(sketch, "E2742", {"start": v(38.5, 15.84) * mm, "end": v(38.27, 15.73) * mm});
            skLineSegment(sketch, "E2743", {"start": v(38.27, 15.73) * mm, "end": v(38.06, 15.6) * mm});
            skLineSegment(sketch, "E2744", {"start": v(38.06, 15.6) * mm, "end": v(37.86, 15.45) * mm});
            skLineSegment(sketch, "E2745", {"start": v(37.86, 15.45) * mm, "end": v(37.67, 15.29) * mm});
            skLineSegment(sketch, "E2746", {"start": v(37.67, 15.29) * mm, "end": v(37.5, 15.1) * mm});
            skLineSegment(sketch, "E2747", {"start": v(37.5, 15.1) * mm, "end": v(37.36, 14.9) * mm});
            skLineSegment(sketch, "E2748", {"start": v(37.36, 14.9) * mm, "end": v(37.23, 14.69) * mm});
            skLineSegment(sketch, "E2749", {"start": v(37.23, 14.69) * mm, "end": v(37.12, 14.46) * mm});
            skLineSegment(sketch, "E2750", {"start": v(37.12, 14.46) * mm, "end": v(37.03, 14.22) * mm});
            skLineSegment(sketch, "E2751", {"start": v(37.03, 14.22) * mm, "end": v(36.97, 13.98) * mm});
            skLineSegment(sketch, "E2752", {"start": v(36.97, 13.98) * mm, "end": v(36.93, 13.72) * mm});
            skLineSegment(sketch, "E2753", {"start": v(36.93, 13.72) * mm, "end": v(36.91, 13.45) * mm});
            skLineSegment(sketch, "E2754", {"start": v(36.91, 13.45) * mm, "end": v(36.91, -22.53) * mm});
            skLineSegment(sketch, "E2755", {"start": v(36.91, -22.53) * mm, "end": v(36.91, -22.64) * mm});
            skLineSegment(sketch, "E2756", {"start": v(36.91, -22.64) * mm, "end": v(36.9, -22.74) * mm});
            skLineSegment(sketch, "E2757", {"start": v(36.9, -22.74) * mm, "end": v(36.88, -22.84) * mm});
            skLineSegment(sketch, "E2758", {"start": v(36.88, -22.84) * mm, "end": v(36.85, -22.93) * mm});
            skLineSegment(sketch, "E2759", {"start": v(36.85, -22.93) * mm, "end": v(36.82, -23.01) * mm});
            skLineSegment(sketch, "E2760", {"start": v(36.82, -23.01) * mm, "end": v(36.77, -23.09) * mm});
            skLineSegment(sketch, "E2761", {"start": v(36.77, -23.09) * mm, "end": v(36.72, -23.16) * mm});
            skLineSegment(sketch, "E2762", {"start": v(36.72, -23.16) * mm, "end": v(36.66, -23.22) * mm});
            skLineSegment(sketch, "E2763", {"start": v(36.66, -23.22) * mm, "end": v(36.6, -23.28) * mm});
            skLineSegment(sketch, "E2764", {"start": v(36.6, -23.28) * mm, "end": v(36.52, -23.33) * mm});
            skLineSegment(sketch, "E2765", {"start": v(36.52, -23.33) * mm, "end": v(36.44, -23.37) * mm});
            skLineSegment(sketch, "E2766", {"start": v(36.44, -23.37) * mm, "end": v(36.35, -23.4) * mm});
            skLineSegment(sketch, "E2767", {"start": v(36.35, -23.4) * mm, "end": v(36.25, -23.44) * mm});
            skLineSegment(sketch, "E2768", {"start": v(36.25, -23.44) * mm, "end": v(36.14, -23.46) * mm});
            skLineSegment(sketch, "E2769", {"start": v(36.14, -23.46) * mm, "end": v(36.03, -23.47) * mm});
            skLineSegment(sketch, "E2770", {"start": v(36.03, -23.47) * mm, "end": v(35.9, -23.48) * mm});
            skLineSegment(sketch, "E2771", {"start": v(35.9, -23.48) * mm, "end": v(33.5, -23.48) * mm});
            skLineSegment(sketch, "E2772", {"start": v(33.5, -23.48) * mm, "end": v(33.46, -23.48) * mm});
            skLineSegment(sketch, "E2773", {"start": v(33.46, -23.48) * mm, "end": v(33.43, -23.48) * mm});
            skLineSegment(sketch, "E2774", {"start": v(33.43, -23.48) * mm, "end": v(33.39, -23.47) * mm});
            skLineSegment(sketch, "E2775", {"start": v(33.39, -23.47) * mm, "end": v(33.35, -23.46) * mm});
            skLineSegment(sketch, "E2776", {"start": v(33.35, -23.46) * mm, "end": v(33.31, -23.45) * mm});
            skLineSegment(sketch, "E2777", {"start": v(33.31, -23.45) * mm, "end": v(33.28, -23.44) * mm});
            skLineSegment(sketch, "E2778", {"start": v(33.28, -23.44) * mm, "end": v(33.25, -23.42) * mm});
            skLineSegment(sketch, "E2779", {"start": v(33.25, -23.42) * mm, "end": v(33.21, -23.4) * mm});
            skLineSegment(sketch, "E2780", {"start": v(33.21, -23.4) * mm, "end": v(33.18, -23.38) * mm});
            skLineSegment(sketch, "E2781", {"start": v(33.18, -23.38) * mm, "end": v(33.15, -23.36) * mm});
            skLineSegment(sketch, "E2782", {"start": v(33.15, -23.36) * mm, "end": v(33.12, -23.33) * mm});
            skLineSegment(sketch, "E2783", {"start": v(33.12, -23.33) * mm, "end": v(33.1, -23.3) * mm});
            skLineSegment(sketch, "E2784", {"start": v(33.1, -23.3) * mm, "end": v(33.07, -23.28) * mm});
            skLineSegment(sketch, "E2785", {"start": v(33.07, -23.28) * mm, "end": v(33.05, -23.25) * mm});
            skLineSegment(sketch, "E2786", {"start": v(33.05, -23.25) * mm, "end": v(33.03, -23.21) * mm});
            skLineSegment(sketch, "E2787", {"start": v(33.03, -23.21) * mm, "end": v(33, -23.18) * mm});
            skLineSegment(sketch, "E2788", {"start": v(33, -23.18) * mm, "end": v(26.3, -9.7) * mm});
            skLineSegment(sketch, "E2789", {"start": v(26.3, -9.7) * mm, "end": v(26.23, -9.58) * mm});
            skLineSegment(sketch, "E2790", {"start": v(26.23, -9.58) * mm, "end": v(26.15, -9.46) * mm});
            skLineSegment(sketch, "E2791", {"start": v(26.15, -9.46) * mm, "end": v(26.07, -9.35) * mm});
            skLineSegment(sketch, "E2792", {"start": v(26.07, -9.35) * mm, "end": v(25.98, -9.25) * mm});
            skLineSegment(sketch, "E2793", {"start": v(25.98, -9.25) * mm, "end": v(25.9, -9.15) * mm});
            skLineSegment(sketch, "E2794", {"start": v(25.9, -9.15) * mm, "end": v(25.79, -9.06) * mm});
            skLineSegment(sketch, "E2795", {"start": v(25.79, -9.06) * mm, "end": v(25.68, -8.98) * mm});
            skLineSegment(sketch, "E2796", {"start": v(25.68, -8.98) * mm, "end": v(25.57, -8.9) * mm});
            skLineSegment(sketch, "E2797", {"start": v(25.57, -8.9) * mm, "end": v(25.46, -8.84) * mm});
            skLineSegment(sketch, "E2798", {"start": v(25.46, -8.84) * mm, "end": v(25.34, -8.78) * mm});
            skLineSegment(sketch, "E2799", {"start": v(25.34, -8.78) * mm, "end": v(25.21, -8.73) * mm});
            skLineSegment(sketch, "E2800", {"start": v(25.21, -8.73) * mm, "end": v(25.08, -8.7) * mm});
            skLineSegment(sketch, "E2801", {"start": v(25.08, -8.7) * mm, "end": v(24.95, -8.66) * mm});
            skLineSegment(sketch, "E2802", {"start": v(24.95, -8.66) * mm, "end": v(24.82, -8.63) * mm});
            skLineSegment(sketch, "E2803", {"start": v(24.82, -8.63) * mm, "end": v(24.68, -8.62) * mm});
            skLineSegment(sketch, "E2804", {"start": v(24.68, -8.62) * mm, "end": v(24.54, -8.61) * mm});
            skLineSegment(sketch, "E2805", {"start": v(24.54, -8.61) * mm, "end": v(9.92, -8.61) * mm});
            skLineSegment(sketch, "E2806", {"start": v(9.92, -8.61) * mm, "end": v(9.8, -8.61) * mm});
            skLineSegment(sketch, "E2807", {"start": v(9.8, -8.61) * mm, "end": v(9.68, -8.6) * mm});
            skLineSegment(sketch, "E2808", {"start": v(9.68, -8.6) * mm, "end": v(9.57, -8.58) * mm});
            skLineSegment(sketch, "E2809", {"start": v(9.57, -8.58) * mm, "end": v(9.47, -8.56) * mm});
            skLineSegment(sketch, "E2810", {"start": v(9.47, -8.56) * mm, "end": v(9.38, -8.52) * mm});
            skLineSegment(sketch, "E2811", {"start": v(9.38, -8.52) * mm, "end": v(9.3, -8.48) * mm});
            skLineSegment(sketch, "E2812", {"start": v(9.3, -8.48) * mm, "end": v(9.22, -8.43) * mm});
            skLineSegment(sketch, "E2813", {"start": v(9.22, -8.43) * mm, "end": v(9.16, -8.37) * mm});
            skLineSegment(sketch, "E2814", {"start": v(9.16, -8.37) * mm, "end": v(9.1, -8.3) * mm});
            skLineSegment(sketch, "E2815", {"start": v(9.1, -8.3) * mm, "end": v(9.05, -8.24) * mm});
            skLineSegment(sketch, "E2816", {"start": v(9.05, -8.24) * mm, "end": v(9, -8.16) * mm});
            skLineSegment(sketch, "E2817", {"start": v(9, -8.16) * mm, "end": v(8.97, -8.07) * mm});
            skLineSegment(sketch, "E2818", {"start": v(8.97, -8.07) * mm, "end": v(8.94, -7.97) * mm});
            skLineSegment(sketch, "E2819", {"start": v(8.94, -7.97) * mm, "end": v(8.93, -7.87) * mm});
            skLineSegment(sketch, "E2820", {"start": v(8.93, -7.87) * mm, "end": v(8.91, -7.75) * mm});
            skLineSegment(sketch, "E2821", {"start": v(8.91, -7.75) * mm, "end": v(8.91, -7.63) * mm});
            skLineSegment(sketch, "E2822", {"start": v(8.91, -7.63) * mm, "end": v(8.91, -7.52) * mm});
            skLineSegment(sketch, "E2823", {"start": v(8.91, -7.52) * mm, "end": v(8.93, -7.4) * mm});
            skLineSegment(sketch, "E2824", {"start": v(8.93, -7.4) * mm, "end": v(8.94, -7.3) * mm});
            skLineSegment(sketch, "E2825", {"start": v(8.94, -7.3) * mm, "end": v(8.97, -7.22) * mm});
            skLineSegment(sketch, "E2826", {"start": v(8.97, -7.22) * mm, "end": v(9, -7.13) * mm});
            skLineSegment(sketch, "E2827", {"start": v(9, -7.13) * mm, "end": v(9.05, -7.06) * mm});
            skLineSegment(sketch, "E2828", {"start": v(9.05, -7.06) * mm, "end": v(9.1, -6.99) * mm});
            skLineSegment(sketch, "E2829", {"start": v(9.1, -6.99) * mm, "end": v(9.16, -6.93) * mm});
            skLineSegment(sketch, "E2830", {"start": v(9.16, -6.93) * mm, "end": v(9.22, -6.87) * mm});
            skLineSegment(sketch, "E2831", {"start": v(9.22, -6.87) * mm, "end": v(9.3, -6.83) * mm});
            skLineSegment(sketch, "E2832", {"start": v(9.3, -6.83) * mm, "end": v(9.38, -6.79) * mm});
            skLineSegment(sketch, "E2833", {"start": v(9.38, -6.79) * mm, "end": v(9.47, -6.75) * mm});
            skLineSegment(sketch, "E2834", {"start": v(9.47, -6.75) * mm, "end": v(9.57, -6.73) * mm});
            skLineSegment(sketch, "E2835", {"start": v(9.57, -6.73) * mm, "end": v(9.68, -6.71) * mm});
            skLineSegment(sketch, "E2836", {"start": v(9.68, -6.71) * mm, "end": v(9.8, -6.7) * mm});
            skLineSegment(sketch, "E2837", {"start": v(9.8, -6.7) * mm, "end": v(9.92, -6.7) * mm});
            skLineSegment(sketch, "E2838", {"start": v(9.92, -6.7) * mm, "end": v(21.86, -6.7) * mm});
            skLineSegment(sketch, "E2839", {"start": v(21.86, -6.7) * mm, "end": v(21.98, -6.7) * mm});
            skLineSegment(sketch, "E2840", {"start": v(21.98, -6.7) * mm, "end": v(22.1, -6.68) * mm});
            skLineSegment(sketch, "E2841", {"start": v(22.1, -6.68) * mm, "end": v(22.2, -6.67) * mm});
            skLineSegment(sketch, "E2842", {"start": v(22.2, -6.67) * mm, "end": v(22.31, -6.64) * mm});
            skLineSegment(sketch, "E2843", {"start": v(22.31, -6.64) * mm, "end": v(22.42, -6.6) * mm});
            skLineSegment(sketch, "E2844", {"start": v(22.42, -6.6) * mm, "end": v(22.53, -6.57) * mm});
            skLineSegment(sketch, "E2845", {"start": v(22.53, -6.57) * mm, "end": v(22.63, -6.53) * mm});
            skLineSegment(sketch, "E2846", {"start": v(22.63, -6.53) * mm, "end": v(22.73, -6.47) * mm});
            skLineSegment(sketch, "E2847", {"start": v(22.73, -6.47) * mm, "end": v(22.83, -6.42) * mm});
            skLineSegment(sketch, "E2848", {"start": v(22.83, -6.42) * mm, "end": v(22.92, -6.35) * mm});
            skLineSegment(sketch, "E2849", {"start": v(22.92, -6.35) * mm, "end": v(23, -6.28) * mm});
            skLineSegment(sketch, "E2850", {"start": v(23, -6.28) * mm, "end": v(23.1, -6.2) * mm});
            skLineSegment(sketch, "E2851", {"start": v(23.1, -6.2) * mm, "end": v(23.17, -6.13) * mm});
            skLineSegment(sketch, "E2852", {"start": v(23.17, -6.13) * mm, "end": v(23.25, -6.04) * mm});
            skLineSegment(sketch, "E2853", {"start": v(23.25, -6.04) * mm, "end": v(23.32, -5.95) * mm});
            skLineSegment(sketch, "E2854", {"start": v(23.32, -5.95) * mm, "end": v(23.38, -5.85) * mm});
            skLineSegment(sketch, "E2855", {"start": v(23.38, -5.85) * mm, "end": v(23.44, -5.75) * mm});
            skLineSegment(sketch, "E2856", {"start": v(23.44, -5.75) * mm, "end": v(23.49, -5.65) * mm});
            skLineSegment(sketch, "E2857", {"start": v(23.49, -5.65) * mm, "end": v(23.53, -5.54) * mm});
            skLineSegment(sketch, "E2858", {"start": v(23.53, -5.54) * mm, "end": v(23.57, -5.44) * mm});
            skLineSegment(sketch, "E2859", {"start": v(23.57, -5.44) * mm, "end": v(23.6, -5.33) * mm});
            skLineSegment(sketch, "E2860", {"start": v(23.6, -5.33) * mm, "end": v(23.62, -5.22) * mm});
            skLineSegment(sketch, "E2861", {"start": v(23.62, -5.22) * mm, "end": v(23.64, -5.1) * mm});
            skLineSegment(sketch, "E2862", {"start": v(23.64, -5.1) * mm, "end": v(23.65, -5) * mm});
            skLineSegment(sketch, "E2863", {"start": v(23.65, -5) * mm, "end": v(23.65, -4.88) * mm});
            skLineSegment(sketch, "E2864", {"start": v(23.65, -4.88) * mm, "end": v(23.65, -4.77) * mm});
            skLineSegment(sketch, "E2865", {"start": v(23.65, -4.77) * mm, "end": v(23.63, -4.66) * mm});
            skLineSegment(sketch, "E2866", {"start": v(23.63, -4.66) * mm, "end": v(23.61, -4.55) * mm});
            skLineSegment(sketch, "E2867", {"start": v(23.61, -4.55) * mm, "end": v(23.59, -4.44) * mm});
            skLineSegment(sketch, "E2868", {"start": v(23.59, -4.44) * mm, "end": v(23.55, -4.33) * mm});
            skLineSegment(sketch, "E2869", {"start": v(23.55, -4.33) * mm, "end": v(23.51, -4.22) * mm});
            skLineSegment(sketch, "E2870", {"start": v(23.51, -4.22) * mm, "end": v(23.46, -4.12) * mm});
            skLineSegment(sketch, "E2871", {"start": v(23.46, -4.12) * mm, "end": v(13.73, 15.58) * mm});
            skLineSegment(sketch, "E2872", {"start": v(13.73, 15.58) * mm, "end": v(13.69, 15.66) * mm});
            skLineSegment(sketch, "E2873", {"start": v(13.69, 15.66) * mm, "end": v(13.64, 15.74) * mm});
            skLineSegment(sketch, "E2874", {"start": v(13.64, 15.74) * mm, "end": v(13.58, 15.81) * mm});
            skLineSegment(sketch, "E2875", {"start": v(13.58, 15.81) * mm, "end": v(13.52, 15.88) * mm});
            skLineSegment(sketch, "E2876", {"start": v(13.52, 15.88) * mm, "end": v(13.46, 15.95) * mm});
            skLineSegment(sketch, "E2877", {"start": v(13.46, 15.95) * mm, "end": v(13.4, 16) * mm});
            skLineSegment(sketch, "E2878", {"start": v(13.4, 16) * mm, "end": v(13.32, 16.06) * mm});
            skLineSegment(sketch, "E2879", {"start": v(13.32, 16.06) * mm, "end": v(13.25, 16.11) * mm});
            skLineSegment(sketch, "E2880", {"start": v(13.25, 16.11) * mm, "end": v(13.17, 16.16) * mm});
            skLineSegment(sketch, "E2881", {"start": v(13.17, 16.16) * mm, "end": v(13.1, 16.2) * mm});
            skLineSegment(sketch, "E2882", {"start": v(13.1, 16.2) * mm, "end": v(13, 16.23) * mm});
            skLineSegment(sketch, "E2883", {"start": v(13, 16.23) * mm, "end": v(12.92, 16.26) * mm});
            skLineSegment(sketch, "E2884", {"start": v(12.92, 16.26) * mm, "end": v(12.83, 16.28) * mm});
            skLineSegment(sketch, "E2885", {"start": v(12.83, 16.28) * mm, "end": v(12.74, 16.3) * mm});
            skLineSegment(sketch, "E2886", {"start": v(12.74, 16.3) * mm, "end": v(12.65, 16.3) * mm});
            skLineSegment(sketch, "E2887", {"start": v(12.65, 16.3) * mm, "end": v(12.56, 16.3) * mm});
            skLineSegment(sketch, "E2888", {"start": v(12.56, 16.3) * mm, "end": v(12.38, 16.3) * mm});
            skLineSegment(sketch, "E2889", {"start": v(12.38, 16.3) * mm, "end": v(12.29, 16.3) * mm});
            skLineSegment(sketch, "E2890", {"start": v(12.29, 16.3) * mm, "end": v(12.2, 16.3) * mm});
            skLineSegment(sketch, "E2891", {"start": v(12.2, 16.3) * mm, "end": v(12.12, 16.28) * mm});
            skLineSegment(sketch, "E2892", {"start": v(12.12, 16.28) * mm, "end": v(12.03, 16.26) * mm});
            skLineSegment(sketch, "E2893", {"start": v(12.03, 16.26) * mm, "end": v(11.95, 16.23) * mm});
            skLineSegment(sketch, "E2894", {"start": v(11.95, 16.23) * mm, "end": v(11.87, 16.2) * mm});
            skLineSegment(sketch, "E2895", {"start": v(11.87, 16.2) * mm, "end": v(11.8, 16.17) * mm});
            skLineSegment(sketch, "E2896", {"start": v(11.8, 16.17) * mm, "end": v(11.72, 16.12) * mm});
            skLineSegment(sketch, "E2897", {"start": v(11.72, 16.12) * mm, "end": v(11.65, 16.08) * mm});
            skLineSegment(sketch, "E2898", {"start": v(11.65, 16.08) * mm, "end": v(11.58, 16.03) * mm});
            skLineSegment(sketch, "E2899", {"start": v(11.58, 16.03) * mm, "end": v(11.52, 15.97) * mm});
            skLineSegment(sketch, "E2900", {"start": v(11.52, 15.97) * mm, "end": v(11.46, 15.9) * mm});
            skLineSegment(sketch, "E2901", {"start": v(11.46, 15.9) * mm, "end": v(11.4, 15.84) * mm});
            skLineSegment(sketch, "E2902", {"start": v(11.4, 15.84) * mm, "end": v(11.35, 15.77) * mm});
            skLineSegment(sketch, "E2903", {"start": v(11.35, 15.77) * mm, "end": v(11.3, 15.7) * mm});
            skLineSegment(sketch, "E2904", {"start": v(11.3, 15.7) * mm, "end": v(11.26, 15.62) * mm});
            skLineSegment(sketch, "E2905", {"start": v(11.26, 15.62) * mm, "end": v(-8.01, -22.72) * mm});
            skLineSegment(sketch, "E2906", {"start": v(-8.01, -22.72) * mm, "end": v(-8.06, -22.8) * mm});
            skLineSegment(sketch, "E2907", {"start": v(-8.06, -22.8) * mm, "end": v(-8.11, -22.89) * mm});
            skLineSegment(sketch, "E2908", {"start": v(-8.11, -22.89) * mm, "end": v(-8.17, -22.96) * mm});
            skLineSegment(sketch, "E2909", {"start": v(-8.17, -22.96) * mm, "end": v(-8.23, -23.04) * mm});
            skLineSegment(sketch, "E2910", {"start": v(-8.23, -23.04) * mm, "end": v(-8.3, -23.1) * mm});
            skLineSegment(sketch, "E2911", {"start": v(-8.3, -23.1) * mm, "end": v(-8.37, -23.17) * mm});
            skLineSegment(sketch, "E2912", {"start": v(-8.37, -23.17) * mm, "end": v(-8.44, -23.23) * mm});
            skLineSegment(sketch, "E2913", {"start": v(-8.44, -23.23) * mm, "end": v(-8.52, -23.28) * mm});
            skLineSegment(sketch, "E2914", {"start": v(-8.52, -23.28) * mm, "end": v(-8.6, -23.32) * mm});
            skLineSegment(sketch, "E2915", {"start": v(-8.6, -23.32) * mm, "end": v(-8.7, -23.37) * mm});
            skLineSegment(sketch, "E2916", {"start": v(-8.7, -23.37) * mm, "end": v(-8.78, -23.4) * mm});
            skLineSegment(sketch, "E2917", {"start": v(-8.78, -23.4) * mm, "end": v(-8.87, -23.43) * mm});
            skLineSegment(sketch, "E2918", {"start": v(-8.87, -23.43) * mm, "end": v(-8.96, -23.45) * mm});
            skLineSegment(sketch, "E2919", {"start": v(-8.96, -23.45) * mm, "end": v(-9.06, -23.47) * mm});
            skLineSegment(sketch, "E2920", {"start": v(-9.06, -23.47) * mm, "end": v(-9.16, -23.48) * mm});
            skLineSegment(sketch, "E2921", {"start": v(-9.16, -23.48) * mm, "end": v(-9.25, -23.48) * mm});
            skLineSegment(sketch, "E2922", {"start": v(-9.25, -23.48) * mm, "end": v(-11.94, -23.48) * mm});
            skLineSegment(sketch, "E2923", {"start": v(-11.94, -23.48) * mm, "end": v(-12.06, -23.48) * mm});
            skLineSegment(sketch, "E2924", {"start": v(-12.06, -23.48) * mm, "end": v(-12.17, -23.47) * mm});
            skLineSegment(sketch, "E2925", {"start": v(-12.17, -23.47) * mm, "end": v(-12.28, -23.46) * mm});
            skLineSegment(sketch, "E2926", {"start": v(-12.28, -23.46) * mm, "end": v(-12.4, -23.44) * mm});
            skLineSegment(sketch, "E2927", {"start": v(-12.4, -23.44) * mm, "end": v(-12.5, -23.42) * mm});
            skLineSegment(sketch, "E2928", {"start": v(-12.5, -23.42) * mm, "end": v(-12.61, -23.39) * mm});
            skLineSegment(sketch, "E2929", {"start": v(-12.61, -23.39) * mm, "end": v(-12.72, -23.35) * mm});
            skLineSegment(sketch, "E2930", {"start": v(-12.72, -23.35) * mm, "end": v(-12.82, -23.3) * mm});
            skLineSegment(sketch, "E2931", {"start": v(-12.82, -23.3) * mm, "end": v(-12.93, -23.26) * mm});
            skLineSegment(sketch, "E2932", {"start": v(-12.93, -23.26) * mm, "end": v(-13.03, -23.21) * mm});
            skLineSegment(sketch, "E2933", {"start": v(-13.03, -23.21) * mm, "end": v(-13.12, -23.16) * mm});
            skLineSegment(sketch, "E2934", {"start": v(-13.12, -23.16) * mm, "end": v(-13.22, -23.1) * mm});
            skLineSegment(sketch, "E2935", {"start": v(-13.22, -23.1) * mm, "end": v(-13.31, -23.03) * mm});
            skLineSegment(sketch, "E2936", {"start": v(-13.31, -23.03) * mm, "end": v(-13.4, -22.96) * mm});
            skLineSegment(sketch, "E2937", {"start": v(-13.4, -22.96) * mm, "end": v(-13.49, -22.89) * mm});
            skLineSegment(sketch, "E2938", {"start": v(-13.49, -22.89) * mm, "end": v(-13.57, -22.8) * mm});
            skLineSegment(sketch, "E2939", {"start": v(-13.57, -22.8) * mm, "end": v(-29.29, -7.1) * mm});
            skLineSegment(sketch, "E2940", {"start": v(-29.29, -7.1) * mm, "end": v(-29.3, -7.08) * mm});
            skLineSegment(sketch, "E2941", {"start": v(-29.3, -7.08) * mm, "end": v(-29.31, -7.06) * mm});
            skLineSegment(sketch, "E2942", {"start": v(-29.31, -7.06) * mm, "end": v(-29.33, -7.04) * mm});
            skLineSegment(sketch, "E2943", {"start": v(-29.33, -7.04) * mm, "end": v(-29.33, -7.03) * mm});
            skLineSegment(sketch, "E2944", {"start": v(-29.33, -7.03) * mm, "end": v(-29.34, -7.01) * mm});
            skLineSegment(sketch, "E2945", {"start": v(-29.34, -7.01) * mm, "end": v(-29.35, -7) * mm});
            skLineSegment(sketch, "E2946", {"start": v(-29.35, -7) * mm, "end": v(-29.35, -6.98) * mm});
            skLineSegment(sketch, "E2947", {"start": v(-29.35, -6.98) * mm, "end": v(-29.35, -6.96) * mm});
            skLineSegment(sketch, "E2948", {"start": v(-29.35, -6.96) * mm, "end": v(-29.36, -6.95) * mm});
            skLineSegment(sketch, "E2949", {"start": v(-29.36, -6.95) * mm, "end": v(-29.36, -6.93) * mm});
            skLineSegment(sketch, "E2950", {"start": v(-29.36, -6.93) * mm, "end": v(-29.36, -6.91) * mm});
            skLineSegment(sketch, "E2951", {"start": v(-29.36, -6.91) * mm, "end": v(-29.35, -6.9) * mm});
            skLineSegment(sketch, "E2952", {"start": v(-29.35, -6.9) * mm, "end": v(-29.35, -6.88) * mm});
            skLineSegment(sketch, "E2953", {"start": v(-29.35, -6.88) * mm, "end": v(-29.35, -6.87) * mm});
            skLineSegment(sketch, "E2954", {"start": v(-29.35, -6.87) * mm, "end": v(-29.34, -6.85) * mm});
            skLineSegment(sketch, "E2955", {"start": v(-29.34, -6.85) * mm, "end": v(-29.34, -6.84) * mm});
            skLineSegment(sketch, "E2956", {"start": v(-29.34, -6.84) * mm, "end": v(-29.33, -6.83) * mm});
            skLineSegment(sketch, "E2957", {"start": v(-29.33, -6.83) * mm, "end": v(-29.33, -6.81) * mm});
            skLineSegment(sketch, "E2958", {"start": v(-29.33, -6.81) * mm, "end": v(-29.32, -6.8) * mm});
            skLineSegment(sketch, "E2959", {"start": v(-29.32, -6.8) * mm, "end": v(-29.3, -6.79) * mm});
            skLineSegment(sketch, "E2960", {"start": v(-29.3, -6.79) * mm, "end": v(-29.3, -6.78) * mm});
            skLineSegment(sketch, "E2961", {"start": v(-29.3, -6.78) * mm, "end": v(-29.29, -6.77) * mm});
            skLineSegment(sketch, "E2962", {"start": v(-29.29, -6.77) * mm, "end": v(-29.28, -6.75) * mm});
            skLineSegment(sketch, "E2963", {"start": v(-29.28, -6.75) * mm, "end": v(-29.26, -6.74) * mm});
            skLineSegment(sketch, "E2964", {"start": v(-29.26, -6.74) * mm, "end": v(-29.25, -6.73) * mm});
            skLineSegment(sketch, "E2965", {"start": v(-29.25, -6.73) * mm, "end": v(-29.24, -6.72) * mm});
            skLineSegment(sketch, "E2966", {"start": v(-29.24, -6.72) * mm, "end": v(-29.22, -6.72) * mm});
            skLineSegment(sketch, "E2967", {"start": v(-29.22, -6.72) * mm, "end": v(-29.2, -6.71) * mm});
            skLineSegment(sketch, "E2968", {"start": v(-29.2, -6.71) * mm, "end": v(-29.18, -6.7) * mm});
            skLineSegment(sketch, "E2969", {"start": v(-29.18, -6.7) * mm, "end": v(-29.17, -6.7) * mm});
            skLineSegment(sketch, "E2970", {"start": v(-29.17, -6.7) * mm, "end": v(-29.15, -6.7) * mm});
            skLineSegment(sketch, "E2971", {"start": v(-29.15, -6.7) * mm, "end": v(-29.13, -6.7) * mm});
            skLineSegment(sketch, "E2972", {"start": v(-29.13, -6.7) * mm, "end": v(-23.36, -6.7) * mm});
            skLineSegment(sketch, "E2973", {"start": v(-23.36, -6.7) * mm, "end": v(-22.87, -6.69) * mm});
            skLineSegment(sketch, "E2974", {"start": v(-22.87, -6.69) * mm, "end": v(-22.38, -6.66) * mm});
            skLineSegment(sketch, "E2975", {"start": v(-22.38, -6.66) * mm, "end": v(-21.9, -6.62) * mm});
            skLineSegment(sketch, "E2976", {"start": v(-21.9, -6.62) * mm, "end": v(-21.42, -6.55) * mm});
            skLineSegment(sketch, "E2977", {"start": v(-21.42, -6.55) * mm, "end": v(-20.95, -6.47) * mm});
            skLineSegment(sketch, "E2978", {"start": v(-20.95, -6.47) * mm, "end": v(-20.48, -6.37) * mm});
            skLineSegment(sketch, "E2979", {"start": v(-20.48, -6.37) * mm, "end": v(-20.03, -6.26) * mm});
            skLineSegment(sketch, "E2980", {"start": v(-20.03, -6.26) * mm, "end": v(-19.58, -6.12) * mm});
            skLineSegment(sketch, "E2981", {"start": v(-19.58, -6.12) * mm, "end": v(-19.13, -5.97) * mm});
            skLineSegment(sketch, "E2982", {"start": v(-19.13, -5.97) * mm, "end": v(-18.7, -5.8) * mm});
            skLineSegment(sketch, "E2983", {"start": v(-18.7, -5.8) * mm, "end": v(-18.26, -5.61) * mm});
            skLineSegment(sketch, "E2984", {"start": v(-18.26, -5.61) * mm, "end": v(-17.84, -5.4) * mm});
            skLineSegment(sketch, "E2985", {"start": v(-17.84, -5.4) * mm, "end": v(-17.42, -5.18) * mm});
            skLineSegment(sketch, "E2986", {"start": v(-17.42, -5.18) * mm, "end": v(-17.01, -4.94) * mm});
            skLineSegment(sketch, "E2987", {"start": v(-17.01, -4.94) * mm, "end": v(-16.6, -4.68) * mm});
            skLineSegment(sketch, "E2988", {"start": v(-16.6, -4.68) * mm, "end": v(-16.21, -4.4) * mm});
            skLineSegment(sketch, "E2989", {"start": v(-16.21, -4.4) * mm, "end": v(-15.7, -4) * mm});
            skLineSegment(sketch, "E2990", {"start": v(-15.7, -4) * mm, "end": v(-15.23, -3.59) * mm});
            skLineSegment(sketch, "E2991", {"start": v(-15.23, -3.59) * mm, "end": v(-14.78, -3.14) * mm});
            skLineSegment(sketch, "E2992", {"start": v(-14.78, -3.14) * mm, "end": v(-14.37, -2.68) * mm});
            skLineSegment(sketch, "E2993", {"start": v(-14.37, -2.68) * mm, "end": v(-14, -2.19) * mm});
            skLineSegment(sketch, "E2994", {"start": v(-14, -2.19) * mm, "end": v(-13.65, -1.67) * mm});
            skLineSegment(sketch, "E2995", {"start": v(-13.65, -1.67) * mm, "end": v(-13.33, -1.14) * mm});
            skLineSegment(sketch, "E2996", {"start": v(-13.33, -1.14) * mm, "end": v(-13.05, -0.58) * mm});
            skLineSegment(sketch, "E2997", {"start": v(-13.05, -0.58) * mm, "end": v(-12.8, 0) * mm});
            skLineSegment(sketch, "E2998", {"start": v(-12.8, 0) * mm, "end": v(-12.59, 0.6) * mm});
            skLineSegment(sketch, "E2999", {"start": v(-12.59, 0.6) * mm, "end": v(-12.4, 1.22) * mm});
            skLineSegment(sketch, "E3000", {"start": v(-12.4, 1.22) * mm, "end": v(-12.26, 1.87) * mm});
            skLineSegment(sketch, "E3001", {"start": v(-12.26, 1.87) * mm, "end": v(-12.14, 2.54) * mm});
            skLineSegment(sketch, "E3002", {"start": v(-12.14, 2.54) * mm, "end": v(-12.06, 3.23) * mm});
            skLineSegment(sketch, "E3003", {"start": v(-12.06, 3.23) * mm, "end": v(-12, 3.94) * mm});
            skLineSegment(sketch, "E3004", {"start": v(-12, 3.94) * mm, "end": v(-12, 4.67) * mm});
            skLineSegment(sketch, "E3005", {"start": v(-12, 4.67) * mm, "end": v(-12, 5.4) * mm});
            skLineSegment(sketch, "E3006", {"start": v(-12, 5.4) * mm, "end": v(-12.06, 6.12) * mm});
            skLineSegment(sketch, "E3007", {"start": v(-12.06, 6.12) * mm, "end": v(-12.14, 6.8) * mm});
            skLineSegment(sketch, "E3008", {"start": v(-12.14, 6.8) * mm, "end": v(-12.26, 7.48) * mm});
            skLineSegment(sketch, "E3009", {"start": v(-12.26, 7.48) * mm, "end": v(-12.4, 8.12) * mm});
            skLineSegment(sketch, "E3010", {"start": v(-12.4, 8.12) * mm, "end": v(-12.59, 8.75) * mm});
            skLineSegment(sketch, "E3011", {"start": v(-12.59, 8.75) * mm, "end": v(-12.8, 9.35) * mm});
            skLineSegment(sketch, "E3012", {"start": v(-12.8, 9.35) * mm, "end": v(-13.05, 9.93) * mm});
            skLineSegment(sketch, "E3013", {"start": v(-13.05, 9.93) * mm, "end": v(-13.33, 10.48) * mm});
            skLineSegment(sketch, "E3014", {"start": v(-13.33, 10.48) * mm, "end": v(-13.65, 11.02) * mm});
            skLineSegment(sketch, "E3015", {"start": v(-13.65, 11.02) * mm, "end": v(-14, 11.53) * mm});
            skLineSegment(sketch, "E3016", {"start": v(-14, 11.53) * mm, "end": v(-14.37, 12.02) * mm});
            skLineSegment(sketch, "E3017", {"start": v(-14.37, 12.02) * mm, "end": v(-14.78, 12.49) * mm});
            skLineSegment(sketch, "E3018", {"start": v(-14.78, 12.49) * mm, "end": v(-15.23, 12.93) * mm});
            skLineSegment(sketch, "E3019", {"start": v(-15.23, 12.93) * mm, "end": v(-15.7, 13.35) * mm});
            skLineSegment(sketch, "E3020", {"start": v(-15.7, 13.35) * mm, "end": v(-16.21, 13.75) * mm});
            skLineSegment(sketch, "E3021", {"start": v(-16.21, 13.75) * mm, "end": v(-16.6, 14.03) * mm});
            skLineSegment(sketch, "E3022", {"start": v(-16.6, 14.03) * mm, "end": v(-17.01, 14.29) * mm});
            skLineSegment(sketch, "E3023", {"start": v(-17.01, 14.29) * mm, "end": v(-17.42, 14.53) * mm});
            skLineSegment(sketch, "E3024", {"start": v(-17.42, 14.53) * mm, "end": v(-17.84, 14.75) * mm});
            skLineSegment(sketch, "E3025", {"start": v(-17.84, 14.75) * mm, "end": v(-18.26, 14.96) * mm});
            skLineSegment(sketch, "E3026", {"start": v(-18.26, 14.96) * mm, "end": v(-18.7, 15.15) * mm});
            skLineSegment(sketch, "E3027", {"start": v(-18.7, 15.15) * mm, "end": v(-19.13, 15.32) * mm});
            skLineSegment(sketch, "E3028", {"start": v(-19.13, 15.32) * mm, "end": v(-19.58, 15.47) * mm});
            skLineSegment(sketch, "E3029", {"start": v(-19.58, 15.47) * mm, "end": v(-20.03, 15.6) * mm});
            skLineSegment(sketch, "E3030", {"start": v(-20.03, 15.6) * mm, "end": v(-20.48, 15.72) * mm});
            skLineSegment(sketch, "E3031", {"start": v(-20.48, 15.72) * mm, "end": v(-20.95, 15.82) * mm});
            skLineSegment(sketch, "E3032", {"start": v(-20.95, 15.82) * mm, "end": v(-21.42, 15.9) * mm});
            skLineSegment(sketch, "E3033", {"start": v(-21.42, 15.9) * mm, "end": v(-21.9, 15.96) * mm});
            skLineSegment(sketch, "E3034", {"start": v(-21.9, 15.96) * mm, "end": v(-22.38, 16) * mm});
            skLineSegment(sketch, "E3035", {"start": v(-22.38, 16) * mm, "end": v(-22.87, 16.04) * mm});
            skLineSegment(sketch, "E3036", {"start": v(-22.87, 16.04) * mm, "end": v(-23.36, 16.04) * mm});
            skLineSegment(sketch, "E3037", {"start": v(-23.36, 16.04) * mm, "end": v(-36.97, 16.04) * mm});
            skLineSegment(sketch, "E3038", {"start": v(-36.97, 16.04) * mm, "end": v(-37.25, 16.03) * mm});
            skLineSegment(sketch, "E3039", {"start": v(-37.25, 16.03) * mm, "end": v(-37.52, 15.99) * mm});
            skLineSegment(sketch, "E3040", {"start": v(-37.52, 15.99) * mm, "end": v(-37.78, 15.92) * mm});
            skLineSegment(sketch, "E3041", {"start": v(-37.78, 15.92) * mm, "end": v(-38.03, 15.83) * mm});
            skLineSegment(sketch, "E3042", {"start": v(-38.03, 15.83) * mm, "end": v(-38.27, 15.71) * mm});
            skLineSegment(sketch, "E3043", {"start": v(-38.27, 15.71) * mm, "end": v(-38.5, 15.58) * mm});
            skLineSegment(sketch, "E3044", {"start": v(-38.5, 15.58) * mm, "end": v(-38.7, 15.42) * mm});
            skLineSegment(sketch, "E3045", {"start": v(-38.7, 15.42) * mm, "end": v(-38.9, 15.24) * mm});
            skLineSegment(sketch, "E3046", {"start": v(-38.9, 15.24) * mm, "end": v(-39.08, 15.05) * mm});
            skLineSegment(sketch, "E3047", {"start": v(-39.08, 15.05) * mm, "end": v(-39.24, 14.84) * mm});
            skLineSegment(sketch, "E3048", {"start": v(-39.24, 14.84) * mm, "end": v(-39.38, 14.6) * mm});
            skLineSegment(sketch, "E3049", {"start": v(-39.38, 14.6) * mm, "end": v(-39.5, 14.37) * mm});
            skLineSegment(sketch, "E3050", {"start": v(-39.5, 14.37) * mm, "end": v(-39.58, 14.12) * mm});
            skLineSegment(sketch, "E3051", {"start": v(-39.58, 14.12) * mm, "end": v(-39.65, 13.86) * mm});
            skLineSegment(sketch, "E3052", {"start": v(-39.65, 13.86) * mm, "end": v(-39.7, 13.58) * mm});
            skLineSegment(sketch, "E3053", {"start": v(-39.7, 13.58) * mm, "end": v(-39.7, 13.3) * mm});
            skLineSegment(sketch, "E3054", {"start": v(-39.7, 13.3) * mm, "end": v(-39.7, -22.53) * mm});
            skLineSegment(sketch, "E3055", {"start": v(-39.7, -22.53) * mm, "end": v(-39.71, -22.64) * mm});
            skLineSegment(sketch, "E3056", {"start": v(-39.71, -22.64) * mm, "end": v(-39.72, -22.74) * mm});
            skLineSegment(sketch, "E3057", {"start": v(-39.72, -22.74) * mm, "end": v(-39.74, -22.84) * mm});
            skLineSegment(sketch, "E3058", {"start": v(-39.74, -22.84) * mm, "end": v(-39.77, -22.93) * mm});
            skLineSegment(sketch, "E3059", {"start": v(-39.77, -22.93) * mm, "end": v(-39.8, -23.01) * mm});
            skLineSegment(sketch, "E3060", {"start": v(-39.8, -23.01) * mm, "end": v(-39.85, -23.09) * mm});
            skLineSegment(sketch, "E3061", {"start": v(-39.85, -23.09) * mm, "end": v(-39.9, -23.16) * mm});
            skLineSegment(sketch, "E3062", {"start": v(-39.9, -23.16) * mm, "end": v(-39.96, -23.22) * mm});
            skLineSegment(sketch, "E3063", {"start": v(-39.96, -23.22) * mm, "end": v(-40.03, -23.28) * mm});
            skLineSegment(sketch, "E3064", {"start": v(-40.03, -23.28) * mm, "end": v(-40.1, -23.33) * mm});
            skLineSegment(sketch, "E3065", {"start": v(-40.1, -23.33) * mm, "end": v(-40.18, -23.37) * mm});
            skLineSegment(sketch, "E3066", {"start": v(-40.18, -23.37) * mm, "end": v(-40.27, -23.4) * mm});
            skLineSegment(sketch, "E3067", {"start": v(-40.27, -23.4) * mm, "end": v(-40.37, -23.44) * mm});
            skLineSegment(sketch, "E3068", {"start": v(-40.37, -23.44) * mm, "end": v(-40.48, -23.46) * mm});
            skLineSegment(sketch, "E3069", {"start": v(-40.48, -23.46) * mm, "end": v(-40.6, -23.47) * mm});
            skLineSegment(sketch, "E3070", {"start": v(-40.6, -23.47) * mm, "end": v(-40.72, -23.48) * mm});
            skLineSegment(sketch, "E3071", {"start": v(-40.72, -23.48) * mm, "end": v(-43.52, -23.48) * mm});
            skLineSegment(sketch, "E3072", {"start": v(-43.52, -23.48) * mm, "end": v(-43.62, -23.48) * mm});
            skLineSegment(sketch, "E3073", {"start": v(-43.62, -23.48) * mm, "end": v(-43.72, -23.46) * mm});
            skLineSegment(sketch, "E3074", {"start": v(-43.72, -23.46) * mm, "end": v(-43.82, -23.44) * mm});
            skLineSegment(sketch, "E3075", {"start": v(-43.82, -23.44) * mm, "end": v(-43.91, -23.4) * mm});
            skLineSegment(sketch, "E3076", {"start": v(-43.91, -23.4) * mm, "end": v(-44, -23.36) * mm});
            skLineSegment(sketch, "E3077", {"start": v(-44, -23.36) * mm, "end": v(-44.09, -23.31) * mm});
            skLineSegment(sketch, "E3078", {"start": v(-44.09, -23.31) * mm, "end": v(-44.16, -23.25) * mm});
            skLineSegment(sketch, "E3079", {"start": v(-44.16, -23.25) * mm, "end": v(-44.24, -23.19) * mm});
            skLineSegment(sketch, "E3080", {"start": v(-44.24, -23.19) * mm, "end": v(-44.3, -23.11) * mm});
            skLineSegment(sketch, "E3081", {"start": v(-44.3, -23.11) * mm, "end": v(-44.36, -23.04) * mm});
            skLineSegment(sketch, "E3082", {"start": v(-44.36, -23.04) * mm, "end": v(-44.41, -22.95) * mm});
            skLineSegment(sketch, "E3083", {"start": v(-44.41, -22.95) * mm, "end": v(-44.45, -22.86) * mm});
            skLineSegment(sketch, "E3084", {"start": v(-44.45, -22.86) * mm, "end": v(-44.49, -22.77) * mm});
            skLineSegment(sketch, "E3085", {"start": v(-44.49, -22.77) * mm, "end": v(-44.51, -22.67) * mm});
            skLineSegment(sketch, "E3086", {"start": v(-44.51, -22.67) * mm, "end": v(-44.53, -22.57) * mm});
            skLineSegment(sketch, "E3087", {"start": v(-44.53, -22.57) * mm, "end": v(-44.53, -22.47) * mm});
            skLineSegment(sketch, "E3088", {"start": v(-44.53, -22.47) * mm, "end": v(-44.53, 12.07) * mm});
            skLineSegment(sketch, "E3089", {"start": v(-44.53, 12.07) * mm, "end": v(-44.54, 12.3) * mm});
            skLineSegment(sketch, "E3090", {"start": v(-44.54, 12.3) * mm, "end": v(-44.55, 12.5) * mm});
            skLineSegment(sketch, "E3091", {"start": v(-44.55, 12.5) * mm, "end": v(-44.57, 12.72) * mm});
            skLineSegment(sketch, "E3092", {"start": v(-44.57, 12.72) * mm, "end": v(-44.6, 12.92) * mm});
            skLineSegment(sketch, "E3093", {"start": v(-44.6, 12.92) * mm, "end": v(-44.64, 13.12) * mm});
            skLineSegment(sketch, "E3094", {"start": v(-44.64, 13.12) * mm, "end": v(-44.69, 13.31) * mm});
            skLineSegment(sketch, "E3095", {"start": v(-44.69, 13.31) * mm, "end": v(-44.74, 13.5) * mm});
            skLineSegment(sketch, "E3096", {"start": v(-44.74, 13.5) * mm, "end": v(-44.8, 13.69) * mm});
            skLineSegment(sketch, "E3097", {"start": v(-44.8, 13.69) * mm, "end": v(-44.88, 13.86) * mm});
            skLineSegment(sketch, "E3098", {"start": v(-44.88, 13.86) * mm, "end": v(-44.96, 14.04) * mm});
            skLineSegment(sketch, "E3099", {"start": v(-44.96, 14.04) * mm, "end": v(-45.05, 14.2) * mm});
            skLineSegment(sketch, "E3100", {"start": v(-45.05, 14.2) * mm, "end": v(-45.14, 14.36) * mm});
            skLineSegment(sketch, "E3101", {"start": v(-45.14, 14.36) * mm, "end": v(-45.25, 14.52) * mm});
            skLineSegment(sketch, "E3102", {"start": v(-45.25, 14.52) * mm, "end": v(-45.36, 14.67) * mm});
            skLineSegment(sketch, "E3103", {"start": v(-45.36, 14.67) * mm, "end": v(-45.48, 14.81) * mm});
            skLineSegment(sketch, "E3104", {"start": v(-45.48, 14.81) * mm, "end": v(-45.61, 14.95) * mm});
            skLineSegment(sketch, "E3105", {"start": v(-45.61, 14.95) * mm, "end": v(-45.75, 15.08) * mm});
            skLineSegment(sketch, "E3106", {"start": v(-45.75, 15.08) * mm, "end": v(-45.9, 15.2) * mm});
            skLineSegment(sketch, "E3107", {"start": v(-45.9, 15.2) * mm, "end": v(-46.04, 15.32) * mm});
            skLineSegment(sketch, "E3108", {"start": v(-46.04, 15.32) * mm, "end": v(-46.2, 15.43) * mm});
            skLineSegment(sketch, "E3109", {"start": v(-46.2, 15.43) * mm, "end": v(-46.36, 15.53) * mm});
            skLineSegment(sketch, "E3110", {"start": v(-46.36, 15.53) * mm, "end": v(-46.52, 15.62) * mm});
            skLineSegment(sketch, "E3111", {"start": v(-46.52, 15.62) * mm, "end": v(-46.7, 15.7) * mm});
            skLineSegment(sketch, "E3112", {"start": v(-46.7, 15.7) * mm, "end": v(-46.87, 15.77) * mm});
            skLineSegment(sketch, "E3113", {"start": v(-46.87, 15.77) * mm, "end": v(-47.05, 15.83) * mm});
            skLineSegment(sketch, "E3114", {"start": v(-47.05, 15.83) * mm, "end": v(-47.24, 15.9) * mm});
            skLineSegment(sketch, "E3115", {"start": v(-47.24, 15.9) * mm, "end": v(-47.43, 15.94) * mm});
            skLineSegment(sketch, "E3116", {"start": v(-47.43, 15.94) * mm, "end": v(-47.63, 15.98) * mm});
            skLineSegment(sketch, "E3117", {"start": v(-47.63, 15.98) * mm, "end": v(-47.83, 16) * mm});
            skLineSegment(sketch, "E3118", {"start": v(-47.83, 16) * mm, "end": v(-48.04, 16.03) * mm});
            skLineSegment(sketch, "E3119", {"start": v(-48.04, 16.03) * mm, "end": v(-48.25, 16.04) * mm});
            skLineSegment(sketch, "E3120", {"start": v(-48.25, 16.04) * mm, "end": v(-48.47, 16.04) * mm});
            skLineSegment(sketch, "E3121", {"start": v(-48.47, 16.04) * mm, "end": v(-48.68, 16.04) * mm});
            skLineSegment(sketch, "E3122", {"start": v(-48.68, 16.04) * mm, "end": v(-48.9, 16.03) * mm});
            skLineSegment(sketch, "E3123", {"start": v(-48.9, 16.03) * mm, "end": v(-49.1, 16) * mm});
            skLineSegment(sketch, "E3124", {"start": v(-49.1, 16) * mm, "end": v(-49.3, 15.97) * mm});
            skLineSegment(sketch, "E3125", {"start": v(-49.3, 15.97) * mm, "end": v(-49.49, 15.93) * mm});
            skLineSegment(sketch, "E3126", {"start": v(-49.49, 15.93) * mm, "end": v(-49.68, 15.89) * mm});
            skLineSegment(sketch, "E3127", {"start": v(-49.68, 15.89) * mm, "end": v(-49.86, 15.83) * mm});
            skLineSegment(sketch, "E3128", {"start": v(-49.86, 15.83) * mm, "end": v(-50.04, 15.76) * mm});
            skLineSegment(sketch, "E3129", {"start": v(-50.04, 15.76) * mm, "end": v(-50.21, 15.69) * mm});
            skLineSegment(sketch, "E3130", {"start": v(-50.21, 15.69) * mm, "end": v(-50.38, 15.6) * mm});
            skLineSegment(sketch, "E3131", {"start": v(-50.38, 15.6) * mm, "end": v(-50.55, 15.51) * mm});
            skLineSegment(sketch, "E3132", {"start": v(-50.55, 15.51) * mm, "end": v(-50.7, 15.41) * mm});
            skLineSegment(sketch, "E3133", {"start": v(-50.7, 15.41) * mm, "end": v(-50.87, 15.3) * mm});
            skLineSegment(sketch, "E3134", {"start": v(-50.87, 15.3) * mm, "end": v(-51.02, 15.19) * mm});
            skLineSegment(sketch, "E3135", {"start": v(-51.02, 15.19) * mm, "end": v(-51.16, 15.06) * mm});
            skLineSegment(sketch, "E3136", {"start": v(-51.16, 15.06) * mm, "end": v(-51.3, 14.93) * mm});
            skLineSegment(sketch, "E3137", {"start": v(-51.3, 14.93) * mm, "end": v(-51.43, 14.79) * mm});
            skLineSegment(sketch, "E3138", {"start": v(-51.43, 14.79) * mm, "end": v(-51.56, 14.64) * mm});
            skLineSegment(sketch, "E3139", {"start": v(-51.56, 14.64) * mm, "end": v(-51.68, 14.49) * mm});
            skLineSegment(sketch, "E3140", {"start": v(-51.68, 14.49) * mm, "end": v(-51.78, 14.33) * mm});
            skLineSegment(sketch, "E3141", {"start": v(-51.78, 14.33) * mm, "end": v(-51.88, 14.17) * mm});
            skLineSegment(sketch, "E3142", {"start": v(-51.88, 14.17) * mm, "end": v(-51.97, 14) * mm});
            skLineSegment(sketch, "E3143", {"start": v(-51.97, 14) * mm, "end": v(-52.06, 13.83) * mm});
            skLineSegment(sketch, "E3144", {"start": v(-52.06, 13.83) * mm, "end": v(-52.13, 13.65) * mm});
            skLineSegment(sketch, "E3145", {"start": v(-52.13, 13.65) * mm, "end": v(-52.2, 13.47) * mm});
            skLineSegment(sketch, "E3146", {"start": v(-52.2, 13.47) * mm, "end": v(-52.25, 13.29) * mm});
            skLineSegment(sketch, "E3147", {"start": v(-52.25, 13.29) * mm, "end": v(-52.3, 13.1) * mm});
            skLineSegment(sketch, "E3148", {"start": v(-52.3, 13.1) * mm, "end": v(-52.34, 12.9) * mm});
            skLineSegment(sketch, "E3149", {"start": v(-52.34, 12.9) * mm, "end": v(-52.37, 12.7) * mm});
            skLineSegment(sketch, "E3150", {"start": v(-52.37, 12.7) * mm, "end": v(-52.39, 12.5) * mm});
            skLineSegment(sketch, "E3151", {"start": v(-52.39, 12.5) * mm, "end": v(-52.4, 12.28) * mm});
            skLineSegment(sketch, "E3152", {"start": v(-52.4, 12.28) * mm, "end": v(-52.4, 12.07) * mm});
            skLineSegment(sketch, "E3153", {"start": v(-52.4, 12.07) * mm, "end": v(-52.4, -17.98) * mm});
            skLineSegment(sketch, "E3154", {"start": v(-52.4, -17.98) * mm, "end": v(-52.4, -18) * mm});
            skLineSegment(sketch, "E3155", {"start": v(-52.4, -18) * mm, "end": v(-52.41, -18.02) * mm});
            skLineSegment(sketch, "E3156", {"start": v(-52.41, -18.02) * mm, "end": v(-52.42, -18.03) * mm});
            skLineSegment(sketch, "E3157", {"start": v(-52.42, -18.03) * mm, "end": v(-52.42, -18.05) * mm});
            skLineSegment(sketch, "E3158", {"start": v(-52.42, -18.05) * mm, "end": v(-52.43, -18.06) * mm});
            skLineSegment(sketch, "E3159", {"start": v(-52.43, -18.06) * mm, "end": v(-52.44, -18.08) * mm});
            skLineSegment(sketch, "E3160", {"start": v(-52.44, -18.08) * mm, "end": v(-52.45, -18.09) * mm});
            skLineSegment(sketch, "E3161", {"start": v(-52.45, -18.09) * mm, "end": v(-52.46, -18.1) * mm});
            skLineSegment(sketch, "E3162", {"start": v(-52.46, -18.1) * mm, "end": v(-52.47, -18.11) * mm});
            skLineSegment(sketch, "E3163", {"start": v(-52.47, -18.11) * mm, "end": v(-52.48, -18.12) * mm});
            skLineSegment(sketch, "E3164", {"start": v(-52.48, -18.12) * mm, "end": v(-52.5, -18.13) * mm});
            skLineSegment(sketch, "E3165", {"start": v(-52.5, -18.13) * mm, "end": v(-52.51, -18.13) * mm});
            skLineSegment(sketch, "E3166", {"start": v(-52.51, -18.13) * mm, "end": v(-52.53, -18.14) * mm});
            skLineSegment(sketch, "E3167", {"start": v(-52.53, -18.14) * mm, "end": v(-52.54, -18.14) * mm});
            skLineSegment(sketch, "E3168", {"start": v(-52.54, -18.14) * mm, "end": v(-52.56, -18.14) * mm});
            skLineSegment(sketch, "E3169", {"start": v(-52.56, -18.14) * mm, "end": v(-52.57, -18.14) * mm});
            skLineSegment(sketch, "E3170", {"start": v(-52.57, -18.14) * mm, "end": v(-52.58, -18.14) * mm});
            skLineSegment(sketch, "E3171", {"start": v(-52.58, -18.14) * mm, "end": v(-52.59, -18.14) * mm});
            skLineSegment(sketch, "E3172", {"start": v(-52.59, -18.14) * mm, "end": v(-52.6, -18.14) * mm});
            skLineSegment(sketch, "E3173", {"start": v(-52.6, -18.14) * mm, "end": v(-52.6, -18.14) * mm});
            skLineSegment(sketch, "E3174", {"start": v(-52.6, -18.14) * mm, "end": v(-52.61, -18.14) * mm});
            skLineSegment(sketch, "E3175", {"start": v(-52.61, -18.14) * mm, "end": v(-52.62, -18.13) * mm});
            skLineSegment(sketch, "E3176", {"start": v(-52.62, -18.13) * mm, "end": v(-52.63, -18.13) * mm});
            skLineSegment(sketch, "E3177", {"start": v(-52.63, -18.13) * mm, "end": v(-52.64, -18.13) * mm});
            skLineSegment(sketch, "E3178", {"start": v(-52.64, -18.13) * mm, "end": v(-52.65, -18.12) * mm});
            skLineSegment(sketch, "E3179", {"start": v(-52.65, -18.12) * mm, "end": v(-52.66, -18.12) * mm});
            skLineSegment(sketch, "E3180", {"start": v(-52.66, -18.12) * mm, "end": v(-52.67, -18.1) * mm});
            skLineSegment(sketch, "E3181", {"start": v(-52.67, -18.1) * mm, "end": v(-52.68, -18.1) * mm});
            skLineSegment(sketch, "E3182", {"start": v(-52.68, -18.1) * mm, "end": v(-52.69, -18.09) * mm});
            skLineSegment(sketch, "E3183", {"start": v(-52.69, -18.09) * mm, "end": v(-52.7, -18.08) * mm});
            skLineSegment(sketch, "E3184", {"start": v(-52.7, -18.08) * mm, "end": v(-52.7, -18.07) * mm});
            skLineSegment(sketch, "E3185", {"start": v(-52.7, -18.07) * mm, "end": v(-52.71, -18.05) * mm});
            skLineSegment(sketch, "E3186", {"start": v(-52.71, -18.05) * mm, "end": v(-69.4, 15.25) * mm});
            skLineSegment(sketch, "E3187", {"start": v(-69.4, 15.25) * mm, "end": v(-69.46, 15.34) * mm});
            skLineSegment(sketch, "E3188", {"start": v(-69.46, 15.34) * mm, "end": v(-69.51, 15.42) * mm});
            skLineSegment(sketch, "E3189", {"start": v(-69.51, 15.42) * mm, "end": v(-69.57, 15.5) * mm});
            skLineSegment(sketch, "E3190", {"start": v(-69.57, 15.5) * mm, "end": v(-69.64, 15.58) * mm});
            skLineSegment(sketch, "E3191", {"start": v(-69.64, 15.58) * mm, "end": v(-69.7, 15.65) * mm});
            skLineSegment(sketch, "E3192", {"start": v(-69.7, 15.65) * mm, "end": v(-69.78, 15.72) * mm});
            skLineSegment(sketch, "E3193", {"start": v(-69.78, 15.72) * mm, "end": v(-69.86, 15.78) * mm});
            skLineSegment(sketch, "E3194", {"start": v(-69.86, 15.78) * mm, "end": v(-69.94, 15.83) * mm});
            skLineSegment(sketch, "E3195", {"start": v(-69.94, 15.83) * mm, "end": v(-70.03, 15.88) * mm});
            skLineSegment(sketch, "E3196", {"start": v(-70.03, 15.88) * mm, "end": v(-70.11, 15.92) * mm});
            skLineSegment(sketch, "E3197", {"start": v(-70.11, 15.92) * mm, "end": v(-70.2, 15.96) * mm});
            skLineSegment(sketch, "E3198", {"start": v(-70.2, 15.96) * mm, "end": v(-70.3, 15.99) * mm});
            skLineSegment(sketch, "E3199", {"start": v(-70.3, 15.99) * mm, "end": v(-70.4, 16.01) * mm});
            skLineSegment(sketch, "E3200", {"start": v(-70.4, 16.01) * mm, "end": v(-70.5, 16.03) * mm});
            skLineSegment(sketch, "E3201", {"start": v(-70.5, 16.03) * mm, "end": v(-70.6, 16.04) * mm});
            skLineSegment(sketch, "E3202", {"start": v(-70.6, 16.04) * mm, "end": v(-70.7, 16.04) * mm});
            skLineSegment(sketch, "E3203", {"start": v(-70.7, 16.04) * mm, "end": v(-70.85, 16.04) * mm});
            skLineSegment(sketch, "E3204", {"start": v(-70.85, 16.04) * mm, "end": v(-71, 16.02) * mm});
            skLineSegment(sketch, "E3205", {"start": v(-71, 16.02) * mm, "end": v(-71.13, 15.98) * mm});
            skLineSegment(sketch, "E3206", {"start": v(-71.13, 15.98) * mm, "end": v(-71.26, 15.93) * mm});
            skLineSegment(sketch, "E3207", {"start": v(-71.26, 15.93) * mm, "end": v(-71.39, 15.87) * mm});
            skLineSegment(sketch, "E3208", {"start": v(-71.39, 15.87) * mm, "end": v(-71.5, 15.8) * mm});
            skLineSegment(sketch, "E3209", {"start": v(-71.5, 15.8) * mm, "end": v(-71.62, 15.71) * mm});
            skLineSegment(sketch, "E3210", {"start": v(-71.62, 15.71) * mm, "end": v(-71.72, 15.62) * mm});
            skLineSegment(sketch, "E3211", {"start": v(-71.72, 15.62) * mm, "end": v(-71.81, 15.52) * mm});
            skLineSegment(sketch, "E3212", {"start": v(-71.81, 15.52) * mm, "end": v(-71.9, 15.4) * mm});
            skLineSegment(sketch, "E3213", {"start": v(-71.9, 15.4) * mm, "end": v(-71.97, 15.29) * mm});
            skLineSegment(sketch, "E3214", {"start": v(-71.97, 15.29) * mm, "end": v(-72.03, 15.16) * mm});
            skLineSegment(sketch, "E3215", {"start": v(-72.03, 15.16) * mm, "end": v(-72.08, 15.03) * mm});
            skLineSegment(sketch, "E3216", {"start": v(-72.08, 15.03) * mm, "end": v(-72.12, 14.9) * mm});
            skLineSegment(sketch, "E3217", {"start": v(-72.12, 14.9) * mm, "end": v(-72.14, 14.75) * mm});
            skLineSegment(sketch, "E3218", {"start": v(-72.14, 14.75) * mm, "end": v(-72.15, 14.6) * mm});
            skLineSegment(sketch, "E3219", {"start": v(-72.15, 14.6) * mm, "end": v(-72.15, -22.83) * mm});
            skLineSegment(sketch, "E3220", {"start": v(-72.15, -22.83) * mm, "end": v(-72.15, -22.9) * mm});
            skLineSegment(sketch, "E3221", {"start": v(-72.15, -22.9) * mm, "end": v(-72.16, -22.96) * mm});
            skLineSegment(sketch, "E3222", {"start": v(-72.16, -22.96) * mm, "end": v(-72.17, -23.02) * mm});
            skLineSegment(sketch, "E3223", {"start": v(-72.17, -23.02) * mm, "end": v(-72.2, -23.08) * mm});
            skLineSegment(sketch, "E3224", {"start": v(-72.2, -23.08) * mm, "end": v(-72.22, -23.14) * mm});
            skLineSegment(sketch, "E3225", {"start": v(-72.22, -23.14) * mm, "end": v(-72.26, -23.2) * mm});
            skLineSegment(sketch, "E3226", {"start": v(-72.26, -23.2) * mm, "end": v(-72.3, -23.25) * mm});
            skLineSegment(sketch, "E3227", {"start": v(-72.3, -23.25) * mm, "end": v(-72.34, -23.3) * mm});
            skLineSegment(sketch, "E3228", {"start": v(-72.34, -23.3) * mm, "end": v(-72.38, -23.33) * mm});
            skLineSegment(sketch, "E3229", {"start": v(-72.38, -23.33) * mm, "end": v(-72.43, -23.37) * mm});
            skLineSegment(sketch, "E3230", {"start": v(-72.43, -23.37) * mm, "end": v(-72.49, -23.4) * mm});
            skLineSegment(sketch, "E3231", {"start": v(-72.49, -23.4) * mm, "end": v(-72.55, -23.43) * mm});
            skLineSegment(sketch, "E3232", {"start": v(-72.55, -23.43) * mm, "end": v(-72.6, -23.45) * mm});
            skLineSegment(sketch, "E3233", {"start": v(-72.6, -23.45) * mm, "end": v(-72.67, -23.47) * mm});
            skLineSegment(sketch, "E3234", {"start": v(-72.67, -23.47) * mm, "end": v(-72.73, -23.48) * mm});
            skLineSegment(sketch, "E3235", {"start": v(-72.73, -23.48) * mm, "end": v(-72.8, -23.48) * mm});
            skLineSegment(sketch, "E3236", {"start": v(-72.8, -23.48) * mm, "end": v(-91.32, -23.48) * mm});
            skLineSegment(sketch, "E3237", {"start": v(-91.32, -23.48) * mm, "end": v(-91.38, -23.48) * mm});
            skLineSegment(sketch, "E3238", {"start": v(-91.38, -23.48) * mm, "end": v(-91.44, -23.47) * mm});
            skLineSegment(sketch, "E3239", {"start": v(-91.44, -23.47) * mm, "end": v(-91.5, -23.46) * mm});
            skLineSegment(sketch, "E3240", {"start": v(-91.5, -23.46) * mm, "end": v(-91.55, -23.44) * mm});
            skLineSegment(sketch, "E3241", {"start": v(-91.55, -23.44) * mm, "end": v(-91.6, -23.42) * mm});
            skLineSegment(sketch, "E3242", {"start": v(-91.6, -23.42) * mm, "end": v(-91.64, -23.39) * mm});
            skLineSegment(sketch, "E3243", {"start": v(-91.64, -23.39) * mm, "end": v(-91.69, -23.35) * mm});
            skLineSegment(sketch, "E3244", {"start": v(-91.69, -23.35) * mm, "end": v(-91.73, -23.32) * mm});
            skLineSegment(sketch, "E3245", {"start": v(-91.73, -23.32) * mm, "end": v(-91.76, -23.28) * mm});
            skLineSegment(sketch, "E3246", {"start": v(-91.76, -23.28) * mm, "end": v(-91.8, -23.23) * mm});
            skLineSegment(sketch, "E3247", {"start": v(-91.8, -23.23) * mm, "end": v(-91.83, -23.18) * mm});
            skLineSegment(sketch, "E3248", {"start": v(-91.83, -23.18) * mm, "end": v(-91.85, -23.13) * mm});
            skLineSegment(sketch, "E3249", {"start": v(-91.85, -23.13) * mm, "end": v(-91.87, -23.08) * mm});
            skLineSegment(sketch, "E3250", {"start": v(-91.87, -23.08) * mm, "end": v(-91.88, -23.03) * mm});
            skLineSegment(sketch, "E3251", {"start": v(-91.88, -23.03) * mm, "end": v(-91.9, -22.97) * mm});
            skLineSegment(sketch, "E3252", {"start": v(-91.9, -22.97) * mm, "end": v(-91.9, -22.91) * mm});
            skLineSegment(sketch, "E3253", {"start": v(-91.9, -22.91) * mm, "end": v(-91.9, -21.25) * mm});
            skLineSegment(sketch, "E3254", {"start": v(-91.9, -21.25) * mm, "end": v(-91.9, -21.23) * mm});
            skLineSegment(sketch, "E3255", {"start": v(-91.9, -21.23) * mm, "end": v(-91.9, -21.21) * mm});
            skLineSegment(sketch, "E3256", {"start": v(-91.9, -21.21) * mm, "end": v(-91.89, -21.2) * mm});
            skLineSegment(sketch, "E3257", {"start": v(-91.89, -21.2) * mm, "end": v(-91.88, -21.18) * mm});
            skLineSegment(sketch, "E3258", {"start": v(-91.88, -21.18) * mm, "end": v(-91.87, -21.16) * mm});
            skLineSegment(sketch, "E3259", {"start": v(-91.87, -21.16) * mm, "end": v(-91.87, -21.14) * mm});
            skLineSegment(sketch, "E3260", {"start": v(-91.87, -21.14) * mm, "end": v(-91.86, -21.13) * mm});
            skLineSegment(sketch, "E3261", {"start": v(-91.86, -21.13) * mm, "end": v(-91.84, -21.11) * mm});
            skLineSegment(sketch, "E3262", {"start": v(-91.84, -21.11) * mm, "end": v(-91.83, -21.1) * mm});
            skLineSegment(sketch, "E3263", {"start": v(-91.83, -21.1) * mm, "end": v(-91.82, -21.09) * mm});
            skLineSegment(sketch, "E3264", {"start": v(-91.82, -21.09) * mm, "end": v(-91.8, -21.07) * mm});
            skLineSegment(sketch, "E3265", {"start": v(-91.8, -21.07) * mm, "end": v(-91.79, -21.06) * mm});
            skLineSegment(sketch, "E3266", {"start": v(-91.79, -21.06) * mm, "end": v(-91.77, -21.05) * mm});
            skLineSegment(sketch, "E3267", {"start": v(-91.77, -21.05) * mm, "end": v(-91.75, -21.04) * mm});
            skLineSegment(sketch, "E3268", {"start": v(-91.75, -21.04) * mm, "end": v(-91.73, -21.04) * mm});
            skLineSegment(sketch, "E3269", {"start": v(-91.73, -21.04) * mm, "end": v(-91.72, -21.03) * mm});
            skLineSegment(sketch, "E3270", {"start": v(-91.72, -21.03) * mm, "end": v(-90.93, -20.84) * mm});
            skLineSegment(sketch, "E3271", {"start": v(-90.93, -20.84) * mm, "end": v(-90.16, -20.62) * mm});
            skLineSegment(sketch, "E3272", {"start": v(-90.16, -20.62) * mm, "end": v(-89.41, -20.37) * mm});
            skLineSegment(sketch, "E3273", {"start": v(-89.41, -20.37) * mm, "end": v(-88.68, -20.09) * mm});
            skLineSegment(sketch, "E3274", {"start": v(-88.68, -20.09) * mm, "end": v(-87.96, -19.78) * mm});
            skLineSegment(sketch, "E3275", {"start": v(-87.96, -19.78) * mm, "end": v(-87.26, -19.44) * mm});
            skLineSegment(sketch, "E3276", {"start": v(-87.26, -19.44) * mm, "end": v(-86.57, -19.07) * mm});
            skLineSegment(sketch, "E3277", {"start": v(-86.57, -19.07) * mm, "end": v(-85.9, -18.68) * mm});
            skLineSegment(sketch, "E3278", {"start": v(-85.9, -18.68) * mm, "end": v(-85.25, -18.25) * mm});
            skLineSegment(sketch, "E3279", {"start": v(-85.25, -18.25) * mm, "end": v(-84.62, -17.8) * mm});
            skLineSegment(sketch, "E3280", {"start": v(-84.62, -17.8) * mm, "end": v(-84, -17.32) * mm});
            skLineSegment(sketch, "E3281", {"start": v(-84, -17.32) * mm, "end": v(-83.4, -16.81) * mm});
            skLineSegment(sketch, "E3282", {"start": v(-83.4, -16.81) * mm, "end": v(-82.83, -16.27) * mm});
            skLineSegment(sketch, "E3283", {"start": v(-82.83, -16.27) * mm, "end": v(-82.27, -15.7) * mm});
            skLineSegment(sketch, "E3284", {"start": v(-82.27, -15.7) * mm, "end": v(-81.73, -15.11) * mm});
            skLineSegment(sketch, "E3285", {"start": v(-81.73, -15.11) * mm, "end": v(-81.2, -14.5) * mm});
            skLineSegment(sketch, "E3286", {"start": v(-81.2, -14.5) * mm, "end": v(-80.7, -13.84) * mm});
            skLineSegment(sketch, "E3287", {"start": v(-80.7, -13.84) * mm, "end": v(-80.21, -13.17) * mm});
            skLineSegment(sketch, "E3288", {"start": v(-80.21, -13.17) * mm, "end": v(-79.77, -12.5) * mm});
            skLineSegment(sketch, "E3289", {"start": v(-79.77, -12.5) * mm, "end": v(-79.36, -11.8) * mm});
            skLineSegment(sketch, "E3290", {"start": v(-79.36, -11.8) * mm, "end": v(-78.98, -11.1) * mm});
            skLineSegment(sketch, "E3291", {"start": v(-78.98, -11.1) * mm, "end": v(-78.63, -10.38) * mm});
            skLineSegment(sketch, "E3292", {"start": v(-78.63, -10.38) * mm, "end": v(-78.32, -9.66) * mm});
            skLineSegment(sketch, "E3293", {"start": v(-78.32, -9.66) * mm, "end": v(-78.03, -8.92) * mm});
            skLineSegment(sketch, "E3294", {"start": v(-78.03, -8.92) * mm, "end": v(-77.79, -8.17) * mm});
            skLineSegment(sketch, "E3295", {"start": v(-77.79, -8.17) * mm, "end": v(-77.57, -7.41) * mm});
            skLineSegment(sketch, "E3296", {"start": v(-77.57, -7.41) * mm, "end": v(-77.39, -6.64) * mm});
            skLineSegment(sketch, "E3297", {"start": v(-77.39, -6.64) * mm, "end": v(-77.24, -5.86) * mm});
            skLineSegment(sketch, "E3298", {"start": v(-77.24, -5.86) * mm, "end": v(-77.12, -5.07) * mm});
            skLineSegment(sketch, "E3299", {"start": v(-77.12, -5.07) * mm, "end": v(-77.04, -4.26) * mm});
            skLineSegment(sketch, "E3300", {"start": v(-77.04, -4.26) * mm, "end": v(-76.99, -3.45) * mm});
            skLineSegment(sketch, "E3301", {"start": v(-76.99, -3.45) * mm, "end": v(-76.97, -2.63) * mm});
            skLineSegment(sketch, "E3302", {"start": v(-76.97, -2.63) * mm, "end": v(-77, -1.65) * mm});
            skLineSegment(sketch, "E3303", {"start": v(-77, -1.65) * mm, "end": v(-77.06, -0.7) * mm});
            skLineSegment(sketch, "E3304", {"start": v(-77.06, -0.7) * mm, "end": v(-77.17, 0.25) * mm});
            skLineSegment(sketch, "E3305", {"start": v(-77.17, 0.25) * mm, "end": v(-77.32, 1.17) * mm});
            skLineSegment(sketch, "E3306", {"start": v(-77.32, 1.17) * mm, "end": v(-77.51, 2.08) * mm});
            skLineSegment(sketch, "E3307", {"start": v(-77.51, 2.08) * mm, "end": v(-77.75, 2.97) * mm});
            skLineSegment(sketch, "E3308", {"start": v(-77.75, 2.97) * mm, "end": v(-78.03, 3.84) * mm});
            skLineSegment(sketch, "E3309", {"start": v(-78.03, 3.84) * mm, "end": v(-78.35, 4.69) * mm});
            skLineSegment(sketch, "E3310", {"start": v(-78.35, 4.69) * mm, "end": v(-78.72, 5.52) * mm});
            skLineSegment(sketch, "E3311", {"start": v(-78.72, 5.52) * mm, "end": v(-79.13, 6.33) * mm});
            skLineSegment(sketch, "E3312", {"start": v(-79.13, 6.33) * mm, "end": v(-79.58, 7.13) * mm});
            skLineSegment(sketch, "E3313", {"start": v(-79.58, 7.13) * mm, "end": v(-80.08, 7.9) * mm});
            skLineSegment(sketch, "E3314", {"start": v(-80.08, 7.9) * mm, "end": v(-80.61, 8.66) * mm});
            skLineSegment(sketch, "E3315", {"start": v(-80.61, 8.66) * mm, "end": v(-81.2, 9.4) * mm});
            skLineSegment(sketch, "E3316", {"start": v(-81.2, 9.4) * mm, "end": v(-81.81, 10.1) * mm});
            skLineSegment(sketch, "E3317", {"start": v(-81.81, 10.1) * mm, "end": v(-82.48, 10.8) * mm});
            skLineSegment(sketch, "E3318", {"start": v(-82.48, 10.8) * mm, "end": v(-83.17, 11.47) * mm});
            skLineSegment(sketch, "E3319", {"start": v(-83.17, 11.47) * mm, "end": v(-83.89, 12.09) * mm});
            skLineSegment(sketch, "E3320", {"start": v(-83.89, 12.09) * mm, "end": v(-84.62, 12.67) * mm});
            skLineSegment(sketch, "E3321", {"start": v(-84.62, 12.67) * mm, "end": v(-85.38, 13.2) * mm});
            skLineSegment(sketch, "E3322", {"start": v(-85.38, 13.2) * mm, "end": v(-86.15, 13.7) * mm});
            skLineSegment(sketch, "E3323", {"start": v(-86.15, 13.7) * mm, "end": v(-86.95, 14.15) * mm});
            skLineSegment(sketch, "E3324", {"start": v(-86.95, 14.15) * mm, "end": v(-87.76, 14.56) * mm});
            skLineSegment(sketch, "E3325", {"start": v(-87.76, 14.56) * mm, "end": v(-88.6, 14.93) * mm});
            skLineSegment(sketch, "E3326", {"start": v(-88.6, 14.93) * mm, "end": v(-89.44, 15.25) * mm});
            skLineSegment(sketch, "E3327", {"start": v(-89.44, 15.25) * mm, "end": v(-90.31, 15.53) * mm});
            skLineSegment(sketch, "E3328", {"start": v(-90.31, 15.53) * mm, "end": v(-91.2, 15.77) * mm});
            skLineSegment(sketch, "E3329", {"start": v(-91.2, 15.77) * mm, "end": v(-92.1, 15.96) * mm});
            skLineSegment(sketch, "E3330", {"start": v(-92.1, 15.96) * mm, "end": v(-93.03, 16.11) * mm});
            skLineSegment(sketch, "E3331", {"start": v(-93.03, 16.11) * mm, "end": v(-93.97, 16.22) * mm});
            skLineSegment(sketch, "E3332", {"start": v(-93.97, 16.22) * mm, "end": v(-94.93, 16.29) * mm});
            skLineSegment(sketch, "E3333", {"start": v(-94.93, 16.29) * mm, "end": v(-95.91, 16.3) * mm});
            skLineSegment(sketch, "E3334", {"start": v(-95.91, 16.3) * mm, "end": v(-96.88, 16.29) * mm});
            skLineSegment(sketch, "E3335", {"start": v(-96.88, 16.29) * mm, "end": v(-97.84, 16.22) * mm});
            skLineSegment(sketch, "E3336", {"start": v(-97.84, 16.22) * mm, "end": v(-98.77, 16.11) * mm});
            skLineSegment(sketch, "E3337", {"start": v(-98.77, 16.11) * mm, "end": v(-99.7, 15.96) * mm});
            skLineSegment(sketch, "E3338", {"start": v(-99.7, 15.96) * mm, "end": v(-100.6, 15.77) * mm});
            skLineSegment(sketch, "E3339", {"start": v(-100.6, 15.77) * mm, "end": v(-101.48, 15.53) * mm});
            skLineSegment(sketch, "E3340", {"start": v(-101.48, 15.53) * mm, "end": v(-102.34, 15.25) * mm});
            skLineSegment(sketch, "E3341", {"start": v(-102.34, 15.25) * mm, "end": v(-103.19, 14.93) * mm});
            skLineSegment(sketch, "E3342", {"start": v(-103.19, 14.93) * mm, "end": v(-104.02, 14.56) * mm});
            skLineSegment(sketch, "E3343", {"start": v(-104.02, 14.56) * mm, "end": v(-104.83, 14.15) * mm});
            skLineSegment(sketch, "E3344", {"start": v(-104.83, 14.15) * mm, "end": v(-105.62, 13.7) * mm});
            skLineSegment(sketch, "E3345", {"start": v(-105.62, 13.7) * mm, "end": v(-106.4, 13.2) * mm});
            skLineSegment(sketch, "E3346", {"start": v(-106.4, 13.2) * mm, "end": v(-107.15, 12.67) * mm});
            skLineSegment(sketch, "E3347", {"start": v(-107.15, 12.67) * mm, "end": v(-107.88, 12.09) * mm});
            skLineSegment(sketch, "E3348", {"start": v(-107.88, 12.09) * mm, "end": v(-108.6, 11.47) * mm});
            skLineSegment(sketch, "E3349", {"start": v(-108.6, 11.47) * mm, "end": v(-109.29, 10.8) * mm});
            skLineSegment(sketch, "E3350", {"start": v(-109.29, 10.8) * mm, "end": v(-109.95, 10.1) * mm});
            skLineSegment(sketch, "E3351", {"start": v(-109.95, 10.1) * mm, "end": v(-110.58, 9.4) * mm});
            skLineSegment(sketch, "E3352", {"start": v(-110.58, 9.4) * mm, "end": v(-111.15, 8.66) * mm});
            skLineSegment(sketch, "E3353", {"start": v(-111.15, 8.66) * mm, "end": v(-111.7, 7.9) * mm});
            skLineSegment(sketch, "E3354", {"start": v(-111.7, 7.9) * mm, "end": v(-112.19, 7.13) * mm});
            skLineSegment(sketch, "E3355", {"start": v(-112.19, 7.13) * mm, "end": v(-112.64, 6.33) * mm});
            skLineSegment(sketch, "E3356", {"start": v(-112.64, 6.33) * mm, "end": v(-113.05, 5.52) * mm});
            skLineSegment(sketch, "E3357", {"start": v(-113.05, 5.52) * mm, "end": v(-113.41, 4.69) * mm});
            skLineSegment(sketch, "E3358", {"start": v(-113.41, 4.69) * mm, "end": v(-113.74, 3.84) * mm});
            skLineSegment(sketch, "E3359", {"start": v(-113.74, 3.84) * mm, "end": v(-114.02, 2.97) * mm});
            skLineSegment(sketch, "E3360", {"start": v(-114.02, 2.97) * mm, "end": v(-114.25, 2.08) * mm});
            skLineSegment(sketch, "E3361", {"start": v(-114.25, 2.08) * mm, "end": v(-114.45, 1.17) * mm});
            skLineSegment(sketch, "E3362", {"start": v(-114.45, 1.17) * mm, "end": v(-114.6, 0.25) * mm});
            skLineSegment(sketch, "E3363", {"start": v(-114.6, 0.25) * mm, "end": v(-114.7, -0.7) * mm});
            skLineSegment(sketch, "E3364", {"start": v(-114.7, -0.7) * mm, "end": v(-114.77, -1.65) * mm});
            skLineSegment(sketch, "E3365", {"start": v(-114.77, -1.65) * mm, "end": v(-114.8, -2.63) * mm});
            skLineSegment(sketch, "E3366", {"start": v(-114.8, -2.63) * mm, "end": v(-114.78, -3.45) * mm});
            skLineSegment(sketch, "E3367", {"start": v(-114.78, -3.45) * mm, "end": v(-114.73, -4.26) * mm});
            skLineSegment(sketch, "E3368", {"start": v(-114.73, -4.26) * mm, "end": v(-114.65, -5.07) * mm});
            skLineSegment(sketch, "E3369", {"start": v(-114.65, -5.07) * mm, "end": v(-114.53, -5.86) * mm});
            skLineSegment(sketch, "E3370", {"start": v(-114.53, -5.86) * mm, "end": v(-114.38, -6.64) * mm});
            skLineSegment(sketch, "E3371", {"start": v(-114.38, -6.64) * mm, "end": v(-114.2, -7.41) * mm});
            skLineSegment(sketch, "E3372", {"start": v(-114.2, -7.41) * mm, "end": v(-113.98, -8.17) * mm});
            skLineSegment(sketch, "E3373", {"start": v(-113.98, -8.17) * mm, "end": v(-113.73, -8.92) * mm});
            skLineSegment(sketch, "E3374", {"start": v(-113.73, -8.92) * mm, "end": v(-113.45, -9.66) * mm});
            skLineSegment(sketch, "E3375", {"start": v(-113.45, -9.66) * mm, "end": v(-113.14, -10.38) * mm});
            skLineSegment(sketch, "E3376", {"start": v(-113.14, -10.38) * mm, "end": v(-112.8, -11.1) * mm});
            skLineSegment(sketch, "E3377", {"start": v(-112.8, -11.1) * mm, "end": v(-112.41, -11.8) * mm});
            skLineSegment(sketch, "E3378", {"start": v(-112.41, -11.8) * mm, "end": v(-112, -12.5) * mm});
            skLineSegment(sketch, "E3379", {"start": v(-112, -12.5) * mm, "end": v(-111.55, -13.17) * mm});
            skLineSegment(sketch, "E3380", {"start": v(-111.55, -13.17) * mm, "end": v(-111.08, -13.84) * mm});
            skLineSegment(sketch, "E3381", {"start": v(-111.08, -13.84) * mm, "end": v(-110.57, -14.5) * mm});
            skLineSegment(sketch, "E3382", {"start": v(-110.57, -14.5) * mm, "end": v(-110.04, -15.11) * mm});
            skLineSegment(sketch, "E3383", {"start": v(-110.04, -15.11) * mm, "end": v(-109.5, -15.7) * mm});
            skLineSegment(sketch, "E3384", {"start": v(-109.5, -15.7) * mm, "end": v(-108.94, -16.27) * mm});
            skLineSegment(sketch, "E3385", {"start": v(-108.94, -16.27) * mm, "end": v(-108.36, -16.81) * mm});
            skLineSegment(sketch, "E3386", {"start": v(-108.36, -16.81) * mm, "end": v(-107.76, -17.32) * mm});
            skLineSegment(sketch, "E3387", {"start": v(-107.76, -17.32) * mm, "end": v(-107.15, -17.8) * mm});
            skLineSegment(sketch, "E3388", {"start": v(-107.15, -17.8) * mm, "end": v(-106.51, -18.25) * mm});
            skLineSegment(sketch, "E3389", {"start": v(-106.51, -18.25) * mm, "end": v(-105.86, -18.68) * mm});
            skLineSegment(sketch, "E3390", {"start": v(-105.86, -18.68) * mm, "end": v(-105.2, -19.07) * mm});
            skLineSegment(sketch, "E3391", {"start": v(-105.2, -19.07) * mm, "end": v(-104.51, -19.44) * mm});
            skLineSegment(sketch, "E3392", {"start": v(-104.51, -19.44) * mm, "end": v(-103.81, -19.78) * mm});
            skLineSegment(sketch, "E3393", {"start": v(-103.81, -19.78) * mm, "end": v(-103.1, -20.09) * mm});
            skLineSegment(sketch, "E3394", {"start": v(-103.1, -20.09) * mm, "end": v(-102.36, -20.37) * mm});
            skLineSegment(sketch, "E3395", {"start": v(-102.36, -20.37) * mm, "end": v(-101.6, -20.62) * mm});
            skLineSegment(sketch, "E3396", {"start": v(-101.6, -20.62) * mm, "end": v(-100.84, -20.84) * mm});
            skLineSegment(sketch, "E3397", {"start": v(-100.84, -20.84) * mm, "end": v(-100.05, -21.03) * mm});
            skLineSegment(sketch, "E3398", {"start": v(-100.05, -21.03) * mm, "end": v(-100.03, -21.04) * mm});
            skLineSegment(sketch, "E3399", {"start": v(-100.03, -21.04) * mm, "end": v(-100.01, -21.04) * mm});
            skLineSegment(sketch, "E3400", {"start": v(-100.01, -21.04) * mm, "end": v(-100, -21.05) * mm});
            skLineSegment(sketch, "E3401", {"start": v(-100, -21.05) * mm, "end": v(-99.98, -21.06) * mm});
            skLineSegment(sketch, "E3402", {"start": v(-99.98, -21.06) * mm, "end": v(-99.96, -21.07) * mm});
            skLineSegment(sketch, "E3403", {"start": v(-99.96, -21.07) * mm, "end": v(-99.95, -21.09) * mm});
            skLineSegment(sketch, "E3404", {"start": v(-99.95, -21.09) * mm, "end": v(-99.94, -21.1) * mm});
            skLineSegment(sketch, "E3405", {"start": v(-99.94, -21.1) * mm, "end": v(-99.92, -21.11) * mm});
            skLineSegment(sketch, "E3406", {"start": v(-99.92, -21.11) * mm, "end": v(-99.91, -21.13) * mm});
            skLineSegment(sketch, "E3407", {"start": v(-99.91, -21.13) * mm, "end": v(-99.9, -21.14) * mm});
            skLineSegment(sketch, "E3408", {"start": v(-99.9, -21.14) * mm, "end": v(-99.9, -21.16) * mm});
            skLineSegment(sketch, "E3409", {"start": v(-99.9, -21.16) * mm, "end": v(-99.89, -21.18) * mm});
            skLineSegment(sketch, "E3410", {"start": v(-99.89, -21.18) * mm, "end": v(-99.88, -21.2) * mm});
            skLineSegment(sketch, "E3411", {"start": v(-99.88, -21.2) * mm, "end": v(-99.88, -21.21) * mm});
            skLineSegment(sketch, "E3412", {"start": v(-99.88, -21.21) * mm, "end": v(-99.87, -21.23) * mm});
            skLineSegment(sketch, "E3413", {"start": v(-99.87, -21.23) * mm, "end": v(-99.87, -21.25) * mm});
            skLineSegment(sketch, "E3414", {"start": v(-99.87, -21.25) * mm, "end": v(-99.87, -22.91) * mm});
            skLineSegment(sketch, "E3415", {"start": v(-99.87, -22.91) * mm, "end": v(-99.88, -22.97) * mm});
            skLineSegment(sketch, "E3416", {"start": v(-99.88, -22.97) * mm, "end": v(-99.89, -23.03) * mm});
            skLineSegment(sketch, "E3417", {"start": v(-99.89, -23.03) * mm, "end": v(-99.9, -23.08) * mm});
            skLineSegment(sketch, "E3418", {"start": v(-99.9, -23.08) * mm, "end": v(-99.92, -23.13) * mm});
            skLineSegment(sketch, "E3419", {"start": v(-99.92, -23.13) * mm, "end": v(-99.94, -23.18) * mm});
            skLineSegment(sketch, "E3420", {"start": v(-99.94, -23.18) * mm, "end": v(-99.97, -23.23) * mm});
            skLineSegment(sketch, "E3421", {"start": v(-99.97, -23.23) * mm, "end": v(-100, -23.28) * mm});
            skLineSegment(sketch, "E3422", {"start": v(-100, -23.28) * mm, "end": v(-100.04, -23.32) * mm});
            skLineSegment(sketch, "E3423", {"start": v(-100.04, -23.32) * mm, "end": v(-100.08, -23.35) * mm});
            skLineSegment(sketch, "E3424", {"start": v(-100.08, -23.35) * mm, "end": v(-100.13, -23.39) * mm});
            skLineSegment(sketch, "E3425", {"start": v(-100.13, -23.39) * mm, "end": v(-100.17, -23.42) * mm});
            skLineSegment(sketch, "E3426", {"start": v(-100.17, -23.42) * mm, "end": v(-100.22, -23.44) * mm});
            skLineSegment(sketch, "E3427", {"start": v(-100.22, -23.44) * mm, "end": v(-100.28, -23.46) * mm});
            skLineSegment(sketch, "E3428", {"start": v(-100.28, -23.46) * mm, "end": v(-100.33, -23.47) * mm});
            skLineSegment(sketch, "E3429", {"start": v(-100.33, -23.47) * mm, "end": v(-100.39, -23.48) * mm});
            skLineSegment(sketch, "E3430", {"start": v(-100.39, -23.48) * mm, "end": v(-100.44, -23.48) * mm});
            skLineSegment(sketch, "E3431", {"start": v(-100.44, -23.48) * mm, "end": v(-140.73, -23.48) * mm});
            skLineSegment(sketch, "E3432", {"start": v(-140.73, -23.48) * mm, "end": v(-140.86, -23.48) * mm});
            skLineSegment(sketch, "E3433", {"start": v(-140.86, -23.48) * mm, "end": v(-140.97, -23.47) * mm});
            skLineSegment(sketch, "E3434", {"start": v(-140.97, -23.47) * mm, "end": v(-141.08, -23.45) * mm});
            skLineSegment(sketch, "E3435", {"start": v(-141.08, -23.45) * mm, "end": v(-141.18, -23.43) * mm});
            skLineSegment(sketch, "E3436", {"start": v(-141.18, -23.43) * mm, "end": v(-141.27, -23.4) * mm});
            skLineSegment(sketch, "E3437", {"start": v(-141.27, -23.4) * mm, "end": v(-141.35, -23.35) * mm});
            skLineSegment(sketch, "E3438", {"start": v(-141.35, -23.35) * mm, "end": v(-141.43, -23.3) * mm});
            skLineSegment(sketch, "E3439", {"start": v(-141.43, -23.3) * mm, "end": v(-141.5, -23.25) * mm});
            skLineSegment(sketch, "E3440", {"start": v(-141.5, -23.25) * mm, "end": v(-141.55, -23.19) * mm});
            skLineSegment(sketch, "E3441", {"start": v(-141.55, -23.19) * mm, "end": v(-141.6, -23.12) * mm});
            skLineSegment(sketch, "E3442", {"start": v(-141.6, -23.12) * mm, "end": v(-141.65, -23.04) * mm});
            skLineSegment(sketch, "E3443", {"start": v(-141.65, -23.04) * mm, "end": v(-141.68, -22.95) * mm});
            skLineSegment(sketch, "E3444", {"start": v(-141.68, -22.95) * mm, "end": v(-141.7, -22.86) * mm});
            skLineSegment(sketch, "E3445", {"start": v(-141.7, -22.86) * mm, "end": v(-141.73, -22.75) * mm});
            skLineSegment(sketch, "E3446", {"start": v(-141.73, -22.75) * mm, "end": v(-141.74, -22.64) * mm});
            skLineSegment(sketch, "E3447", {"start": v(-141.74, -22.64) * mm, "end": v(-141.74, -22.53) * mm});
            skLineSegment(sketch, "E3448", {"start": v(-141.74, -22.53) * mm, "end": v(-141.74, -22.4) * mm});
            skLineSegment(sketch, "E3449", {"start": v(-141.74, -22.4) * mm, "end": v(-141.73, -22.3) * mm});
            skLineSegment(sketch, "E3450", {"start": v(-141.73, -22.3) * mm, "end": v(-141.7, -22.2) * mm});
            skLineSegment(sketch, "E3451", {"start": v(-141.7, -22.2) * mm, "end": v(-141.68, -22.1) * mm});
            skLineSegment(sketch, "E3452", {"start": v(-141.68, -22.1) * mm, "end": v(-141.65, -22.01) * mm});
            skLineSegment(sketch, "E3453", {"start": v(-141.65, -22.01) * mm, "end": v(-141.6, -21.94) * mm});
            skLineSegment(sketch, "E3454", {"start": v(-141.6, -21.94) * mm, "end": v(-141.55, -21.86) * mm});
            skLineSegment(sketch, "E3455", {"start": v(-141.55, -21.86) * mm, "end": v(-141.5, -21.8) * mm});
            skLineSegment(sketch, "E3456", {"start": v(-141.5, -21.8) * mm, "end": v(-141.43, -21.75) * mm});
            skLineSegment(sketch, "E3457", {"start": v(-141.43, -21.75) * mm, "end": v(-141.35, -21.7) * mm});
            skLineSegment(sketch, "E3458", {"start": v(-141.35, -21.7) * mm, "end": v(-141.27, -21.66) * mm});
            skLineSegment(sketch, "E3459", {"start": v(-141.27, -21.66) * mm, "end": v(-141.18, -21.63) * mm});
            skLineSegment(sketch, "E3460", {"start": v(-141.18, -21.63) * mm, "end": v(-141.08, -21.6) * mm});
            skLineSegment(sketch, "E3461", {"start": v(-141.08, -21.6) * mm, "end": v(-140.97, -21.58) * mm});
            skLineSegment(sketch, "E3462", {"start": v(-140.97, -21.58) * mm, "end": v(-140.86, -21.57) * mm});
            skLineSegment(sketch, "E3463", {"start": v(-140.86, -21.57) * mm, "end": v(-140.73, -21.57) * mm});
            skLineSegment(sketch, "E3464", {"start": v(-140.73, -21.57) * mm, "end": v(-123.48, -21.57) * mm});
            skLineSegment(sketch, "E3465", {"start": v(-123.48, -21.57) * mm, "end": v(-123.27, -21.56) * mm});
            skLineSegment(sketch, "E3466", {"start": v(-123.27, -21.56) * mm, "end": v(-123.07, -21.55) * mm});
            skLineSegment(sketch, "E3467", {"start": v(-123.07, -21.55) * mm, "end": v(-122.87, -21.53) * mm});
            skLineSegment(sketch, "E3468", {"start": v(-122.87, -21.53) * mm, "end": v(-122.67, -21.5) * mm});
            skLineSegment(sketch, "E3469", {"start": v(-122.67, -21.5) * mm, "end": v(-122.48, -21.46) * mm});
            skLineSegment(sketch, "E3470", {"start": v(-122.48, -21.46) * mm, "end": v(-122.3, -21.4) * mm});
            skLineSegment(sketch, "E3471", {"start": v(-122.3, -21.4) * mm, "end": v(-122.1, -21.35) * mm});
            skLineSegment(sketch, "E3472", {"start": v(-122.1, -21.35) * mm, "end": v(-121.93, -21.28) * mm});
            skLineSegment(sketch, "E3473", {"start": v(-121.93, -21.28) * mm, "end": v(-121.75, -21.2) * mm});
            skLineSegment(sketch, "E3474", {"start": v(-121.75, -21.2) * mm, "end": v(-121.58, -21.12) * mm});
            skLineSegment(sketch, "E3475", {"start": v(-121.58, -21.12) * mm, "end": v(-121.41, -21.03) * mm});
            skLineSegment(sketch, "E3476", {"start": v(-121.41, -21.03) * mm, "end": v(-121.25, -20.92) * mm});
            skLineSegment(sketch, "E3477", {"start": v(-121.25, -20.92) * mm, "end": v(-121.09, -20.81) * mm});
            skLineSegment(sketch, "E3478", {"start": v(-121.09, -20.81) * mm, "end": v(-120.93, -20.7) * mm});
            skLineSegment(sketch, "E3479", {"start": v(-120.93, -20.7) * mm, "end": v(-120.78, -20.57) * mm});
            skLineSegment(sketch, "E3480", {"start": v(-120.78, -20.57) * mm, "end": v(-120.63, -20.43) * mm});
            skLineSegment(sketch, "E3481", {"start": v(-120.63, -20.43) * mm, "end": v(-120.5, -20.28) * mm});
            skLineSegment(sketch, "E3482", {"start": v(-120.5, -20.28) * mm, "end": v(-120.36, -20.13) * mm});
            skLineSegment(sketch, "E3483", {"start": v(-120.36, -20.13) * mm, "end": v(-120.24, -19.98) * mm});
            skLineSegment(sketch, "E3484", {"start": v(-120.24, -19.98) * mm, "end": v(-120.12, -19.82) * mm});
            skLineSegment(sketch, "E3485", {"start": v(-120.12, -19.82) * mm, "end": v(-120.02, -19.66) * mm});
            skLineSegment(sketch, "E3486", {"start": v(-120.02, -19.66) * mm, "end": v(-119.92, -19.5) * mm});
            skLineSegment(sketch, "E3487", {"start": v(-119.92, -19.5) * mm, "end": v(-119.84, -19.33) * mm});
            skLineSegment(sketch, "E3488", {"start": v(-119.84, -19.33) * mm, "end": v(-119.76, -19.15) * mm});
            skLineSegment(sketch, "E3489", {"start": v(-119.76, -19.15) * mm, "end": v(-119.69, -18.97) * mm});
            skLineSegment(sketch, "E3490", {"start": v(-119.69, -18.97) * mm, "end": v(-119.63, -18.79) * mm});
            skLineSegment(sketch, "E3491", {"start": v(-119.63, -18.79) * mm, "end": v(-119.58, -18.6) * mm});
            skLineSegment(sketch, "E3492", {"start": v(-119.58, -18.6) * mm, "end": v(-119.54, -18.4) * mm});
            skLineSegment(sketch, "E3493", {"start": v(-119.54, -18.4) * mm, "end": v(-119.5, -18.21) * mm});
            skLineSegment(sketch, "E3494", {"start": v(-119.5, -18.21) * mm, "end": v(-119.48, -18.02) * mm});
            skLineSegment(sketch, "E3495", {"start": v(-119.48, -18.02) * mm, "end": v(-119.47, -17.81) * mm});
            skLineSegment(sketch, "E3496", {"start": v(-119.47, -17.81) * mm, "end": v(-119.46, -17.6) * mm});
            skLineSegment(sketch, "E3497", {"start": v(-119.46, -17.6) * mm, "end": v(-119.47, -17.4) * mm});
            skLineSegment(sketch, "E3498", {"start": v(-119.47, -17.4) * mm, "end": v(-119.48, -17.18) * mm});
            skLineSegment(sketch, "E3499", {"start": v(-119.48, -17.18) * mm, "end": v(-119.5, -16.98) * mm});
            skLineSegment(sketch, "E3500", {"start": v(-119.5, -16.98) * mm, "end": v(-119.54, -16.78) * mm});
            skLineSegment(sketch, "E3501", {"start": v(-119.54, -16.78) * mm, "end": v(-119.58, -16.58) * mm});
            skLineSegment(sketch, "E3502", {"start": v(-119.58, -16.58) * mm, "end": v(-119.63, -16.39) * mm});
            skLineSegment(sketch, "E3503", {"start": v(-119.63, -16.39) * mm, "end": v(-119.68, -16.2) * mm});
            skLineSegment(sketch, "E3504", {"start": v(-119.68, -16.2) * mm, "end": v(-119.75, -16.02) * mm});
            skLineSegment(sketch, "E3505", {"start": v(-119.75, -16.02) * mm, "end": v(-119.83, -15.84) * mm});
            skLineSegment(sketch, "E3506", {"start": v(-119.83, -15.84) * mm, "end": v(-119.91, -15.67) * mm});
            skLineSegment(sketch, "E3507", {"start": v(-119.91, -15.67) * mm, "end": v(-120, -15.5) * mm});
            skLineSegment(sketch, "E3508", {"start": v(-120, -15.5) * mm, "end": v(-120.1, -15.34) * mm});
            skLineSegment(sketch, "E3509", {"start": v(-120.1, -15.34) * mm, "end": v(-120.22, -15.18) * mm});
            skLineSegment(sketch, "E3510", {"start": v(-120.22, -15.18) * mm, "end": v(-120.34, -15.02) * mm});
            skLineSegment(sketch, "E3511", {"start": v(-120.34, -15.02) * mm, "end": v(-120.47, -14.87) * mm});
            skLineSegment(sketch, "E3512", {"start": v(-120.47, -14.87) * mm, "end": v(-120.6, -14.73) * mm});
            skLineSegment(sketch, "E3513", {"start": v(-120.6, -14.73) * mm, "end": v(-120.75, -14.6) * mm});
            skLineSegment(sketch, "E3514", {"start": v(-120.75, -14.6) * mm, "end": v(-120.9, -14.46) * mm});
            skLineSegment(sketch, "E3515", {"start": v(-120.9, -14.46) * mm, "end": v(-121.05, -14.34) * mm});
            skLineSegment(sketch, "E3516", {"start": v(-121.05, -14.34) * mm, "end": v(-121.21, -14.23) * mm});
            skLineSegment(sketch, "E3517", {"start": v(-121.21, -14.23) * mm, "end": v(-121.37, -14.13) * mm});
            skLineSegment(sketch, "E3518", {"start": v(-121.37, -14.13) * mm, "end": v(-121.54, -14.04) * mm});
            skLineSegment(sketch, "E3519", {"start": v(-121.54, -14.04) * mm, "end": v(-121.72, -13.95) * mm});
            skLineSegment(sketch, "E3520", {"start": v(-121.72, -13.95) * mm, "end": v(-121.9, -13.88) * mm});
            skLineSegment(sketch, "E3521", {"start": v(-121.9, -13.88) * mm, "end": v(-122.08, -13.8) * mm});
            skLineSegment(sketch, "E3522", {"start": v(-122.08, -13.8) * mm, "end": v(-122.26, -13.75) * mm});
            skLineSegment(sketch, "E3523", {"start": v(-122.26, -13.75) * mm, "end": v(-122.46, -13.7) * mm});
            skLineSegment(sketch, "E3524", {"start": v(-122.46, -13.7) * mm, "end": v(-122.65, -13.66) * mm});
            skLineSegment(sketch, "E3525", {"start": v(-122.65, -13.66) * mm, "end": v(-122.85, -13.63) * mm});
            skLineSegment(sketch, "E3526", {"start": v(-122.85, -13.63) * mm, "end": v(-123.06, -13.6) * mm});
            skLineSegment(sketch, "E3527", {"start": v(-123.06, -13.6) * mm, "end": v(-123.27, -13.6) * mm});
            skLineSegment(sketch, "E3528", {"start": v(-123.27, -13.6) * mm, "end": v(-123.48, -13.59) * mm});
            skLineSegment(sketch, "E3529", {"start": v(-123.48, -13.59) * mm, "end": v(-138.61, -13.59) * mm});
            skLineSegment(sketch, "E3530", {"start": v(-138.61, -13.59) * mm, "end": v(-138.9, -13.58) * mm});
            skLineSegment(sketch, "E3531", {"start": v(-138.9, -13.58) * mm, "end": v(-139.18, -13.54) * mm});
            skLineSegment(sketch, "E3532", {"start": v(-139.18, -13.54) * mm, "end": v(-139.46, -13.47) * mm});
            skLineSegment(sketch, "E3533", {"start": v(-139.46, -13.47) * mm, "end": v(-139.72, -13.38) * mm});
            skLineSegment(sketch, "E3534", {"start": v(-139.72, -13.38) * mm, "end": v(-139.97, -13.27) * mm});
            skLineSegment(sketch, "E3535", {"start": v(-139.97, -13.27) * mm, "end": v(-140.22, -13.14) * mm});
            skLineSegment(sketch, "E3536", {"start": v(-140.22, -13.14) * mm, "end": v(-140.44, -13) * mm});
            skLineSegment(sketch, "E3537", {"start": v(-140.44, -13) * mm, "end": v(-140.66, -12.82) * mm});
            skLineSegment(sketch, "E3538", {"start": v(-140.66, -12.82) * mm, "end": v(-140.86, -12.63) * mm});
            skLineSegment(sketch, "E3539", {"start": v(-140.86, -12.63) * mm, "end": v(-141.04, -12.43) * mm});
            skLineSegment(sketch, "E3540", {"start": v(-141.04, -12.43) * mm, "end": v(-141.2, -12.2) * mm});
            skLineSegment(sketch, "E3541", {"start": v(-141.2, -12.2) * mm, "end": v(-141.34, -11.97) * mm});
            skLineSegment(sketch, "E3542", {"start": v(-141.34, -11.97) * mm, "end": v(-141.46, -11.72) * mm});
            skLineSegment(sketch, "E3543", {"start": v(-141.46, -11.72) * mm, "end": v(-141.56, -11.46) * mm});
            skLineSegment(sketch, "E3544", {"start": v(-141.56, -11.46) * mm, "end": v(-141.64, -11.19) * mm});
            skLineSegment(sketch, "E3545", {"start": v(-141.64, -11.19) * mm, "end": v(-141.69, -10.9) * mm});
            skLineSegment(sketch, "E3546", {"start": v(-141.69, -10.9) * mm, "end": v(-141.72, -10.65) * mm});
            skLineSegment(sketch, "E3547", {"start": v(-141.72, -10.65) * mm, "end": v(-141.74, -10.4) * mm});
            skLineSegment(sketch, "E3548", {"start": v(-141.74, -10.4) * mm, "end": v(-141.74, -10.16) * mm});
            skLineSegment(sketch, "E3549", {"start": v(-141.74, -10.16) * mm, "end": v(-141.74, -9.92) * mm});
            skLineSegment(sketch, "E3550", {"start": v(-141.74, -9.92) * mm, "end": v(-141.72, -9.7) * mm});
            skLineSegment(sketch, "E3551", {"start": v(-141.72, -9.7) * mm, "end": v(-141.7, -9.47) * mm});
            skLineSegment(sketch, "E3552", {"start": v(-141.7, -9.47) * mm, "end": v(-141.65, -9.26) * mm});
            skLineSegment(sketch, "E3553", {"start": v(-141.65, -9.26) * mm, "end": v(-141.6, -9.05) * mm});
            skLineSegment(sketch, "E3554", {"start": v(-141.6, -9.05) * mm, "end": v(-141.54, -8.85) * mm});
            skLineSegment(sketch, "E3555", {"start": v(-141.54, -8.85) * mm, "end": v(-141.47, -8.65) * mm});
            skLineSegment(sketch, "E3556", {"start": v(-141.47, -8.65) * mm, "end": v(-141.38, -8.47) * mm});
            skLineSegment(sketch, "E3557", {"start": v(-141.38, -8.47) * mm, "end": v(-141.29, -8.29) * mm});
            skLineSegment(sketch, "E3558", {"start": v(-141.29, -8.29) * mm, "end": v(-141.18, -8.12) * mm});
            skLineSegment(sketch, "E3559", {"start": v(-141.18, -8.12) * mm, "end": v(-141.06, -7.95) * mm});
            skLineSegment(sketch, "E3560", {"start": v(-141.06, -7.95) * mm, "end": v(-140.93, -7.8) * mm});
            skLineSegment(sketch, "E3561", {"start": v(-140.93, -7.8) * mm, "end": v(-140.8, -7.65) * mm});
            skLineSegment(sketch, "E3562", {"start": v(-140.8, -7.65) * mm, "end": v(-140.67, -7.53) * mm});
            skLineSegment(sketch, "E3563", {"start": v(-140.67, -7.53) * mm, "end": v(-140.55, -7.43) * mm});
            skLineSegment(sketch, "E3564", {"start": v(-140.55, -7.43) * mm, "end": v(-140.42, -7.33) * mm});
            skLineSegment(sketch, "E3565", {"start": v(-140.42, -7.33) * mm, "end": v(-140.28, -7.23) * mm});
            skLineSegment(sketch, "E3566", {"start": v(-140.28, -7.23) * mm, "end": v(-140.14, -7.15) * mm});
            skLineSegment(sketch, "E3567", {"start": v(-140.14, -7.15) * mm, "end": v(-140, -7.07) * mm});
            skLineSegment(sketch, "E3568", {"start": v(-140, -7.07) * mm, "end": v(-139.85, -7) * mm});
            skLineSegment(sketch, "E3569", {"start": v(-139.85, -7) * mm, "end": v(-139.7, -6.94) * mm});
            skLineSegment(sketch, "E3570", {"start": v(-139.7, -6.94) * mm, "end": v(-139.53, -6.88) * mm});
            skLineSegment(sketch, "E3571", {"start": v(-139.53, -6.88) * mm, "end": v(-139.37, -6.83) * mm});
            skLineSegment(sketch, "E3572", {"start": v(-139.37, -6.83) * mm, "end": v(-139.2, -6.8) * mm});
            skLineSegment(sketch, "E3573", {"start": v(-139.2, -6.8) * mm, "end": v(-139.03, -6.76) * mm});
            skLineSegment(sketch, "E3574", {"start": v(-139.03, -6.76) * mm, "end": v(-138.85, -6.73) * mm});
            skLineSegment(sketch, "E3575", {"start": v(-138.85, -6.73) * mm, "end": v(-138.67, -6.71) * mm});
            skLineSegment(sketch, "E3576", {"start": v(-138.67, -6.71) * mm, "end": v(-138.49, -6.7) * mm});
            skLineSegment(sketch, "E3577", {"start": v(-138.49, -6.7) * mm, "end": v(-138.3, -6.7) * mm});
            skLineSegment(sketch, "E3578", {"start": v(-138.3, -6.7) * mm, "end": v(-128.4, -6.7) * mm});
            skLineSegment(sketch, "E3579", {"start": v(-128.4, -6.7) * mm, "end": v(-128.18, -6.7) * mm});
            skLineSegment(sketch, "E3580", {"start": v(-128.18, -6.7) * mm, "end": v(-127.97, -6.68) * mm});
            skLineSegment(sketch, "E3581", {"start": v(-127.97, -6.68) * mm, "end": v(-127.76, -6.66) * mm});
            skLineSegment(sketch, "E3582", {"start": v(-127.76, -6.66) * mm, "end": v(-127.55, -6.63) * mm});
            skLineSegment(sketch, "E3583", {"start": v(-127.55, -6.63) * mm, "end": v(-127.35, -6.6) * mm});
            skLineSegment(sketch, "E3584", {"start": v(-127.35, -6.6) * mm, "end": v(-127.16, -6.54) * mm});
            skLineSegment(sketch, "E3585", {"start": v(-127.16, -6.54) * mm, "end": v(-126.97, -6.49) * mm});
            skLineSegment(sketch, "E3586", {"start": v(-126.97, -6.49) * mm, "end": v(-126.79, -6.42) * mm});
            skLineSegment(sketch, "E3587", {"start": v(-126.79, -6.42) * mm, "end": v(-126.61, -6.35) * mm});
            skLineSegment(sketch, "E3588", {"start": v(-126.61, -6.35) * mm, "end": v(-126.44, -6.27) * mm});
            skLineSegment(sketch, "E3589", {"start": v(-126.44, -6.27) * mm, "end": v(-126.27, -6.18) * mm});
            skLineSegment(sketch, "E3590", {"start": v(-126.27, -6.18) * mm, "end": v(-126.11, -6.08) * mm});
            skLineSegment(sketch, "E3591", {"start": v(-126.11, -6.08) * mm, "end": v(-125.96, -5.98) * mm});
            skLineSegment(sketch, "E3592", {"start": v(-125.96, -5.98) * mm, "end": v(-125.8, -5.86) * mm});
            skLineSegment(sketch, "E3593", {"start": v(-125.8, -5.86) * mm, "end": v(-125.66, -5.74) * mm});
            skLineSegment(sketch, "E3594", {"start": v(-125.66, -5.74) * mm, "end": v(-125.53, -5.61) * mm});
            skLineSegment(sketch, "E3595", {"start": v(-125.53, -5.61) * mm, "end": v(-125.4, -5.47) * mm});
            skLineSegment(sketch, "E3596", {"start": v(-125.4, -5.47) * mm, "end": v(-125.27, -5.33) * mm});
            skLineSegment(sketch, "E3597", {"start": v(-125.27, -5.33) * mm, "end": v(-125.16, -5.18) * mm});
            skLineSegment(sketch, "E3598", {"start": v(-125.16, -5.18) * mm, "end": v(-125.05, -5.02) * mm});
            skLineSegment(sketch, "E3599", {"start": v(-125.05, -5.02) * mm, "end": v(-124.95, -4.86) * mm});
            skLineSegment(sketch, "E3600", {"start": v(-124.95, -4.86) * mm, "end": v(-124.86, -4.7) * mm});
            skLineSegment(sketch, "E3601", {"start": v(-124.86, -4.7) * mm, "end": v(-124.78, -4.52) * mm});
            skLineSegment(sketch, "E3602", {"start": v(-124.78, -4.52) * mm, "end": v(-124.71, -4.35) * mm});
            skLineSegment(sketch, "E3603", {"start": v(-124.71, -4.35) * mm, "end": v(-124.65, -4.16) * mm});
            skLineSegment(sketch, "E3604", {"start": v(-124.65, -4.16) * mm, "end": v(-124.6, -3.98) * mm});
            skLineSegment(sketch, "E3605", {"start": v(-124.6, -3.98) * mm, "end": v(-124.55, -3.78) * mm});
            skLineSegment(sketch, "E3606", {"start": v(-124.55, -3.78) * mm, "end": v(-124.5, -3.58) * mm});
            skLineSegment(sketch, "E3607", {"start": v(-124.5, -3.58) * mm, "end": v(-124.48, -3.38) * mm});
            skLineSegment(sketch, "E3608", {"start": v(-124.48, -3.38) * mm, "end": v(-124.46, -3.17) * mm});
            skLineSegment(sketch, "E3609", {"start": v(-124.46, -3.17) * mm, "end": v(-124.44, -2.95) * mm});
            skLineSegment(sketch, "E3610", {"start": v(-124.44, -2.95) * mm, "end": v(-124.44, -2.74) * mm});
            skLineSegment(sketch, "E3611", {"start": v(-124.44, -2.74) * mm, "end": v(-124.44, -2.52) * mm});
            skLineSegment(sketch, "E3612", {"start": v(-124.44, -2.52) * mm, "end": v(-124.46, -2.31) * mm});
            skLineSegment(sketch, "E3613", {"start": v(-124.46, -2.31) * mm, "end": v(-124.48, -2.1) * mm});
            skLineSegment(sketch, "E3614", {"start": v(-124.48, -2.1) * mm, "end": v(-124.5, -1.9) * mm});
            skLineSegment(sketch, "E3615", {"start": v(-124.5, -1.9) * mm, "end": v(-124.55, -1.71) * mm});
            skLineSegment(sketch, "E3616", {"start": v(-124.55, -1.71) * mm, "end": v(-124.6, -1.52) * mm});
            skLineSegment(sketch, "E3617", {"start": v(-124.6, -1.52) * mm, "end": v(-124.65, -1.34) * mm});
            skLineSegment(sketch, "E3618", {"start": v(-124.65, -1.34) * mm, "end": v(-124.72, -1.16) * mm});
            skLineSegment(sketch, "E3619", {"start": v(-124.72, -1.16) * mm, "end": v(-124.8, -0.98) * mm});
            skLineSegment(sketch, "E3620", {"start": v(-124.8, -0.98) * mm, "end": v(-124.87, -0.8) * mm});
            skLineSegment(sketch, "E3621", {"start": v(-124.87, -0.8) * mm, "end": v(-124.97, -0.64) * mm});
            skLineSegment(sketch, "E3622", {"start": v(-124.97, -0.64) * mm, "end": v(-125.07, -0.48) * mm});
            skLineSegment(sketch, "E3623", {"start": v(-125.07, -0.48) * mm, "end": v(-125.18, -0.33) * mm});
            skLineSegment(sketch, "E3624", {"start": v(-125.18, -0.33) * mm, "end": v(-125.3, -0.17) * mm});
            skLineSegment(sketch, "E3625", {"start": v(-125.3, -0.17) * mm, "end": v(-125.42, -0.03) * mm});
            skLineSegment(sketch, "E3626", {"start": v(-125.42, -0.03) * mm, "end": v(-125.55, 0.11) * mm});
            skLineSegment(sketch, "E3627", {"start": v(-125.55, 0.11) * mm, "end": v(-125.7, 0.25) * mm});
            skLineSegment(sketch, "E3628", {"start": v(-125.7, 0.25) * mm, "end": v(-125.84, 0.37) * mm});
            skLineSegment(sketch, "E3629", {"start": v(-125.84, 0.37) * mm, "end": v(-126, 0.5) * mm});
            skLineSegment(sketch, "E3630", {"start": v(-126, 0.5) * mm, "end": v(-126.15, 0.6) * mm});
            skLineSegment(sketch, "E3631", {"start": v(-126.15, 0.6) * mm, "end": v(-126.3, 0.7) * mm});
            skLineSegment(sketch, "E3632", {"start": v(-126.3, 0.7) * mm, "end": v(-126.48, 0.8) * mm});
            skLineSegment(sketch, "E3633", {"start": v(-126.48, 0.8) * mm, "end": v(-126.65, 0.87) * mm});
            skLineSegment(sketch, "E3634", {"start": v(-126.65, 0.87) * mm, "end": v(-126.82, 0.95) * mm});
            skLineSegment(sketch, "E3635", {"start": v(-126.82, 0.95) * mm, "end": v(-127, 1.01) * mm});
            skLineSegment(sketch, "E3636", {"start": v(-127, 1.01) * mm, "end": v(-127.19, 1.07) * mm});
            skLineSegment(sketch, "E3637", {"start": v(-127.19, 1.07) * mm, "end": v(-127.38, 1.12) * mm});
            skLineSegment(sketch, "E3638", {"start": v(-127.38, 1.12) * mm, "end": v(-127.57, 1.16) * mm});
            skLineSegment(sketch, "E3639", {"start": v(-127.57, 1.16) * mm, "end": v(-127.77, 1.19) * mm});
            skLineSegment(sketch, "E3640", {"start": v(-127.77, 1.19) * mm, "end": v(-127.98, 1.21) * mm});
            skLineSegment(sketch, "E3641", {"start": v(-127.98, 1.21) * mm, "end": v(-128.19, 1.22) * mm});
            skLineSegment(sketch, "E3642", {"start": v(-128.19, 1.22) * mm, "end": v(-128.4, 1.23) * mm});
            skLineSegment(sketch, "E3643", {"start": v(-128.4, 1.23) * mm, "end": v(-138.3, 1.23) * mm});
            skLineSegment(sketch, "E3644", {"start": v(-138.3, 1.23) * mm, "end": v(-138.49, 1.23) * mm});
            skLineSegment(sketch, "E3645", {"start": v(-138.49, 1.23) * mm, "end": v(-138.67, 1.24) * mm});
            skLineSegment(sketch, "E3646", {"start": v(-138.67, 1.24) * mm, "end": v(-138.85, 1.26) * mm});
            skLineSegment(sketch, "E3647", {"start": v(-138.85, 1.26) * mm, "end": v(-139.03, 1.29) * mm});
            skLineSegment(sketch, "E3648", {"start": v(-139.03, 1.29) * mm, "end": v(-139.2, 1.32) * mm});
            skLineSegment(sketch, "E3649", {"start": v(-139.2, 1.32) * mm, "end": v(-139.37, 1.36) * mm});
            skLineSegment(sketch, "E3650", {"start": v(-139.37, 1.36) * mm, "end": v(-139.53, 1.41) * mm});
            skLineSegment(sketch, "E3651", {"start": v(-139.53, 1.41) * mm, "end": v(-139.7, 1.47) * mm});
            skLineSegment(sketch, "E3652", {"start": v(-139.7, 1.47) * mm, "end": v(-139.85, 1.53) * mm});
            skLineSegment(sketch, "E3653", {"start": v(-139.85, 1.53) * mm, "end": v(-140, 1.6) * mm});
            skLineSegment(sketch, "E3654", {"start": v(-140, 1.6) * mm, "end": v(-140.14, 1.68) * mm});
            skLineSegment(sketch, "E3655", {"start": v(-140.14, 1.68) * mm, "end": v(-140.28, 1.76) * mm});
            skLineSegment(sketch, "E3656", {"start": v(-140.28, 1.76) * mm, "end": v(-140.42, 1.86) * mm});
            skLineSegment(sketch, "E3657", {"start": v(-140.42, 1.86) * mm, "end": v(-140.55, 1.96) * mm});
            skLineSegment(sketch, "E3658", {"start": v(-140.55, 1.96) * mm, "end": v(-140.67, 2.06) * mm});
            skLineSegment(sketch, "E3659", {"start": v(-140.67, 2.06) * mm, "end": v(-140.8, 2.18) * mm});
            skLineSegment(sketch, "E3660", {"start": v(-140.8, 2.18) * mm, "end": v(-140.9, 2.3) * mm});
            skLineSegment(sketch, "E3661", {"start": v(-140.9, 2.3) * mm, "end": v(-141.01, 2.42) * mm});
            skLineSegment(sketch, "E3662", {"start": v(-141.01, 2.42) * mm, "end": v(-141.11, 2.55) * mm});
            skLineSegment(sketch, "E3663", {"start": v(-141.11, 2.55) * mm, "end": v(-141.2, 2.69) * mm});
            skLineSegment(sketch, "E3664", {"start": v(-141.2, 2.69) * mm, "end": v(-141.3, 2.83) * mm});
            skLineSegment(sketch, "E3665", {"start": v(-141.3, 2.83) * mm, "end": v(-141.37, 2.97) * mm});
            skLineSegment(sketch, "E3666", {"start": v(-141.37, 2.97) * mm, "end": v(-141.44, 3.12) * mm});
            skLineSegment(sketch, "E3667", {"start": v(-141.44, 3.12) * mm, "end": v(-141.5, 3.28) * mm});
            skLineSegment(sketch, "E3668", {"start": v(-141.5, 3.28) * mm, "end": v(-141.56, 3.44) * mm});
            skLineSegment(sketch, "E3669", {"start": v(-141.56, 3.44) * mm, "end": v(-141.6, 3.6) * mm});
            skLineSegment(sketch, "E3670", {"start": v(-141.6, 3.6) * mm, "end": v(-141.65, 3.77) * mm});
            skLineSegment(sketch, "E3671", {"start": v(-141.65, 3.77) * mm, "end": v(-141.68, 3.94) * mm});
            skLineSegment(sketch, "E3672", {"start": v(-141.68, 3.94) * mm, "end": v(-141.7, 4.12) * mm});
            skLineSegment(sketch, "E3673", {"start": v(-141.7, 4.12) * mm, "end": v(-141.73, 4.3) * mm});
            skLineSegment(sketch, "E3674", {"start": v(-141.73, 4.3) * mm, "end": v(-141.74, 4.48) * mm});
            skLineSegment(sketch, "E3675", {"start": v(-141.74, 4.48) * mm, "end": v(-141.74, 4.67) * mm});
            skLineSegment(sketch, "E3676", {"start": v(-141.74, 4.67) * mm, "end": v(-141.74, 4.86) * mm});
            skLineSegment(sketch, "E3677", {"start": v(-141.74, 4.86) * mm, "end": v(-141.73, 5.05) * mm});
            skLineSegment(sketch, "E3678", {"start": v(-141.73, 5.05) * mm, "end": v(-141.7, 5.23) * mm});
            skLineSegment(sketch, "E3679", {"start": v(-141.7, 5.23) * mm, "end": v(-141.68, 5.4) * mm});
            skLineSegment(sketch, "E3680", {"start": v(-141.68, 5.4) * mm, "end": v(-141.65, 5.58) * mm});
            skLineSegment(sketch, "E3681", {"start": v(-141.65, 5.58) * mm, "end": v(-141.6, 5.75) * mm});
            skLineSegment(sketch, "E3682", {"start": v(-141.6, 5.75) * mm, "end": v(-141.56, 5.91) * mm});
            skLineSegment(sketch, "E3683", {"start": v(-141.56, 5.91) * mm, "end": v(-141.5, 6.07) * mm});
            skLineSegment(sketch, "E3684", {"start": v(-141.5, 6.07) * mm, "end": v(-141.44, 6.22) * mm});
            skLineSegment(sketch, "E3685", {"start": v(-141.44, 6.22) * mm, "end": v(-141.37, 6.37) * mm});
            skLineSegment(sketch, "E3686", {"start": v(-141.37, 6.37) * mm, "end": v(-141.3, 6.52) * mm});
            skLineSegment(sketch, "E3687", {"start": v(-141.3, 6.52) * mm, "end": v(-141.2, 6.66) * mm});
            skLineSegment(sketch, "E3688", {"start": v(-141.2, 6.66) * mm, "end": v(-141.11, 6.8) * mm});
            skLineSegment(sketch, "E3689", {"start": v(-141.11, 6.8) * mm, "end": v(-141.01, 6.92) * mm});
            skLineSegment(sketch, "E3690", {"start": v(-141.01, 6.92) * mm, "end": v(-140.9, 7.05) * mm});
            skLineSegment(sketch, "E3691", {"start": v(-140.9, 7.05) * mm, "end": v(-140.8, 7.17) * mm});
            skLineSegment(sketch, "E3692", {"start": v(-140.8, 7.17) * mm, "end": v(-140.67, 7.28) * mm});
            skLineSegment(sketch, "E3693", {"start": v(-140.67, 7.28) * mm, "end": v(-140.55, 7.4) * mm});
            skLineSegment(sketch, "E3694", {"start": v(-140.55, 7.4) * mm, "end": v(-140.42, 7.5) * mm});
            skLineSegment(sketch, "E3695", {"start": v(-140.42, 7.5) * mm, "end": v(-140.28, 7.58) * mm});
            skLineSegment(sketch, "E3696", {"start": v(-140.28, 7.58) * mm, "end": v(-140.14, 7.67) * mm});
            skLineSegment(sketch, "E3697", {"start": v(-140.14, 7.67) * mm, "end": v(-140, 7.75) * mm});
            skLineSegment(sketch, "E3698", {"start": v(-140, 7.75) * mm, "end": v(-139.85, 7.82) * mm});
            skLineSegment(sketch, "E3699", {"start": v(-139.85, 7.82) * mm, "end": v(-139.7, 7.88) * mm});
            skLineSegment(sketch, "E3700", {"start": v(-139.7, 7.88) * mm, "end": v(-139.53, 7.94) * mm});
            skLineSegment(sketch, "E3701", {"start": v(-139.53, 7.94) * mm, "end": v(-139.37, 7.98) * mm});
            skLineSegment(sketch, "E3702", {"start": v(-139.37, 7.98) * mm, "end": v(-139.2, 8.03) * mm});
            skLineSegment(sketch, "E3703", {"start": v(-139.2, 8.03) * mm, "end": v(-139.03, 8.06) * mm});
            skLineSegment(sketch, "E3704", {"start": v(-139.03, 8.06) * mm, "end": v(-138.85, 8.09) * mm});
            skLineSegment(sketch, "E3705", {"start": v(-138.85, 8.09) * mm, "end": v(-138.67, 8.1) * mm});
            skLineSegment(sketch, "E3706", {"start": v(-138.67, 8.1) * mm, "end": v(-138.49, 8.11) * mm});
            skLineSegment(sketch, "E3707", {"start": v(-138.49, 8.11) * mm, "end": v(-138.3, 8.12) * mm});
            skLineSegment(sketch, "E3708", {"start": v(-138.3, 8.12) * mm, "end": v(-123.48, 8.12) * mm});
            skLineSegment(sketch, "E3709", {"start": v(-123.48, 8.12) * mm, "end": v(-123.27, 8.12) * mm});
            skLineSegment(sketch, "E3710", {"start": v(-123.27, 8.12) * mm, "end": v(-123.06, 8.14) * mm});
            skLineSegment(sketch, "E3711", {"start": v(-123.06, 8.14) * mm, "end": v(-122.85, 8.16) * mm});
            skLineSegment(sketch, "E3712", {"start": v(-122.85, 8.16) * mm, "end": v(-122.65, 8.19) * mm});
            skLineSegment(sketch, "E3713", {"start": v(-122.65, 8.19) * mm, "end": v(-122.46, 8.23) * mm});
            skLineSegment(sketch, "E3714", {"start": v(-122.46, 8.23) * mm, "end": v(-122.26, 8.28) * mm});
            skLineSegment(sketch, "E3715", {"start": v(-122.26, 8.28) * mm, "end": v(-122.08, 8.33) * mm});
            skLineSegment(sketch, "E3716", {"start": v(-122.08, 8.33) * mm, "end": v(-121.9, 8.4) * mm});
            skLineSegment(sketch, "E3717", {"start": v(-121.9, 8.4) * mm, "end": v(-121.72, 8.47) * mm});
            skLineSegment(sketch, "E3718", {"start": v(-121.72, 8.47) * mm, "end": v(-121.54, 8.56) * mm});
            skLineSegment(sketch, "E3719", {"start": v(-121.54, 8.56) * mm, "end": v(-121.38, 8.65) * mm});
            skLineSegment(sketch, "E3720", {"start": v(-121.38, 8.65) * mm, "end": v(-121.21, 8.75) * mm});
            skLineSegment(sketch, "E3721", {"start": v(-121.21, 8.75) * mm, "end": v(-121.05, 8.85) * mm});
            skLineSegment(sketch, "E3722", {"start": v(-121.05, 8.85) * mm, "end": v(-120.9, 8.97) * mm});
            skLineSegment(sketch, "E3723", {"start": v(-120.9, 8.97) * mm, "end": v(-120.75, 9.1) * mm});
            skLineSegment(sketch, "E3724", {"start": v(-120.75, 9.1) * mm, "end": v(-120.6, 9.23) * mm});
            skLineSegment(sketch, "E3725", {"start": v(-120.6, 9.23) * mm, "end": v(-120.47, 9.37) * mm});
            skLineSegment(sketch, "E3726", {"start": v(-120.47, 9.37) * mm, "end": v(-120.34, 9.52) * mm});
            skLineSegment(sketch, "E3727", {"start": v(-120.34, 9.52) * mm, "end": v(-120.22, 9.67) * mm});
            skLineSegment(sketch, "E3728", {"start": v(-120.22, 9.67) * mm, "end": v(-120.1, 9.83) * mm});
            skLineSegment(sketch, "E3729", {"start": v(-120.1, 9.83) * mm, "end": v(-120, 9.99) * mm});
            skLineSegment(sketch, "E3730", {"start": v(-120, 9.99) * mm, "end": v(-119.91, 10.15) * mm});
            skLineSegment(sketch, "E3731", {"start": v(-119.91, 10.15) * mm, "end": v(-119.83, 10.33) * mm});
            skLineSegment(sketch, "E3732", {"start": v(-119.83, 10.33) * mm, "end": v(-119.75, 10.5) * mm});
            skLineSegment(sketch, "E3733", {"start": v(-119.75, 10.5) * mm, "end": v(-119.68, 10.68) * mm});
            skLineSegment(sketch, "E3734", {"start": v(-119.68, 10.68) * mm, "end": v(-119.63, 10.87) * mm});
            skLineSegment(sketch, "E3735", {"start": v(-119.63, 10.87) * mm, "end": v(-119.58, 11.06) * mm});
            skLineSegment(sketch, "E3736", {"start": v(-119.58, 11.06) * mm, "end": v(-119.54, 11.25) * mm});
            skLineSegment(sketch, "E3737", {"start": v(-119.54, 11.25) * mm, "end": v(-119.5, 11.45) * mm});
            skLineSegment(sketch, "E3738", {"start": v(-119.5, 11.45) * mm, "end": v(-119.48, 11.66) * mm});
            skLineSegment(sketch, "E3739", {"start": v(-119.48, 11.66) * mm, "end": v(-119.47, 11.87) * mm});
            skLineSegment(sketch, "E3740", {"start": v(-119.47, 11.87) * mm, "end": v(-119.46, 12.08) * mm});
            skLineSegment(sketch, "E3741", {"start": v(-119.46, 12.08) * mm, "end": v(-119.47, 12.3) * mm});
            skLineSegment(sketch, "E3742", {"start": v(-119.47, 12.3) * mm, "end": v(-119.48, 12.5) * mm});
            skLineSegment(sketch, "E3743", {"start": v(-119.48, 12.5) * mm, "end": v(-119.5, 12.7) * mm});
            skLineSegment(sketch, "E3744", {"start": v(-119.5, 12.7) * mm, "end": v(-119.54, 12.9) * mm});
            skLineSegment(sketch, "E3745", {"start": v(-119.54, 12.9) * mm, "end": v(-119.58, 13.1) * mm});
            skLineSegment(sketch, "E3746", {"start": v(-119.58, 13.1) * mm, "end": v(-119.63, 13.3) * mm});
            skLineSegment(sketch, "E3747", {"start": v(-119.63, 13.3) * mm, "end": v(-119.68, 13.48) * mm});
            skLineSegment(sketch, "E3748", {"start": v(-119.68, 13.48) * mm, "end": v(-119.75, 13.66) * mm});
            skLineSegment(sketch, "E3749", {"start": v(-119.75, 13.66) * mm, "end": v(-119.83, 13.84) * mm});
            skLineSegment(sketch, "E3750", {"start": v(-119.83, 13.84) * mm, "end": v(-119.91, 14) * mm});
            skLineSegment(sketch, "E3751", {"start": v(-119.91, 14) * mm, "end": v(-120, 14.17) * mm});
            skLineSegment(sketch, "E3752", {"start": v(-120, 14.17) * mm, "end": v(-120.1, 14.34) * mm});
            skLineSegment(sketch, "E3753", {"start": v(-120.1, 14.34) * mm, "end": v(-120.22, 14.5) * mm});
            skLineSegment(sketch, "E3754", {"start": v(-120.22, 14.5) * mm, "end": v(-120.34, 14.64) * mm});
            skLineSegment(sketch, "E3755", {"start": v(-120.34, 14.64) * mm, "end": v(-120.47, 14.79) * mm});
            skLineSegment(sketch, "E3756", {"start": v(-120.47, 14.79) * mm, "end": v(-120.6, 14.93) * mm});
            skLineSegment(sketch, "E3757", {"start": v(-120.6, 14.93) * mm, "end": v(-120.75, 15.07) * mm});
            skLineSegment(sketch, "E3758", {"start": v(-120.75, 15.07) * mm, "end": v(-120.9, 15.2) * mm});
            skLineSegment(sketch, "E3759", {"start": v(-120.9, 15.2) * mm, "end": v(-121.05, 15.3) * mm});
            skLineSegment(sketch, "E3760", {"start": v(-121.05, 15.3) * mm, "end": v(-121.21, 15.42) * mm});
            skLineSegment(sketch, "E3761", {"start": v(-121.21, 15.42) * mm, "end": v(-121.38, 15.52) * mm});
            skLineSegment(sketch, "E3762", {"start": v(-121.38, 15.52) * mm, "end": v(-121.54, 15.6) * mm});
            skLineSegment(sketch, "E3763", {"start": v(-121.54, 15.6) * mm, "end": v(-121.72, 15.7) * mm});
            skLineSegment(sketch, "E3764", {"start": v(-121.72, 15.7) * mm, "end": v(-121.9, 15.76) * mm});
            skLineSegment(sketch, "E3765", {"start": v(-121.9, 15.76) * mm, "end": v(-122.08, 15.83) * mm});
            skLineSegment(sketch, "E3766", {"start": v(-122.08, 15.83) * mm, "end": v(-122.26, 15.89) * mm});
            skLineSegment(sketch, "E3767", {"start": v(-122.26, 15.89) * mm, "end": v(-122.46, 15.94) * mm});
            skLineSegment(sketch, "E3768", {"start": v(-122.46, 15.94) * mm, "end": v(-122.65, 15.97) * mm});
            skLineSegment(sketch, "E3769", {"start": v(-122.65, 15.97) * mm, "end": v(-122.85, 16) * mm});
            skLineSegment(sketch, "E3770", {"start": v(-122.85, 16) * mm, "end": v(-123.06, 16.03) * mm});
            skLineSegment(sketch, "E3771", {"start": v(-123.06, 16.03) * mm, "end": v(-123.27, 16.04) * mm});
            skLineSegment(sketch, "E3772", {"start": v(-123.27, 16.04) * mm, "end": v(-123.48, 16.04) * mm});
            skLineSegment(sketch, "E3773", {"start": v(-123.48, 16.04) * mm, "end": v(-146.51, 16.04) * mm});
            skLineSegment(sketch, "E3774", {"start": v(-146.51, 16.04) * mm, "end": v(-146.83, 16.03) * mm});
            skLineSegment(sketch, "E3775", {"start": v(-146.83, 16.03) * mm, "end": v(-147.15, 15.98) * mm});
            skLineSegment(sketch, "E3776", {"start": v(-147.15, 15.98) * mm, "end": v(-147.45, 15.9) * mm});
            skLineSegment(sketch, "E3777", {"start": v(-147.45, 15.9) * mm, "end": v(-147.74, 15.8) * mm});
            skLineSegment(sketch, "E3778", {"start": v(-147.74, 15.8) * mm, "end": v(-148.02, 15.66) * mm});
            skLineSegment(sketch, "E3779", {"start": v(-148.02, 15.66) * mm, "end": v(-148.28, 15.5) * mm});
            skLineSegment(sketch, "E3780", {"start": v(-148.28, 15.5) * mm, "end": v(-148.52, 15.32) * mm});
            skLineSegment(sketch, "E3781", {"start": v(-148.52, 15.32) * mm, "end": v(-148.74, 15.12) * mm});
            skLineSegment(sketch, "E3782", {"start": v(-148.74, 15.12) * mm, "end": v(-148.95, 14.9) * mm});
            skLineSegment(sketch, "E3783", {"start": v(-148.95, 14.9) * mm, "end": v(-149.13, 14.65) * mm});
            skLineSegment(sketch, "E3784", {"start": v(-149.13, 14.65) * mm, "end": v(-149.29, 14.4) * mm});
            skLineSegment(sketch, "E3785", {"start": v(-149.29, 14.4) * mm, "end": v(-149.42, 14.12) * mm});
            skLineSegment(sketch, "E3786", {"start": v(-149.42, 14.12) * mm, "end": v(-149.53, 13.83) * mm});
            skLineSegment(sketch, "E3787", {"start": v(-149.53, 13.83) * mm, "end": v(-149.6, 13.52) * mm});
            skLineSegment(sketch, "E3788", {"start": v(-149.6, 13.52) * mm, "end": v(-149.65, 13.21) * mm});
            skLineSegment(sketch, "E3789", {"start": v(-149.65, 13.21) * mm, "end": v(-149.67, 12.89) * mm});
            skLineSegment(sketch, "E3790", {"start": v(-149.67, 12.89) * mm, "end": v(-149.67, -22.53) * mm});
            skLineSegment(sketch, "E3791", {"start": v(-149.67, -22.53) * mm, "end": v(-149.67, -22.64) * mm});
            skLineSegment(sketch, "E3792", {"start": v(-149.67, -22.64) * mm, "end": v(-149.68, -22.74) * mm});
            skLineSegment(sketch, "E3793", {"start": v(-149.68, -22.74) * mm, "end": v(-149.7, -22.84) * mm});
            skLineSegment(sketch, "E3794", {"start": v(-149.7, -22.84) * mm, "end": v(-149.73, -22.93) * mm});
            skLineSegment(sketch, "E3795", {"start": v(-149.73, -22.93) * mm, "end": v(-149.77, -23.01) * mm});
            skLineSegment(sketch, "E3796", {"start": v(-149.77, -23.01) * mm, "end": v(-149.8, -23.09) * mm});
            skLineSegment(sketch, "E3797", {"start": v(-149.8, -23.09) * mm, "end": v(-149.86, -23.16) * mm});
            skLineSegment(sketch, "E3798", {"start": v(-149.86, -23.16) * mm, "end": v(-149.92, -23.22) * mm});
            skLineSegment(sketch, "E3799", {"start": v(-149.92, -23.22) * mm, "end": v(-149.99, -23.28) * mm});
            skLineSegment(sketch, "E3800", {"start": v(-149.99, -23.28) * mm, "end": v(-150.06, -23.33) * mm});
            skLineSegment(sketch, "E3801", {"start": v(-150.06, -23.33) * mm, "end": v(-150.14, -23.37) * mm});
            skLineSegment(sketch, "E3802", {"start": v(-150.14, -23.37) * mm, "end": v(-150.23, -23.4) * mm});
            skLineSegment(sketch, "E3803", {"start": v(-150.23, -23.4) * mm, "end": v(-150.33, -23.44) * mm});
            skLineSegment(sketch, "E3804", {"start": v(-150.33, -23.44) * mm, "end": v(-150.44, -23.46) * mm});
            skLineSegment(sketch, "E3805", {"start": v(-150.44, -23.46) * mm, "end": v(-150.56, -23.47) * mm});
            skLineSegment(sketch, "E3806", {"start": v(-150.56, -23.47) * mm, "end": v(-150.68, -23.48) * mm});
            skLineSegment(sketch, "E3807", {"start": v(-150.68, -23.48) * mm, "end": v(-153.84, -23.48) * mm});
            skLineSegment(sketch, "E3808", {"start": v(-153.84, -23.48) * mm, "end": v(-153.9, -23.48) * mm});
            skLineSegment(sketch, "E3809", {"start": v(-153.9, -23.48) * mm, "end": v(-153.97, -23.47) * mm});
            skLineSegment(sketch, "E3810", {"start": v(-153.97, -23.47) * mm, "end": v(-154.03, -23.45) * mm});
            skLineSegment(sketch, "E3811", {"start": v(-154.03, -23.45) * mm, "end": v(-154.1, -23.43) * mm});
            skLineSegment(sketch, "E3812", {"start": v(-154.1, -23.43) * mm, "end": v(-154.15, -23.4) * mm});
            skLineSegment(sketch, "E3813", {"start": v(-154.15, -23.4) * mm, "end": v(-154.2, -23.37) * mm});
            skLineSegment(sketch, "E3814", {"start": v(-154.2, -23.37) * mm, "end": v(-154.26, -23.33) * mm});
            skLineSegment(sketch, "E3815", {"start": v(-154.26, -23.33) * mm, "end": v(-154.3, -23.3) * mm});
            skLineSegment(sketch, "E3816", {"start": v(-154.3, -23.3) * mm, "end": v(-154.34, -23.25) * mm});
            skLineSegment(sketch, "E3817", {"start": v(-154.34, -23.25) * mm, "end": v(-154.38, -23.2) * mm});
            skLineSegment(sketch, "E3818", {"start": v(-154.38, -23.2) * mm, "end": v(-154.42, -23.14) * mm});
            skLineSegment(sketch, "E3819", {"start": v(-154.42, -23.14) * mm, "end": v(-154.44, -23.08) * mm});
            skLineSegment(sketch, "E3820", {"start": v(-154.44, -23.08) * mm, "end": v(-154.46, -23.02) * mm});
            skLineSegment(sketch, "E3821", {"start": v(-154.46, -23.02) * mm, "end": v(-154.48, -22.96) * mm});
            skLineSegment(sketch, "E3822", {"start": v(-154.48, -22.96) * mm, "end": v(-154.5, -22.9) * mm});
            skLineSegment(sketch, "E3823", {"start": v(-154.5, -22.9) * mm, "end": v(-154.5, -22.83) * mm});
            skLineSegment(sketch, "E3824", {"start": v(-154.5, -22.83) * mm, "end": v(-154.5, 12.07) * mm});
            skLineSegment(sketch, "E3825", {"start": v(-154.5, 12.07) * mm, "end": v(-154.5, 12.3) * mm});
            skLineSegment(sketch, "E3826", {"start": v(-154.5, 12.3) * mm, "end": v(-154.51, 12.5) * mm});
            skLineSegment(sketch, "E3827", {"start": v(-154.51, 12.5) * mm, "end": v(-154.53, 12.72) * mm});
            skLineSegment(sketch, "E3828", {"start": v(-154.53, 12.72) * mm, "end": v(-154.56, 12.92) * mm});
            skLineSegment(sketch, "E3829", {"start": v(-154.56, 12.92) * mm, "end": v(-154.6, 13.12) * mm});
            skLineSegment(sketch, "E3830", {"start": v(-154.6, 13.12) * mm, "end": v(-154.65, 13.31) * mm});
            skLineSegment(sketch, "E3831", {"start": v(-154.65, 13.31) * mm, "end": v(-154.7, 13.5) * mm});
            skLineSegment(sketch, "E3832", {"start": v(-154.7, 13.5) * mm, "end": v(-154.77, 13.69) * mm});
            skLineSegment(sketch, "E3833", {"start": v(-154.77, 13.69) * mm, "end": v(-154.84, 13.86) * mm});
            skLineSegment(sketch, "E3834", {"start": v(-154.84, 13.86) * mm, "end": v(-154.92, 14.04) * mm});
            skLineSegment(sketch, "E3835", {"start": v(-154.92, 14.04) * mm, "end": v(-155, 14.2) * mm});
            skLineSegment(sketch, "E3836", {"start": v(-155, 14.2) * mm, "end": v(-155.1, 14.36) * mm});
            skLineSegment(sketch, "E3837", {"start": v(-155.1, 14.36) * mm, "end": v(-155.2, 14.52) * mm});
            skLineSegment(sketch, "E3838", {"start": v(-155.2, 14.52) * mm, "end": v(-155.32, 14.67) * mm});
            skLineSegment(sketch, "E3839", {"start": v(-155.32, 14.67) * mm, "end": v(-155.44, 14.81) * mm});
            skLineSegment(sketch, "E3840", {"start": v(-155.44, 14.81) * mm, "end": v(-155.57, 14.95) * mm});
            skLineSegment(sketch, "E3841", {"start": v(-155.57, 14.95) * mm, "end": v(-155.71, 15.08) * mm});
            skLineSegment(sketch, "E3842", {"start": v(-155.71, 15.08) * mm, "end": v(-155.85, 15.2) * mm});
            skLineSegment(sketch, "E3843", {"start": v(-155.85, 15.2) * mm, "end": v(-156, 15.32) * mm});
            skLineSegment(sketch, "E3844", {"start": v(-156, 15.32) * mm, "end": v(-156.16, 15.43) * mm});
            skLineSegment(sketch, "E3845", {"start": v(-156.16, 15.43) * mm, "end": v(-156.32, 15.53) * mm});
            skLineSegment(sketch, "E3846", {"start": v(-156.32, 15.53) * mm, "end": v(-156.48, 15.62) * mm});
            skLineSegment(sketch, "E3847", {"start": v(-156.48, 15.62) * mm, "end": v(-156.65, 15.7) * mm});
            skLineSegment(sketch, "E3848", {"start": v(-156.65, 15.7) * mm, "end": v(-156.83, 15.77) * mm});
            skLineSegment(sketch, "E3849", {"start": v(-156.83, 15.77) * mm, "end": v(-157.01, 15.83) * mm});
            skLineSegment(sketch, "E3850", {"start": v(-157.01, 15.83) * mm, "end": v(-157.2, 15.9) * mm});
            skLineSegment(sketch, "E3851", {"start": v(-157.2, 15.9) * mm, "end": v(-157.4, 15.94) * mm});
            skLineSegment(sketch, "E3852", {"start": v(-157.4, 15.94) * mm, "end": v(-157.59, 15.98) * mm});
            skLineSegment(sketch, "E3853", {"start": v(-157.59, 15.98) * mm, "end": v(-157.8, 16) * mm});
            skLineSegment(sketch, "E3854", {"start": v(-157.8, 16) * mm, "end": v(-158, 16.03) * mm});
            skLineSegment(sketch, "E3855", {"start": v(-158, 16.03) * mm, "end": v(-158.21, 16.04) * mm});
            skLineSegment(sketch, "E3856", {"start": v(-158.21, 16.04) * mm, "end": v(-158.43, 16.04) * mm});
            skLineSegment(sketch, "E3857", {"start": v(-158.43, 16.04) * mm, "end": v(-158.64, 16.04) * mm});
            skLineSegment(sketch, "E3858", {"start": v(-158.64, 16.04) * mm, "end": v(-158.85, 16.03) * mm});
            skLineSegment(sketch, "E3859", {"start": v(-158.85, 16.03) * mm, "end": v(-159.05, 16) * mm});
            skLineSegment(sketch, "E3860", {"start": v(-159.05, 16) * mm, "end": v(-159.25, 15.97) * mm});
            skLineSegment(sketch, "E3861", {"start": v(-159.25, 15.97) * mm, "end": v(-159.45, 15.93) * mm});
            skLineSegment(sketch, "E3862", {"start": v(-159.45, 15.93) * mm, "end": v(-159.64, 15.89) * mm});
            skLineSegment(sketch, "E3863", {"start": v(-159.64, 15.89) * mm, "end": v(-159.82, 15.83) * mm});
            skLineSegment(sketch, "E3864", {"start": v(-159.82, 15.83) * mm, "end": v(-160, 15.76) * mm});
            skLineSegment(sketch, "E3865", {"start": v(-160, 15.76) * mm, "end": v(-160.17, 15.69) * mm});
            skLineSegment(sketch, "E3866", {"start": v(-160.17, 15.69) * mm, "end": v(-160.34, 15.6) * mm});
            skLineSegment(sketch, "E3867", {"start": v(-160.34, 15.6) * mm, "end": v(-160.5, 15.51) * mm});
            skLineSegment(sketch, "E3868", {"start": v(-160.5, 15.51) * mm, "end": v(-160.67, 15.41) * mm});
            skLineSegment(sketch, "E3869", {"start": v(-160.67, 15.41) * mm, "end": v(-160.83, 15.3) * mm});
            skLineSegment(sketch, "E3870", {"start": v(-160.83, 15.3) * mm, "end": v(-160.98, 15.19) * mm});
            skLineSegment(sketch, "E3871", {"start": v(-160.98, 15.19) * mm, "end": v(-161.12, 15.06) * mm});
            skLineSegment(sketch, "E3872", {"start": v(-161.12, 15.06) * mm, "end": v(-161.26, 14.93) * mm});
            skLineSegment(sketch, "E3873", {"start": v(-161.26, 14.93) * mm, "end": v(-161.4, 14.79) * mm});
            skLineSegment(sketch, "E3874", {"start": v(-161.4, 14.79) * mm, "end": v(-161.52, 14.64) * mm});
            skLineSegment(sketch, "E3875", {"start": v(-161.52, 14.64) * mm, "end": v(-161.64, 14.49) * mm});
            skLineSegment(sketch, "E3876", {"start": v(-161.64, 14.49) * mm, "end": v(-161.74, 14.33) * mm});
            skLineSegment(sketch, "E3877", {"start": v(-161.74, 14.33) * mm, "end": v(-161.84, 14.17) * mm});
            skLineSegment(sketch, "E3878", {"start": v(-161.84, 14.17) * mm, "end": v(-161.93, 14) * mm});
            skLineSegment(sketch, "E3879", {"start": v(-161.93, 14) * mm, "end": v(-162.02, 13.83) * mm});
            skLineSegment(sketch, "E3880", {"start": v(-162.02, 13.83) * mm, "end": v(-162.09, 13.65) * mm});
            skLineSegment(sketch, "E3881", {"start": v(-162.09, 13.65) * mm, "end": v(-162.15, 13.47) * mm});
            skLineSegment(sketch, "E3882", {"start": v(-162.15, 13.47) * mm, "end": v(-162.21, 13.29) * mm});
            skLineSegment(sketch, "E3883", {"start": v(-162.21, 13.29) * mm, "end": v(-162.26, 13.1) * mm});
            skLineSegment(sketch, "E3884", {"start": v(-162.26, 13.1) * mm, "end": v(-162.3, 12.9) * mm});
            skLineSegment(sketch, "E3885", {"start": v(-162.3, 12.9) * mm, "end": v(-162.33, 12.7) * mm});
            skLineSegment(sketch, "E3886", {"start": v(-162.33, 12.7) * mm, "end": v(-162.35, 12.5) * mm});
            skLineSegment(sketch, "E3887", {"start": v(-162.35, 12.5) * mm, "end": v(-162.36, 12.28) * mm});
            skLineSegment(sketch, "E3888", {"start": v(-162.36, 12.28) * mm, "end": v(-162.37, 12.07) * mm});
            skLineSegment(sketch, "E3889", {"start": v(-162.37, 12.07) * mm, "end": v(-162.37, -18.54) * mm});
            skLineSegment(sketch, "E3890", {"start": v(-162.37, -18.54) * mm, "end": v(-162.37, -18.54) * mm});
            skLineSegment(sketch, "E3891", {"start": v(-162.37, -18.54) * mm, "end": v(-162.37, -18.55) * mm});
            skLineSegment(sketch, "E3892", {"start": v(-162.37, -18.55) * mm, "end": v(-162.37, -18.55) * mm});
            skLineSegment(sketch, "E3893", {"start": v(-162.37, -18.55) * mm, "end": v(-162.37, -18.56) * mm});
            skLineSegment(sketch, "E3894", {"start": v(-162.37, -18.56) * mm, "end": v(-162.37, -18.56) * mm});
            skLineSegment(sketch, "E3895", {"start": v(-162.37, -18.56) * mm, "end": v(-162.38, -18.56) * mm});
            skLineSegment(sketch, "E3896", {"start": v(-162.38, -18.56) * mm, "end": v(-162.38, -18.56) * mm});
            skLineSegment(sketch, "E3897", {"start": v(-162.38, -18.56) * mm, "end": v(-162.39, -18.56) * mm});
            skLineSegment(sketch, "E3898", {"start": v(-162.39, -18.56) * mm, "end": v(-162.39, -18.56) * mm});
            skLineSegment(sketch, "E3899", {"start": v(-162.39, -18.56) * mm, "end": v(-162.4, -18.56) * mm});
            skLineSegment(sketch, "E3900", {"start": v(-162.4, -18.56) * mm, "end": v(-162.4, -18.56) * mm});
            skLineSegment(sketch, "E3901", {"start": v(-162.4, -18.56) * mm, "end": v(-162.41, -18.56) * mm});
            skLineSegment(sketch, "E3902", {"start": v(-162.41, -18.56) * mm, "end": v(-162.41, -18.56) * mm});
            skLineSegment(sketch, "E3903", {"start": v(-162.41, -18.56) * mm, "end": v(-162.42, -18.56) * mm});
            skLineSegment(sketch, "E3904", {"start": v(-162.42, -18.56) * mm, "end": v(-162.42, -18.56) * mm});
            skLineSegment(sketch, "E3905", {"start": v(-162.42, -18.56) * mm, "end": v(-162.42, -18.55) * mm});
            skLineSegment(sketch, "E3906", {"start": v(-162.42, -18.55) * mm, "end": v(-179.18, 14.87) * mm});
            skLineSegment(sketch, "E3907", {"start": v(-179.18, 14.87) * mm, "end": v(-179.24, 14.98) * mm});
            skLineSegment(sketch, "E3908", {"start": v(-179.24, 14.98) * mm, "end": v(-179.3, 15.1) * mm});
            skLineSegment(sketch, "E3909", {"start": v(-179.3, 15.1) * mm, "end": v(-179.37, 15.21) * mm});
            skLineSegment(sketch, "E3910", {"start": v(-179.37, 15.21) * mm, "end": v(-179.45, 15.33) * mm});
            skLineSegment(sketch, "E3911", {"start": v(-179.45, 15.33) * mm, "end": v(-179.53, 15.44) * mm});
            skLineSegment(sketch, "E3912", {"start": v(-179.53, 15.44) * mm, "end": v(-179.62, 15.55) * mm});
            skLineSegment(sketch, "E3913", {"start": v(-179.62, 15.55) * mm, "end": v(-179.72, 15.65) * mm});
            skLineSegment(sketch, "E3914", {"start": v(-179.72, 15.65) * mm, "end": v(-179.82, 15.75) * mm});
            skLineSegment(sketch, "E3915", {"start": v(-179.82, 15.75) * mm, "end": v(-179.93, 15.83) * mm});
            skLineSegment(sketch, "E3916", {"start": v(-179.93, 15.83) * mm, "end": v(-180.05, 15.9) * mm});
            skLineSegment(sketch, "E3917", {"start": v(-180.05, 15.9) * mm, "end": v(-180.18, 15.96) * mm});
            skLineSegment(sketch, "E3918", {"start": v(-180.18, 15.96) * mm, "end": v(-180.32, 16) * mm});
            skLineSegment(sketch, "E3919", {"start": v(-180.32, 16) * mm, "end": v(-180.47, 16.04) * mm});
            skLineSegment(sketch, "E3920", {"start": v(-180.47, 16.04) * mm, "end": v(-180.63, 16.05) * mm});
            skLineSegment(sketch, "E3921", {"start": v(-180.63, 16.05) * mm, "end": v(-180.67, 16.05) * mm});
            skLineSegment(sketch, "E3922", {"start": v(-180.67, 16.05) * mm, "end": v(-180.7, 16.04) * mm});
            skLineSegment(sketch, "E3923", {"start": v(-180.7, 16.04) * mm, "end": v(-180.73, 16.04) * mm});
            skLineSegment(sketch, "E3924", {"start": v(-180.73, 16.04) * mm, "end": v(-180.75, 16.04) * mm});
            skLineSegment(sketch, "E3925", {"start": v(-180.75, 16.04) * mm, "end": v(-180.76, 16.04) * mm});
            skLineSegment(sketch, "E3926", {"start": v(-180.76, 16.04) * mm, "end": v(-180.78, 16.04) * mm});
            skLineSegment(sketch, "E3927", {"start": v(-180.78, 16.04) * mm, "end": v(-180.83, 16.04) * mm});
            skLineSegment(sketch, "E3928", {"start": v(-180.83, 16.04) * mm, "end": v(-180.98, 16.03) * mm});
            skLineSegment(sketch, "E3929", {"start": v(-180.98, 16.03) * mm, "end": v(-181.12, 16) * mm});
            skLineSegment(sketch, "E3930", {"start": v(-181.12, 16) * mm, "end": v(-181.25, 15.96) * mm});
            skLineSegment(sketch, "E3931", {"start": v(-181.25, 15.96) * mm, "end": v(-181.37, 15.9) * mm});
            skLineSegment(sketch, "E3932", {"start": v(-181.37, 15.9) * mm, "end": v(-181.49, 15.83) * mm});
            skLineSegment(sketch, "E3933", {"start": v(-181.49, 15.83) * mm, "end": v(-181.59, 15.75) * mm});
            skLineSegment(sketch, "E3934", {"start": v(-181.59, 15.75) * mm, "end": v(-181.68, 15.66) * mm});
            skLineSegment(sketch, "E3935", {"start": v(-181.68, 15.66) * mm, "end": v(-181.77, 15.56) * mm});
            skLineSegment(sketch, "E3936", {"start": v(-181.77, 15.56) * mm, "end": v(-181.84, 15.45) * mm});
            skLineSegment(sketch, "E3937", {"start": v(-181.84, 15.45) * mm, "end": v(-181.9, 15.34) * mm});
            skLineSegment(sketch, "E3938", {"start": v(-181.9, 15.34) * mm, "end": v(-181.96, 15.23) * mm});
            skLineSegment(sketch, "E3939", {"start": v(-181.96, 15.23) * mm, "end": v(-182.01, 15.12) * mm});
            skLineSegment(sketch, "E3940", {"start": v(-182.01, 15.12) * mm, "end": v(-182.05, 15) * mm});
            skLineSegment(sketch, "E3941", {"start": v(-182.05, 15) * mm, "end": v(-182.08, 14.88) * mm});
            skLineSegment(sketch, "E3942", {"start": v(-182.08, 14.88) * mm, "end": v(-182.1, 14.77) * mm});
            skLineSegment(sketch, "E3943", {"start": v(-182.1, 14.77) * mm, "end": v(-182.1, 14.67) * mm});
            skLineSegment(sketch, "E3944", {"start": v(-182.1, 14.67) * mm, "end": v(-182.1, -22.83) * mm});
            skLineSegment(sketch, "E3945", {"start": v(-182.1, -22.83) * mm, "end": v(-182.1, -22.9) * mm});
            skLineSegment(sketch, "E3946", {"start": v(-182.1, -22.9) * mm, "end": v(-182.12, -22.96) * mm});
            skLineSegment(sketch, "E3947", {"start": v(-182.12, -22.96) * mm, "end": v(-182.13, -23.02) * mm});
            skLineSegment(sketch, "E3948", {"start": v(-182.13, -23.02) * mm, "end": v(-182.16, -23.08) * mm});
            skLineSegment(sketch, "E3949", {"start": v(-182.16, -23.08) * mm, "end": v(-182.18, -23.14) * mm});
            skLineSegment(sketch, "E3950", {"start": v(-182.18, -23.14) * mm, "end": v(-182.22, -23.2) * mm});
            skLineSegment(sketch, "E3951", {"start": v(-182.22, -23.2) * mm, "end": v(-182.26, -23.25) * mm});
            skLineSegment(sketch, "E3952", {"start": v(-182.26, -23.25) * mm, "end": v(-182.3, -23.3) * mm});
            skLineSegment(sketch, "E3953", {"start": v(-182.3, -23.3) * mm, "end": v(-182.34, -23.33) * mm});
            skLineSegment(sketch, "E3954", {"start": v(-182.34, -23.33) * mm, "end": v(-182.4, -23.37) * mm});
            skLineSegment(sketch, "E3955", {"start": v(-182.4, -23.37) * mm, "end": v(-182.45, -23.4) * mm});
            skLineSegment(sketch, "E3956", {"start": v(-182.45, -23.4) * mm, "end": v(-182.5, -23.43) * mm});
            skLineSegment(sketch, "E3957", {"start": v(-182.5, -23.43) * mm, "end": v(-182.57, -23.45) * mm});
            skLineSegment(sketch, "E3958", {"start": v(-182.57, -23.45) * mm, "end": v(-182.63, -23.47) * mm});
            skLineSegment(sketch, "E3959", {"start": v(-182.63, -23.47) * mm, "end": v(-182.7, -23.48) * mm});
            skLineSegment(sketch, "E3960", {"start": v(-182.7, -23.48) * mm, "end": v(-182.76, -23.48) * mm});
            skLineSegment(sketch, "E3961", {"start": v(-182.76, -23.48) * mm, "end": v(-184.5, -23.48) * mm});
            skLineSegment(sketch, "E3962", {"start": v(-184.5, -23.48) * mm, "end": v(-184.53, -23.52) * mm});
            skLineSegment(sketch, "E3963", {"start": v(-184.53, -23.52) * mm, "end": v(-192.86, -23.52) * mm});
            skLineSegment(sketch, "E3964", {"start": v(-192.86, -23.52) * mm, "end": v(-193.43, -23.5) * mm});
            skLineSegment(sketch, "E3965", {"start": v(-193.43, -23.5) * mm, "end": v(-193.99, -23.4) * mm});
            skLineSegment(sketch, "E3966", {"start": v(-193.99, -23.4) * mm, "end": v(-194.53, -23.27) * mm});
            skLineSegment(sketch, "E3967", {"start": v(-194.53, -23.27) * mm, "end": v(-195.05, -23.08) * mm});
            skLineSegment(sketch, "E3968", {"start": v(-195.05, -23.08) * mm, "end": v(-195.54, -22.84) * mm});
            skLineSegment(sketch, "E3969", {"start": v(-195.54, -22.84) * mm, "end": v(-196, -22.56) * mm});
            skLineSegment(sketch, "E3970", {"start": v(-196, -22.56) * mm, "end": v(-196.44, -22.23) * mm});
            skLineSegment(sketch, "E3971", {"start": v(-196.44, -22.23) * mm, "end": v(-196.84, -21.87) * mm});
            skLineSegment(sketch, "E3972", {"start": v(-196.84, -21.87) * mm, "end": v(-197.2, -21.47) * mm});
            skLineSegment(sketch, "E3973", {"start": v(-197.2, -21.47) * mm, "end": v(-197.53, -21.03) * mm});
            skLineSegment(sketch, "E3974", {"start": v(-197.53, -21.03) * mm, "end": v(-197.8, -20.57) * mm});
            skLineSegment(sketch, "E3975", {"start": v(-197.8, -20.57) * mm, "end": v(-198.05, -20.08) * mm});
            skLineSegment(sketch, "E3976", {"start": v(-198.05, -20.08) * mm, "end": v(-198.24, -19.56) * mm});
            skLineSegment(sketch, "E3977", {"start": v(-198.24, -19.56) * mm, "end": v(-198.37, -19.02) * mm});
            skLineSegment(sketch, "E3978", {"start": v(-198.37, -19.02) * mm, "end": v(-198.46, -18.46) * mm});
            skLineSegment(sketch, "E3979", {"start": v(-198.46, -18.46) * mm, "end": v(-198.49, -17.89) * mm});
            skLineSegment(sketch, "E3980", {"start": v(-198.49, -17.89) * mm, "end": v(-198.49, 17.82) * mm});
            skLineSegment(sketch, "E3981", {"start": v(-198.49, 17.82) * mm, "end": v(-198.46, 18.4) * mm});
            skLineSegment(sketch, "E3982", {"start": v(-198.46, 18.4) * mm, "end": v(-198.37, 18.96) * mm});
            skLineSegment(sketch, "E3983", {"start": v(-198.37, 18.96) * mm, "end": v(-198.24, 19.5) * mm});
            skLineSegment(sketch, "E3984", {"start": v(-198.24, 19.5) * mm, "end": v(-198.05, 20.02) * mm});
            skLineSegment(sketch, "E3985", {"start": v(-198.05, 20.02) * mm, "end": v(-197.8, 20.5) * mm});
            skLineSegment(sketch, "E3986", {"start": v(-197.8, 20.5) * mm, "end": v(-197.53, 20.97) * mm});
            skLineSegment(sketch, "E3987", {"start": v(-197.53, 20.97) * mm, "end": v(-197.2, 21.4) * mm});
            skLineSegment(sketch, "E3988", {"start": v(-197.2, 21.4) * mm, "end": v(-196.84, 21.8) * mm});
            skLineSegment(sketch, "E3989", {"start": v(-196.84, 21.8) * mm, "end": v(-196.44, 22.17) * mm});
            skLineSegment(sketch, "E3990", {"start": v(-196.44, 22.17) * mm, "end": v(-196, 22.5) * mm});
            skLineSegment(sketch, "E3991", {"start": v(-196, 22.5) * mm, "end": v(-195.54, 22.78) * mm});
            skLineSegment(sketch, "E3992", {"start": v(-195.54, 22.78) * mm, "end": v(-195.05, 23.01) * mm});
            skLineSegment(sketch, "E3993", {"start": v(-195.05, 23.01) * mm, "end": v(-194.53, 23.2) * mm});
            skLineSegment(sketch, "E3994", {"start": v(-194.53, 23.2) * mm, "end": v(-193.99, 23.34) * mm});
            skLineSegment(sketch, "E3995", {"start": v(-193.99, 23.34) * mm, "end": v(-193.43, 23.43) * mm});
            skLineSegment(sketch, "E3996", {"start": v(-193.43, 23.43) * mm, "end": v(-192.86, 23.46) * mm});
            skLineSegment(sketch, "E3997", {"start": v(-192.86, 23.46) * mm, "end": v(192.86, 23.46) * mm});
            skLineSegment(sketch, "E3998", {"start": v(192.86, 23.46) * mm, "end": v(193.43, 23.43) * mm});
            skLineSegment(sketch, "E3999", {"start": v(193.43, 23.43) * mm, "end": v(193.99, 23.34) * mm});
            skLineSegment(sketch, "E4000", {"start": v(193.99, 23.34) * mm, "end": v(194.53, 23.2) * mm});
            skLineSegment(sketch, "E4001", {"start": v(194.53, 23.2) * mm, "end": v(195.05, 23.01) * mm});
            skLineSegment(sketch, "E4002", {"start": v(195.05, 23.01) * mm, "end": v(195.54, 22.78) * mm});
            skLineSegment(sketch, "E4003", {"start": v(195.54, 22.78) * mm, "end": v(196, 22.5) * mm});
            skLineSegment(sketch, "E4004", {"start": v(196, 22.5) * mm, "end": v(196.44, 22.17) * mm});
            skLineSegment(sketch, "E4005", {"start": v(196.44, 22.17) * mm, "end": v(196.84, 21.8) * mm});
            skLineSegment(sketch, "E4006", {"start": v(196.84, 21.8) * mm, "end": v(197.2, 21.4) * mm});
            skLineSegment(sketch, "E4007", {"start": v(197.2, 21.4) * mm, "end": v(197.53, 20.97) * mm});
            skLineSegment(sketch, "E4008", {"start": v(197.53, 20.97) * mm, "end": v(197.8, 20.5) * mm});
            skLineSegment(sketch, "E4009", {"start": v(197.8, 20.5) * mm, "end": v(198.05, 20.02) * mm});
            skLineSegment(sketch, "E4010", {"start": v(198.05, 20.02) * mm, "end": v(198.24, 19.5) * mm});
            skLineSegment(sketch, "E4011", {"start": v(198.24, 19.5) * mm, "end": v(198.37, 18.96) * mm});
            skLineSegment(sketch, "E4012", {"start": v(198.37, 18.96) * mm, "end": v(198.46, 18.4) * mm});
            skLineSegment(sketch, "E4013", {"start": v(198.46, 18.4) * mm, "end": v(198.49, 17.82) * mm});
            skLineSegment(sketch, "E4014", {"start": v(198.49, 17.82) * mm, "end": v(198.49, -17.89) * mm});
            skSolve(sketch);
        }
        {
            var Q0;
            Q0=makeQuery(id+"F0.imprint","IMPRINT",FACE,{"disambiguationData":[TD([[makeQuery(id+"F0.imprint","IMPRINT",EDGE,{"derivedFrom":sQuery(id+"F0.wireOp",EDGE,"E0")}),1.0]])]});
            var Q1;
            Q1=makeQuery(id+"F0.imprint","IMPRINT",FACE,{"disambiguationData":[TD([[makeQuery(id+"F0.imprint","IMPRINT",EDGE,{"derivedFrom":sQuery(id+"F0.wireOp",EDGE,"E136")}),1.0]])]});
            extrude(context, id + "F1", {"entities" : qUnion([Q0, Q1]), "oppositeDirection" : true, "depth" : 2.5 * mm});
        }
        {
            var Q0;
            Q0=qCreatedBy(makeId("Top.planeOp"),FACE);
            var sketch = newSketch(context, id + "F2", { "sketchPlane" : qUnion([Q0])});
            skLineSegment(sketch, "E4015.top", {"start": v(0, 0) * mm, "end": v(800, 0) * mm});
            skLineSegment(sketch, "E4015.right", {"start": v(800, 200) * mm, "end": v(800, 0) * mm});
            skLineSegment(sketch, "E4016", {"start": v(0, 124.86) * mm, "end": v(0, -124.86) * mm, "construction": true});
            skLineSegment(sketch, "E4017", {"start": v(-355.85, 0) * mm, "end": v(355.85, 0) * mm, "construction": true});
            skLineSegment(sketch, "E4018.bottom", {"start": v(-156.51, 23.46) * mm, "end": v(-151.51, 23.46) * mm});
            skLineSegment(sketch, "E4018.top", {"start": v(-156.51, 36.51) * mm, "end": v(-151.51, 36.51) * mm});
            skLineSegment(sketch, "E4018.left", {"start": v(-156.51, 23.46) * mm, "end": v(-156.51, 36.51) * mm});
            skLineSegment(sketch, "E4018.right", {"start": v(-151.51, 23.46) * mm, "end": v(-151.51, 36.51) * mm});
            skLineSegment(sketch, "E4019.bottom", {"start": v(-121.51, -36.51) * mm, "end": v(-116.51, -36.51) * mm});
            skLineSegment(sketch, "E4019.top", {"start": v(-121.51, -23.48) * mm, "end": v(-116.51, -23.48) * mm});
            skLineSegment(sketch, "E4019.left", {"start": v(-121.51, -36.51) * mm, "end": v(-121.51, -23.48) * mm});
            skLineSegment(sketch, "E4019.right", {"start": v(-116.51, -36.51) * mm, "end": v(-116.51, -23.48) * mm});
            skLineSegment(sketch, "E4020.bottom", {"start": v(106.51, -36.51) * mm, "end": v(111.51, -36.51) * mm});
            skLineSegment(sketch, "E4020.top", {"start": v(106.51, -23.48) * mm, "end": v(111.51, -23.48) * mm});
            skLineSegment(sketch, "E4020.left", {"start": v(106.51, -36.51) * mm, "end": v(106.51, -23.48) * mm});
            skLineSegment(sketch, "E4020.right", {"start": v(111.51, -36.51) * mm, "end": v(111.51, -23.48) * mm});
            skLineSegment(sketch, "E4021.bottom", {"start": v(-2.51, 23.46) * mm, "end": v(2.49, 23.46) * mm});
            skLineSegment(sketch, "E4021.top", {"start": v(-2.51, 36.51) * mm, "end": v(2.49, 36.51) * mm});
            skLineSegment(sketch, "E4021.left", {"start": v(-2.51, 23.46) * mm, "end": v(-2.51, 36.51) * mm});
            skLineSegment(sketch, "E4021.right", {"start": v(2.49, 23.46) * mm, "end": v(2.49, 36.51) * mm});
            skLineSegment(sketch, "E4022.bottom", {"start": v(151.51, 23.46) * mm, "end": v(156.51, 23.46) * mm});
            skLineSegment(sketch, "E4022.top", {"start": v(151.51, 36.51) * mm, "end": v(156.51, 36.51) * mm});
            skLineSegment(sketch, "E4022.left", {"start": v(151.51, 23.46) * mm, "end": v(151.51, 36.51) * mm});
            skLineSegment(sketch, "E4022.right", {"start": v(156.51, 23.46) * mm, "end": v(156.51, 36.51) * mm});
            skLineSegment(sketch, "E4023.bottom", {"start": v(-216.51, -2.53) * mm, "end": v(-198.49, -2.53) * mm});
            skLineSegment(sketch, "E4023.top", {"start": v(-216.51, 2.47) * mm, "end": v(-198.49, 2.47) * mm});
            skLineSegment(sketch, "E4023.left", {"start": v(-216.51, -2.53) * mm, "end": v(-216.51, 2.47) * mm});
            skLineSegment(sketch, "E4023.right", {"start": v(-198.49, -2.53) * mm, "end": v(-198.49, 2.47) * mm});
            skLineSegment(sketch, "E4024.bottom", {"start": v(198.49, -2.53) * mm, "end": v(216.51, -2.53) * mm});
            skLineSegment(sketch, "E4024.top", {"start": v(198.49, 2.47) * mm, "end": v(216.51, 2.47) * mm});
            skLineSegment(sketch, "E4024.left", {"start": v(198.49, -2.53) * mm, "end": v(198.49, 2.47) * mm});
            skLineSegment(sketch, "E4024.right", {"start": v(216.51, -2.53) * mm, "end": v(216.51, 2.47) * mm});
            skSolve(sketch);
        }
        {
            var Q0;
            Q0 = qSketchRegion(id + "F2", true);
            extrude(context, id + "F3", {"entities" : qUnion([Q0]), "depth" : 12.5 * mm});
        }
    });
